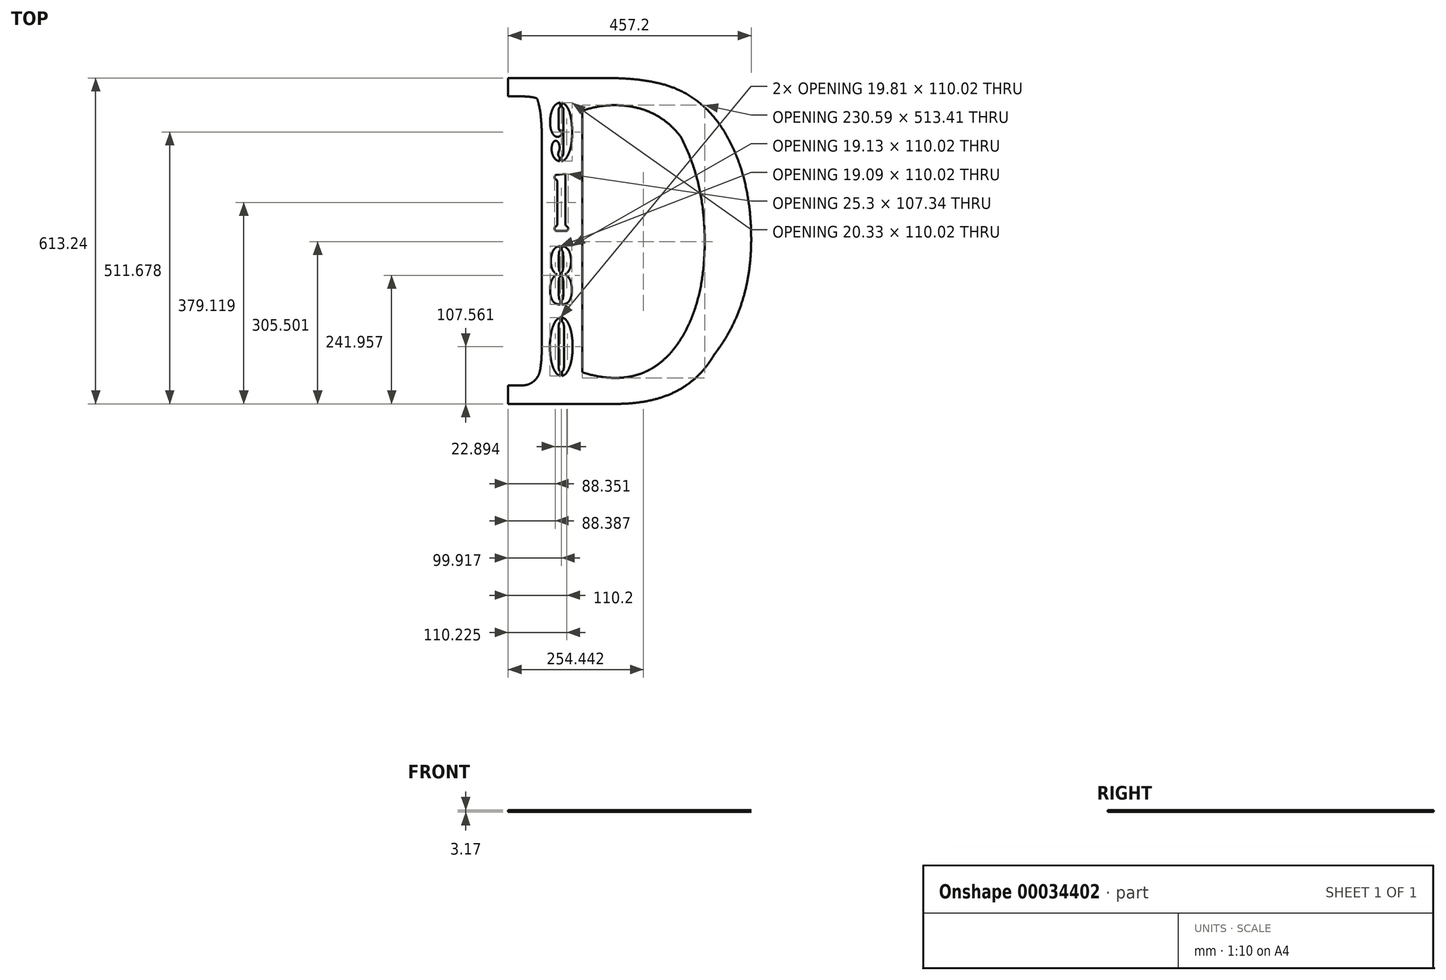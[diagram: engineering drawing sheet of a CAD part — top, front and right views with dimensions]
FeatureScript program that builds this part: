
annotation { "Feature Type Name" : "Feature", "Feature Type Description" : "" }
export const myFeature = defineFeature(function(context is Context, id is Id, definition is map)
    precondition{}
    {
        {
            var Q0;
            Q0=qCreatedBy(makeId("Top.planeOp"),FACE);
            var sketch = newSketch(context, id + "F0", { "sketchPlane" : qUnion([Q0])});
            skLineSegment(sketch, "E0", {"start": v(26.6, 0.36) * mm, "end": v(26.6, 0.12) * mm});
            skLineSegment(sketch, "E1", {"start": v(26.6, 0.12) * mm, "end": v(26.6, -0.1) * mm});
            skLineSegment(sketch, "E2", {"start": v(26.6, -0.1) * mm, "end": v(26.6, -0.34) * mm});
            skLineSegment(sketch, "E3", {"start": v(26.6, -0.34) * mm, "end": v(26.6, -0.57) * mm});
            skLineSegment(sketch, "E4", {"start": v(26.6, -0.57) * mm, "end": v(26.6, -0.8) * mm});
            skLineSegment(sketch, "E5", {"start": v(26.6, -0.8) * mm, "end": v(26.58, -1.03) * mm});
            skLineSegment(sketch, "E6", {"start": v(26.58, -1.03) * mm, "end": v(26.58, -1.26) * mm});
            skLineSegment(sketch, "E7", {"start": v(26.58, -1.26) * mm, "end": v(26.57, -1.49) * mm});
            skLineSegment(sketch, "E8", {"start": v(26.57, -1.49) * mm, "end": v(26.56, -1.72) * mm});
            skLineSegment(sketch, "E9", {"start": v(26.56, -1.72) * mm, "end": v(26.55, -1.94) * mm});
            skLineSegment(sketch, "E10", {"start": v(26.55, -1.94) * mm, "end": v(26.54, -2.17) * mm});
            skLineSegment(sketch, "E11", {"start": v(26.54, -2.17) * mm, "end": v(26.53, -2.4) * mm});
            skLineSegment(sketch, "E12", {"start": v(26.53, -2.4) * mm, "end": v(26.52, -2.62) * mm});
            skLineSegment(sketch, "E13", {"start": v(26.52, -2.62) * mm, "end": v(26.5, -2.85) * mm});
            skLineSegment(sketch, "E14", {"start": v(26.5, -2.85) * mm, "end": v(26.5, -3.07) * mm});
            skLineSegment(sketch, "E15", {"start": v(26.5, -3.07) * mm, "end": v(26.48, -3.3) * mm});
            skLineSegment(sketch, "E16", {"start": v(26.48, -3.3) * mm, "end": v(26.46, -3.52) * mm});
            skLineSegment(sketch, "E17", {"start": v(26.46, -3.52) * mm, "end": v(26.44, -3.74) * mm});
            skLineSegment(sketch, "E18", {"start": v(26.44, -3.74) * mm, "end": v(26.42, -3.97) * mm});
            skLineSegment(sketch, "E19", {"start": v(26.42, -3.97) * mm, "end": v(26.4, -4.19) * mm});
            skLineSegment(sketch, "E20", {"start": v(26.4, -4.19) * mm, "end": v(26.39, -4.4) * mm});
            skLineSegment(sketch, "E21", {"start": v(26.39, -4.4) * mm, "end": v(26.36, -4.63) * mm});
            skLineSegment(sketch, "E22", {"start": v(26.36, -4.63) * mm, "end": v(26.34, -4.85) * mm});
            skLineSegment(sketch, "E23", {"start": v(26.34, -4.85) * mm, "end": v(26.32, -5.07) * mm});
            skLineSegment(sketch, "E24", {"start": v(26.32, -5.07) * mm, "end": v(26.3, -5.29) * mm});
            skLineSegment(sketch, "E25", {"start": v(26.3, -5.29) * mm, "end": v(26.27, -5.5) * mm});
            skLineSegment(sketch, "E26", {"start": v(26.27, -5.5) * mm, "end": v(26.24, -5.73) * mm});
            skLineSegment(sketch, "E27", {"start": v(26.24, -5.73) * mm, "end": v(26.22, -5.94) * mm});
            skLineSegment(sketch, "E28", {"start": v(26.22, -5.94) * mm, "end": v(26.19, -6.16) * mm});
            skLineSegment(sketch, "E29", {"start": v(26.19, -6.16) * mm, "end": v(26.16, -6.38) * mm});
            skLineSegment(sketch, "E30", {"start": v(26.16, -6.38) * mm, "end": v(26.13, -6.6) * mm});
            skLineSegment(sketch, "E31", {"start": v(26.13, -6.6) * mm, "end": v(26.1, -6.8) * mm});
            skLineSegment(sketch, "E32", {"start": v(26.1, -6.8) * mm, "end": v(26.07, -7.02) * mm});
            skLineSegment(sketch, "E33", {"start": v(26.07, -7.02) * mm, "end": v(26.03, -7.24) * mm});
            skLineSegment(sketch, "E34", {"start": v(26.03, -7.24) * mm, "end": v(26, -7.45) * mm});
            skLineSegment(sketch, "E35", {"start": v(26, -7.45) * mm, "end": v(25.96, -7.66) * mm});
            skLineSegment(sketch, "E36", {"start": v(25.96, -7.66) * mm, "end": v(25.93, -7.88) * mm});
            skLineSegment(sketch, "E37", {"start": v(25.93, -7.88) * mm, "end": v(25.9, -8.09) * mm});
            skLineSegment(sketch, "E38", {"start": v(25.9, -8.09) * mm, "end": v(25.85, -8.3) * mm});
            skLineSegment(sketch, "E39", {"start": v(25.85, -8.3) * mm, "end": v(25.81, -8.5) * mm});
            skLineSegment(sketch, "E40", {"start": v(25.81, -8.5) * mm, "end": v(25.77, -8.72) * mm});
            skLineSegment(sketch, "E41", {"start": v(25.77, -8.72) * mm, "end": v(25.73, -8.93) * mm});
            skLineSegment(sketch, "E42", {"start": v(25.73, -8.93) * mm, "end": v(25.7, -9.14) * mm});
            skLineSegment(sketch, "E43", {"start": v(25.7, -9.14) * mm, "end": v(25.65, -9.35) * mm});
            skLineSegment(sketch, "E44", {"start": v(25.65, -9.35) * mm, "end": v(25.6, -9.55) * mm});
            skLineSegment(sketch, "E45", {"start": v(25.6, -9.55) * mm, "end": v(25.56, -9.76) * mm});
            skLineSegment(sketch, "E46", {"start": v(25.56, -9.76) * mm, "end": v(25.51, -9.97) * mm});
            skLineSegment(sketch, "E47", {"start": v(25.51, -9.97) * mm, "end": v(25.47, -10.17) * mm});
            skLineSegment(sketch, "E48", {"start": v(25.47, -10.17) * mm, "end": v(25.42, -10.38) * mm});
            skLineSegment(sketch, "E49", {"start": v(25.42, -10.38) * mm, "end": v(25.37, -10.59) * mm});
            skLineSegment(sketch, "E50", {"start": v(25.37, -10.59) * mm, "end": v(25.32, -10.79) * mm});
            skLineSegment(sketch, "E51", {"start": v(25.32, -10.79) * mm, "end": v(25.27, -11) * mm});
            skLineSegment(sketch, "E52", {"start": v(25.27, -11) * mm, "end": v(25.22, -11.2) * mm});
            skLineSegment(sketch, "E53", {"start": v(25.22, -11.2) * mm, "end": v(25.16, -11.4) * mm});
            skLineSegment(sketch, "E54", {"start": v(25.16, -11.4) * mm, "end": v(25.11, -11.6) * mm});
            skLineSegment(sketch, "E55", {"start": v(25.11, -11.6) * mm, "end": v(25.06, -11.8) * mm});
            skLineSegment(sketch, "E56", {"start": v(25.06, -11.8) * mm, "end": v(25, -12) * mm});
            skLineSegment(sketch, "E57", {"start": v(25, -12) * mm, "end": v(24.94, -12.2) * mm});
            skLineSegment(sketch, "E58", {"start": v(24.94, -12.2) * mm, "end": v(24.89, -12.4) * mm});
            skLineSegment(sketch, "E59", {"start": v(24.89, -12.4) * mm, "end": v(24.83, -12.6) * mm});
            skLineSegment(sketch, "E60", {"start": v(24.83, -12.6) * mm, "end": v(24.77, -12.8) * mm});
            skLineSegment(sketch, "E61", {"start": v(24.77, -12.8) * mm, "end": v(24.7, -13) * mm});
            skLineSegment(sketch, "E62", {"start": v(24.7, -13) * mm, "end": v(24.64, -13.2) * mm});
            skLineSegment(sketch, "E63", {"start": v(24.64, -13.2) * mm, "end": v(24.58, -13.4) * mm});
            skLineSegment(sketch, "E64", {"start": v(24.58, -13.4) * mm, "end": v(24.52, -13.6) * mm});
            skLineSegment(sketch, "E65", {"start": v(24.52, -13.6) * mm, "end": v(24.45, -13.8) * mm});
            skLineSegment(sketch, "E66", {"start": v(24.45, -13.8) * mm, "end": v(24.39, -13.99) * mm});
            skLineSegment(sketch, "E67", {"start": v(24.39, -13.99) * mm, "end": v(24.32, -14.18) * mm});
            skLineSegment(sketch, "E68", {"start": v(24.32, -14.18) * mm, "end": v(24.25, -14.38) * mm});
            skLineSegment(sketch, "E69", {"start": v(24.25, -14.38) * mm, "end": v(24.19, -14.57) * mm});
            skLineSegment(sketch, "E70", {"start": v(24.19, -14.57) * mm, "end": v(24.12, -14.76) * mm});
            skLineSegment(sketch, "E71", {"start": v(24.12, -14.76) * mm, "end": v(24.05, -14.95) * mm});
            skLineSegment(sketch, "E72", {"start": v(24.05, -14.95) * mm, "end": v(23.97, -15.15) * mm});
            skLineSegment(sketch, "E73", {"start": v(23.97, -15.15) * mm, "end": v(23.9, -15.34) * mm});
            skLineSegment(sketch, "E74", {"start": v(23.9, -15.34) * mm, "end": v(23.83, -15.53) * mm});
            skLineSegment(sketch, "E75", {"start": v(23.83, -15.53) * mm, "end": v(23.75, -15.72) * mm});
            skLineSegment(sketch, "E76", {"start": v(23.75, -15.72) * mm, "end": v(23.68, -15.91) * mm});
            skLineSegment(sketch, "E77", {"start": v(23.68, -15.91) * mm, "end": v(23.6, -16.1) * mm});
            skLineSegment(sketch, "E78", {"start": v(23.6, -16.1) * mm, "end": v(23.52, -16.29) * mm});
            skLineSegment(sketch, "E79", {"start": v(23.52, -16.29) * mm, "end": v(23.45, -16.48) * mm});
            skLineSegment(sketch, "E80", {"start": v(23.45, -16.48) * mm, "end": v(23.37, -16.66) * mm});
            skLineSegment(sketch, "E81", {"start": v(23.37, -16.66) * mm, "end": v(23.29, -16.85) * mm});
            skLineSegment(sketch, "E82", {"start": v(23.29, -16.85) * mm, "end": v(23.2, -17.04) * mm});
            skLineSegment(sketch, "E83", {"start": v(23.2, -17.04) * mm, "end": v(23.12, -17.22) * mm});
            skLineSegment(sketch, "E84", {"start": v(23.12, -17.22) * mm, "end": v(23.04, -17.4) * mm});
            skLineSegment(sketch, "E85", {"start": v(23.04, -17.4) * mm, "end": v(22.95, -17.6) * mm});
            skLineSegment(sketch, "E86", {"start": v(22.95, -17.6) * mm, "end": v(22.87, -17.78) * mm});
            skLineSegment(sketch, "E87", {"start": v(22.87, -17.78) * mm, "end": v(22.78, -17.96) * mm});
            skLineSegment(sketch, "E88", {"start": v(22.78, -17.96) * mm, "end": v(22.7, -18.15) * mm});
            skLineSegment(sketch, "E89", {"start": v(22.7, -18.15) * mm, "end": v(22.6, -18.33) * mm});
            skLineSegment(sketch, "E90", {"start": v(22.6, -18.33) * mm, "end": v(22.52, -18.5) * mm});
            skLineSegment(sketch, "E91", {"start": v(22.52, -18.5) * mm, "end": v(22.43, -18.7) * mm});
            skLineSegment(sketch, "E92", {"start": v(22.43, -18.7) * mm, "end": v(22.34, -18.87) * mm});
            skLineSegment(sketch, "E93", {"start": v(22.34, -18.87) * mm, "end": v(22.24, -19.05) * mm});
            skLineSegment(sketch, "E94", {"start": v(22.24, -19.05) * mm, "end": v(22.15, -19.23) * mm});
            skLineSegment(sketch, "E95", {"start": v(22.15, -19.23) * mm, "end": v(22.06, -19.41) * mm});
            skLineSegment(sketch, "E96", {"start": v(22.06, -19.41) * mm, "end": v(21.96, -19.6) * mm});
            skLineSegment(sketch, "E97", {"start": v(21.96, -19.6) * mm, "end": v(21.87, -19.77) * mm});
            skLineSegment(sketch, "E98", {"start": v(21.87, -19.77) * mm, "end": v(21.77, -19.95) * mm});
            skLineSegment(sketch, "E99", {"start": v(21.77, -19.95) * mm, "end": v(21.67, -20.12) * mm});
            skLineSegment(sketch, "E100", {"start": v(21.67, -20.12) * mm, "end": v(21.57, -20.3) * mm});
            skLineSegment(sketch, "E101", {"start": v(21.57, -20.3) * mm, "end": v(21.47, -20.48) * mm});
            skLineSegment(sketch, "E102", {"start": v(21.47, -20.48) * mm, "end": v(21.37, -20.65) * mm});
            skLineSegment(sketch, "E103", {"start": v(21.37, -20.65) * mm, "end": v(21.27, -20.83) * mm});
            skLineSegment(sketch, "E104", {"start": v(21.27, -20.83) * mm, "end": v(21.16, -21) * mm});
            skLineSegment(sketch, "E105", {"start": v(21.16, -21) * mm, "end": v(21.06, -21.17) * mm});
            skLineSegment(sketch, "E106", {"start": v(21.06, -21.17) * mm, "end": v(20.96, -21.35) * mm});
            skLineSegment(sketch, "E107", {"start": v(20.96, -21.35) * mm, "end": v(20.85, -21.52) * mm});
            skLineSegment(sketch, "E108", {"start": v(20.85, -21.52) * mm, "end": v(20.74, -21.7) * mm});
            skLineSegment(sketch, "E109", {"start": v(20.74, -21.7) * mm, "end": v(20.63, -21.86) * mm});
            skLineSegment(sketch, "E110", {"start": v(20.63, -21.86) * mm, "end": v(20.53, -22.03) * mm});
            skLineSegment(sketch, "E111", {"start": v(20.53, -22.03) * mm, "end": v(20.42, -22.2) * mm});
            skLineSegment(sketch, "E112", {"start": v(20.42, -22.2) * mm, "end": v(20.3, -22.37) * mm});
            skLineSegment(sketch, "E113", {"start": v(20.3, -22.37) * mm, "end": v(20.2, -22.54) * mm});
            skLineSegment(sketch, "E114", {"start": v(16.38, -27.97) * mm, "end": v(16.27, -28.11) * mm});
            skLineSegment(sketch, "E115", {"start": v(16.27, -28.11) * mm, "end": v(16.15, -28.25) * mm});
            skLineSegment(sketch, "E116", {"start": v(16.15, -28.25) * mm, "end": v(16.03, -28.4) * mm});
            skLineSegment(sketch, "E117", {"start": v(16.03, -28.4) * mm, "end": v(15.9, -28.53) * mm});
            skLineSegment(sketch, "E118", {"start": v(15.9, -28.53) * mm, "end": v(15.78, -28.67) * mm});
            skLineSegment(sketch, "E119", {"start": v(15.78, -28.67) * mm, "end": v(15.66, -28.8) * mm});
            skLineSegment(sketch, "E120", {"start": v(15.66, -28.8) * mm, "end": v(15.53, -28.94) * mm});
            skLineSegment(sketch, "E121", {"start": v(15.53, -28.94) * mm, "end": v(15.4, -29.07) * mm});
            skLineSegment(sketch, "E122", {"start": v(15.4, -29.07) * mm, "end": v(15.28, -29.2) * mm});
            skLineSegment(sketch, "E123", {"start": v(15.28, -29.2) * mm, "end": v(15.15, -29.33) * mm});
            skLineSegment(sketch, "E124", {"start": v(15.15, -29.33) * mm, "end": v(15.02, -29.46) * mm});
            skLineSegment(sketch, "E125", {"start": v(15.02, -29.46) * mm, "end": v(14.89, -29.59) * mm});
            skLineSegment(sketch, "E126", {"start": v(14.89, -29.59) * mm, "end": v(14.75, -29.71) * mm});
            skLineSegment(sketch, "E127", {"start": v(14.75, -29.71) * mm, "end": v(14.62, -29.84) * mm});
            skLineSegment(sketch, "E128", {"start": v(14.62, -29.84) * mm, "end": v(14.49, -29.96) * mm});
            skLineSegment(sketch, "E129", {"start": v(14.49, -29.96) * mm, "end": v(14.35, -30.09) * mm});
            skLineSegment(sketch, "E130", {"start": v(14.35, -30.09) * mm, "end": v(14.21, -30.2) * mm});
            skLineSegment(sketch, "E131", {"start": v(14.21, -30.2) * mm, "end": v(14.08, -30.33) * mm});
            skLineSegment(sketch, "E132", {"start": v(14.08, -30.33) * mm, "end": v(13.94, -30.44) * mm});
            skLineSegment(sketch, "E133", {"start": v(13.94, -30.44) * mm, "end": v(13.8, -30.56) * mm});
            skLineSegment(sketch, "E134", {"start": v(13.8, -30.56) * mm, "end": v(13.66, -30.68) * mm});
            skLineSegment(sketch, "E135", {"start": v(13.66, -30.68) * mm, "end": v(13.51, -30.8) * mm});
            skLineSegment(sketch, "E136", {"start": v(13.51, -30.8) * mm, "end": v(13.37, -30.9) * mm});
            skLineSegment(sketch, "E137", {"start": v(13.37, -30.9) * mm, "end": v(13.23, -31.02) * mm});
            skLineSegment(sketch, "E138", {"start": v(13.23, -31.02) * mm, "end": v(13.08, -31.13) * mm});
            skLineSegment(sketch, "E139", {"start": v(13.08, -31.13) * mm, "end": v(12.93, -31.24) * mm});
            skLineSegment(sketch, "E140", {"start": v(12.93, -31.24) * mm, "end": v(12.79, -31.34) * mm});
            skLineSegment(sketch, "E141", {"start": v(12.79, -31.34) * mm, "end": v(12.64, -31.45) * mm});
            skLineSegment(sketch, "E142", {"start": v(12.64, -31.45) * mm, "end": v(12.49, -31.56) * mm});
            skLineSegment(sketch, "E143", {"start": v(12.49, -31.56) * mm, "end": v(12.34, -31.66) * mm});
            skLineSegment(sketch, "E144", {"start": v(12.34, -31.66) * mm, "end": v(12.18, -31.76) * mm});
            skLineSegment(sketch, "E145", {"start": v(12.18, -31.76) * mm, "end": v(12.03, -31.86) * mm});
            skLineSegment(sketch, "E146", {"start": v(12.03, -31.86) * mm, "end": v(11.87, -31.96) * mm});
            skLineSegment(sketch, "E147", {"start": v(11.87, -31.96) * mm, "end": v(11.72, -32.06) * mm});
            skLineSegment(sketch, "E148", {"start": v(11.72, -32.06) * mm, "end": v(11.56, -32.16) * mm});
            skLineSegment(sketch, "E149", {"start": v(11.56, -32.16) * mm, "end": v(11.4, -32.25) * mm});
            skLineSegment(sketch, "E150", {"start": v(11.4, -32.25) * mm, "end": v(11.24, -32.35) * mm});
            skLineSegment(sketch, "E151", {"start": v(11.24, -32.35) * mm, "end": v(11.08, -32.44) * mm});
            skLineSegment(sketch, "E152", {"start": v(11.08, -32.44) * mm, "end": v(10.92, -32.53) * mm});
            skLineSegment(sketch, "E153", {"start": v(10.92, -32.53) * mm, "end": v(10.76, -32.62) * mm});
            skLineSegment(sketch, "E154", {"start": v(10.76, -32.62) * mm, "end": v(10.6, -32.71) * mm});
            skLineSegment(sketch, "E155", {"start": v(10.6, -32.71) * mm, "end": v(10.43, -32.8) * mm});
            skLineSegment(sketch, "E156", {"start": v(10.43, -32.8) * mm, "end": v(10.27, -32.89) * mm});
            skLineSegment(sketch, "E157", {"start": v(10.27, -32.89) * mm, "end": v(10.1, -32.97) * mm});
            skLineSegment(sketch, "E158", {"start": v(10.1, -32.97) * mm, "end": v(9.93, -33.06) * mm});
            skLineSegment(sketch, "E159", {"start": v(9.93, -33.06) * mm, "end": v(9.76, -33.14) * mm});
            skLineSegment(sketch, "E160", {"start": v(9.76, -33.14) * mm, "end": v(9.6, -33.22) * mm});
            skLineSegment(sketch, "E161", {"start": v(9.6, -33.22) * mm, "end": v(9.42, -33.3) * mm});
            skLineSegment(sketch, "E162", {"start": v(9.42, -33.3) * mm, "end": v(9.25, -33.38) * mm});
            skLineSegment(sketch, "E163", {"start": v(9.25, -33.38) * mm, "end": v(9.07, -33.46) * mm});
            skLineSegment(sketch, "E164", {"start": v(9.07, -33.46) * mm, "end": v(8.9, -33.53) * mm});
            skLineSegment(sketch, "E165", {"start": v(8.9, -33.53) * mm, "end": v(8.72, -33.6) * mm});
            skLineSegment(sketch, "E166", {"start": v(8.72, -33.6) * mm, "end": v(8.55, -33.68) * mm});
            skLineSegment(sketch, "E167", {"start": v(8.55, -33.68) * mm, "end": v(8.37, -33.75) * mm});
            skLineSegment(sketch, "E168", {"start": v(8.37, -33.75) * mm, "end": v(8.19, -33.82) * mm});
            skLineSegment(sketch, "E169", {"start": v(8.19, -33.82) * mm, "end": v(8, -33.9) * mm});
            skLineSegment(sketch, "E170", {"start": v(8, -33.9) * mm, "end": v(7.83, -33.96) * mm});
            skLineSegment(sketch, "E171", {"start": v(7.83, -33.96) * mm, "end": v(7.64, -34.03) * mm});
            skLineSegment(sketch, "E172", {"start": v(7.64, -34.03) * mm, "end": v(7.46, -34.1) * mm});
            skLineSegment(sketch, "E173", {"start": v(7.46, -34.1) * mm, "end": v(7.27, -34.16) * mm});
            skLineSegment(sketch, "E174", {"start": v(7.27, -34.16) * mm, "end": v(7.09, -34.22) * mm});
            skLineSegment(sketch, "E175", {"start": v(7.09, -34.22) * mm, "end": v(6.9, -34.28) * mm});
            skLineSegment(sketch, "E176", {"start": v(6.9, -34.28) * mm, "end": v(6.71, -34.34) * mm});
            skLineSegment(sketch, "E177", {"start": v(6.71, -34.34) * mm, "end": v(6.52, -34.4) * mm});
            skLineSegment(sketch, "E178", {"start": v(6.52, -34.4) * mm, "end": v(6.33, -34.46) * mm});
            skLineSegment(sketch, "E179", {"start": v(6.33, -34.46) * mm, "end": v(6.14, -34.52) * mm});
            skLineSegment(sketch, "E180", {"start": v(6.14, -34.52) * mm, "end": v(5.95, -34.57) * mm});
            skLineSegment(sketch, "E181", {"start": v(5.95, -34.57) * mm, "end": v(5.75, -34.62) * mm});
            skLineSegment(sketch, "E182", {"start": v(5.75, -34.62) * mm, "end": v(5.56, -34.68) * mm});
            skLineSegment(sketch, "E183", {"start": v(5.56, -34.68) * mm, "end": v(5.36, -34.73) * mm});
            skLineSegment(sketch, "E184", {"start": v(5.36, -34.73) * mm, "end": v(5.16, -34.78) * mm});
            skLineSegment(sketch, "E185", {"start": v(5.16, -34.78) * mm, "end": v(4.97, -34.82) * mm});
            skLineSegment(sketch, "E186", {"start": v(4.97, -34.82) * mm, "end": v(4.77, -34.87) * mm});
            skLineSegment(sketch, "E187", {"start": v(4.77, -34.87) * mm, "end": v(4.57, -34.92) * mm});
            skLineSegment(sketch, "E188", {"start": v(4.57, -34.92) * mm, "end": v(4.36, -34.96) * mm});
            skLineSegment(sketch, "E189", {"start": v(4.36, -34.96) * mm, "end": v(4.16, -35) * mm});
            skLineSegment(sketch, "E190", {"start": v(4.16, -35) * mm, "end": v(3.96, -35.05) * mm});
            skLineSegment(sketch, "E191", {"start": v(3.96, -35.05) * mm, "end": v(3.75, -35.09) * mm});
            skLineSegment(sketch, "E192", {"start": v(3.75, -35.09) * mm, "end": v(3.54, -35.13) * mm});
            skLineSegment(sketch, "E193", {"start": v(3.54, -35.13) * mm, "end": v(3.34, -35.16) * mm});
            skLineSegment(sketch, "E194", {"start": v(3.34, -35.16) * mm, "end": v(3.13, -35.2) * mm});
            skLineSegment(sketch, "E195", {"start": v(3.13, -35.2) * mm, "end": v(2.92, -35.23) * mm});
            skLineSegment(sketch, "E196", {"start": v(2.92, -35.23) * mm, "end": v(2.7, -35.27) * mm});
            skLineSegment(sketch, "E197", {"start": v(2.7, -35.27) * mm, "end": v(2.5, -35.3) * mm});
            skLineSegment(sketch, "E198", {"start": v(2.5, -35.3) * mm, "end": v(2.28, -35.33) * mm});
            skLineSegment(sketch, "E199", {"start": v(2.28, -35.33) * mm, "end": v(2.07, -35.36) * mm});
            skLineSegment(sketch, "E200", {"start": v(2.07, -35.36) * mm, "end": v(1.85, -35.39) * mm});
            skLineSegment(sketch, "E201", {"start": v(1.85, -35.39) * mm, "end": v(1.64, -35.42) * mm});
            skLineSegment(sketch, "E202", {"start": v(1.64, -35.42) * mm, "end": v(1.42, -35.44) * mm});
            skLineSegment(sketch, "E203", {"start": v(1.42, -35.44) * mm, "end": v(1.2, -35.47) * mm});
            skLineSegment(sketch, "E204", {"start": v(1.2, -35.47) * mm, "end": v(0.98, -35.5) * mm});
            skLineSegment(sketch, "E205", {"start": v(0.98, -35.5) * mm, "end": v(0.76, -35.51) * mm});
            skLineSegment(sketch, "E206", {"start": v(0.76, -35.51) * mm, "end": v(0.54, -35.53) * mm});
            skLineSegment(sketch, "E207", {"start": v(0.54, -35.53) * mm, "end": v(0.31, -35.55) * mm});
            skLineSegment(sketch, "E208", {"start": v(0.31, -35.55) * mm, "end": v(0.09, -35.57) * mm});
            skLineSegment(sketch, "E209", {"start": v(0.09, -35.57) * mm, "end": v(-0.14, -35.59) * mm});
            skLineSegment(sketch, "E210", {"start": v(-0.14, -35.59) * mm, "end": v(-0.36, -35.6) * mm});
            skLineSegment(sketch, "E211", {"start": v(-0.36, -35.6) * mm, "end": v(-0.6, -35.62) * mm});
            skLineSegment(sketch, "E212", {"start": v(-0.6, -35.62) * mm, "end": v(-0.82, -35.63) * mm});
            skLineSegment(sketch, "E213", {"start": v(-0.82, -35.63) * mm, "end": v(-1.05, -35.64) * mm});
            skLineSegment(sketch, "E214", {"start": v(-1.05, -35.64) * mm, "end": v(-1.28, -35.65) * mm});
            skLineSegment(sketch, "E215", {"start": v(-1.28, -35.65) * mm, "end": v(-1.51, -35.66) * mm});
            skLineSegment(sketch, "E216", {"start": v(-1.51, -35.66) * mm, "end": v(-1.75, -35.66) * mm});
            skLineSegment(sketch, "E217", {"start": v(-1.75, -35.66) * mm, "end": v(-1.98, -35.67) * mm});
            skLineSegment(sketch, "E218", {"start": v(-1.98, -35.67) * mm, "end": v(-2.22, -35.68) * mm});
            skLineSegment(sketch, "E219", {"start": v(-2.22, -35.68) * mm, "end": v(-2.45, -35.68) * mm});
            skLineSegment(sketch, "E220", {"start": v(-2.45, -35.68) * mm, "end": v(-2.7, -35.68) * mm});
            skLineSegment(sketch, "E221", {"start": v(-2.7, -35.68) * mm, "end": v(-2.93, -35.68) * mm});
            skLineSegment(sketch, "E222", {"start": v(-2.93, -35.68) * mm, "end": v(-26.6, -35.68) * mm});
            skLineSegment(sketch, "E223", {"start": v(-26.6, -35.68) * mm, "end": v(-26.6, -31.67) * mm});
            skLineSegment(sketch, "E224", {"start": v(-26.6, -31.67) * mm, "end": v(-23.9, -31.67) * mm});
            skLineSegment(sketch, "E225", {"start": v(-23.9, -31.67) * mm, "end": v(-23.82, -31.67) * mm});
            skLineSegment(sketch, "E226", {"start": v(-23.82, -31.67) * mm, "end": v(-23.73, -31.67) * mm});
            skLineSegment(sketch, "E227", {"start": v(-23.73, -31.67) * mm, "end": v(-23.64, -31.67) * mm});
            skLineSegment(sketch, "E228", {"start": v(-23.64, -31.67) * mm, "end": v(-23.56, -31.66) * mm});
            skLineSegment(sketch, "E229", {"start": v(-23.56, -31.66) * mm, "end": v(-23.47, -31.66) * mm});
            skLineSegment(sketch, "E230", {"start": v(-23.47, -31.66) * mm, "end": v(-23.4, -31.65) * mm});
            skLineSegment(sketch, "E231", {"start": v(-23.4, -31.65) * mm, "end": v(-23.3, -31.64) * mm});
            skLineSegment(sketch, "E232", {"start": v(-23.3, -31.64) * mm, "end": v(-23.23, -31.63) * mm});
            skLineSegment(sketch, "E233", {"start": v(-23.23, -31.63) * mm, "end": v(-23.14, -31.62) * mm});
            skLineSegment(sketch, "E234", {"start": v(-23.14, -31.62) * mm, "end": v(-23.06, -31.61) * mm});
            skLineSegment(sketch, "E235", {"start": v(-23.06, -31.61) * mm, "end": v(-22.98, -31.6) * mm});
            skLineSegment(sketch, "E236", {"start": v(-22.98, -31.6) * mm, "end": v(-22.9, -31.59) * mm});
            skLineSegment(sketch, "E237", {"start": v(-22.9, -31.59) * mm, "end": v(-22.83, -31.57) * mm});
            skLineSegment(sketch, "E238", {"start": v(-22.83, -31.57) * mm, "end": v(-22.75, -31.56) * mm});
            skLineSegment(sketch, "E239", {"start": v(-22.75, -31.56) * mm, "end": v(-22.67, -31.54) * mm});
            skLineSegment(sketch, "E240", {"start": v(-22.67, -31.54) * mm, "end": v(-22.6, -31.52) * mm});
            skLineSegment(sketch, "E241", {"start": v(-22.6, -31.52) * mm, "end": v(-22.52, -31.5) * mm});
            skLineSegment(sketch, "E242", {"start": v(-22.52, -31.5) * mm, "end": v(-22.45, -31.49) * mm});
            skLineSegment(sketch, "E243", {"start": v(-22.45, -31.49) * mm, "end": v(-22.38, -31.46) * mm});
            skLineSegment(sketch, "E244", {"start": v(-22.38, -31.46) * mm, "end": v(-22.3, -31.44) * mm});
            skLineSegment(sketch, "E245", {"start": v(-22.3, -31.44) * mm, "end": v(-22.23, -31.42) * mm});
            skLineSegment(sketch, "E246", {"start": v(-22.23, -31.42) * mm, "end": v(-22.16, -31.4) * mm});
            skLineSegment(sketch, "E247", {"start": v(-22.16, -31.4) * mm, "end": v(-22.1, -31.37) * mm});
            skLineSegment(sketch, "E248", {"start": v(-22.1, -31.37) * mm, "end": v(-22.02, -31.34) * mm});
            skLineSegment(sketch, "E249", {"start": v(-22.02, -31.34) * mm, "end": v(-21.96, -31.31) * mm});
            skLineSegment(sketch, "E250", {"start": v(-21.96, -31.31) * mm, "end": v(-21.89, -31.29) * mm});
            skLineSegment(sketch, "E251", {"start": v(-21.89, -31.29) * mm, "end": v(-21.82, -31.25) * mm});
            skLineSegment(sketch, "E252", {"start": v(-21.82, -31.25) * mm, "end": v(-21.76, -31.22) * mm});
            skLineSegment(sketch, "E253", {"start": v(-21.76, -31.22) * mm, "end": v(-21.7, -31.2) * mm});
            skLineSegment(sketch, "E254", {"start": v(-21.7, -31.2) * mm, "end": v(-21.63, -31.16) * mm});
            skLineSegment(sketch, "E255", {"start": v(-21.63, -31.16) * mm, "end": v(-21.57, -31.12) * mm});
            skLineSegment(sketch, "E256", {"start": v(-21.57, -31.12) * mm, "end": v(-21.5, -31.09) * mm});
            skLineSegment(sketch, "E257", {"start": v(-21.5, -31.09) * mm, "end": v(-21.44, -31.05) * mm});
            skLineSegment(sketch, "E258", {"start": v(-21.44, -31.05) * mm, "end": v(-21.38, -31.01) * mm});
            skLineSegment(sketch, "E259", {"start": v(-21.38, -31.01) * mm, "end": v(-21.32, -30.97) * mm});
            skLineSegment(sketch, "E260", {"start": v(-21.32, -30.97) * mm, "end": v(-21.26, -30.93) * mm});
            skLineSegment(sketch, "E261", {"start": v(-21.26, -30.93) * mm, "end": v(-21.2, -30.89) * mm});
            skLineSegment(sketch, "E262", {"start": v(-21.2, -30.89) * mm, "end": v(-21.15, -30.85) * mm});
            skLineSegment(sketch, "E263", {"start": v(-21.15, -30.85) * mm, "end": v(-21.1, -30.8) * mm});
            skLineSegment(sketch, "E264", {"start": v(-21.1, -30.8) * mm, "end": v(-21.04, -30.76) * mm});
            skLineSegment(sketch, "E265", {"start": v(-21.04, -30.76) * mm, "end": v(-20.98, -30.71) * mm});
            skLineSegment(sketch, "E266", {"start": v(-20.98, -30.71) * mm, "end": v(-20.93, -30.66) * mm});
            skLineSegment(sketch, "E267", {"start": v(-20.93, -30.66) * mm, "end": v(-20.87, -30.62) * mm});
            skLineSegment(sketch, "E268", {"start": v(-20.87, -30.62) * mm, "end": v(-20.82, -30.57) * mm});
            skLineSegment(sketch, "E269", {"start": v(-20.82, -30.57) * mm, "end": v(-20.77, -30.52) * mm});
            skLineSegment(sketch, "E270", {"start": v(-20.77, -30.52) * mm, "end": v(-20.72, -30.46) * mm});
            skLineSegment(sketch, "E271", {"start": v(-20.72, -30.46) * mm, "end": v(-20.67, -30.41) * mm});
            skLineSegment(sketch, "E272", {"start": v(-20.67, -30.41) * mm, "end": v(-20.62, -30.36) * mm});
            skLineSegment(sketch, "E273", {"start": v(-20.62, -30.36) * mm, "end": v(-20.57, -30.3) * mm});
            skLineSegment(sketch, "E274", {"start": v(-20.57, -30.3) * mm, "end": v(-20.52, -30.25) * mm});
            skLineSegment(sketch, "E275", {"start": v(-20.52, -30.25) * mm, "end": v(-20.48, -30.19) * mm});
            skLineSegment(sketch, "E276", {"start": v(-20.48, -30.19) * mm, "end": v(-20.43, -30.13) * mm});
            skLineSegment(sketch, "E277", {"start": v(-20.43, -30.13) * mm, "end": v(-20.39, -30.07) * mm});
            skLineSegment(sketch, "E278", {"start": v(-20.39, -30.07) * mm, "end": v(-20.34, -30) * mm});
            skLineSegment(sketch, "E279", {"start": v(-20.34, -30) * mm, "end": v(-20.3, -29.95) * mm});
            skLineSegment(sketch, "E280", {"start": v(-20.3, -29.95) * mm, "end": v(-20.26, -29.88) * mm});
            skLineSegment(sketch, "E281", {"start": v(-20.26, -29.88) * mm, "end": v(-20.22, -29.82) * mm});
            skLineSegment(sketch, "E282", {"start": v(-20.22, -29.82) * mm, "end": v(-20.18, -29.75) * mm});
            skLineSegment(sketch, "E283", {"start": v(-20.18, -29.75) * mm, "end": v(-20.14, -29.69) * mm});
            skLineSegment(sketch, "E284", {"start": v(-20.14, -29.69) * mm, "end": v(-20.1, -29.62) * mm});
            skLineSegment(sketch, "E285", {"start": v(-20.1, -29.62) * mm, "end": v(-20.06, -29.55) * mm});
            skLineSegment(sketch, "E286", {"start": v(-20.06, -29.55) * mm, "end": v(-20.02, -29.48) * mm});
            skLineSegment(sketch, "E287", {"start": v(-20.02, -29.48) * mm, "end": v(-19.98, -29.4) * mm});
            skLineSegment(sketch, "E288", {"start": v(-19.98, -29.4) * mm, "end": v(-19.95, -29.34) * mm});
            skLineSegment(sketch, "E289", {"start": v(-19.95, -29.34) * mm, "end": v(-19.93, -29.29) * mm});
            skLineSegment(sketch, "E290", {"start": v(-19.93, -29.29) * mm, "end": v(-19.9, -29.24) * mm});
            skLineSegment(sketch, "E291", {"start": v(-19.9, -29.24) * mm, "end": v(-19.88, -29.2) * mm});
            skLineSegment(sketch, "E292", {"start": v(-19.88, -29.2) * mm, "end": v(-19.86, -29.14) * mm});
            skLineSegment(sketch, "E293", {"start": v(-19.86, -29.14) * mm, "end": v(-19.84, -29.09) * mm});
            skLineSegment(sketch, "E294", {"start": v(-19.84, -29.09) * mm, "end": v(-19.82, -29.03) * mm});
            skLineSegment(sketch, "E295", {"start": v(-19.82, -29.03) * mm, "end": v(-19.8, -28.97) * mm});
            skLineSegment(sketch, "E296", {"start": v(-19.8, -28.97) * mm, "end": v(-19.78, -28.91) * mm});
            skLineSegment(sketch, "E297", {"start": v(-19.78, -28.91) * mm, "end": v(-19.76, -28.85) * mm});
            skLineSegment(sketch, "E298", {"start": v(-19.76, -28.85) * mm, "end": v(-19.74, -28.79) * mm});
            skLineSegment(sketch, "E299", {"start": v(-19.74, -28.79) * mm, "end": v(-19.7, -28.65) * mm});
            skLineSegment(sketch, "E300", {"start": v(-19.7, -28.65) * mm, "end": v(-19.67, -28.5) * mm});
            skLineSegment(sketch, "E301", {"start": v(-19.67, -28.5) * mm, "end": v(-19.64, -28.36) * mm});
            skLineSegment(sketch, "E302", {"start": v(-19.64, -28.36) * mm, "end": v(-19.6, -28.2) * mm});
            skLineSegment(sketch, "E303", {"start": v(-19.6, -28.2) * mm, "end": v(-19.57, -28.03) * mm});
            skLineSegment(sketch, "E304", {"start": v(-19.57, -28.03) * mm, "end": v(-19.54, -27.86) * mm});
            skLineSegment(sketch, "E305", {"start": v(-19.54, -27.86) * mm, "end": v(-19.52, -27.68) * mm});
            skLineSegment(sketch, "E306", {"start": v(-19.52, -27.68) * mm, "end": v(-19.49, -27.49) * mm});
            skLineSegment(sketch, "E307", {"start": v(-19.49, -27.49) * mm, "end": v(-19.46, -27.29) * mm});
            skLineSegment(sketch, "E308", {"start": v(-19.46, -27.29) * mm, "end": v(-19.44, -27.08) * mm});
            skLineSegment(sketch, "E309", {"start": v(-19.44, -27.08) * mm, "end": v(-19.42, -26.87) * mm});
            skLineSegment(sketch, "E310", {"start": v(-19.42, -26.87) * mm, "end": v(-19.4, -26.65) * mm});
            skLineSegment(sketch, "E311", {"start": v(-19.4, -26.65) * mm, "end": v(-19.37, -26.42) * mm});
            skLineSegment(sketch, "E312", {"start": v(-19.37, -26.42) * mm, "end": v(-19.36, -26.18) * mm});
            skLineSegment(sketch, "E313", {"start": v(-19.36, -26.18) * mm, "end": v(-19.34, -25.93) * mm});
            skLineSegment(sketch, "E314", {"start": v(-19.34, -25.93) * mm, "end": v(-19.32, -25.68) * mm});
            skLineSegment(sketch, "E315", {"start": v(-19.32, -25.68) * mm, "end": v(-19.3, -25.42) * mm});
            skLineSegment(sketch, "E316", {"start": v(-19.3, -25.42) * mm, "end": v(-19.3, -25.15) * mm});
            skLineSegment(sketch, "E317", {"start": v(-19.3, -25.15) * mm, "end": v(-19.28, -24.87) * mm});
            skLineSegment(sketch, "E318", {"start": v(-19.28, -24.87) * mm, "end": v(-19.27, -24.58) * mm});
            skLineSegment(sketch, "E319", {"start": v(-19.27, -24.58) * mm, "end": v(-19.26, -24.29) * mm});
            skLineSegment(sketch, "E320", {"start": v(-19.26, -24.29) * mm, "end": v(-19.26, -23.98) * mm});
            skLineSegment(sketch, "E321", {"start": v(-19.26, -23.98) * mm, "end": v(-19.25, -23.67) * mm});
            skLineSegment(sketch, "E322", {"start": v(-19.25, -23.67) * mm, "end": v(-19.24, -23.36) * mm});
            skLineSegment(sketch, "E323", {"start": v(-19.24, -23.36) * mm, "end": v(-19.24, -23.03) * mm});
            skLineSegment(sketch, "E324", {"start": v(-19.24, -23.03) * mm, "end": v(-19.24, -22.7) * mm});
            skLineSegment(sketch, "E325", {"start": v(-19.24, -22.7) * mm, "end": v(-19.24, -22.35) * mm});
            skLineSegment(sketch, "E326", {"start": v(-19.24, -22.35) * mm, "end": v(-19.24, 22.35) * mm});
            skLineSegment(sketch, "E327", {"start": v(-19.24, 22.35) * mm, "end": v(-19.24, 22.73) * mm});
            skLineSegment(sketch, "E328", {"start": v(-19.24, 22.73) * mm, "end": v(-19.24, 23.1) * mm});
            skLineSegment(sketch, "E329", {"start": v(-19.24, 23.1) * mm, "end": v(-19.25, 23.46) * mm});
            skLineSegment(sketch, "E330", {"start": v(-19.25, 23.46) * mm, "end": v(-19.26, 23.82) * mm});
            skLineSegment(sketch, "E331", {"start": v(-19.26, 23.82) * mm, "end": v(-19.26, 24.17) * mm});
            skLineSegment(sketch, "E332", {"start": v(-19.26, 24.17) * mm, "end": v(-19.28, 24.51) * mm});
            skLineSegment(sketch, "E333", {"start": v(-19.28, 24.51) * mm, "end": v(-19.29, 24.85) * mm});
            skLineSegment(sketch, "E334", {"start": v(-19.29, 24.85) * mm, "end": v(-19.3, 25.18) * mm});
            skLineSegment(sketch, "E335", {"start": v(-19.3, 25.18) * mm, "end": v(-19.32, 25.5) * mm});
            skLineSegment(sketch, "E336", {"start": v(-19.32, 25.5) * mm, "end": v(-19.34, 25.82) * mm});
            skLineSegment(sketch, "E337", {"start": v(-19.34, 25.82) * mm, "end": v(-19.36, 26.13) * mm});
            skLineSegment(sketch, "E338", {"start": v(-19.36, 26.13) * mm, "end": v(-19.39, 26.44) * mm});
            skLineSegment(sketch, "E339", {"start": v(-19.39, 26.44) * mm, "end": v(-19.41, 26.74) * mm});
            skLineSegment(sketch, "E340", {"start": v(-19.41, 26.74) * mm, "end": v(-19.44, 27.03) * mm});
            skLineSegment(sketch, "E341", {"start": v(-19.44, 27.03) * mm, "end": v(-19.47, 27.32) * mm});
            skLineSegment(sketch, "E342", {"start": v(-19.47, 27.32) * mm, "end": v(-19.5, 27.6) * mm});
            skLineSegment(sketch, "E343", {"start": v(-19.5, 27.6) * mm, "end": v(-19.54, 27.87) * mm});
            skLineSegment(sketch, "E344", {"start": v(-19.54, 27.87) * mm, "end": v(-19.57, 28.14) * mm});
            skLineSegment(sketch, "E345", {"start": v(-19.57, 28.14) * mm, "end": v(-19.61, 28.4) * mm});
            skLineSegment(sketch, "E346", {"start": v(-19.61, 28.4) * mm, "end": v(-19.65, 28.66) * mm});
            skLineSegment(sketch, "E347", {"start": v(-19.65, 28.66) * mm, "end": v(-19.7, 28.9) * mm});
            skLineSegment(sketch, "E348", {"start": v(-19.7, 28.9) * mm, "end": v(-19.74, 29.15) * mm});
            skLineSegment(sketch, "E349", {"start": v(-19.74, 29.15) * mm, "end": v(-19.78, 29.38) * mm});
            skLineSegment(sketch, "E350", {"start": v(-19.78, 29.38) * mm, "end": v(-19.83, 29.61) * mm});
            skLineSegment(sketch, "E351", {"start": v(-19.83, 29.61) * mm, "end": v(-19.88, 29.83) * mm});
            skLineSegment(sketch, "E352", {"start": v(-19.88, 29.83) * mm, "end": v(-19.94, 30.05) * mm});
            skLineSegment(sketch, "E353", {"start": v(-19.94, 30.05) * mm, "end": v(-19.96, 30.16) * mm});
            skLineSegment(sketch, "E354", {"start": v(-19.96, 30.16) * mm, "end": v(-20, 30.26) * mm});
            skLineSegment(sketch, "E355", {"start": v(-20, 30.26) * mm, "end": v(-20.02, 30.36) * mm});
            skLineSegment(sketch, "E356", {"start": v(-20.02, 30.36) * mm, "end": v(-20.05, 30.46) * mm});
            skLineSegment(sketch, "E357", {"start": v(-20.05, 30.46) * mm, "end": v(-20.08, 30.56) * mm});
            skLineSegment(sketch, "E358", {"start": v(-20.08, 30.56) * mm, "end": v(-20.1, 30.66) * mm});
            skLineSegment(sketch, "E359", {"start": v(-20.1, 30.66) * mm, "end": v(-20.14, 30.76) * mm});
            skLineSegment(sketch, "E360", {"start": v(-20.14, 30.76) * mm, "end": v(-20.17, 30.85) * mm});
            skLineSegment(sketch, "E361", {"start": v(-20.17, 30.85) * mm, "end": v(-20.2, 30.95) * mm});
            skLineSegment(sketch, "E362", {"start": v(-20.2, 30.95) * mm, "end": v(-20.23, 31.04) * mm});
            skLineSegment(sketch, "E363", {"start": v(-20.23, 31.04) * mm, "end": v(-20.26, 31.13) * mm});
            skLineSegment(sketch, "E364", {"start": v(-20.26, 31.13) * mm, "end": v(-20.3, 31.22) * mm});
            skLineSegment(sketch, "E365", {"start": v(-20.3, 31.22) * mm, "end": v(-20.36, 31.24) * mm});
            skLineSegment(sketch, "E366", {"start": v(-20.36, 31.24) * mm, "end": v(-20.43, 31.27) * mm});
            skLineSegment(sketch, "E367", {"start": v(-20.43, 31.27) * mm, "end": v(-20.5, 31.3) * mm});
            skLineSegment(sketch, "E368", {"start": v(-20.5, 31.3) * mm, "end": v(-20.58, 31.32) * mm});
            skLineSegment(sketch, "E369", {"start": v(-20.58, 31.32) * mm, "end": v(-20.66, 31.35) * mm});
            skLineSegment(sketch, "E370", {"start": v(-20.66, 31.35) * mm, "end": v(-20.74, 31.37) * mm});
            skLineSegment(sketch, "E371", {"start": v(-20.74, 31.37) * mm, "end": v(-20.83, 31.4) * mm});
            skLineSegment(sketch, "E372", {"start": v(-20.83, 31.4) * mm, "end": v(-20.92, 31.41) * mm});
            skLineSegment(sketch, "E373", {"start": v(-20.92, 31.41) * mm, "end": v(-21, 31.44) * mm});
            skLineSegment(sketch, "E374", {"start": v(-21, 31.44) * mm, "end": v(-21.1, 31.46) * mm});
            skLineSegment(sketch, "E375", {"start": v(-21.1, 31.46) * mm, "end": v(-21.2, 31.47) * mm});
            skLineSegment(sketch, "E376", {"start": v(-21.2, 31.47) * mm, "end": v(-21.3, 31.5) * mm});
            skLineSegment(sketch, "E377", {"start": v(-21.3, 31.5) * mm, "end": v(-21.4, 31.51) * mm});
            skLineSegment(sketch, "E378", {"start": v(-21.4, 31.51) * mm, "end": v(-21.5, 31.53) * mm});
            skLineSegment(sketch, "E379", {"start": v(-21.5, 31.53) * mm, "end": v(-21.61, 31.54) * mm});
            skLineSegment(sketch, "E380", {"start": v(-21.61, 31.54) * mm, "end": v(-21.73, 31.56) * mm});
            skLineSegment(sketch, "E381", {"start": v(-21.73, 31.56) * mm, "end": v(-21.84, 31.57) * mm});
            skLineSegment(sketch, "E382", {"start": v(-21.84, 31.57) * mm, "end": v(-21.96, 31.58) * mm});
            skLineSegment(sketch, "E383", {"start": v(-21.96, 31.58) * mm, "end": v(-22.08, 31.6) * mm});
            skLineSegment(sketch, "E384", {"start": v(-22.08, 31.6) * mm, "end": v(-22.2, 31.6) * mm});
            skLineSegment(sketch, "E385", {"start": v(-22.2, 31.6) * mm, "end": v(-22.33, 31.62) * mm});
            skLineSegment(sketch, "E386", {"start": v(-22.33, 31.62) * mm, "end": v(-22.46, 31.63) * mm});
            skLineSegment(sketch, "E387", {"start": v(-22.46, 31.63) * mm, "end": v(-22.59, 31.63) * mm});
            skLineSegment(sketch, "E388", {"start": v(-22.59, 31.63) * mm, "end": v(-22.72, 31.64) * mm});
            skLineSegment(sketch, "E389", {"start": v(-22.72, 31.64) * mm, "end": v(-22.86, 31.65) * mm});
            skLineSegment(sketch, "E390", {"start": v(-22.86, 31.65) * mm, "end": v(-23, 31.65) * mm});
            skLineSegment(sketch, "E391", {"start": v(-23, 31.65) * mm, "end": v(-23.14, 31.66) * mm});
            skLineSegment(sketch, "E392", {"start": v(-23.14, 31.66) * mm, "end": v(-23.3, 31.66) * mm});
            skLineSegment(sketch, "E393", {"start": v(-23.3, 31.66) * mm, "end": v(-23.44, 31.67) * mm});
            skLineSegment(sketch, "E394", {"start": v(-23.44, 31.67) * mm, "end": v(-23.6, 31.67) * mm});
            skLineSegment(sketch, "E395", {"start": v(-23.6, 31.67) * mm, "end": v(-23.75, 31.67) * mm});
            skLineSegment(sketch, "E396", {"start": v(-23.75, 31.67) * mm, "end": v(-23.9, 31.67) * mm});
            skLineSegment(sketch, "E397", {"start": v(-23.9, 31.67) * mm, "end": v(-26.6, 31.67) * mm});
            skLineSegment(sketch, "E398", {"start": v(-26.6, 31.67) * mm, "end": v(-26.6, 35.68) * mm});
            skLineSegment(sketch, "E399", {"start": v(-26.6, 35.68) * mm, "end": v(-4.97, 35.68) * mm});
            skLineSegment(sketch, "E400", {"start": v(-4.97, 35.68) * mm, "end": v(-4.66, 35.68) * mm});
            skLineSegment(sketch, "E401", {"start": v(-4.66, 35.68) * mm, "end": v(-4.35, 35.68) * mm});
            skLineSegment(sketch, "E402", {"start": v(-4.35, 35.68) * mm, "end": v(-4.04, 35.68) * mm});
            skLineSegment(sketch, "E403", {"start": v(-4.04, 35.68) * mm, "end": v(-3.74, 35.67) * mm});
            skLineSegment(sketch, "E404", {"start": v(-3.74, 35.67) * mm, "end": v(-3.43, 35.67) * mm});
            skLineSegment(sketch, "E405", {"start": v(-3.43, 35.67) * mm, "end": v(-3.13, 35.66) * mm});
            skLineSegment(sketch, "E406", {"start": v(-3.13, 35.66) * mm, "end": v(-2.83, 35.65) * mm});
            skLineSegment(sketch, "E407", {"start": v(-2.83, 35.65) * mm, "end": v(-2.54, 35.64) * mm});
            skLineSegment(sketch, "E408", {"start": v(-2.54, 35.64) * mm, "end": v(-2.24, 35.63) * mm});
            skLineSegment(sketch, "E409", {"start": v(-2.24, 35.63) * mm, "end": v(-1.95, 35.62) * mm});
            skLineSegment(sketch, "E410", {"start": v(-1.95, 35.62) * mm, "end": v(-1.66, 35.6) * mm});
            skLineSegment(sketch, "E411", {"start": v(-1.66, 35.6) * mm, "end": v(-1.37, 35.6) * mm});
            skLineSegment(sketch, "E412", {"start": v(-1.37, 35.6) * mm, "end": v(-1.08, 35.58) * mm});
            skLineSegment(sketch, "E413", {"start": v(-1.08, 35.58) * mm, "end": v(-0.8, 35.56) * mm});
            skLineSegment(sketch, "E414", {"start": v(-0.8, 35.56) * mm, "end": v(-0.52, 35.54) * mm});
            skLineSegment(sketch, "E415", {"start": v(-0.52, 35.54) * mm, "end": v(-0.24, 35.52) * mm});
            skLineSegment(sketch, "E416", {"start": v(-0.24, 35.52) * mm, "end": v(0.04, 35.5) * mm});
            skLineSegment(sketch, "E417", {"start": v(0.04, 35.5) * mm, "end": v(0.31, 35.48) * mm});
            skLineSegment(sketch, "E418", {"start": v(0.31, 35.48) * mm, "end": v(0.59, 35.45) * mm});
            skLineSegment(sketch, "E419", {"start": v(0.59, 35.45) * mm, "end": v(0.86, 35.43) * mm});
            skLineSegment(sketch, "E420", {"start": v(0.86, 35.43) * mm, "end": v(1.13, 35.4) * mm});
            skLineSegment(sketch, "E421", {"start": v(1.13, 35.4) * mm, "end": v(1.4, 35.38) * mm});
            skLineSegment(sketch, "E422", {"start": v(1.4, 35.38) * mm, "end": v(1.66, 35.35) * mm});
            skLineSegment(sketch, "E423", {"start": v(1.66, 35.35) * mm, "end": v(1.92, 35.32) * mm});
            skLineSegment(sketch, "E424", {"start": v(1.92, 35.32) * mm, "end": v(2.18, 35.29) * mm});
            skLineSegment(sketch, "E425", {"start": v(2.18, 35.29) * mm, "end": v(2.44, 35.26) * mm});
            skLineSegment(sketch, "E426", {"start": v(2.44, 35.26) * mm, "end": v(2.7, 35.22) * mm});
            skLineSegment(sketch, "E427", {"start": v(2.7, 35.22) * mm, "end": v(2.95, 35.19) * mm});
            skLineSegment(sketch, "E428", {"start": v(2.95, 35.19) * mm, "end": v(3.2, 35.15) * mm});
            skLineSegment(sketch, "E429", {"start": v(3.2, 35.15) * mm, "end": v(3.45, 35.12) * mm});
            skLineSegment(sketch, "E430", {"start": v(3.45, 35.12) * mm, "end": v(3.7, 35.08) * mm});
            skLineSegment(sketch, "E431", {"start": v(3.7, 35.08) * mm, "end": v(3.94, 35.04) * mm});
            skLineSegment(sketch, "E432", {"start": v(3.94, 35.04) * mm, "end": v(4.19, 35) * mm});
            skLineSegment(sketch, "E433", {"start": v(4.19, 35) * mm, "end": v(4.43, 34.96) * mm});
            skLineSegment(sketch, "E434", {"start": v(4.43, 34.96) * mm, "end": v(4.67, 34.91) * mm});
            skLineSegment(sketch, "E435", {"start": v(4.67, 34.91) * mm, "end": v(4.9, 34.87) * mm});
            skLineSegment(sketch, "E436", {"start": v(4.9, 34.87) * mm, "end": v(5.14, 34.82) * mm});
            skLineSegment(sketch, "E437", {"start": v(5.14, 34.82) * mm, "end": v(5.37, 34.78) * mm});
            skLineSegment(sketch, "E438", {"start": v(5.37, 34.78) * mm, "end": v(5.6, 34.73) * mm});
            skLineSegment(sketch, "E439", {"start": v(5.6, 34.73) * mm, "end": v(5.83, 34.68) * mm});
            skLineSegment(sketch, "E440", {"start": v(5.83, 34.68) * mm, "end": v(6.06, 34.63) * mm});
            skLineSegment(sketch, "E441", {"start": v(6.06, 34.63) * mm, "end": v(6.28, 34.58) * mm});
            skLineSegment(sketch, "E442", {"start": v(6.28, 34.58) * mm, "end": v(6.5, 34.52) * mm});
            skLineSegment(sketch, "E443", {"start": v(6.5, 34.52) * mm, "end": v(6.72, 34.47) * mm});
            skLineSegment(sketch, "E444", {"start": v(6.72, 34.47) * mm, "end": v(6.94, 34.41) * mm});
            skLineSegment(sketch, "E445", {"start": v(6.94, 34.41) * mm, "end": v(7.15, 34.35) * mm});
            skLineSegment(sketch, "E446", {"start": v(7.15, 34.35) * mm, "end": v(7.37, 34.3) * mm});
            skLineSegment(sketch, "E447", {"start": v(7.37, 34.3) * mm, "end": v(7.58, 34.24) * mm});
            skLineSegment(sketch, "E448", {"start": v(7.58, 34.24) * mm, "end": v(7.79, 34.18) * mm});
            skLineSegment(sketch, "E449", {"start": v(7.79, 34.18) * mm, "end": v(8, 34.11) * mm});
            skLineSegment(sketch, "E450", {"start": v(8, 34.11) * mm, "end": v(8.2, 34.05) * mm});
            skLineSegment(sketch, "E451", {"start": v(8.2, 34.05) * mm, "end": v(8.4, 33.99) * mm});
            skLineSegment(sketch, "E452", {"start": v(8.4, 33.99) * mm, "end": v(8.6, 33.92) * mm});
            skLineSegment(sketch, "E453", {"start": v(8.6, 33.92) * mm, "end": v(8.8, 33.85) * mm});
            skLineSegment(sketch, "E454", {"start": v(8.8, 33.85) * mm, "end": v(9, 33.78) * mm});
            skLineSegment(sketch, "E455", {"start": v(9, 33.78) * mm, "end": v(9.2, 33.71) * mm});
            skLineSegment(sketch, "E456", {"start": v(9.2, 33.71) * mm, "end": v(9.38, 33.64) * mm});
            skLineSegment(sketch, "E457", {"start": v(9.38, 33.64) * mm, "end": v(9.57, 33.57) * mm});
            skLineSegment(sketch, "E458", {"start": v(9.57, 33.57) * mm, "end": v(9.76, 33.5) * mm});
            skLineSegment(sketch, "E459", {"start": v(9.76, 33.5) * mm, "end": v(9.94, 33.42) * mm});
            skLineSegment(sketch, "E460", {"start": v(9.94, 33.42) * mm, "end": v(10.13, 33.35) * mm});
            skLineSegment(sketch, "E461", {"start": v(10.13, 33.35) * mm, "end": v(10.3, 33.27) * mm});
            skLineSegment(sketch, "E462", {"start": v(10.3, 33.27) * mm, "end": v(10.49, 33.2) * mm});
            skLineSegment(sketch, "E463", {"start": v(10.49, 33.2) * mm, "end": v(10.66, 33.11) * mm});
            skLineSegment(sketch, "E464", {"start": v(10.66, 33.11) * mm, "end": v(10.9, 33) * mm});
            skLineSegment(sketch, "E465", {"start": v(10.9, 33) * mm, "end": v(11.15, 32.88) * mm});
            skLineSegment(sketch, "E466", {"start": v(11.15, 32.88) * mm, "end": v(11.4, 32.77) * mm});
            skLineSegment(sketch, "E467", {"start": v(11.4, 32.77) * mm, "end": v(11.64, 32.64) * mm});
            skLineSegment(sketch, "E468", {"start": v(11.64, 32.64) * mm, "end": v(11.87, 32.52) * mm});
            skLineSegment(sketch, "E469", {"start": v(11.87, 32.52) * mm, "end": v(12.11, 32.4) * mm});
            skLineSegment(sketch, "E470", {"start": v(12.11, 32.4) * mm, "end": v(12.35, 32.26) * mm});
            skLineSegment(sketch, "E471", {"start": v(12.35, 32.26) * mm, "end": v(12.58, 32.13) * mm});
            skLineSegment(sketch, "E472", {"start": v(12.58, 32.13) * mm, "end": v(12.81, 32) * mm});
            skLineSegment(sketch, "E473", {"start": v(12.81, 32) * mm, "end": v(13.04, 31.85) * mm});
            skLineSegment(sketch, "E474", {"start": v(13.04, 31.85) * mm, "end": v(13.27, 31.71) * mm});
            skLineSegment(sketch, "E475", {"start": v(13.27, 31.71) * mm, "end": v(13.5, 31.57) * mm});
            skLineSegment(sketch, "E476", {"start": v(13.5, 31.57) * mm, "end": v(13.72, 31.42) * mm});
            skLineSegment(sketch, "E477", {"start": v(13.72, 31.42) * mm, "end": v(13.94, 31.27) * mm});
            skLineSegment(sketch, "E478", {"start": v(13.94, 31.27) * mm, "end": v(14.16, 31.11) * mm});
            skLineSegment(sketch, "E479", {"start": v(14.16, 31.11) * mm, "end": v(14.38, 30.95) * mm});
            skLineSegment(sketch, "E480", {"start": v(14.38, 30.95) * mm, "end": v(14.6, 30.8) * mm});
            skLineSegment(sketch, "E481", {"start": v(14.6, 30.8) * mm, "end": v(14.81, 30.63) * mm});
            skLineSegment(sketch, "E482", {"start": v(14.81, 30.63) * mm, "end": v(15.03, 30.46) * mm});
            skLineSegment(sketch, "E483", {"start": v(15.03, 30.46) * mm, "end": v(15.24, 30.3) * mm});
            skLineSegment(sketch, "E484", {"start": v(15.24, 30.3) * mm, "end": v(15.45, 30.12) * mm});
            skLineSegment(sketch, "E485", {"start": v(15.45, 30.12) * mm, "end": v(15.66, 29.95) * mm});
            skLineSegment(sketch, "E486", {"start": v(15.66, 29.95) * mm, "end": v(15.87, 29.77) * mm});
            skLineSegment(sketch, "E487", {"start": v(15.87, 29.77) * mm, "end": v(16.07, 29.59) * mm});
            skLineSegment(sketch, "E488", {"start": v(16.07, 29.59) * mm, "end": v(16.28, 29.4) * mm});
            skLineSegment(sketch, "E489", {"start": v(16.28, 29.4) * mm, "end": v(16.48, 29.22) * mm});
            skLineSegment(sketch, "E490", {"start": v(16.48, 29.22) * mm, "end": v(16.68, 29.03) * mm});
            skLineSegment(sketch, "E491", {"start": v(16.68, 29.03) * mm, "end": v(16.88, 28.83) * mm});
            skLineSegment(sketch, "E492", {"start": v(16.88, 28.83) * mm, "end": v(17.07, 28.64) * mm});
            skLineSegment(sketch, "E493", {"start": v(17.07, 28.64) * mm, "end": v(17.27, 28.44) * mm});
            skLineSegment(sketch, "E494", {"start": v(17.27, 28.44) * mm, "end": v(17.46, 28.24) * mm});
            skLineSegment(sketch, "E495", {"start": v(17.46, 28.24) * mm, "end": v(17.65, 28.03) * mm});
            skLineSegment(sketch, "E496", {"start": v(17.65, 28.03) * mm, "end": v(17.84, 27.82) * mm});
            skLineSegment(sketch, "E497", {"start": v(17.84, 27.82) * mm, "end": v(18.03, 27.61) * mm});
            skLineSegment(sketch, "E498", {"start": v(18.03, 27.61) * mm, "end": v(18.21, 27.4) * mm});
            skLineSegment(sketch, "E499", {"start": v(18.21, 27.4) * mm, "end": v(18.4, 27.18) * mm});
            skLineSegment(sketch, "E500", {"start": v(18.4, 27.18) * mm, "end": v(18.58, 26.96) * mm});
            skLineSegment(sketch, "E501", {"start": v(18.58, 26.96) * mm, "end": v(18.76, 26.74) * mm});
            skLineSegment(sketch, "E502", {"start": v(18.76, 26.74) * mm, "end": v(18.94, 26.5) * mm});
            skLineSegment(sketch, "E503", {"start": v(18.94, 26.5) * mm, "end": v(19.12, 26.28) * mm});
            skLineSegment(sketch, "E504", {"start": v(19.12, 26.28) * mm, "end": v(19.3, 26.05) * mm});
            skLineSegment(sketch, "E505", {"start": v(19.3, 26.05) * mm, "end": v(19.47, 25.81) * mm});
            skLineSegment(sketch, "E506", {"start": v(19.47, 25.81) * mm, "end": v(19.64, 25.58) * mm});
            skLineSegment(sketch, "E507", {"start": v(19.64, 25.58) * mm, "end": v(19.8, 25.33) * mm});
            skLineSegment(sketch, "E508", {"start": v(19.8, 25.33) * mm, "end": v(19.98, 25.1) * mm});
            skLineSegment(sketch, "E509", {"start": v(19.98, 25.1) * mm, "end": v(20.14, 24.84) * mm});
            skLineSegment(sketch, "E510", {"start": v(20.14, 24.84) * mm, "end": v(20.3, 24.6) * mm});
            skLineSegment(sketch, "E511", {"start": v(20.3, 24.6) * mm, "end": v(20.47, 24.34) * mm});
            skLineSegment(sketch, "E512", {"start": v(20.47, 24.34) * mm, "end": v(20.63, 24.08) * mm});
            skLineSegment(sketch, "E513", {"start": v(20.63, 24.08) * mm, "end": v(20.8, 23.83) * mm});
            skLineSegment(sketch, "E514", {"start": v(20.8, 23.83) * mm, "end": v(20.95, 23.56) * mm});
            skLineSegment(sketch, "E515", {"start": v(20.95, 23.56) * mm, "end": v(21.1, 23.3) * mm});
            skLineSegment(sketch, "E516", {"start": v(21.1, 23.3) * mm, "end": v(21.26, 23.03) * mm});
            skLineSegment(sketch, "E517", {"start": v(21.26, 23.03) * mm, "end": v(21.42, 22.76) * mm});
            skLineSegment(sketch, "E518", {"start": v(21.42, 22.76) * mm, "end": v(21.57, 22.48) * mm});
            skLineSegment(sketch, "E519", {"start": v(21.57, 22.48) * mm, "end": v(21.72, 22.2) * mm});
            skLineSegment(sketch, "E520", {"start": v(21.72, 22.2) * mm, "end": v(21.86, 21.93) * mm});
            skLineSegment(sketch, "E521", {"start": v(21.86, 21.93) * mm, "end": v(22, 21.65) * mm});
            skLineSegment(sketch, "E522", {"start": v(22, 21.65) * mm, "end": v(22.15, 21.36) * mm});
            skLineSegment(sketch, "E523", {"start": v(22.15, 21.36) * mm, "end": v(22.3, 21.07) * mm});
            skLineSegment(sketch, "E524", {"start": v(22.3, 21.07) * mm, "end": v(22.44, 20.78) * mm});
            skLineSegment(sketch, "E525", {"start": v(22.44, 20.78) * mm, "end": v(22.58, 20.48) * mm});
            skLineSegment(sketch, "E526", {"start": v(22.58, 20.48) * mm, "end": v(22.71, 20.19) * mm});
            skLineSegment(sketch, "E527", {"start": v(22.71, 20.19) * mm, "end": v(22.85, 19.88) * mm});
            skLineSegment(sketch, "E528", {"start": v(22.85, 19.88) * mm, "end": v(22.96, 19.62) * mm});
            skLineSegment(sketch, "E529", {"start": v(22.96, 19.62) * mm, "end": v(23.08, 19.35) * mm});
            skLineSegment(sketch, "E530", {"start": v(23.08, 19.35) * mm, "end": v(23.2, 19.08) * mm});
            skLineSegment(sketch, "E531", {"start": v(23.2, 19.08) * mm, "end": v(23.3, 18.81) * mm});
            skLineSegment(sketch, "E532", {"start": v(23.3, 18.81) * mm, "end": v(23.41, 18.54) * mm});
            skLineSegment(sketch, "E533", {"start": v(23.41, 18.54) * mm, "end": v(23.52, 18.27) * mm});
            skLineSegment(sketch, "E534", {"start": v(23.52, 18.27) * mm, "end": v(23.62, 18) * mm});
            skLineSegment(sketch, "E535", {"start": v(23.62, 18) * mm, "end": v(23.73, 17.72) * mm});
            skLineSegment(sketch, "E536", {"start": v(23.73, 17.72) * mm, "end": v(23.83, 17.44) * mm});
            skLineSegment(sketch, "E537", {"start": v(23.83, 17.44) * mm, "end": v(23.93, 17.16) * mm});
            skLineSegment(sketch, "E538", {"start": v(23.93, 17.16) * mm, "end": v(24.03, 16.88) * mm});
            skLineSegment(sketch, "E539", {"start": v(24.03, 16.88) * mm, "end": v(24.12, 16.6) * mm});
            skLineSegment(sketch, "E540", {"start": v(24.12, 16.6) * mm, "end": v(24.22, 16.32) * mm});
            skLineSegment(sketch, "E541", {"start": v(24.22, 16.32) * mm, "end": v(24.31, 16.04) * mm});
            skLineSegment(sketch, "E542", {"start": v(24.31, 16.04) * mm, "end": v(24.4, 15.76) * mm});
            skLineSegment(sketch, "E543", {"start": v(24.4, 15.76) * mm, "end": v(24.5, 15.47) * mm});
            skLineSegment(sketch, "E544", {"start": v(24.5, 15.47) * mm, "end": v(24.58, 15.19) * mm});
            skLineSegment(sketch, "E545", {"start": v(24.58, 15.19) * mm, "end": v(24.66, 14.9) * mm});
            skLineSegment(sketch, "E546", {"start": v(24.66, 14.9) * mm, "end": v(24.75, 14.6) * mm});
            skLineSegment(sketch, "E547", {"start": v(24.75, 14.6) * mm, "end": v(24.83, 14.32) * mm});
            skLineSegment(sketch, "E548", {"start": v(24.83, 14.32) * mm, "end": v(24.9, 14.03) * mm});
            skLineSegment(sketch, "E549", {"start": v(24.9, 14.03) * mm, "end": v(24.99, 13.74) * mm});
            skLineSegment(sketch, "E550", {"start": v(24.99, 13.74) * mm, "end": v(25.06, 13.44) * mm});
            skLineSegment(sketch, "E551", {"start": v(25.06, 13.44) * mm, "end": v(25.14, 13.15) * mm});
            skLineSegment(sketch, "E552", {"start": v(25.14, 13.15) * mm, "end": v(25.2, 12.85) * mm});
            skLineSegment(sketch, "E553", {"start": v(25.2, 12.85) * mm, "end": v(25.28, 12.55) * mm});
            skLineSegment(sketch, "E554", {"start": v(25.28, 12.55) * mm, "end": v(25.35, 12.26) * mm});
            skLineSegment(sketch, "E555", {"start": v(25.35, 12.26) * mm, "end": v(25.41, 11.96) * mm});
            skLineSegment(sketch, "E556", {"start": v(25.41, 11.96) * mm, "end": v(25.48, 11.66) * mm});
            skLineSegment(sketch, "E557", {"start": v(25.48, 11.66) * mm, "end": v(25.54, 11.35) * mm});
            skLineSegment(sketch, "E558", {"start": v(25.54, 11.35) * mm, "end": v(25.6, 11.05) * mm});
            skLineSegment(sketch, "E559", {"start": v(25.6, 11.05) * mm, "end": v(25.66, 10.75) * mm});
            skLineSegment(sketch, "E560", {"start": v(25.66, 10.75) * mm, "end": v(25.72, 10.44) * mm});
            skLineSegment(sketch, "E561", {"start": v(25.72, 10.44) * mm, "end": v(25.78, 10.13) * mm});
            skLineSegment(sketch, "E562", {"start": v(25.78, 10.13) * mm, "end": v(25.83, 9.83) * mm});
            skLineSegment(sketch, "E563", {"start": v(25.83, 9.83) * mm, "end": v(25.88, 9.52) * mm});
            skLineSegment(sketch, "E564", {"start": v(25.88, 9.52) * mm, "end": v(25.93, 9.2) * mm});
            skLineSegment(sketch, "E565", {"start": v(25.93, 9.2) * mm, "end": v(25.98, 8.9) * mm});
            skLineSegment(sketch, "E566", {"start": v(25.98, 8.9) * mm, "end": v(26.03, 8.58) * mm});
            skLineSegment(sketch, "E567", {"start": v(26.03, 8.58) * mm, "end": v(26.07, 8.27) * mm});
            skLineSegment(sketch, "E568", {"start": v(26.07, 8.27) * mm, "end": v(26.12, 7.95) * mm});
            skLineSegment(sketch, "E569", {"start": v(26.12, 7.95) * mm, "end": v(26.16, 7.63) * mm});
            skLineSegment(sketch, "E570", {"start": v(26.16, 7.63) * mm, "end": v(26.2, 7.32) * mm});
            skLineSegment(sketch, "E571", {"start": v(26.2, 7.32) * mm, "end": v(26.24, 7) * mm});
            skLineSegment(sketch, "E572", {"start": v(26.24, 7) * mm, "end": v(26.27, 6.68) * mm});
            skLineSegment(sketch, "E573", {"start": v(26.27, 6.68) * mm, "end": v(26.3, 6.35) * mm});
            skLineSegment(sketch, "E574", {"start": v(26.3, 6.35) * mm, "end": v(26.34, 6.03) * mm});
            skLineSegment(sketch, "E575", {"start": v(26.34, 6.03) * mm, "end": v(26.37, 5.7) * mm});
            skLineSegment(sketch, "E576", {"start": v(26.37, 5.7) * mm, "end": v(26.4, 5.38) * mm});
            skLineSegment(sketch, "E577", {"start": v(26.4, 5.38) * mm, "end": v(26.42, 5.06) * mm});
            skLineSegment(sketch, "E578", {"start": v(26.42, 5.06) * mm, "end": v(26.45, 4.73) * mm});
            skLineSegment(sketch, "E579", {"start": v(26.45, 4.73) * mm, "end": v(26.47, 4.4) * mm});
            skLineSegment(sketch, "E580", {"start": v(26.47, 4.4) * mm, "end": v(26.5, 4.07) * mm});
            skLineSegment(sketch, "E581", {"start": v(26.5, 4.07) * mm, "end": v(26.51, 3.74) * mm});
            skLineSegment(sketch, "E582", {"start": v(26.51, 3.74) * mm, "end": v(26.53, 3.4) * mm});
            skLineSegment(sketch, "E583", {"start": v(26.53, 3.4) * mm, "end": v(26.54, 3.07) * mm});
            skLineSegment(sketch, "E584", {"start": v(26.54, 3.07) * mm, "end": v(26.56, 2.74) * mm});
            skLineSegment(sketch, "E585", {"start": v(26.56, 2.74) * mm, "end": v(26.57, 2.4) * mm});
            skLineSegment(sketch, "E586", {"start": v(26.57, 2.4) * mm, "end": v(26.58, 2.06) * mm});
            skLineSegment(sketch, "E587", {"start": v(26.58, 2.06) * mm, "end": v(26.59, 1.72) * mm});
            skLineSegment(sketch, "E588", {"start": v(26.59, 1.72) * mm, "end": v(26.6, 1.38) * mm});
            skLineSegment(sketch, "E589", {"start": v(26.6, 1.38) * mm, "end": v(26.6, 1.04) * mm});
            skLineSegment(sketch, "E590", {"start": v(26.6, 1.04) * mm, "end": v(26.6, 0.7) * mm});
            skLineSegment(sketch, "E591", {"start": v(26.6, 0.7) * mm, "end": v(26.6, 0.36) * mm});
            skLineSegment(sketch, "E592", {"start": v(16.42, -0.13) * mm, "end": v(16.42, 0.28) * mm});
            skLineSegment(sketch, "E593", {"start": v(16.42, 0.28) * mm, "end": v(16.42, 0.68) * mm});
            skLineSegment(sketch, "E594", {"start": v(16.42, 0.68) * mm, "end": v(16.41, 1.08) * mm});
            skLineSegment(sketch, "E595", {"start": v(16.41, 1.08) * mm, "end": v(16.4, 1.49) * mm});
            skLineSegment(sketch, "E596", {"start": v(16.4, 1.49) * mm, "end": v(16.4, 1.89) * mm});
            skLineSegment(sketch, "E597", {"start": v(16.4, 1.89) * mm, "end": v(16.38, 2.29) * mm});
            skLineSegment(sketch, "E598", {"start": v(16.38, 2.29) * mm, "end": v(16.36, 2.68) * mm});
            skLineSegment(sketch, "E599", {"start": v(16.36, 2.68) * mm, "end": v(16.34, 3.08) * mm});
            skLineSegment(sketch, "E600", {"start": v(16.34, 3.08) * mm, "end": v(16.32, 3.47) * mm});
            skLineSegment(sketch, "E601", {"start": v(16.32, 3.47) * mm, "end": v(16.3, 3.87) * mm});
            skLineSegment(sketch, "E602", {"start": v(16.3, 3.87) * mm, "end": v(16.27, 4.26) * mm});
            skLineSegment(sketch, "E603", {"start": v(16.27, 4.26) * mm, "end": v(16.24, 4.65) * mm});
            skLineSegment(sketch, "E604", {"start": v(16.24, 4.65) * mm, "end": v(16.2, 5.03) * mm});
            skLineSegment(sketch, "E605", {"start": v(16.2, 5.03) * mm, "end": v(16.17, 5.42) * mm});
            skLineSegment(sketch, "E606", {"start": v(16.17, 5.42) * mm, "end": v(16.14, 5.8) * mm});
            skLineSegment(sketch, "E607", {"start": v(16.14, 5.8) * mm, "end": v(16.1, 6.2) * mm});
            skLineSegment(sketch, "E608", {"start": v(16.1, 6.2) * mm, "end": v(16.05, 6.57) * mm});
            skLineSegment(sketch, "E609", {"start": v(16.05, 6.57) * mm, "end": v(16, 6.95) * mm});
            skLineSegment(sketch, "E610", {"start": v(16, 6.95) * mm, "end": v(15.96, 7.33) * mm});
            skLineSegment(sketch, "E611", {"start": v(15.96, 7.33) * mm, "end": v(15.91, 7.7) * mm});
            skLineSegment(sketch, "E612", {"start": v(15.91, 7.7) * mm, "end": v(15.86, 8.09) * mm});
            skLineSegment(sketch, "E613", {"start": v(15.86, 8.09) * mm, "end": v(15.8, 8.46) * mm});
            skLineSegment(sketch, "E614", {"start": v(15.8, 8.46) * mm, "end": v(15.74, 8.83) * mm});
            skLineSegment(sketch, "E615", {"start": v(15.74, 8.83) * mm, "end": v(15.68, 9.2) * mm});
            skLineSegment(sketch, "E616", {"start": v(15.68, 9.2) * mm, "end": v(15.62, 9.58) * mm});
            skLineSegment(sketch, "E617", {"start": v(15.62, 9.58) * mm, "end": v(15.56, 9.94) * mm});
            skLineSegment(sketch, "E618", {"start": v(15.56, 9.94) * mm, "end": v(15.49, 10.31) * mm});
            skLineSegment(sketch, "E619", {"start": v(15.49, 10.31) * mm, "end": v(15.42, 10.68) * mm});
            skLineSegment(sketch, "E620", {"start": v(15.42, 10.68) * mm, "end": v(15.34, 11.04) * mm});
            skLineSegment(sketch, "E621", {"start": v(15.34, 11.04) * mm, "end": v(15.27, 11.4) * mm});
            skLineSegment(sketch, "E622", {"start": v(15.27, 11.4) * mm, "end": v(15.2, 11.76) * mm});
            skLineSegment(sketch, "E623", {"start": v(15.2, 11.76) * mm, "end": v(15.1, 12.12) * mm});
            skLineSegment(sketch, "E624", {"start": v(15.1, 12.12) * mm, "end": v(15.03, 12.48) * mm});
            skLineSegment(sketch, "E625", {"start": v(15.03, 12.48) * mm, "end": v(14.94, 12.84) * mm});
            skLineSegment(sketch, "E626", {"start": v(14.94, 12.84) * mm, "end": v(14.85, 13.2) * mm});
            skLineSegment(sketch, "E627", {"start": v(14.85, 13.2) * mm, "end": v(14.76, 13.55) * mm});
            skLineSegment(sketch, "E628", {"start": v(14.76, 13.55) * mm, "end": v(14.67, 13.9) * mm});
            skLineSegment(sketch, "E629", {"start": v(14.67, 13.9) * mm, "end": v(14.57, 14.25) * mm});
            skLineSegment(sketch, "E630", {"start": v(14.57, 14.25) * mm, "end": v(14.47, 14.6) * mm});
            skLineSegment(sketch, "E631", {"start": v(14.47, 14.6) * mm, "end": v(14.37, 14.95) * mm});
            skLineSegment(sketch, "E632", {"start": v(14.37, 14.95) * mm, "end": v(14.27, 15.3) * mm});
            skLineSegment(sketch, "E633", {"start": v(14.27, 15.3) * mm, "end": v(14.16, 15.64) * mm});
            skLineSegment(sketch, "E634", {"start": v(14.16, 15.64) * mm, "end": v(14.05, 15.98) * mm});
            skLineSegment(sketch, "E635", {"start": v(14.05, 15.98) * mm, "end": v(13.94, 16.32) * mm});
            skLineSegment(sketch, "E636", {"start": v(13.94, 16.32) * mm, "end": v(13.82, 16.66) * mm});
            skLineSegment(sketch, "E637", {"start": v(13.82, 16.66) * mm, "end": v(13.7, 17) * mm});
            skLineSegment(sketch, "E638", {"start": v(13.7, 17) * mm, "end": v(13.59, 17.34) * mm});
            skLineSegment(sketch, "E639", {"start": v(13.59, 17.34) * mm, "end": v(13.47, 17.67) * mm});
            skLineSegment(sketch, "E640", {"start": v(13.47, 17.67) * mm, "end": v(13.34, 18) * mm});
            skLineSegment(sketch, "E641", {"start": v(13.34, 18) * mm, "end": v(13.21, 18.34) * mm});
            skLineSegment(sketch, "E642", {"start": v(13.21, 18.34) * mm, "end": v(13.08, 18.67) * mm});
            skLineSegment(sketch, "E643", {"start": v(13.08, 18.67) * mm, "end": v(12.95, 19) * mm});
            skLineSegment(sketch, "E644", {"start": v(12.95, 19) * mm, "end": v(12.82, 19.33) * mm});
            skLineSegment(sketch, "E645", {"start": v(12.82, 19.33) * mm, "end": v(12.68, 19.65) * mm});
            skLineSegment(sketch, "E646", {"start": v(12.68, 19.65) * mm, "end": v(12.54, 19.98) * mm});
            skLineSegment(sketch, "E647", {"start": v(12.54, 19.98) * mm, "end": v(12.4, 20.3) * mm});
            skLineSegment(sketch, "E648", {"start": v(12.4, 20.3) * mm, "end": v(12.25, 20.62) * mm});
            skLineSegment(sketch, "E649", {"start": v(12.25, 20.62) * mm, "end": v(12.1, 20.94) * mm});
            skLineSegment(sketch, "E650", {"start": v(12.1, 20.94) * mm, "end": v(11.95, 21.26) * mm});
            skLineSegment(sketch, "E651", {"start": v(11.95, 21.26) * mm, "end": v(11.8, 21.58) * mm});
            skLineSegment(sketch, "E652", {"start": v(11.8, 21.58) * mm, "end": v(11.65, 21.9) * mm});
            skLineSegment(sketch, "E653", {"start": v(11.65, 21.9) * mm, "end": v(11.49, 22.2) * mm});
            skLineSegment(sketch, "E654", {"start": v(11.49, 22.2) * mm, "end": v(11.33, 22.52) * mm});
            skLineSegment(sketch, "E655", {"start": v(11.33, 22.52) * mm, "end": v(11.17, 22.83) * mm});
            skLineSegment(sketch, "E656", {"start": v(11.17, 22.83) * mm, "end": v(11.08, 22.94) * mm});
            skLineSegment(sketch, "E657", {"start": v(11.08, 22.94) * mm, "end": v(11, 23.05) * mm});
            skLineSegment(sketch, "E658", {"start": v(11, 23.05) * mm, "end": v(10.92, 23.15) * mm});
            skLineSegment(sketch, "E659", {"start": v(10.92, 23.15) * mm, "end": v(10.83, 23.26) * mm});
            skLineSegment(sketch, "E660", {"start": v(10.83, 23.26) * mm, "end": v(10.75, 23.36) * mm});
            skLineSegment(sketch, "E661", {"start": v(10.75, 23.36) * mm, "end": v(10.67, 23.47) * mm});
            skLineSegment(sketch, "E662", {"start": v(10.67, 23.47) * mm, "end": v(10.58, 23.57) * mm});
            skLineSegment(sketch, "E663", {"start": v(10.58, 23.57) * mm, "end": v(10.5, 23.67) * mm});
            skLineSegment(sketch, "E664", {"start": v(10.5, 23.67) * mm, "end": v(10.4, 23.77) * mm});
            skLineSegment(sketch, "E665", {"start": v(10.4, 23.77) * mm, "end": v(10.32, 23.87) * mm});
            skLineSegment(sketch, "E666", {"start": v(10.32, 23.87) * mm, "end": v(10.24, 23.97) * mm});
            skLineSegment(sketch, "E667", {"start": v(10.24, 23.97) * mm, "end": v(10.15, 24.07) * mm});
            skLineSegment(sketch, "E668", {"start": v(10.15, 24.07) * mm, "end": v(10.06, 24.17) * mm});
            skLineSegment(sketch, "E669", {"start": v(10.06, 24.17) * mm, "end": v(9.97, 24.26) * mm});
            skLineSegment(sketch, "E670", {"start": v(9.97, 24.26) * mm, "end": v(9.88, 24.36) * mm});
            skLineSegment(sketch, "E671", {"start": v(9.88, 24.36) * mm, "end": v(9.8, 24.45) * mm});
            skLineSegment(sketch, "E672", {"start": v(9.8, 24.45) * mm, "end": v(9.7, 24.55) * mm});
            skLineSegment(sketch, "E673", {"start": v(9.7, 24.55) * mm, "end": v(9.61, 24.64) * mm});
            skLineSegment(sketch, "E674", {"start": v(9.61, 24.64) * mm, "end": v(9.52, 24.73) * mm});
            skLineSegment(sketch, "E675", {"start": v(9.52, 24.73) * mm, "end": v(9.43, 24.82) * mm});
            skLineSegment(sketch, "E676", {"start": v(9.43, 24.82) * mm, "end": v(9.34, 24.91) * mm});
            skLineSegment(sketch, "E677", {"start": v(9.34, 24.91) * mm, "end": v(9.24, 25) * mm});
            skLineSegment(sketch, "E678", {"start": v(9.24, 25) * mm, "end": v(9.15, 25.1) * mm});
            skLineSegment(sketch, "E679", {"start": v(9.15, 25.1) * mm, "end": v(9.06, 25.18) * mm});
            skLineSegment(sketch, "E680", {"start": v(9.06, 25.18) * mm, "end": v(8.96, 25.27) * mm});
            skLineSegment(sketch, "E681", {"start": v(8.96, 25.27) * mm, "end": v(8.87, 25.36) * mm});
            skLineSegment(sketch, "E682", {"start": v(8.87, 25.36) * mm, "end": v(8.77, 25.44) * mm});
            skLineSegment(sketch, "E683", {"start": v(8.77, 25.44) * mm, "end": v(8.68, 25.53) * mm});
            skLineSegment(sketch, "E684", {"start": v(8.68, 25.53) * mm, "end": v(8.58, 25.6) * mm});
            skLineSegment(sketch, "E685", {"start": v(8.58, 25.6) * mm, "end": v(8.48, 25.7) * mm});
            skLineSegment(sketch, "E686", {"start": v(8.48, 25.7) * mm, "end": v(8.39, 25.77) * mm});
            skLineSegment(sketch, "E687", {"start": v(8.39, 25.77) * mm, "end": v(8.29, 25.86) * mm});
            skLineSegment(sketch, "E688", {"start": v(8.29, 25.86) * mm, "end": v(8.2, 25.94) * mm});
            skLineSegment(sketch, "E689", {"start": v(8.2, 25.94) * mm, "end": v(8.1, 26.02) * mm});
            skLineSegment(sketch, "E690", {"start": v(8.1, 26.02) * mm, "end": v(8, 26.1) * mm});
            skLineSegment(sketch, "E691", {"start": v(8, 26.1) * mm, "end": v(7.9, 26.17) * mm});
            skLineSegment(sketch, "E692", {"start": v(7.9, 26.17) * mm, "end": v(7.8, 26.25) * mm});
            skLineSegment(sketch, "E693", {"start": v(7.8, 26.25) * mm, "end": v(7.7, 26.33) * mm});
            skLineSegment(sketch, "E694", {"start": v(7.7, 26.33) * mm, "end": v(7.6, 26.4) * mm});
            skLineSegment(sketch, "E695", {"start": v(7.6, 26.4) * mm, "end": v(7.49, 26.48) * mm});
            skLineSegment(sketch, "E696", {"start": v(7.49, 26.48) * mm, "end": v(7.39, 26.55) * mm});
            skLineSegment(sketch, "E697", {"start": v(7.39, 26.55) * mm, "end": v(7.28, 26.62) * mm});
            skLineSegment(sketch, "E698", {"start": v(7.28, 26.62) * mm, "end": v(7.18, 26.7) * mm});
            skLineSegment(sketch, "E699", {"start": v(7.18, 26.7) * mm, "end": v(7.08, 26.77) * mm});
            skLineSegment(sketch, "E700", {"start": v(7.08, 26.77) * mm, "end": v(6.97, 26.84) * mm});
            skLineSegment(sketch, "E701", {"start": v(6.97, 26.84) * mm, "end": v(6.87, 26.9) * mm});
            skLineSegment(sketch, "E702", {"start": v(6.87, 26.9) * mm, "end": v(6.76, 26.98) * mm});
            skLineSegment(sketch, "E703", {"start": v(6.76, 26.98) * mm, "end": v(6.66, 27.04) * mm});
            skLineSegment(sketch, "E704", {"start": v(6.66, 27.04) * mm, "end": v(6.55, 27.11) * mm});
            skLineSegment(sketch, "E705", {"start": v(6.55, 27.11) * mm, "end": v(6.44, 27.18) * mm});
            skLineSegment(sketch, "E706", {"start": v(6.44, 27.18) * mm, "end": v(6.33, 27.24) * mm});
            skLineSegment(sketch, "E707", {"start": v(6.33, 27.24) * mm, "end": v(6.23, 27.3) * mm});
            skLineSegment(sketch, "E708", {"start": v(6.23, 27.3) * mm, "end": v(6.12, 27.37) * mm});
            skLineSegment(sketch, "E709", {"start": v(6.12, 27.37) * mm, "end": v(6, 27.43) * mm});
            skLineSegment(sketch, "E710", {"start": v(6, 27.43) * mm, "end": v(5.9, 27.5) * mm});
            skLineSegment(sketch, "E711", {"start": v(5.9, 27.5) * mm, "end": v(5.8, 27.56) * mm});
            skLineSegment(sketch, "E712", {"start": v(5.8, 27.56) * mm, "end": v(5.68, 27.62) * mm});
            skLineSegment(sketch, "E713", {"start": v(5.68, 27.62) * mm, "end": v(5.57, 27.68) * mm});
            skLineSegment(sketch, "E714", {"start": v(5.57, 27.68) * mm, "end": v(5.46, 27.74) * mm});
            skLineSegment(sketch, "E715", {"start": v(5.46, 27.74) * mm, "end": v(5.35, 27.8) * mm});
            skLineSegment(sketch, "E716", {"start": v(5.35, 27.8) * mm, "end": v(5.23, 27.85) * mm});
            skLineSegment(sketch, "E717", {"start": v(5.23, 27.85) * mm, "end": v(5.12, 27.9) * mm});
            skLineSegment(sketch, "E718", {"start": v(5.12, 27.9) * mm, "end": v(5, 27.96) * mm});
            skLineSegment(sketch, "E719", {"start": v(5, 27.96) * mm, "end": v(4.9, 28.02) * mm});
            skLineSegment(sketch, "E720", {"start": v(4.9, 28.02) * mm, "end": v(4.78, 28.07) * mm});
            skLineSegment(sketch, "E721", {"start": v(4.78, 28.07) * mm, "end": v(4.66, 28.12) * mm});
            skLineSegment(sketch, "E722", {"start": v(4.66, 28.12) * mm, "end": v(4.55, 28.17) * mm});
            skLineSegment(sketch, "E723", {"start": v(4.55, 28.17) * mm, "end": v(4.43, 28.22) * mm});
            skLineSegment(sketch, "E724", {"start": v(4.43, 28.22) * mm, "end": v(4.31, 28.28) * mm});
            skLineSegment(sketch, "E725", {"start": v(4.31, 28.28) * mm, "end": v(4.2, 28.32) * mm});
            skLineSegment(sketch, "E726", {"start": v(4.2, 28.32) * mm, "end": v(4.08, 28.37) * mm});
            skLineSegment(sketch, "E727", {"start": v(4.08, 28.37) * mm, "end": v(3.96, 28.42) * mm});
            skLineSegment(sketch, "E728", {"start": v(3.96, 28.42) * mm, "end": v(3.84, 28.47) * mm});
            skLineSegment(sketch, "E729", {"start": v(3.84, 28.47) * mm, "end": v(3.72, 28.51) * mm});
            skLineSegment(sketch, "E730", {"start": v(3.72, 28.51) * mm, "end": v(3.6, 28.56) * mm});
            skLineSegment(sketch, "E731", {"start": v(3.6, 28.56) * mm, "end": v(3.48, 28.6) * mm});
            skLineSegment(sketch, "E732", {"start": v(3.48, 28.6) * mm, "end": v(3.36, 28.65) * mm});
            skLineSegment(sketch, "E733", {"start": v(3.36, 28.65) * mm, "end": v(3.24, 28.69) * mm});
            skLineSegment(sketch, "E734", {"start": v(3.24, 28.69) * mm, "end": v(3.12, 28.73) * mm});
            skLineSegment(sketch, "E735", {"start": v(3.12, 28.73) * mm, "end": v(3, 28.77) * mm});
            skLineSegment(sketch, "E736", {"start": v(3, 28.77) * mm, "end": v(2.88, 28.81) * mm});
            skLineSegment(sketch, "E737", {"start": v(2.88, 28.81) * mm, "end": v(2.75, 28.85) * mm});
            skLineSegment(sketch, "E738", {"start": v(2.75, 28.85) * mm, "end": v(2.63, 28.89) * mm});
            skLineSegment(sketch, "E739", {"start": v(2.63, 28.89) * mm, "end": v(2.5, 28.93) * mm});
            skLineSegment(sketch, "E740", {"start": v(2.5, 28.93) * mm, "end": v(2.38, 28.96) * mm});
            skLineSegment(sketch, "E741", {"start": v(2.38, 28.96) * mm, "end": v(2.25, 29) * mm});
            skLineSegment(sketch, "E742", {"start": v(2.25, 29) * mm, "end": v(2.13, 29.03) * mm});
            skLineSegment(sketch, "E743", {"start": v(2.13, 29.03) * mm, "end": v(2, 29.07) * mm});
            skLineSegment(sketch, "E744", {"start": v(2, 29.07) * mm, "end": v(1.88, 29.1) * mm});
            skLineSegment(sketch, "E745", {"start": v(1.88, 29.1) * mm, "end": v(1.75, 29.13) * mm});
            skLineSegment(sketch, "E746", {"start": v(1.75, 29.13) * mm, "end": v(1.62, 29.17) * mm});
            skLineSegment(sketch, "E747", {"start": v(1.62, 29.17) * mm, "end": v(1.5, 29.2) * mm});
            skLineSegment(sketch, "E748", {"start": v(1.5, 29.2) * mm, "end": v(1.36, 29.23) * mm});
            skLineSegment(sketch, "E749", {"start": v(1.36, 29.23) * mm, "end": v(1.23, 29.26) * mm});
            skLineSegment(sketch, "E750", {"start": v(1.23, 29.26) * mm, "end": v(1.1, 29.28) * mm});
            skLineSegment(sketch, "E751", {"start": v(1.1, 29.28) * mm, "end": v(0.97, 29.31) * mm});
            skLineSegment(sketch, "E752", {"start": v(0.97, 29.31) * mm, "end": v(0.84, 29.34) * mm});
            skLineSegment(sketch, "E753", {"start": v(0.84, 29.34) * mm, "end": v(0.71, 29.36) * mm});
            skLineSegment(sketch, "E754", {"start": v(0.71, 29.36) * mm, "end": v(0.58, 29.39) * mm});
            skLineSegment(sketch, "E755", {"start": v(0.58, 29.39) * mm, "end": v(0.45, 29.41) * mm});
            skLineSegment(sketch, "E756", {"start": v(0.45, 29.41) * mm, "end": v(0.32, 29.44) * mm});
            skLineSegment(sketch, "E757", {"start": v(0.32, 29.44) * mm, "end": v(0.18, 29.46) * mm});
            skLineSegment(sketch, "E758", {"start": v(0.18, 29.46) * mm, "end": v(0, 29.49) * mm});
            skLineSegment(sketch, "E759", {"start": v(0.05, 29.48) * mm, "end": v(-0.09, 29.5) * mm});
            skLineSegment(sketch, "E760", {"start": v(-0.09, 29.5) * mm, "end": v(-0.22, 29.52) * mm});
            skLineSegment(sketch, "E761", {"start": v(-0.22, 29.52) * mm, "end": v(-0.36, 29.54) * mm});
            skLineSegment(sketch, "E762", {"start": v(-0.36, 29.54) * mm, "end": v(-0.5, 29.56) * mm});
            skLineSegment(sketch, "E763", {"start": v(-0.5, 29.56) * mm, "end": v(-0.63, 29.57) * mm});
            skLineSegment(sketch, "E764", {"start": v(-0.63, 29.57) * mm, "end": v(-0.77, 29.6) * mm});
            skLineSegment(sketch, "E765", {"start": v(-0.77, 29.6) * mm, "end": v(-0.9, 29.6) * mm});
            skLineSegment(sketch, "E766", {"start": v(-0.9, 29.6) * mm, "end": v(-1.04, 29.62) * mm});
            skLineSegment(sketch, "E767", {"start": v(-1.04, 29.62) * mm, "end": v(-1.18, 29.64) * mm});
            skLineSegment(sketch, "E768", {"start": v(-1.18, 29.64) * mm, "end": v(-1.46, 29.66) * mm});
            skLineSegment(sketch, "E769", {"start": v(-1.46, 29.66) * mm, "end": v(-1.74, 29.68) * mm});
            skLineSegment(sketch, "E770", {"start": v(-1.74, 29.68) * mm, "end": v(-2.02, 29.7) * mm});
            skLineSegment(sketch, "E771", {"start": v(-2.02, 29.7) * mm, "end": v(-2.3, 29.72) * mm});
            skLineSegment(sketch, "E772", {"start": v(-2.3, 29.72) * mm, "end": v(-2.6, 29.73) * mm});
            skLineSegment(sketch, "E773", {"start": v(-2.6, 29.73) * mm, "end": v(-2.88, 29.74) * mm});
            skLineSegment(sketch, "E774", {"start": v(-2.88, 29.74) * mm, "end": v(-3.17, 29.74) * mm});
            skLineSegment(sketch, "E775", {"start": v(-3.17, 29.74) * mm, "end": v(-3.46, 29.74) * mm});
            skLineSegment(sketch, "E776", {"start": v(-3.46, 29.74) * mm, "end": v(-3.67, 29.74) * mm});
            skLineSegment(sketch, "E777", {"start": v(-3.67, 29.74) * mm, "end": v(-3.87, 29.74) * mm});
            skLineSegment(sketch, "E778", {"start": v(-3.87, 29.74) * mm, "end": v(-4.08, 29.73) * mm});
            skLineSegment(sketch, "E779", {"start": v(-4.08, 29.73) * mm, "end": v(-4.29, 29.72) * mm});
            skLineSegment(sketch, "E780", {"start": v(-4.29, 29.72) * mm, "end": v(-4.5, 29.71) * mm});
            skLineSegment(sketch, "E781", {"start": v(-4.5, 29.71) * mm, "end": v(-4.7, 29.7) * mm});
            skLineSegment(sketch, "E782", {"start": v(-4.7, 29.7) * mm, "end": v(-4.91, 29.68) * mm});
            skLineSegment(sketch, "E783", {"start": v(-4.91, 29.68) * mm, "end": v(-5.12, 29.67) * mm});
            skLineSegment(sketch, "E784", {"start": v(-5.12, 29.67) * mm, "end": v(-5.33, 29.65) * mm});
            skLineSegment(sketch, "E785", {"start": v(-5.33, 29.65) * mm, "end": v(-5.54, 29.62) * mm});
            skLineSegment(sketch, "E786", {"start": v(-5.54, 29.62) * mm, "end": v(-5.76, 29.6) * mm});
            skLineSegment(sketch, "E787", {"start": v(-5.76, 29.6) * mm, "end": v(-5.97, 29.57) * mm});
            skLineSegment(sketch, "E788", {"start": v(-5.97, 29.57) * mm, "end": v(-6.18, 29.54) * mm});
            skLineSegment(sketch, "E789", {"start": v(-6.18, 29.54) * mm, "end": v(-6.4, 29.5) * mm});
            skLineSegment(sketch, "E790", {"start": v(-6.4, 29.5) * mm, "end": v(-6.62, 29.47) * mm});
            skLineSegment(sketch, "E791", {"start": v(-6.62, 29.47) * mm, "end": v(-6.83, 29.43) * mm});
            skLineSegment(sketch, "E792", {"start": v(-6.83, 29.43) * mm, "end": v(-7.05, 29.4) * mm});
            skLineSegment(sketch, "E793", {"start": v(-7.05, 29.4) * mm, "end": v(-7.27, 29.35) * mm});
            skLineSegment(sketch, "E794", {"start": v(-7.27, 29.35) * mm, "end": v(-7.49, 29.3) * mm});
            skLineSegment(sketch, "E795", {"start": v(-7.49, 29.3) * mm, "end": v(-7.7, 29.26) * mm});
            skLineSegment(sketch, "E796", {"start": v(-7.7, 29.26) * mm, "end": v(-7.93, 29.21) * mm});
            skLineSegment(sketch, "E797", {"start": v(-7.93, 29.21) * mm, "end": v(-8.15, 29.16) * mm});
            skLineSegment(sketch, "E798", {"start": v(-8.15, 29.16) * mm, "end": v(-8.37, 29.1) * mm});
            skLineSegment(sketch, "E799", {"start": v(-8.37, 29.1) * mm, "end": v(-8.6, 29.05) * mm});
            skLineSegment(sketch, "E800", {"start": v(-8.6, 29.05) * mm, "end": v(-8.82, 28.99) * mm});
            skLineSegment(sketch, "E801", {"start": v(-8.82, 28.99) * mm, "end": v(-9.04, 28.93) * mm});
            skLineSegment(sketch, "E802", {"start": v(-9.04, 28.93) * mm, "end": v(-9.27, 28.86) * mm});
            skLineSegment(sketch, "E803", {"start": v(-9.27, 28.86) * mm, "end": v(-9.5, 28.8) * mm});
            skLineSegment(sketch, "E804", {"start": v(-9.5, 28.8) * mm, "end": v(-9.72, 28.73) * mm});
            skLineSegment(sketch, "E805", {"start": v(-9.72, 28.73) * mm, "end": v(-9.95, 28.66) * mm});
            skLineSegment(sketch, "E806", {"start": v(-9.95, 28.66) * mm, "end": v(-10.18, 28.58) * mm});
            skLineSegment(sketch, "E807", {"start": v(-10.18, 28.58) * mm, "end": v(-10.4, 28.5) * mm});
            skLineSegment(sketch, "E808", {"start": v(-10.4, 28.5) * mm, "end": v(-10.4, -28.8) * mm});
            skLineSegment(sketch, "E809", {"start": v(-10.4, -28.8) * mm, "end": v(-10.16, -28.87) * mm});
            skLineSegment(sketch, "E810", {"start": v(-10.16, -28.87) * mm, "end": v(-9.9, -28.94) * mm});
            skLineSegment(sketch, "E811", {"start": v(-9.9, -28.94) * mm, "end": v(-9.66, -29.01) * mm});
            skLineSegment(sketch, "E812", {"start": v(-9.66, -29.01) * mm, "end": v(-9.41, -29.08) * mm});
            skLineSegment(sketch, "E813", {"start": v(-9.41, -29.08) * mm, "end": v(-9.16, -29.14) * mm});
            skLineSegment(sketch, "E814", {"start": v(-9.16, -29.14) * mm, "end": v(-8.92, -29.2) * mm});
            skLineSegment(sketch, "E815", {"start": v(-8.92, -29.2) * mm, "end": v(-8.68, -29.27) * mm});
            skLineSegment(sketch, "E816", {"start": v(-8.68, -29.27) * mm, "end": v(-8.44, -29.32) * mm});
            skLineSegment(sketch, "E817", {"start": v(-8.44, -29.32) * mm, "end": v(-8.2, -29.38) * mm});
            skLineSegment(sketch, "E818", {"start": v(-8.2, -29.38) * mm, "end": v(-7.96, -29.43) * mm});
            skLineSegment(sketch, "E819", {"start": v(-7.96, -29.43) * mm, "end": v(-7.73, -29.48) * mm});
            skLineSegment(sketch, "E820", {"start": v(-7.73, -29.48) * mm, "end": v(-7.5, -29.53) * mm});
            skLineSegment(sketch, "E821", {"start": v(-7.5, -29.53) * mm, "end": v(-7.26, -29.58) * mm});
            skLineSegment(sketch, "E822", {"start": v(-7.26, -29.58) * mm, "end": v(-7.03, -29.62) * mm});
            skLineSegment(sketch, "E823", {"start": v(-7.03, -29.62) * mm, "end": v(-6.8, -29.66) * mm});
            skLineSegment(sketch, "E824", {"start": v(-6.8, -29.66) * mm, "end": v(-6.57, -29.7) * mm});
            skLineSegment(sketch, "E825", {"start": v(-6.57, -29.7) * mm, "end": v(-6.35, -29.74) * mm});
            skLineSegment(sketch, "E826", {"start": v(-6.35, -29.74) * mm, "end": v(-6.12, -29.77) * mm});
            skLineSegment(sketch, "E827", {"start": v(-6.12, -29.77) * mm, "end": v(-5.9, -29.8) * mm});
            skLineSegment(sketch, "E828", {"start": v(-5.9, -29.8) * mm, "end": v(-5.68, -29.83) * mm});
            skLineSegment(sketch, "E829", {"start": v(-5.68, -29.83) * mm, "end": v(-5.46, -29.86) * mm});
            skLineSegment(sketch, "E830", {"start": v(-5.46, -29.86) * mm, "end": v(-5.24, -29.89) * mm});
            skLineSegment(sketch, "E831", {"start": v(-5.24, -29.89) * mm, "end": v(-5.03, -29.9) * mm});
            skLineSegment(sketch, "E832", {"start": v(-5.03, -29.9) * mm, "end": v(-4.81, -29.93) * mm});
            skLineSegment(sketch, "E833", {"start": v(-4.81, -29.93) * mm, "end": v(-4.6, -29.95) * mm});
            skLineSegment(sketch, "E834", {"start": v(-4.6, -29.95) * mm, "end": v(-4.39, -29.96) * mm});
            skLineSegment(sketch, "E835", {"start": v(-4.39, -29.96) * mm, "end": v(-4.18, -29.97) * mm});
            skLineSegment(sketch, "E836", {"start": v(-4.18, -29.97) * mm, "end": v(-3.97, -29.98) * mm});
            skLineSegment(sketch, "E837", {"start": v(-3.97, -29.98) * mm, "end": v(-3.77, -30) * mm});
            skLineSegment(sketch, "E838", {"start": v(-3.77, -30) * mm, "end": v(-3.56, -30) * mm});
            skLineSegment(sketch, "E839", {"start": v(-3.56, -30) * mm, "end": v(-3.36, -30) * mm});
            skLineSegment(sketch, "E840", {"start": v(-3.36, -30) * mm, "end": v(-3.16, -30) * mm});
            skLineSegment(sketch, "E841", {"start": v(-3.16, -30) * mm, "end": v(-3.02, -30) * mm});
            skLineSegment(sketch, "E842", {"start": v(-3.02, -30) * mm, "end": v(-2.87, -30) * mm});
            skLineSegment(sketch, "E843", {"start": v(-2.87, -30) * mm, "end": v(-2.73, -30) * mm});
            skLineSegment(sketch, "E844", {"start": v(-2.73, -30) * mm, "end": v(-2.6, -30) * mm});
            skLineSegment(sketch, "E845", {"start": v(-2.6, -30) * mm, "end": v(-2.45, -30) * mm});
            skLineSegment(sketch, "E846", {"start": v(-2.45, -30) * mm, "end": v(-2.3, -29.98) * mm});
            skLineSegment(sketch, "E847", {"start": v(-2.3, -29.98) * mm, "end": v(-2.17, -29.98) * mm});
            skLineSegment(sketch, "E848", {"start": v(-2.17, -29.98) * mm, "end": v(-2.03, -29.97) * mm});
            skLineSegment(sketch, "E849", {"start": v(-2.03, -29.97) * mm, "end": v(-1.89, -29.96) * mm});
            skLineSegment(sketch, "E850", {"start": v(-1.89, -29.96) * mm, "end": v(-1.75, -29.95) * mm});
            skLineSegment(sketch, "E851", {"start": v(-1.75, -29.95) * mm, "end": v(-1.61, -29.94) * mm});
            skLineSegment(sketch, "E852", {"start": v(-1.61, -29.94) * mm, "end": v(-1.47, -29.93) * mm});
            skLineSegment(sketch, "E853", {"start": v(-1.47, -29.93) * mm, "end": v(-1.34, -29.91) * mm});
            skLineSegment(sketch, "E854", {"start": v(-1.34, -29.91) * mm, "end": v(-1.2, -29.9) * mm});
            skLineSegment(sketch, "E855", {"start": v(-1.2, -29.9) * mm, "end": v(-1.06, -29.88) * mm});
            skLineSegment(sketch, "E856", {"start": v(-1.06, -29.88) * mm, "end": v(-0.93, -29.87) * mm});
            skLineSegment(sketch, "E857", {"start": v(-0.93, -29.87) * mm, "end": v(-0.8, -29.85) * mm});
            skLineSegment(sketch, "E858", {"start": v(-0.8, -29.85) * mm, "end": v(-0.66, -29.83) * mm});
            skLineSegment(sketch, "E859", {"start": v(-0.66, -29.83) * mm, "end": v(-0.52, -29.8) * mm});
            skLineSegment(sketch, "E860", {"start": v(-0.52, -29.8) * mm, "end": v(-0.39, -29.79) * mm});
            skLineSegment(sketch, "E861", {"start": v(-0.39, -29.79) * mm, "end": v(-0.25, -29.77) * mm});
            skLineSegment(sketch, "E862", {"start": v(-0.25, -29.77) * mm, "end": v(-0.12, -29.74) * mm});
            skLineSegment(sketch, "E863", {"start": v(-0.12, -29.74) * mm, "end": v(0.01, -29.72) * mm});
            skLineSegment(sketch, "E864", {"start": v(0.01, -29.72) * mm, "end": v(0.14, -29.7) * mm});
            skLineSegment(sketch, "E865", {"start": v(0.14, -29.7) * mm, "end": v(0.28, -29.67) * mm});
            skLineSegment(sketch, "E866", {"start": v(0.28, -29.67) * mm, "end": v(0.4, -29.64) * mm});
            skLineSegment(sketch, "E867", {"start": v(0.4, -29.64) * mm, "end": v(0.54, -29.61) * mm});
            skLineSegment(sketch, "E868", {"start": v(0.54, -29.61) * mm, "end": v(0.67, -29.58) * mm});
            skLineSegment(sketch, "E869", {"start": v(0.67, -29.58) * mm, "end": v(0.8, -29.55) * mm});
            skLineSegment(sketch, "E870", {"start": v(0.8, -29.55) * mm, "end": v(0.93, -29.52) * mm});
            skLineSegment(sketch, "E871", {"start": v(0.93, -29.52) * mm, "end": v(1.06, -29.49) * mm});
            skLineSegment(sketch, "E872", {"start": v(1.06, -29.49) * mm, "end": v(1.19, -29.45) * mm});
            skLineSegment(sketch, "E873", {"start": v(1.19, -29.45) * mm, "end": v(1.31, -29.42) * mm});
            skLineSegment(sketch, "E874", {"start": v(1.31, -29.42) * mm, "end": v(1.44, -29.38) * mm});
            skLineSegment(sketch, "E875", {"start": v(1.44, -29.38) * mm, "end": v(1.57, -29.35) * mm});
            skLineSegment(sketch, "E876", {"start": v(1.57, -29.35) * mm, "end": v(1.7, -29.3) * mm});
            skLineSegment(sketch, "E877", {"start": v(1.7, -29.3) * mm, "end": v(1.82, -29.27) * mm});
            skLineSegment(sketch, "E878", {"start": v(1.82, -29.27) * mm, "end": v(1.95, -29.23) * mm});
            skLineSegment(sketch, "E879", {"start": v(1.95, -29.23) * mm, "end": v(2.07, -29.19) * mm});
            skLineSegment(sketch, "E880", {"start": v(2.07, -29.19) * mm, "end": v(2.2, -29.14) * mm});
            skLineSegment(sketch, "E881", {"start": v(2.2, -29.14) * mm, "end": v(2.32, -29.1) * mm});
            skLineSegment(sketch, "E882", {"start": v(2.32, -29.1) * mm, "end": v(2.45, -29.06) * mm});
            skLineSegment(sketch, "E883", {"start": v(2.45, -29.06) * mm, "end": v(2.57, -29) * mm});
            skLineSegment(sketch, "E884", {"start": v(2.57, -29) * mm, "end": v(2.7, -28.96) * mm});
            skLineSegment(sketch, "E885", {"start": v(2.7, -28.96) * mm, "end": v(2.82, -28.92) * mm});
            skLineSegment(sketch, "E886", {"start": v(2.82, -28.92) * mm, "end": v(2.94, -28.87) * mm});
            skLineSegment(sketch, "E887", {"start": v(2.94, -28.87) * mm, "end": v(3.06, -28.82) * mm});
            skLineSegment(sketch, "E888", {"start": v(3.06, -28.82) * mm, "end": v(3.18, -28.77) * mm});
            skLineSegment(sketch, "E889", {"start": v(3.18, -28.77) * mm, "end": v(3.3, -28.71) * mm});
            skLineSegment(sketch, "E890", {"start": v(3.3, -28.71) * mm, "end": v(3.42, -28.66) * mm});
            skLineSegment(sketch, "E891", {"start": v(3.42, -28.66) * mm, "end": v(3.54, -28.6) * mm});
            skLineSegment(sketch, "E892", {"start": v(3.54, -28.6) * mm, "end": v(3.66, -28.55) * mm});
            skLineSegment(sketch, "E893", {"start": v(3.66, -28.55) * mm, "end": v(3.78, -28.5) * mm});
            skLineSegment(sketch, "E894", {"start": v(3.78, -28.5) * mm, "end": v(3.9, -28.44) * mm});
            skLineSegment(sketch, "E895", {"start": v(3.9, -28.44) * mm, "end": v(4.02, -28.38) * mm});
            skLineSegment(sketch, "E896", {"start": v(4.02, -28.38) * mm, "end": v(4.13, -28.32) * mm});
            skLineSegment(sketch, "E897", {"start": v(4.13, -28.32) * mm, "end": v(4.25, -28.26) * mm});
            skLineSegment(sketch, "E898", {"start": v(4.25, -28.26) * mm, "end": v(4.37, -28.2) * mm});
            skLineSegment(sketch, "E899", {"start": v(4.37, -28.2) * mm, "end": v(4.48, -28.13) * mm});
            skLineSegment(sketch, "E900", {"start": v(4.48, -28.13) * mm, "end": v(4.6, -28.07) * mm});
            skLineSegment(sketch, "E901", {"start": v(4.6, -28.07) * mm, "end": v(4.72, -28) * mm});
            skLineSegment(sketch, "E902", {"start": v(4.72, -28) * mm, "end": v(4.83, -27.94) * mm});
            skLineSegment(sketch, "E903", {"start": v(4.83, -27.94) * mm, "end": v(4.94, -27.87) * mm});
            skLineSegment(sketch, "E904", {"start": v(4.94, -27.87) * mm, "end": v(5.06, -27.8) * mm});
            skLineSegment(sketch, "E905", {"start": v(5.06, -27.8) * mm, "end": v(5.17, -27.73) * mm});
            skLineSegment(sketch, "E906", {"start": v(5.17, -27.73) * mm, "end": v(5.28, -27.66) * mm});
            skLineSegment(sketch, "E907", {"start": v(5.28, -27.66) * mm, "end": v(5.4, -27.6) * mm});
            skLineSegment(sketch, "E908", {"start": v(5.4, -27.6) * mm, "end": v(5.5, -27.52) * mm});
            skLineSegment(sketch, "E909", {"start": v(5.5, -27.52) * mm, "end": v(5.62, -27.44) * mm});
            skLineSegment(sketch, "E910", {"start": v(5.62, -27.44) * mm, "end": v(5.73, -27.37) * mm});
            skLineSegment(sketch, "E911", {"start": v(5.73, -27.37) * mm, "end": v(5.84, -27.3) * mm});
            skLineSegment(sketch, "E912", {"start": v(5.84, -27.3) * mm, "end": v(5.95, -27.22) * mm});
            skLineSegment(sketch, "E913", {"start": v(5.95, -27.22) * mm, "end": v(6.06, -27.14) * mm});
            skLineSegment(sketch, "E914", {"start": v(6.06, -27.14) * mm, "end": v(6.17, -27.06) * mm});
            skLineSegment(sketch, "E915", {"start": v(6.17, -27.06) * mm, "end": v(6.28, -26.98) * mm});
            skLineSegment(sketch, "E916", {"start": v(6.28, -26.98) * mm, "end": v(6.39, -26.9) * mm});
            skLineSegment(sketch, "E917", {"start": v(6.39, -26.9) * mm, "end": v(6.5, -26.82) * mm});
            skLineSegment(sketch, "E918", {"start": v(6.5, -26.82) * mm, "end": v(6.6, -26.73) * mm});
            skLineSegment(sketch, "E919", {"start": v(6.6, -26.73) * mm, "end": v(6.7, -26.65) * mm});
            skLineSegment(sketch, "E920", {"start": v(6.7, -26.65) * mm, "end": v(6.81, -26.56) * mm});
            skLineSegment(sketch, "E921", {"start": v(6.81, -26.56) * mm, "end": v(6.92, -26.48) * mm});
            skLineSegment(sketch, "E922", {"start": v(6.92, -26.48) * mm, "end": v(7.03, -26.39) * mm});
            skLineSegment(sketch, "E923", {"start": v(7.03, -26.39) * mm, "end": v(7.13, -26.3) * mm});
            skLineSegment(sketch, "E924", {"start": v(7.13, -26.3) * mm, "end": v(7.24, -26.21) * mm});
            skLineSegment(sketch, "E925", {"start": v(7.24, -26.21) * mm, "end": v(7.34, -26.12) * mm});
            skLineSegment(sketch, "E926", {"start": v(7.34, -26.12) * mm, "end": v(7.44, -26.03) * mm});
            skLineSegment(sketch, "E927", {"start": v(7.44, -26.03) * mm, "end": v(7.55, -25.93) * mm});
            skLineSegment(sketch, "E928", {"start": v(7.55, -25.93) * mm, "end": v(7.65, -25.84) * mm});
            skLineSegment(sketch, "E929", {"start": v(7.65, -25.84) * mm, "end": v(7.75, -25.75) * mm});
            skLineSegment(sketch, "E930", {"start": v(7.75, -25.75) * mm, "end": v(7.85, -25.65) * mm});
            skLineSegment(sketch, "E931", {"start": v(7.85, -25.65) * mm, "end": v(7.95, -25.55) * mm});
            skLineSegment(sketch, "E932", {"start": v(7.95, -25.55) * mm, "end": v(8.05, -25.45) * mm});
            skLineSegment(sketch, "E933", {"start": v(8.05, -25.45) * mm, "end": v(8.15, -25.35) * mm});
            skLineSegment(sketch, "E934", {"start": v(8.15, -25.35) * mm, "end": v(8.25, -25.25) * mm});
            skLineSegment(sketch, "E935", {"start": v(8.25, -25.25) * mm, "end": v(8.35, -25.15) * mm});
            skLineSegment(sketch, "E936", {"start": v(8.35, -25.15) * mm, "end": v(8.45, -25.05) * mm});
            skLineSegment(sketch, "E937", {"start": v(8.45, -25.05) * mm, "end": v(8.55, -24.95) * mm});
            skLineSegment(sketch, "E938", {"start": v(8.55, -24.95) * mm, "end": v(8.65, -24.84) * mm});
            skLineSegment(sketch, "E939", {"start": v(8.65, -24.84) * mm, "end": v(8.75, -24.74) * mm});
            skLineSegment(sketch, "E940", {"start": v(8.75, -24.74) * mm, "end": v(8.84, -24.63) * mm});
            skLineSegment(sketch, "E941", {"start": v(8.84, -24.63) * mm, "end": v(8.94, -24.52) * mm});
            skLineSegment(sketch, "E942", {"start": v(8.94, -24.52) * mm, "end": v(9.04, -24.41) * mm});
            skLineSegment(sketch, "E943", {"start": v(9.04, -24.41) * mm, "end": v(9.13, -24.3) * mm});
            skLineSegment(sketch, "E944", {"start": v(9.13, -24.3) * mm, "end": v(9.23, -24.19) * mm});
            skLineSegment(sketch, "E945", {"start": v(9.23, -24.19) * mm, "end": v(9.32, -24.08) * mm});
            skLineSegment(sketch, "E946", {"start": v(9.32, -24.08) * mm, "end": v(9.42, -23.96) * mm});
            skLineSegment(sketch, "E947", {"start": v(9.42, -23.96) * mm, "end": v(9.5, -23.85) * mm});
            skLineSegment(sketch, "E948", {"start": v(9.5, -23.85) * mm, "end": v(9.6, -23.73) * mm});
            skLineSegment(sketch, "E949", {"start": v(9.6, -23.73) * mm, "end": v(9.7, -23.62) * mm});
            skLineSegment(sketch, "E950", {"start": v(9.7, -23.62) * mm, "end": v(9.79, -23.5) * mm});
            skLineSegment(sketch, "E951", {"start": v(9.79, -23.5) * mm, "end": v(9.88, -23.38) * mm});
            skLineSegment(sketch, "E952", {"start": v(9.88, -23.38) * mm, "end": v(9.97, -23.26) * mm});
            skLineSegment(sketch, "E953", {"start": v(9.97, -23.26) * mm, "end": v(10.06, -23.14) * mm});
            skLineSegment(sketch, "E954", {"start": v(10.06, -23.14) * mm, "end": v(10.15, -23.02) * mm});
            skLineSegment(sketch, "E955", {"start": v(10.15, -23.02) * mm, "end": v(10.24, -22.9) * mm});
            skLineSegment(sketch, "E956", {"start": v(10.24, -22.9) * mm, "end": v(10.33, -22.77) * mm});
            skLineSegment(sketch, "E957", {"start": v(10.33, -22.77) * mm, "end": v(10.42, -22.65) * mm});
            skLineSegment(sketch, "E958", {"start": v(10.42, -22.65) * mm, "end": v(10.51, -22.52) * mm});
            skLineSegment(sketch, "E959", {"start": v(10.51, -22.52) * mm, "end": v(10.6, -22.4) * mm});
            skLineSegment(sketch, "E960", {"start": v(10.6, -22.4) * mm, "end": v(10.69, -22.26) * mm});
            skLineSegment(sketch, "E961", {"start": v(10.69, -22.26) * mm, "end": v(10.77, -22.13) * mm});
            skLineSegment(sketch, "E962", {"start": v(10.77, -22.13) * mm, "end": v(10.86, -22) * mm});
            skLineSegment(sketch, "E963", {"start": v(10.86, -22) * mm, "end": v(10.95, -21.87) * mm});
            skLineSegment(sketch, "E964", {"start": v(10.95, -21.87) * mm, "end": v(11.03, -21.74) * mm});
            skLineSegment(sketch, "E965", {"start": v(11.03, -21.74) * mm, "end": v(11.12, -21.6) * mm});
            skLineSegment(sketch, "E966", {"start": v(11.12, -21.6) * mm, "end": v(11.2, -21.47) * mm});
            skLineSegment(sketch, "E967", {"start": v(11.2, -21.47) * mm, "end": v(11.29, -21.33) * mm});
            skLineSegment(sketch, "E968", {"start": v(11.29, -21.33) * mm, "end": v(11.37, -21.2) * mm});
            skLineSegment(sketch, "E969", {"start": v(11.37, -21.2) * mm, "end": v(11.53, -20.94) * mm});
            skLineSegment(sketch, "E970", {"start": v(11.53, -20.94) * mm, "end": v(11.68, -20.68) * mm});
            skLineSegment(sketch, "E971", {"start": v(11.68, -20.68) * mm, "end": v(11.83, -20.41) * mm});
            skLineSegment(sketch, "E972", {"start": v(11.83, -20.41) * mm, "end": v(11.98, -20.15) * mm});
            skLineSegment(sketch, "E973", {"start": v(11.98, -20.15) * mm, "end": v(12.13, -19.88) * mm});
            skLineSegment(sketch, "E974", {"start": v(12.13, -19.88) * mm, "end": v(12.27, -19.6) * mm});
            skLineSegment(sketch, "E975", {"start": v(12.27, -19.6) * mm, "end": v(12.42, -19.34) * mm});
            skLineSegment(sketch, "E976", {"start": v(12.42, -19.34) * mm, "end": v(12.56, -19.06) * mm});
            skLineSegment(sketch, "E977", {"start": v(12.56, -19.06) * mm, "end": v(12.7, -18.78) * mm});
            skLineSegment(sketch, "E978", {"start": v(12.7, -18.78) * mm, "end": v(12.83, -18.5) * mm});
            skLineSegment(sketch, "E979", {"start": v(12.83, -18.5) * mm, "end": v(12.96, -18.22) * mm});
            skLineSegment(sketch, "E980", {"start": v(12.96, -18.22) * mm, "end": v(13.09, -17.94) * mm});
            skLineSegment(sketch, "E981", {"start": v(13.09, -17.94) * mm, "end": v(13.22, -17.65) * mm});
            skLineSegment(sketch, "E982", {"start": v(13.22, -17.65) * mm, "end": v(13.34, -17.37) * mm});
            skLineSegment(sketch, "E983", {"start": v(13.34, -17.37) * mm, "end": v(13.46, -17.08) * mm});
            skLineSegment(sketch, "E984", {"start": v(13.46, -17.08) * mm, "end": v(13.58, -16.78) * mm});
            skLineSegment(sketch, "E985", {"start": v(13.58, -16.78) * mm, "end": v(13.7, -16.49) * mm});
            skLineSegment(sketch, "E986", {"start": v(13.7, -16.49) * mm, "end": v(13.81, -16.2) * mm});
            skLineSegment(sketch, "E987", {"start": v(13.81, -16.2) * mm, "end": v(13.93, -15.9) * mm});
            skLineSegment(sketch, "E988", {"start": v(13.93, -15.9) * mm, "end": v(14.04, -15.6) * mm});
            skLineSegment(sketch, "E989", {"start": v(14.04, -15.6) * mm, "end": v(14.14, -15.29) * mm});
            skLineSegment(sketch, "E990", {"start": v(14.14, -15.29) * mm, "end": v(14.25, -14.98) * mm});
            skLineSegment(sketch, "E991", {"start": v(14.25, -14.98) * mm, "end": v(14.35, -14.67) * mm});
            skLineSegment(sketch, "E992", {"start": v(14.35, -14.67) * mm, "end": v(14.45, -14.36) * mm});
            skLineSegment(sketch, "E993", {"start": v(14.45, -14.36) * mm, "end": v(14.55, -14.05) * mm});
            skLineSegment(sketch, "E994", {"start": v(14.55, -14.05) * mm, "end": v(14.64, -13.74) * mm});
            skLineSegment(sketch, "E995", {"start": v(14.64, -13.74) * mm, "end": v(14.74, -13.42) * mm});
            skLineSegment(sketch, "E996", {"start": v(14.74, -13.42) * mm, "end": v(14.83, -13.1) * mm});
            skLineSegment(sketch, "E997", {"start": v(14.83, -13.1) * mm, "end": v(14.91, -12.78) * mm});
            skLineSegment(sketch, "E998", {"start": v(14.91, -12.78) * mm, "end": v(15, -12.45) * mm});
            skLineSegment(sketch, "E999", {"start": v(15, -12.45) * mm, "end": v(15.08, -12.13) * mm});
            skLineSegment(sketch, "E1000", {"start": v(15.08, -12.13) * mm, "end": v(15.16, -11.8) * mm});
            skLineSegment(sketch, "E1001", {"start": v(15.16, -11.8) * mm, "end": v(15.24, -11.47) * mm});
            skLineSegment(sketch, "E1002", {"start": v(15.24, -11.47) * mm, "end": v(15.31, -11.14) * mm});
            skLineSegment(sketch, "E1003", {"start": v(15.31, -11.14) * mm, "end": v(15.39, -10.8) * mm});
            skLineSegment(sketch, "E1004", {"start": v(15.39, -10.8) * mm, "end": v(15.46, -10.47) * mm});
            skLineSegment(sketch, "E1005", {"start": v(15.46, -10.47) * mm, "end": v(15.52, -10.13) * mm});
            skLineSegment(sketch, "E1006", {"start": v(15.52, -10.13) * mm, "end": v(15.6, -9.79) * mm});
            skLineSegment(sketch, "E1007", {"start": v(15.6, -9.79) * mm, "end": v(15.65, -9.44) * mm});
            skLineSegment(sketch, "E1008", {"start": v(15.65, -9.44) * mm, "end": v(15.71, -9.1) * mm});
            skLineSegment(sketch, "E1009", {"start": v(15.71, -9.1) * mm, "end": v(15.77, -8.75) * mm});
            skLineSegment(sketch, "E1010", {"start": v(15.77, -8.75) * mm, "end": v(15.83, -8.4) * mm});
            skLineSegment(sketch, "E1011", {"start": v(15.83, -8.4) * mm, "end": v(15.88, -8.05) * mm});
            skLineSegment(sketch, "E1012", {"start": v(15.88, -8.05) * mm, "end": v(15.93, -7.7) * mm});
            skLineSegment(sketch, "E1013", {"start": v(15.93, -7.7) * mm, "end": v(15.98, -7.33) * mm});
            skLineSegment(sketch, "E1014", {"start": v(15.98, -7.33) * mm, "end": v(16.02, -6.97) * mm});
            skLineSegment(sketch, "E1015", {"start": v(16.02, -6.97) * mm, "end": v(16.07, -6.61) * mm});
            skLineSegment(sketch, "E1016", {"start": v(16.07, -6.61) * mm, "end": v(16.1, -6.25) * mm});
            skLineSegment(sketch, "E1017", {"start": v(16.1, -6.25) * mm, "end": v(16.15, -5.88) * mm});
            skLineSegment(sketch, "E1018", {"start": v(16.15, -5.88) * mm, "end": v(16.18, -5.52) * mm});
            skLineSegment(sketch, "E1019", {"start": v(16.18, -5.52) * mm, "end": v(16.22, -5.15) * mm});
            skLineSegment(sketch, "E1020", {"start": v(16.22, -5.15) * mm, "end": v(16.25, -4.77) * mm});
            skLineSegment(sketch, "E1021", {"start": v(16.25, -4.77) * mm, "end": v(16.27, -4.4) * mm});
            skLineSegment(sketch, "E1022", {"start": v(16.27, -4.4) * mm, "end": v(16.3, -4.02) * mm});
            skLineSegment(sketch, "E1023", {"start": v(16.3, -4.02) * mm, "end": v(16.32, -3.64) * mm});
            skLineSegment(sketch, "E1024", {"start": v(16.32, -3.64) * mm, "end": v(16.35, -3.26) * mm});
            skLineSegment(sketch, "E1025", {"start": v(16.35, -3.26) * mm, "end": v(16.36, -2.88) * mm});
            skLineSegment(sketch, "E1026", {"start": v(16.36, -2.88) * mm, "end": v(16.38, -2.5) * mm});
            skLineSegment(sketch, "E1027", {"start": v(16.38, -2.5) * mm, "end": v(16.4, -2.1) * mm});
            skLineSegment(sketch, "E1028", {"start": v(16.4, -2.1) * mm, "end": v(16.4, -1.71) * mm});
            skLineSegment(sketch, "E1029", {"start": v(16.4, -1.71) * mm, "end": v(16.41, -1.32) * mm});
            skLineSegment(sketch, "E1030", {"start": v(16.41, -1.32) * mm, "end": v(16.42, -0.93) * mm});
            skLineSegment(sketch, "E1031", {"start": v(16.42, -0.93) * mm, "end": v(16.42, -0.53) * mm});
            skLineSegment(sketch, "E1032", {"start": v(16.42, -0.53) * mm, "end": v(16.42, -0.13) * mm});
            skLineSegment(sketch, "E1033", {"start": v(-14.96, 17.46) * mm, "end": v(-14.96, 18.39) * mm});
            skLineSegment(sketch, "E1034", {"start": v(-14.96, 18.39) * mm, "end": v(-14.93, 18.4) * mm});
            skLineSegment(sketch, "E1035", {"start": v(-14.93, 18.4) * mm, "end": v(-14.9, 18.43) * mm});
            skLineSegment(sketch, "E1036", {"start": v(-14.9, 18.43) * mm, "end": v(-14.86, 18.46) * mm});
            skLineSegment(sketch, "E1037", {"start": v(-14.86, 18.46) * mm, "end": v(-14.83, 18.48) * mm});
            skLineSegment(sketch, "E1038", {"start": v(-14.83, 18.48) * mm, "end": v(-14.8, 18.5) * mm});
            skLineSegment(sketch, "E1039", {"start": v(-14.8, 18.5) * mm, "end": v(-14.78, 18.53) * mm});
            skLineSegment(sketch, "E1040", {"start": v(-14.78, 18.53) * mm, "end": v(-14.76, 18.55) * mm});
            skLineSegment(sketch, "E1041", {"start": v(-14.76, 18.55) * mm, "end": v(-14.74, 18.58) * mm});
            skLineSegment(sketch, "E1042", {"start": v(-14.74, 18.58) * mm, "end": v(-14.72, 18.6) * mm});
            skLineSegment(sketch, "E1043", {"start": v(-14.72, 18.6) * mm, "end": v(-14.7, 18.63) * mm});
            skLineSegment(sketch, "E1044", {"start": v(-14.7, 18.63) * mm, "end": v(-14.68, 18.67) * mm});
            skLineSegment(sketch, "E1045", {"start": v(-14.68, 18.67) * mm, "end": v(-14.66, 18.7) * mm});
            skLineSegment(sketch, "E1046", {"start": v(-14.66, 18.7) * mm, "end": v(-14.65, 18.74) * mm});
            skLineSegment(sketch, "E1047", {"start": v(-14.65, 18.74) * mm, "end": v(-14.63, 18.78) * mm});
            skLineSegment(sketch, "E1048", {"start": v(-14.63, 18.78) * mm, "end": v(-14.62, 18.82) * mm});
            skLineSegment(sketch, "E1049", {"start": v(-14.62, 18.82) * mm, "end": v(-14.6, 18.87) * mm});
            skLineSegment(sketch, "E1050", {"start": v(-14.6, 18.87) * mm, "end": v(-14.59, 18.92) * mm});
            skLineSegment(sketch, "E1051", {"start": v(-14.59, 18.92) * mm, "end": v(-14.58, 18.97) * mm});
            skLineSegment(sketch, "E1052", {"start": v(-14.58, 18.97) * mm, "end": v(-14.56, 19.02) * mm});
            skLineSegment(sketch, "E1053", {"start": v(-14.56, 19.02) * mm, "end": v(-14.55, 19.07) * mm});
            skLineSegment(sketch, "E1054", {"start": v(-14.55, 19.07) * mm, "end": v(-14.54, 19.12) * mm});
            skLineSegment(sketch, "E1055", {"start": v(-14.54, 19.12) * mm, "end": v(-14.53, 19.17) * mm});
            skLineSegment(sketch, "E1056", {"start": v(-14.53, 19.17) * mm, "end": v(-14.52, 19.22) * mm});
            skLineSegment(sketch, "E1057", {"start": v(-14.52, 19.22) * mm, "end": v(-14.52, 19.27) * mm});
            skLineSegment(sketch, "E1058", {"start": v(-14.52, 19.27) * mm, "end": v(-14.5, 19.33) * mm});
            skLineSegment(sketch, "E1059", {"start": v(-14.5, 19.33) * mm, "end": v(-14.5, 19.38) * mm});
            skLineSegment(sketch, "E1060", {"start": v(-14.5, 19.38) * mm, "end": v(-14.5, 19.43) * mm});
            skLineSegment(sketch, "E1061", {"start": v(-14.5, 19.43) * mm, "end": v(-14.5, 19.49) * mm});
            skLineSegment(sketch, "E1062", {"start": v(-14.5, 19.49) * mm, "end": v(-14.5, 19.54) * mm});
            skLineSegment(sketch, "E1063", {"start": v(-14.5, 19.54) * mm, "end": v(-14.49, 19.6) * mm});
            skLineSegment(sketch, "E1064", {"start": v(-14.49, 19.6) * mm, "end": v(-14.49, 19.66) * mm});
            skLineSegment(sketch, "E1065", {"start": v(-14.49, 19.66) * mm, "end": v(-14.49, 19.71) * mm});
            skLineSegment(sketch, "E1066", {"start": v(-14.49, 19.71) * mm, "end": v(-14.49, 28.16) * mm});
            skLineSegment(sketch, "E1067", {"start": v(-14.49, 28.16) * mm, "end": v(-14.49, 28.35) * mm});
            skLineSegment(sketch, "E1068", {"start": v(-14.49, 28.35) * mm, "end": v(-14.49, 28.52) * mm});
            skLineSegment(sketch, "E1069", {"start": v(-14.49, 28.52) * mm, "end": v(-14.5, 28.65) * mm});
            skLineSegment(sketch, "E1070", {"start": v(-14.5, 28.65) * mm, "end": v(-14.5, 28.76) * mm});
            skLineSegment(sketch, "E1071", {"start": v(-14.5, 28.76) * mm, "end": v(-14.5, 28.8) * mm});
            skLineSegment(sketch, "E1072", {"start": v(-14.5, 28.8) * mm, "end": v(-14.5, 28.84) * mm});
            skLineSegment(sketch, "E1073", {"start": v(-14.5, 28.84) * mm, "end": v(-14.52, 28.89) * mm});
            skLineSegment(sketch, "E1074", {"start": v(-14.52, 28.89) * mm, "end": v(-14.52, 28.92) * mm});
            skLineSegment(sketch, "E1075", {"start": v(-14.52, 28.92) * mm, "end": v(-14.53, 28.96) * mm});
            skLineSegment(sketch, "E1076", {"start": v(-14.53, 28.96) * mm, "end": v(-14.54, 29) * mm});
            skLineSegment(sketch, "E1077", {"start": v(-14.54, 29) * mm, "end": v(-14.55, 29.03) * mm});
            skLineSegment(sketch, "E1078", {"start": v(-14.55, 29.03) * mm, "end": v(-14.57, 29.07) * mm});
            skLineSegment(sketch, "E1079", {"start": v(-14.57, 29.07) * mm, "end": v(-14.58, 29.09) * mm});
            skLineSegment(sketch, "E1080", {"start": v(-14.58, 29.09) * mm, "end": v(-14.59, 29.11) * mm});
            skLineSegment(sketch, "E1081", {"start": v(-14.59, 29.11) * mm, "end": v(-14.6, 29.13) * mm});
            skLineSegment(sketch, "E1082", {"start": v(-14.6, 29.13) * mm, "end": v(-14.61, 29.16) * mm});
            skLineSegment(sketch, "E1083", {"start": v(-14.61, 29.16) * mm, "end": v(-14.63, 29.18) * mm});
            skLineSegment(sketch, "E1084", {"start": v(-14.63, 29.18) * mm, "end": v(-14.64, 29.2) * mm});
            skLineSegment(sketch, "E1085", {"start": v(-14.64, 29.2) * mm, "end": v(-14.66, 29.22) * mm});
            skLineSegment(sketch, "E1086", {"start": v(-14.66, 29.22) * mm, "end": v(-14.68, 29.24) * mm});
            skLineSegment(sketch, "E1087", {"start": v(-14.68, 29.24) * mm, "end": v(-14.7, 29.26) * mm});
            skLineSegment(sketch, "E1088", {"start": v(-14.7, 29.26) * mm, "end": v(-14.71, 29.27) * mm});
            skLineSegment(sketch, "E1089", {"start": v(-14.71, 29.27) * mm, "end": v(-14.73, 29.3) * mm});
            skLineSegment(sketch, "E1090", {"start": v(-14.73, 29.3) * mm, "end": v(-14.76, 29.3) * mm});
            skLineSegment(sketch, "E1091", {"start": v(-14.76, 29.3) * mm, "end": v(-14.78, 29.32) * mm});
            skLineSegment(sketch, "E1092", {"start": v(-14.78, 29.32) * mm, "end": v(-14.8, 29.34) * mm});
            skLineSegment(sketch, "E1093", {"start": v(-14.8, 29.34) * mm, "end": v(-14.83, 29.35) * mm});
            skLineSegment(sketch, "E1094", {"start": v(-14.83, 29.35) * mm, "end": v(-14.85, 29.37) * mm});
            skLineSegment(sketch, "E1095", {"start": v(-14.85, 29.37) * mm, "end": v(-14.85, 30.26) * mm});
            skLineSegment(sketch, "E1096", {"start": v(-14.85, 30.26) * mm, "end": v(-14.8, 30.25) * mm});
            skLineSegment(sketch, "E1097", {"start": v(-14.8, 30.25) * mm, "end": v(-14.74, 30.24) * mm});
            skLineSegment(sketch, "E1098", {"start": v(-14.74, 30.24) * mm, "end": v(-14.69, 30.22) * mm});
            skLineSegment(sketch, "E1099", {"start": v(-14.69, 30.22) * mm, "end": v(-14.63, 30.2) * mm});
            skLineSegment(sketch, "E1100", {"start": v(-14.63, 30.2) * mm, "end": v(-14.58, 30.17) * mm});
            skLineSegment(sketch, "E1101", {"start": v(-14.58, 30.17) * mm, "end": v(-14.53, 30.15) * mm});
            skLineSegment(sketch, "E1102", {"start": v(-14.53, 30.15) * mm, "end": v(-14.47, 30.12) * mm});
            skLineSegment(sketch, "E1103", {"start": v(-14.47, 30.12) * mm, "end": v(-14.42, 30.09) * mm});
            skLineSegment(sketch, "E1104", {"start": v(-14.42, 30.09) * mm, "end": v(-14.37, 30.06) * mm});
            skLineSegment(sketch, "E1105", {"start": v(-14.37, 30.06) * mm, "end": v(-14.32, 30.02) * mm});
            skLineSegment(sketch, "E1106", {"start": v(-14.32, 30.02) * mm, "end": v(-14.27, 29.98) * mm});
            skLineSegment(sketch, "E1107", {"start": v(-14.27, 29.98) * mm, "end": v(-14.22, 29.94) * mm});
            skLineSegment(sketch, "E1108", {"start": v(-14.22, 29.94) * mm, "end": v(-14.16, 29.9) * mm});
            skLineSegment(sketch, "E1109", {"start": v(-14.16, 29.9) * mm, "end": v(-14.11, 29.85) * mm});
            skLineSegment(sketch, "E1110", {"start": v(-14.11, 29.85) * mm, "end": v(-14.07, 29.8) * mm});
            skLineSegment(sketch, "E1111", {"start": v(-14.07, 29.8) * mm, "end": v(-14.02, 29.75) * mm});
            skLineSegment(sketch, "E1112", {"start": v(-14.02, 29.75) * mm, "end": v(-13.97, 29.7) * mm});
            skLineSegment(sketch, "E1113", {"start": v(-13.97, 29.7) * mm, "end": v(-13.92, 29.64) * mm});
            skLineSegment(sketch, "E1114", {"start": v(-13.92, 29.64) * mm, "end": v(-13.87, 29.58) * mm});
            skLineSegment(sketch, "E1115", {"start": v(-13.87, 29.58) * mm, "end": v(-13.83, 29.52) * mm});
            skLineSegment(sketch, "E1116", {"start": v(-13.83, 29.52) * mm, "end": v(-13.78, 29.45) * mm});
            skLineSegment(sketch, "E1117", {"start": v(-13.78, 29.45) * mm, "end": v(-13.73, 29.38) * mm});
            skLineSegment(sketch, "E1118", {"start": v(-13.73, 29.38) * mm, "end": v(-13.69, 29.32) * mm});
            skLineSegment(sketch, "E1119", {"start": v(-13.69, 29.32) * mm, "end": v(-13.65, 29.25) * mm});
            skLineSegment(sketch, "E1120", {"start": v(-13.65, 29.25) * mm, "end": v(-13.6, 29.17) * mm});
            skLineSegment(sketch, "E1121", {"start": v(-13.6, 29.17) * mm, "end": v(-13.56, 29.1) * mm});
            skLineSegment(sketch, "E1122", {"start": v(-13.56, 29.1) * mm, "end": v(-13.52, 29.02) * mm});
            skLineSegment(sketch, "E1123", {"start": v(-13.52, 29.02) * mm, "end": v(-13.48, 28.94) * mm});
            skLineSegment(sketch, "E1124", {"start": v(-13.48, 28.94) * mm, "end": v(-13.44, 28.85) * mm});
            skLineSegment(sketch, "E1125", {"start": v(-13.44, 28.85) * mm, "end": v(-13.4, 28.77) * mm});
            skLineSegment(sketch, "E1126", {"start": v(-13.4, 28.77) * mm, "end": v(-13.36, 28.68) * mm});
            skLineSegment(sketch, "E1127", {"start": v(-13.36, 28.68) * mm, "end": v(-13.32, 28.59) * mm});
            skLineSegment(sketch, "E1128", {"start": v(-13.32, 28.59) * mm, "end": v(-13.27, 28.49) * mm});
            skLineSegment(sketch, "E1129", {"start": v(-13.27, 28.49) * mm, "end": v(-13.23, 28.38) * mm});
            skLineSegment(sketch, "E1130", {"start": v(-13.23, 28.38) * mm, "end": v(-13.2, 28.27) * mm});
            skLineSegment(sketch, "E1131", {"start": v(-13.2, 28.27) * mm, "end": v(-13.15, 28.16) * mm});
            skLineSegment(sketch, "E1132", {"start": v(-13.15, 28.16) * mm, "end": v(-13.12, 28.04) * mm});
            skLineSegment(sketch, "E1133", {"start": v(-13.12, 28.04) * mm, "end": v(-13.08, 27.92) * mm});
            skLineSegment(sketch, "E1134", {"start": v(-13.08, 27.92) * mm, "end": v(-13.05, 27.8) * mm});
            skLineSegment(sketch, "E1135", {"start": v(-13.05, 27.8) * mm, "end": v(-13.01, 27.67) * mm});
            skLineSegment(sketch, "E1136", {"start": v(-13.01, 27.67) * mm, "end": v(-12.98, 27.54) * mm});
            skLineSegment(sketch, "E1137", {"start": v(-12.98, 27.54) * mm, "end": v(-12.95, 27.4) * mm});
            skLineSegment(sketch, "E1138", {"start": v(-12.95, 27.4) * mm, "end": v(-12.92, 27.27) * mm});
            skLineSegment(sketch, "E1139", {"start": v(-12.92, 27.27) * mm, "end": v(-12.89, 27.12) * mm});
            skLineSegment(sketch, "E1140", {"start": v(-12.89, 27.12) * mm, "end": v(-12.86, 26.98) * mm});
            skLineSegment(sketch, "E1141", {"start": v(-12.86, 26.98) * mm, "end": v(-12.83, 26.83) * mm});
            skLineSegment(sketch, "E1142", {"start": v(-12.83, 26.83) * mm, "end": v(-12.8, 26.68) * mm});
            skLineSegment(sketch, "E1143", {"start": v(-12.8, 26.68) * mm, "end": v(-12.78, 26.52) * mm});
            skLineSegment(sketch, "E1144", {"start": v(-12.78, 26.52) * mm, "end": v(-12.76, 26.36) * mm});
            skLineSegment(sketch, "E1145", {"start": v(-12.76, 26.36) * mm, "end": v(-12.74, 26.2) * mm});
            skLineSegment(sketch, "E1146", {"start": v(-12.74, 26.2) * mm, "end": v(-12.72, 26.04) * mm});
            skLineSegment(sketch, "E1147", {"start": v(-12.72, 26.04) * mm, "end": v(-12.7, 25.88) * mm});
            skLineSegment(sketch, "E1148", {"start": v(-12.7, 25.88) * mm, "end": v(-12.68, 25.71) * mm});
            skLineSegment(sketch, "E1149", {"start": v(-12.68, 25.71) * mm, "end": v(-12.67, 25.54) * mm});
            skLineSegment(sketch, "E1150", {"start": v(-12.67, 25.54) * mm, "end": v(-12.66, 25.38) * mm});
            skLineSegment(sketch, "E1151", {"start": v(-12.66, 25.38) * mm, "end": v(-12.64, 25.2) * mm});
            skLineSegment(sketch, "E1152", {"start": v(-12.64, 25.2) * mm, "end": v(-12.63, 25.03) * mm});
            skLineSegment(sketch, "E1153", {"start": v(-12.63, 25.03) * mm, "end": v(-12.62, 24.86) * mm});
            skLineSegment(sketch, "E1154", {"start": v(-12.62, 24.86) * mm, "end": v(-12.61, 24.69) * mm});
            skLineSegment(sketch, "E1155", {"start": v(-12.61, 24.69) * mm, "end": v(-12.6, 24.5) * mm});
            skLineSegment(sketch, "E1156", {"start": v(-12.6, 24.5) * mm, "end": v(-12.6, 24.33) * mm});
            skLineSegment(sketch, "E1157", {"start": v(-12.6, 24.33) * mm, "end": v(-12.6, 24.15) * mm});
            skLineSegment(sketch, "E1158", {"start": v(-12.6, 24.15) * mm, "end": v(-12.6, 23.97) * mm});
            skLineSegment(sketch, "E1159", {"start": v(-12.6, 23.97) * mm, "end": v(-12.6, 23.79) * mm});
            skLineSegment(sketch, "E1160", {"start": v(-12.6, 23.79) * mm, "end": v(-12.6, 23.59) * mm});
            skLineSegment(sketch, "E1161", {"start": v(-12.6, 23.59) * mm, "end": v(-12.6, 23.4) * mm});
            skLineSegment(sketch, "E1162", {"start": v(-12.6, 23.4) * mm, "end": v(-12.6, 23.2) * mm});
            skLineSegment(sketch, "E1163", {"start": v(-12.6, 23.2) * mm, "end": v(-12.6, 23.02) * mm});
            skLineSegment(sketch, "E1164", {"start": v(-12.6, 23.02) * mm, "end": v(-12.62, 22.83) * mm});
            skLineSegment(sketch, "E1165", {"start": v(-12.62, 22.83) * mm, "end": v(-12.63, 22.65) * mm});
            skLineSegment(sketch, "E1166", {"start": v(-12.63, 22.65) * mm, "end": v(-12.64, 22.47) * mm});
            skLineSegment(sketch, "E1167", {"start": v(-12.64, 22.47) * mm, "end": v(-12.65, 22.3) * mm});
            skLineSegment(sketch, "E1168", {"start": v(-12.65, 22.3) * mm, "end": v(-12.67, 22.12) * mm});
            skLineSegment(sketch, "E1169", {"start": v(-12.67, 22.12) * mm, "end": v(-12.68, 21.95) * mm});
            skLineSegment(sketch, "E1170", {"start": v(-12.68, 21.95) * mm, "end": v(-12.7, 21.78) * mm});
            skLineSegment(sketch, "E1171", {"start": v(-12.7, 21.78) * mm, "end": v(-12.72, 21.6) * mm});
            skLineSegment(sketch, "E1172", {"start": v(-12.72, 21.6) * mm, "end": v(-12.75, 21.44) * mm});
            skLineSegment(sketch, "E1173", {"start": v(-12.75, 21.44) * mm, "end": v(-12.77, 21.28) * mm});
            skLineSegment(sketch, "E1174", {"start": v(-12.77, 21.28) * mm, "end": v(-12.8, 21.12) * mm});
            skLineSegment(sketch, "E1175", {"start": v(-12.8, 21.12) * mm, "end": v(-12.82, 20.97) * mm});
            skLineSegment(sketch, "E1176", {"start": v(-12.82, 20.97) * mm, "end": v(-12.85, 20.81) * mm});
            skLineSegment(sketch, "E1177", {"start": v(-12.85, 20.81) * mm, "end": v(-12.89, 20.66) * mm});
            skLineSegment(sketch, "E1178", {"start": v(-12.89, 20.66) * mm, "end": v(-12.92, 20.51) * mm});
            skLineSegment(sketch, "E1179", {"start": v(-12.92, 20.51) * mm, "end": v(-12.95, 20.36) * mm});
            skLineSegment(sketch, "E1180", {"start": v(-12.95, 20.36) * mm, "end": v(-13, 20.22) * mm});
            skLineSegment(sketch, "E1181", {"start": v(-13, 20.22) * mm, "end": v(-13.03, 20.08) * mm});
            skLineSegment(sketch, "E1182", {"start": v(-13.03, 20.08) * mm, "end": v(-13.07, 19.94) * mm});
            skLineSegment(sketch, "E1183", {"start": v(-13.07, 19.94) * mm, "end": v(-13.11, 19.8) * mm});
            skLineSegment(sketch, "E1184", {"start": v(-13.11, 19.8) * mm, "end": v(-13.16, 19.67) * mm});
            skLineSegment(sketch, "E1185", {"start": v(-13.16, 19.67) * mm, "end": v(-13.2, 19.54) * mm});
            skLineSegment(sketch, "E1186", {"start": v(-13.2, 19.54) * mm, "end": v(-13.25, 19.41) * mm});
            skLineSegment(sketch, "E1187", {"start": v(-13.25, 19.41) * mm, "end": v(-13.3, 19.28) * mm});
            skLineSegment(sketch, "E1188", {"start": v(-13.3, 19.28) * mm, "end": v(-13.35, 19.16) * mm});
            skLineSegment(sketch, "E1189", {"start": v(-13.35, 19.16) * mm, "end": v(-13.4, 19.04) * mm});
            skLineSegment(sketch, "E1190", {"start": v(-13.4, 19.04) * mm, "end": v(-13.46, 18.92) * mm});
            skLineSegment(sketch, "E1191", {"start": v(-13.46, 18.92) * mm, "end": v(-13.51, 18.8) * mm});
            skLineSegment(sketch, "E1192", {"start": v(-13.51, 18.8) * mm, "end": v(-13.55, 18.73) * mm});
            skLineSegment(sketch, "E1193", {"start": v(-13.55, 18.73) * mm, "end": v(-13.6, 18.65) * mm});
            skLineSegment(sketch, "E1194", {"start": v(-13.6, 18.65) * mm, "end": v(-13.64, 18.58) * mm});
            skLineSegment(sketch, "E1195", {"start": v(-13.64, 18.58) * mm, "end": v(-13.68, 18.5) * mm});
            skLineSegment(sketch, "E1196", {"start": v(-13.68, 18.5) * mm, "end": v(-13.72, 18.43) * mm});
            skLineSegment(sketch, "E1197", {"start": v(-13.72, 18.43) * mm, "end": v(-13.76, 18.37) * mm});
            skLineSegment(sketch, "E1198", {"start": v(-13.76, 18.37) * mm, "end": v(-13.8, 18.3) * mm});
            skLineSegment(sketch, "E1199", {"start": v(-13.8, 18.3) * mm, "end": v(-13.85, 18.24) * mm});
            skLineSegment(sketch, "E1200", {"start": v(-13.85, 18.24) * mm, "end": v(-13.9, 18.18) * mm});
            skLineSegment(sketch, "E1201", {"start": v(-13.9, 18.18) * mm, "end": v(-13.94, 18.12) * mm});
            skLineSegment(sketch, "E1202", {"start": v(-13.94, 18.12) * mm, "end": v(-13.98, 18.06) * mm});
            skLineSegment(sketch, "E1203", {"start": v(-13.98, 18.06) * mm, "end": v(-14.03, 18) * mm});
            skLineSegment(sketch, "E1204", {"start": v(-14.03, 18) * mm, "end": v(-14.07, 17.96) * mm});
            skLineSegment(sketch, "E1205", {"start": v(-14.07, 17.96) * mm, "end": v(-14.12, 17.9) * mm});
            skLineSegment(sketch, "E1206", {"start": v(-14.12, 17.9) * mm, "end": v(-14.17, 17.86) * mm});
            skLineSegment(sketch, "E1207", {"start": v(-14.17, 17.86) * mm, "end": v(-14.21, 17.81) * mm});
            skLineSegment(sketch, "E1208", {"start": v(-14.21, 17.81) * mm, "end": v(-14.26, 17.77) * mm});
            skLineSegment(sketch, "E1209", {"start": v(-14.26, 17.77) * mm, "end": v(-14.3, 17.73) * mm});
            skLineSegment(sketch, "E1210", {"start": v(-14.3, 17.73) * mm, "end": v(-14.36, 17.7) * mm});
            skLineSegment(sketch, "E1211", {"start": v(-14.36, 17.7) * mm, "end": v(-14.4, 17.66) * mm});
            skLineSegment(sketch, "E1212", {"start": v(-14.4, 17.66) * mm, "end": v(-14.45, 17.63) * mm});
            skLineSegment(sketch, "E1213", {"start": v(-14.45, 17.63) * mm, "end": v(-14.5, 17.6) * mm});
            skLineSegment(sketch, "E1214", {"start": v(-14.5, 17.6) * mm, "end": v(-14.54, 17.57) * mm});
            skLineSegment(sketch, "E1215", {"start": v(-14.54, 17.57) * mm, "end": v(-14.6, 17.55) * mm});
            skLineSegment(sketch, "E1216", {"start": v(-14.6, 17.55) * mm, "end": v(-14.64, 17.53) * mm});
            skLineSegment(sketch, "E1217", {"start": v(-14.64, 17.53) * mm, "end": v(-14.68, 17.51) * mm});
            skLineSegment(sketch, "E1218", {"start": v(-14.68, 17.51) * mm, "end": v(-14.73, 17.5) * mm});
            skLineSegment(sketch, "E1219", {"start": v(-14.73, 17.5) * mm, "end": v(-14.78, 17.48) * mm});
            skLineSegment(sketch, "E1220", {"start": v(-14.78, 17.48) * mm, "end": v(-14.82, 17.47) * mm});
            skLineSegment(sketch, "E1221", {"start": v(-14.82, 17.47) * mm, "end": v(-14.87, 17.47) * mm});
            skLineSegment(sketch, "E1222", {"start": v(-14.87, 17.47) * mm, "end": v(-14.92, 17.46) * mm});
            skLineSegment(sketch, "E1223", {"start": v(-14.92, 17.46) * mm, "end": v(-14.96, 17.46) * mm});
            skLineSegment(sketch, "E1224", {"start": v(-15.31, 18.39) * mm, "end": v(-15.31, 17.46) * mm});
            skLineSegment(sketch, "E1225", {"start": v(-15.31, 17.46) * mm, "end": v(-15.37, 17.46) * mm});
            skLineSegment(sketch, "E1226", {"start": v(-15.37, 17.46) * mm, "end": v(-15.43, 17.47) * mm});
            skLineSegment(sketch, "E1227", {"start": v(-15.43, 17.47) * mm, "end": v(-15.48, 17.48) * mm});
            skLineSegment(sketch, "E1228", {"start": v(-15.48, 17.48) * mm, "end": v(-15.54, 17.49) * mm});
            skLineSegment(sketch, "E1229", {"start": v(-15.54, 17.49) * mm, "end": v(-15.6, 17.5) * mm});
            skLineSegment(sketch, "E1230", {"start": v(-15.6, 17.5) * mm, "end": v(-15.66, 17.52) * mm});
            skLineSegment(sketch, "E1231", {"start": v(-15.66, 17.52) * mm, "end": v(-15.72, 17.55) * mm});
            skLineSegment(sketch, "E1232", {"start": v(-15.72, 17.55) * mm, "end": v(-15.78, 17.57) * mm});
            skLineSegment(sketch, "E1233", {"start": v(-15.78, 17.57) * mm, "end": v(-15.83, 17.6) * mm});
            skLineSegment(sketch, "E1234", {"start": v(-15.83, 17.6) * mm, "end": v(-15.9, 17.63) * mm});
            skLineSegment(sketch, "E1235", {"start": v(-15.9, 17.63) * mm, "end": v(-15.95, 17.67) * mm});
            skLineSegment(sketch, "E1236", {"start": v(-15.95, 17.67) * mm, "end": v(-16.01, 17.7) * mm});
            skLineSegment(sketch, "E1237", {"start": v(-16.01, 17.7) * mm, "end": v(-16.07, 17.75) * mm});
            skLineSegment(sketch, "E1238", {"start": v(-16.07, 17.75) * mm, "end": v(-16.13, 17.8) * mm});
            skLineSegment(sketch, "E1239", {"start": v(-16.13, 17.8) * mm, "end": v(-16.19, 17.85) * mm});
            skLineSegment(sketch, "E1240", {"start": v(-16.19, 17.85) * mm, "end": v(-16.25, 17.9) * mm});
            skLineSegment(sketch, "E1241", {"start": v(-16.25, 17.9) * mm, "end": v(-16.3, 17.95) * mm});
            skLineSegment(sketch, "E1242", {"start": v(-16.3, 17.95) * mm, "end": v(-16.34, 18) * mm});
            skLineSegment(sketch, "E1243", {"start": v(-16.34, 18) * mm, "end": v(-16.4, 18.05) * mm});
            skLineSegment(sketch, "E1244", {"start": v(-16.4, 18.05) * mm, "end": v(-16.44, 18.1) * mm});
            skLineSegment(sketch, "E1245", {"start": v(-16.44, 18.1) * mm, "end": v(-16.48, 18.16) * mm});
            skLineSegment(sketch, "E1246", {"start": v(-16.48, 18.16) * mm, "end": v(-16.52, 18.21) * mm});
            skLineSegment(sketch, "E1247", {"start": v(-16.52, 18.21) * mm, "end": v(-16.56, 18.27) * mm});
            skLineSegment(sketch, "E1248", {"start": v(-16.56, 18.27) * mm, "end": v(-16.6, 18.33) * mm});
            skLineSegment(sketch, "E1249", {"start": v(-16.6, 18.33) * mm, "end": v(-16.64, 18.4) * mm});
            skLineSegment(sketch, "E1250", {"start": v(-16.64, 18.4) * mm, "end": v(-16.68, 18.46) * mm});
            skLineSegment(sketch, "E1251", {"start": v(-16.68, 18.46) * mm, "end": v(-16.72, 18.52) * mm});
            skLineSegment(sketch, "E1252", {"start": v(-16.72, 18.52) * mm, "end": v(-16.75, 18.59) * mm});
            skLineSegment(sketch, "E1253", {"start": v(-16.75, 18.59) * mm, "end": v(-16.78, 18.66) * mm});
            skLineSegment(sketch, "E1254", {"start": v(-16.78, 18.66) * mm, "end": v(-16.81, 18.73) * mm});
            skLineSegment(sketch, "E1255", {"start": v(-16.81, 18.73) * mm, "end": v(-16.84, 18.8) * mm});
            skLineSegment(sketch, "E1256", {"start": v(-16.84, 18.8) * mm, "end": v(-16.87, 18.88) * mm});
            skLineSegment(sketch, "E1257", {"start": v(-16.87, 18.88) * mm, "end": v(-16.9, 18.95) * mm});
            skLineSegment(sketch, "E1258", {"start": v(-16.9, 18.95) * mm, "end": v(-16.93, 19.03) * mm});
            skLineSegment(sketch, "E1259", {"start": v(-16.93, 19.03) * mm, "end": v(-16.95, 19.1) * mm});
            skLineSegment(sketch, "E1260", {"start": v(-16.95, 19.1) * mm, "end": v(-16.97, 19.18) * mm});
            skLineSegment(sketch, "E1261", {"start": v(-16.97, 19.18) * mm, "end": v(-17, 19.26) * mm});
            skLineSegment(sketch, "E1262", {"start": v(-17, 19.26) * mm, "end": v(-17.01, 19.34) * mm});
            skLineSegment(sketch, "E1263", {"start": v(-17.01, 19.34) * mm, "end": v(-17.03, 19.42) * mm});
            skLineSegment(sketch, "E1264", {"start": v(-17.03, 19.42) * mm, "end": v(-17.04, 19.5) * mm});
            skLineSegment(sketch, "E1265", {"start": v(-17.04, 19.5) * mm, "end": v(-17.06, 19.58) * mm});
            skLineSegment(sketch, "E1266", {"start": v(-17.06, 19.58) * mm, "end": v(-17.07, 19.66) * mm});
            skLineSegment(sketch, "E1267", {"start": v(-17.07, 19.66) * mm, "end": v(-17.08, 19.75) * mm});
            skLineSegment(sketch, "E1268", {"start": v(-17.08, 19.75) * mm, "end": v(-17.09, 19.83) * mm});
            skLineSegment(sketch, "E1269", {"start": v(-17.09, 19.83) * mm, "end": v(-17.1, 19.91) * mm});
            skLineSegment(sketch, "E1270", {"start": v(-17.1, 19.91) * mm, "end": v(-17.1, 20) * mm});
            skLineSegment(sketch, "E1271", {"start": v(-17.1, 20) * mm, "end": v(-17.1, 20.08) * mm});
            skLineSegment(sketch, "E1272", {"start": v(-17.1, 20.08) * mm, "end": v(-17.1, 20.17) * mm});
            skLineSegment(sketch, "E1273", {"start": v(-17.1, 20.17) * mm, "end": v(-17.1, 20.26) * mm});
            skLineSegment(sketch, "E1274", {"start": v(-17.1, 20.26) * mm, "end": v(-17.1, 20.36) * mm});
            skLineSegment(sketch, "E1275", {"start": v(-17.1, 20.36) * mm, "end": v(-17.1, 20.45) * mm});
            skLineSegment(sketch, "E1276", {"start": v(-17.1, 20.45) * mm, "end": v(-17.08, 20.53) * mm});
            skLineSegment(sketch, "E1277", {"start": v(-17.08, 20.53) * mm, "end": v(-17.07, 20.62) * mm});
            skLineSegment(sketch, "E1278", {"start": v(-17.07, 20.62) * mm, "end": v(-17.06, 20.7) * mm});
            skLineSegment(sketch, "E1279", {"start": v(-17.06, 20.7) * mm, "end": v(-17.05, 20.79) * mm});
            skLineSegment(sketch, "E1280", {"start": v(-17.05, 20.79) * mm, "end": v(-17.03, 20.87) * mm});
            skLineSegment(sketch, "E1281", {"start": v(-17.03, 20.87) * mm, "end": v(-17.02, 20.95) * mm});
            skLineSegment(sketch, "E1282", {"start": v(-17.02, 20.95) * mm, "end": v(-17, 21.02) * mm});
            skLineSegment(sketch, "E1283", {"start": v(-17, 21.02) * mm, "end": v(-16.98, 21.1) * mm});
            skLineSegment(sketch, "E1284", {"start": v(-16.98, 21.1) * mm, "end": v(-16.95, 21.17) * mm});
            skLineSegment(sketch, "E1285", {"start": v(-16.95, 21.17) * mm, "end": v(-16.93, 21.24) * mm});
            skLineSegment(sketch, "E1286", {"start": v(-16.93, 21.24) * mm, "end": v(-16.9, 21.31) * mm});
            skLineSegment(sketch, "E1287", {"start": v(-16.9, 21.31) * mm, "end": v(-16.87, 21.38) * mm});
            skLineSegment(sketch, "E1288", {"start": v(-16.87, 21.38) * mm, "end": v(-16.84, 21.44) * mm});
            skLineSegment(sketch, "E1289", {"start": v(-16.84, 21.44) * mm, "end": v(-16.8, 21.5) * mm});
            skLineSegment(sketch, "E1290", {"start": v(-16.8, 21.5) * mm, "end": v(-16.77, 21.56) * mm});
            skLineSegment(sketch, "E1291", {"start": v(-16.77, 21.56) * mm, "end": v(-16.74, 21.62) * mm});
            skLineSegment(sketch, "E1292", {"start": v(-16.74, 21.62) * mm, "end": v(-16.7, 21.67) * mm});
            skLineSegment(sketch, "E1293", {"start": v(-16.7, 21.67) * mm, "end": v(-16.66, 21.71) * mm});
            skLineSegment(sketch, "E1294", {"start": v(-16.66, 21.71) * mm, "end": v(-16.62, 21.75) * mm});
            skLineSegment(sketch, "E1295", {"start": v(-16.62, 21.75) * mm, "end": v(-16.6, 21.77) * mm});
            skLineSegment(sketch, "E1296", {"start": v(-16.6, 21.77) * mm, "end": v(-16.59, 21.8) * mm});
            skLineSegment(sketch, "E1297", {"start": v(-16.59, 21.8) * mm, "end": v(-16.57, 21.81) * mm});
            skLineSegment(sketch, "E1298", {"start": v(-16.57, 21.81) * mm, "end": v(-16.55, 21.83) * mm});
            skLineSegment(sketch, "E1299", {"start": v(-16.55, 21.83) * mm, "end": v(-16.52, 21.84) * mm});
            skLineSegment(sketch, "E1300", {"start": v(-16.52, 21.84) * mm, "end": v(-16.5, 21.86) * mm});
            skLineSegment(sketch, "E1301", {"start": v(-16.5, 21.86) * mm, "end": v(-16.48, 21.87) * mm});
            skLineSegment(sketch, "E1302", {"start": v(-16.48, 21.87) * mm, "end": v(-16.46, 21.88) * mm});
            skLineSegment(sketch, "E1303", {"start": v(-16.46, 21.88) * mm, "end": v(-16.44, 21.9) * mm});
            skLineSegment(sketch, "E1304", {"start": v(-16.44, 21.9) * mm, "end": v(-16.42, 21.9) * mm});
            skLineSegment(sketch, "E1305", {"start": v(-16.42, 21.9) * mm, "end": v(-16.4, 21.91) * mm});
            skLineSegment(sketch, "E1306", {"start": v(-16.4, 21.91) * mm, "end": v(-16.37, 21.92) * mm});
            skLineSegment(sketch, "E1307", {"start": v(-16.37, 21.92) * mm, "end": v(-16.35, 21.93) * mm});
            skLineSegment(sketch, "E1308", {"start": v(-16.35, 21.93) * mm, "end": v(-16.33, 21.94) * mm});
            skLineSegment(sketch, "E1309", {"start": v(-16.33, 21.94) * mm, "end": v(-16.3, 21.94) * mm});
            skLineSegment(sketch, "E1310", {"start": v(-16.3, 21.94) * mm, "end": v(-16.28, 21.95) * mm});
            skLineSegment(sketch, "E1311", {"start": v(-16.28, 21.95) * mm, "end": v(-16.26, 21.95) * mm});
            skLineSegment(sketch, "E1312", {"start": v(-16.26, 21.95) * mm, "end": v(-16.23, 21.95) * mm});
            skLineSegment(sketch, "E1313", {"start": v(-16.23, 21.95) * mm, "end": v(-16.21, 21.95) * mm});
            skLineSegment(sketch, "E1314", {"start": v(-16.21, 21.95) * mm, "end": v(-16.19, 21.95) * mm});
            skLineSegment(sketch, "E1315", {"start": v(-16.19, 21.95) * mm, "end": v(-16.14, 21.95) * mm});
            skLineSegment(sketch, "E1316", {"start": v(-16.14, 21.95) * mm, "end": v(-16.1, 21.95) * mm});
            skLineSegment(sketch, "E1317", {"start": v(-16.1, 21.95) * mm, "end": v(-16.08, 21.94) * mm});
            skLineSegment(sketch, "E1318", {"start": v(-16.08, 21.94) * mm, "end": v(-16.06, 21.94) * mm});
            skLineSegment(sketch, "E1319", {"start": v(-16.06, 21.94) * mm, "end": v(-16.02, 21.93) * mm});
            skLineSegment(sketch, "E1320", {"start": v(-16.02, 21.93) * mm, "end": v(-15.98, 21.91) * mm});
            skLineSegment(sketch, "E1321", {"start": v(-15.98, 21.91) * mm, "end": v(-15.94, 21.9) * mm});
            skLineSegment(sketch, "E1322", {"start": v(-15.94, 21.9) * mm, "end": v(-15.9, 21.87) * mm});
            skLineSegment(sketch, "E1323", {"start": v(-15.9, 21.87) * mm, "end": v(-15.87, 21.84) * mm});
            skLineSegment(sketch, "E1324", {"start": v(-15.87, 21.84) * mm, "end": v(-15.83, 21.81) * mm});
            skLineSegment(sketch, "E1325", {"start": v(-15.83, 21.81) * mm, "end": v(-15.8, 21.78) * mm});
            skLineSegment(sketch, "E1326", {"start": v(-15.8, 21.78) * mm, "end": v(-15.76, 21.75) * mm});
            skLineSegment(sketch, "E1327", {"start": v(-15.76, 21.75) * mm, "end": v(-15.73, 21.7) * mm});
            skLineSegment(sketch, "E1328", {"start": v(-15.73, 21.7) * mm, "end": v(-15.7, 21.66) * mm});
            skLineSegment(sketch, "E1329", {"start": v(-15.7, 21.66) * mm, "end": v(-15.66, 21.62) * mm});
            skLineSegment(sketch, "E1330", {"start": v(-15.66, 21.62) * mm, "end": v(-15.63, 21.56) * mm});
            skLineSegment(sketch, "E1331", {"start": v(-15.63, 21.56) * mm, "end": v(-15.6, 21.51) * mm});
            skLineSegment(sketch, "E1332", {"start": v(-15.6, 21.51) * mm, "end": v(-15.57, 21.45) * mm});
            skLineSegment(sketch, "E1333", {"start": v(-15.57, 21.45) * mm, "end": v(-15.54, 21.4) * mm});
            skLineSegment(sketch, "E1334", {"start": v(-15.54, 21.4) * mm, "end": v(-15.51, 21.34) * mm});
            skLineSegment(sketch, "E1335", {"start": v(-15.51, 21.34) * mm, "end": v(-15.5, 21.28) * mm});
            skLineSegment(sketch, "E1336", {"start": v(-15.5, 21.28) * mm, "end": v(-15.47, 21.22) * mm});
            skLineSegment(sketch, "E1337", {"start": v(-15.47, 21.22) * mm, "end": v(-15.45, 21.15) * mm});
            skLineSegment(sketch, "E1338", {"start": v(-15.45, 21.15) * mm, "end": v(-15.43, 21.09) * mm});
            skLineSegment(sketch, "E1339", {"start": v(-15.43, 21.09) * mm, "end": v(-15.41, 21.02) * mm});
            skLineSegment(sketch, "E1340", {"start": v(-15.41, 21.02) * mm, "end": v(-15.4, 20.95) * mm});
            skLineSegment(sketch, "E1341", {"start": v(-15.4, 20.95) * mm, "end": v(-15.39, 20.88) * mm});
            skLineSegment(sketch, "E1342", {"start": v(-15.39, 20.88) * mm, "end": v(-15.38, 20.81) * mm});
            skLineSegment(sketch, "E1343", {"start": v(-15.38, 20.81) * mm, "end": v(-15.37, 20.74) * mm});
            skLineSegment(sketch, "E1344", {"start": v(-15.37, 20.74) * mm, "end": v(-15.36, 20.67) * mm});
            skLineSegment(sketch, "E1345", {"start": v(-15.36, 20.67) * mm, "end": v(-15.36, 20.6) * mm});
            skLineSegment(sketch, "E1346", {"start": v(-15.36, 20.6) * mm, "end": v(-15.35, 20.51) * mm});
            skLineSegment(sketch, "E1347", {"start": v(-15.35, 20.51) * mm, "end": v(-15.35, 20.44) * mm});
            skLineSegment(sketch, "E1348", {"start": v(-15.35, 20.44) * mm, "end": v(-15.35, 20.33) * mm});
            skLineSegment(sketch, "E1349", {"start": v(-15.35, 20.33) * mm, "end": v(-15.36, 20.23) * mm});
            skLineSegment(sketch, "E1350", {"start": v(-15.36, 20.23) * mm, "end": v(-15.36, 20.18) * mm});
            skLineSegment(sketch, "E1351", {"start": v(-15.36, 20.18) * mm, "end": v(-15.37, 20.13) * mm});
            skLineSegment(sketch, "E1352", {"start": v(-15.37, 20.13) * mm, "end": v(-15.37, 20.08) * mm});
            skLineSegment(sketch, "E1353", {"start": v(-15.37, 20.08) * mm, "end": v(-15.38, 20.04) * mm});
            skLineSegment(sketch, "E1354", {"start": v(-15.38, 20.04) * mm, "end": v(-15.39, 20) * mm});
            skLineSegment(sketch, "E1355", {"start": v(-15.39, 20) * mm, "end": v(-15.4, 19.95) * mm});
            skLineSegment(sketch, "E1356", {"start": v(-15.4, 19.95) * mm, "end": v(-15.4, 19.9) * mm});
            skLineSegment(sketch, "E1357", {"start": v(-15.4, 19.9) * mm, "end": v(-15.41, 19.86) * mm});
            skLineSegment(sketch, "E1358", {"start": v(-15.41, 19.86) * mm, "end": v(-15.42, 19.82) * mm});
            skLineSegment(sketch, "E1359", {"start": v(-15.42, 19.82) * mm, "end": v(-15.43, 19.78) * mm});
            skLineSegment(sketch, "E1360", {"start": v(-15.43, 19.78) * mm, "end": v(-15.45, 19.74) * mm});
            skLineSegment(sketch, "E1361", {"start": v(-15.45, 19.74) * mm, "end": v(-15.46, 19.7) * mm});
            skLineSegment(sketch, "E1362", {"start": v(-15.46, 19.7) * mm, "end": v(-15.6, 19.28) * mm});
            skLineSegment(sketch, "E1363", {"start": v(-15.6, 19.28) * mm, "end": v(-15.62, 19.24) * mm});
            skLineSegment(sketch, "E1364", {"start": v(-15.62, 19.24) * mm, "end": v(-15.64, 19.2) * mm});
            skLineSegment(sketch, "E1365", {"start": v(-15.64, 19.2) * mm, "end": v(-15.65, 19.16) * mm});
            skLineSegment(sketch, "E1366", {"start": v(-15.65, 19.16) * mm, "end": v(-15.65, 19.12) * mm});
            skLineSegment(sketch, "E1367", {"start": v(-15.65, 19.12) * mm, "end": v(-15.66, 19.08) * mm});
            skLineSegment(sketch, "E1368", {"start": v(-15.66, 19.08) * mm, "end": v(-15.67, 19.04) * mm});
            skLineSegment(sketch, "E1369", {"start": v(-15.67, 19.04) * mm, "end": v(-15.67, 19) * mm});
            skLineSegment(sketch, "E1370", {"start": v(-15.67, 19) * mm, "end": v(-15.67, 18.96) * mm});
            skLineSegment(sketch, "E1371", {"start": v(-15.67, 18.96) * mm, "end": v(-15.67, 18.93) * mm});
            skLineSegment(sketch, "E1372", {"start": v(-15.67, 18.93) * mm, "end": v(-15.67, 18.9) * mm});
            skLineSegment(sketch, "E1373", {"start": v(-15.67, 18.9) * mm, "end": v(-15.66, 18.87) * mm});
            skLineSegment(sketch, "E1374", {"start": v(-15.66, 18.87) * mm, "end": v(-15.66, 18.83) * mm});
            skLineSegment(sketch, "E1375", {"start": v(-15.66, 18.83) * mm, "end": v(-15.66, 18.8) * mm});
            skLineSegment(sketch, "E1376", {"start": v(-15.66, 18.8) * mm, "end": v(-15.65, 18.77) * mm});
            skLineSegment(sketch, "E1377", {"start": v(-15.65, 18.77) * mm, "end": v(-15.64, 18.74) * mm});
            skLineSegment(sketch, "E1378", {"start": v(-15.64, 18.74) * mm, "end": v(-15.63, 18.72) * mm});
            skLineSegment(sketch, "E1379", {"start": v(-15.63, 18.72) * mm, "end": v(-15.62, 18.69) * mm});
            skLineSegment(sketch, "E1380", {"start": v(-15.62, 18.69) * mm, "end": v(-15.61, 18.66) * mm});
            skLineSegment(sketch, "E1381", {"start": v(-15.61, 18.66) * mm, "end": v(-15.6, 18.63) * mm});
            skLineSegment(sketch, "E1382", {"start": v(-15.6, 18.63) * mm, "end": v(-15.59, 18.6) * mm});
            skLineSegment(sketch, "E1383", {"start": v(-15.59, 18.6) * mm, "end": v(-15.57, 18.58) * mm});
            skLineSegment(sketch, "E1384", {"start": v(-15.57, 18.58) * mm, "end": v(-15.56, 18.55) * mm});
            skLineSegment(sketch, "E1385", {"start": v(-15.56, 18.55) * mm, "end": v(-15.54, 18.53) * mm});
            skLineSegment(sketch, "E1386", {"start": v(-15.54, 18.53) * mm, "end": v(-15.53, 18.5) * mm});
            skLineSegment(sketch, "E1387", {"start": v(-15.53, 18.5) * mm, "end": v(-15.5, 18.48) * mm});
            skLineSegment(sketch, "E1388", {"start": v(-15.5, 18.48) * mm, "end": v(-15.49, 18.46) * mm});
            skLineSegment(sketch, "E1389", {"start": v(-15.49, 18.46) * mm, "end": v(-15.46, 18.45) * mm});
            skLineSegment(sketch, "E1390", {"start": v(-15.46, 18.45) * mm, "end": v(-15.44, 18.43) * mm});
            skLineSegment(sketch, "E1391", {"start": v(-15.44, 18.43) * mm, "end": v(-15.4, 18.42) * mm});
            skLineSegment(sketch, "E1392", {"start": v(-15.4, 18.42) * mm, "end": v(-15.38, 18.4) * mm});
            skLineSegment(sketch, "E1393", {"start": v(-15.38, 18.4) * mm, "end": v(-15.35, 18.4) * mm});
            skLineSegment(sketch, "E1394", {"start": v(-15.35, 18.4) * mm, "end": v(-15.31, 18.39) * mm});
            skLineSegment(sketch, "E1395", {"start": v(-14.85, 24.39) * mm, "end": v(-14.85, 23.34) * mm});
            skLineSegment(sketch, "E1396", {"start": v(-14.85, 23.34) * mm, "end": v(-14.92, 23.27) * mm});
            skLineSegment(sketch, "E1397", {"start": v(-14.92, 23.27) * mm, "end": v(-14.98, 23.2) * mm});
            skLineSegment(sketch, "E1398", {"start": v(-14.98, 23.2) * mm, "end": v(-15.04, 23.15) * mm});
            skLineSegment(sketch, "E1399", {"start": v(-15.04, 23.15) * mm, "end": v(-15.1, 23.1) * mm});
            skLineSegment(sketch, "E1400", {"start": v(-15.1, 23.1) * mm, "end": v(-15.17, 23.05) * mm});
            skLineSegment(sketch, "E1401", {"start": v(-15.17, 23.05) * mm, "end": v(-15.23, 23) * mm});
            skLineSegment(sketch, "E1402", {"start": v(-15.23, 23) * mm, "end": v(-15.3, 22.96) * mm});
            skLineSegment(sketch, "E1403", {"start": v(-15.3, 22.96) * mm, "end": v(-15.32, 22.94) * mm});
            skLineSegment(sketch, "E1404", {"start": v(-15.32, 22.94) * mm, "end": v(-15.35, 22.92) * mm});
            skLineSegment(sketch, "E1405", {"start": v(-15.35, 22.92) * mm, "end": v(-15.38, 22.9) * mm});
            skLineSegment(sketch, "E1406", {"start": v(-15.38, 22.9) * mm, "end": v(-15.42, 22.9) * mm});
            skLineSegment(sketch, "E1407", {"start": v(-15.42, 22.9) * mm, "end": v(-15.45, 22.88) * mm});
            skLineSegment(sketch, "E1408", {"start": v(-15.45, 22.88) * mm, "end": v(-15.48, 22.86) * mm});
            skLineSegment(sketch, "E1409", {"start": v(-15.48, 22.86) * mm, "end": v(-15.5, 22.85) * mm});
            skLineSegment(sketch, "E1410", {"start": v(-15.5, 22.85) * mm, "end": v(-15.54, 22.84) * mm});
            skLineSegment(sketch, "E1411", {"start": v(-15.54, 22.84) * mm, "end": v(-15.57, 22.83) * mm});
            skLineSegment(sketch, "E1412", {"start": v(-15.57, 22.83) * mm, "end": v(-15.6, 22.82) * mm});
            skLineSegment(sketch, "E1413", {"start": v(-15.6, 22.82) * mm, "end": v(-15.63, 22.81) * mm});
            skLineSegment(sketch, "E1414", {"start": v(-15.63, 22.81) * mm, "end": v(-15.66, 22.8) * mm});
            skLineSegment(sketch, "E1415", {"start": v(-15.66, 22.8) * mm, "end": v(-15.69, 22.8) * mm});
            skLineSegment(sketch, "E1416", {"start": v(-15.69, 22.8) * mm, "end": v(-15.72, 22.8) * mm});
            skLineSegment(sketch, "E1417", {"start": v(-15.72, 22.8) * mm, "end": v(-15.75, 22.8) * mm});
            skLineSegment(sketch, "E1418", {"start": v(-15.75, 22.8) * mm, "end": v(-15.78, 22.79) * mm});
            skLineSegment(sketch, "E1419", {"start": v(-15.78, 22.79) * mm, "end": v(-15.8, 22.79) * mm});
            skLineSegment(sketch, "E1420", {"start": v(-15.8, 22.79) * mm, "end": v(-15.84, 22.79) * mm});
            skLineSegment(sketch, "E1421", {"start": v(-15.84, 22.79) * mm, "end": v(-15.87, 22.79) * mm});
            skLineSegment(sketch, "E1422", {"start": v(-15.87, 22.79) * mm, "end": v(-15.9, 22.8) * mm});
            skLineSegment(sketch, "E1423", {"start": v(-15.9, 22.8) * mm, "end": v(-15.95, 22.8) * mm});
            skLineSegment(sketch, "E1424", {"start": v(-15.95, 22.8) * mm, "end": v(-15.98, 22.8) * mm});
            skLineSegment(sketch, "E1425", {"start": v(-15.98, 22.8) * mm, "end": v(-16.02, 22.8) * mm});
            skLineSegment(sketch, "E1426", {"start": v(-16.02, 22.8) * mm, "end": v(-16.05, 22.82) * mm});
            skLineSegment(sketch, "E1427", {"start": v(-16.05, 22.82) * mm, "end": v(-16.1, 22.83) * mm});
            skLineSegment(sketch, "E1428", {"start": v(-16.1, 22.83) * mm, "end": v(-16.13, 22.84) * mm});
            skLineSegment(sketch, "E1429", {"start": v(-16.13, 22.84) * mm, "end": v(-16.16, 22.86) * mm});
            skLineSegment(sketch, "E1430", {"start": v(-16.16, 22.86) * mm, "end": v(-16.2, 22.87) * mm});
            skLineSegment(sketch, "E1431", {"start": v(-16.2, 22.87) * mm, "end": v(-16.24, 22.9) * mm});
            skLineSegment(sketch, "E1432", {"start": v(-16.24, 22.9) * mm, "end": v(-16.27, 22.91) * mm});
            skLineSegment(sketch, "E1433", {"start": v(-16.27, 22.91) * mm, "end": v(-16.3, 22.93) * mm});
            skLineSegment(sketch, "E1434", {"start": v(-16.3, 22.93) * mm, "end": v(-16.34, 22.96) * mm});
            skLineSegment(sketch, "E1435", {"start": v(-16.34, 22.96) * mm, "end": v(-16.38, 22.98) * mm});
            skLineSegment(sketch, "E1436", {"start": v(-16.38, 22.98) * mm, "end": v(-16.42, 23) * mm});
            skLineSegment(sketch, "E1437", {"start": v(-16.42, 23) * mm, "end": v(-16.45, 23.04) * mm});
            skLineSegment(sketch, "E1438", {"start": v(-16.45, 23.04) * mm, "end": v(-16.49, 23.06) * mm});
            skLineSegment(sketch, "E1439", {"start": v(-16.49, 23.06) * mm, "end": v(-16.52, 23.1) * mm});
            skLineSegment(sketch, "E1440", {"start": v(-16.52, 23.1) * mm, "end": v(-16.56, 23.13) * mm});
            skLineSegment(sketch, "E1441", {"start": v(-16.56, 23.13) * mm, "end": v(-16.6, 23.16) * mm});
            skLineSegment(sketch, "E1442", {"start": v(-16.6, 23.16) * mm, "end": v(-16.63, 23.2) * mm});
            skLineSegment(sketch, "E1443", {"start": v(-16.63, 23.2) * mm, "end": v(-16.66, 23.23) * mm});
            skLineSegment(sketch, "E1444", {"start": v(-16.66, 23.23) * mm, "end": v(-16.7, 23.27) * mm});
            skLineSegment(sketch, "E1445", {"start": v(-16.7, 23.27) * mm, "end": v(-16.72, 23.3) * mm});
            skLineSegment(sketch, "E1446", {"start": v(-16.72, 23.3) * mm, "end": v(-16.75, 23.35) * mm});
            skLineSegment(sketch, "E1447", {"start": v(-16.75, 23.35) * mm, "end": v(-16.78, 23.39) * mm});
            skLineSegment(sketch, "E1448", {"start": v(-16.78, 23.39) * mm, "end": v(-16.81, 23.43) * mm});
            skLineSegment(sketch, "E1449", {"start": v(-16.81, 23.43) * mm, "end": v(-16.84, 23.47) * mm});
            skLineSegment(sketch, "E1450", {"start": v(-16.84, 23.47) * mm, "end": v(-16.87, 23.52) * mm});
            skLineSegment(sketch, "E1451", {"start": v(-16.87, 23.52) * mm, "end": v(-16.9, 23.56) * mm});
            skLineSegment(sketch, "E1452", {"start": v(-16.9, 23.56) * mm, "end": v(-16.93, 23.61) * mm});
            skLineSegment(sketch, "E1453", {"start": v(-16.93, 23.61) * mm, "end": v(-16.96, 23.67) * mm});
            skLineSegment(sketch, "E1454", {"start": v(-16.96, 23.67) * mm, "end": v(-16.99, 23.72) * mm});
            skLineSegment(sketch, "E1455", {"start": v(-16.99, 23.72) * mm, "end": v(-17.01, 23.78) * mm});
            skLineSegment(sketch, "E1456", {"start": v(-17.01, 23.78) * mm, "end": v(-17.04, 23.84) * mm});
            skLineSegment(sketch, "E1457", {"start": v(-17.04, 23.84) * mm, "end": v(-17.07, 23.9) * mm});
            skLineSegment(sketch, "E1458", {"start": v(-17.07, 23.9) * mm, "end": v(-17.1, 23.97) * mm});
            skLineSegment(sketch, "E1459", {"start": v(-17.1, 23.97) * mm, "end": v(-17.12, 24.03) * mm});
            skLineSegment(sketch, "E1460", {"start": v(-17.12, 24.03) * mm, "end": v(-17.14, 24.1) * mm});
            skLineSegment(sketch, "E1461", {"start": v(-17.14, 24.1) * mm, "end": v(-17.17, 24.16) * mm});
            skLineSegment(sketch, "E1462", {"start": v(-17.17, 24.16) * mm, "end": v(-17.19, 24.23) * mm});
            skLineSegment(sketch, "E1463", {"start": v(-17.19, 24.23) * mm, "end": v(-17.2, 24.3) * mm});
            skLineSegment(sketch, "E1464", {"start": v(-17.2, 24.3) * mm, "end": v(-17.23, 24.38) * mm});
            skLineSegment(sketch, "E1465", {"start": v(-17.23, 24.38) * mm, "end": v(-17.25, 24.45) * mm});
            skLineSegment(sketch, "E1466", {"start": v(-17.25, 24.45) * mm, "end": v(-17.27, 24.52) * mm});
            skLineSegment(sketch, "E1467", {"start": v(-17.27, 24.52) * mm, "end": v(-17.29, 24.6) * mm});
            skLineSegment(sketch, "E1468", {"start": v(-17.29, 24.6) * mm, "end": v(-17.3, 24.68) * mm});
            skLineSegment(sketch, "E1469", {"start": v(-17.3, 24.68) * mm, "end": v(-17.32, 24.76) * mm});
            skLineSegment(sketch, "E1470", {"start": v(-17.32, 24.76) * mm, "end": v(-17.34, 24.84) * mm});
            skLineSegment(sketch, "E1471", {"start": v(-17.34, 24.84) * mm, "end": v(-17.35, 24.92) * mm});
            skLineSegment(sketch, "E1472", {"start": v(-17.35, 24.92) * mm, "end": v(-17.36, 25) * mm});
            skLineSegment(sketch, "E1473", {"start": v(-17.36, 25) * mm, "end": v(-17.38, 25.08) * mm});
            skLineSegment(sketch, "E1474", {"start": v(-17.38, 25.08) * mm, "end": v(-17.39, 25.16) * mm});
            skLineSegment(sketch, "E1475", {"start": v(-17.39, 25.16) * mm, "end": v(-17.4, 25.24) * mm});
            skLineSegment(sketch, "E1476", {"start": v(-17.4, 25.24) * mm, "end": v(-17.4, 25.33) * mm});
            skLineSegment(sketch, "E1477", {"start": v(-17.4, 25.33) * mm, "end": v(-17.41, 25.41) * mm});
            skLineSegment(sketch, "E1478", {"start": v(-17.41, 25.41) * mm, "end": v(-17.42, 25.5) * mm});
            skLineSegment(sketch, "E1479", {"start": v(-17.42, 25.5) * mm, "end": v(-17.43, 25.58) * mm});
            skLineSegment(sketch, "E1480", {"start": v(-17.43, 25.58) * mm, "end": v(-17.43, 25.67) * mm});
            skLineSegment(sketch, "E1481", {"start": v(-17.43, 25.67) * mm, "end": v(-17.43, 25.75) * mm});
            skLineSegment(sketch, "E1482", {"start": v(-17.43, 25.75) * mm, "end": v(-17.44, 25.84) * mm});
            skLineSegment(sketch, "E1483", {"start": v(-17.44, 25.84) * mm, "end": v(-17.44, 25.93) * mm});
            skLineSegment(sketch, "E1484", {"start": v(-17.44, 25.93) * mm, "end": v(-17.44, 26.02) * mm});
            skLineSegment(sketch, "E1485", {"start": v(-17.44, 26.02) * mm, "end": v(-17.44, 26.15) * mm});
            skLineSegment(sketch, "E1486", {"start": v(-17.44, 26.15) * mm, "end": v(-17.44, 26.27) * mm});
            skLineSegment(sketch, "E1487", {"start": v(-17.44, 26.27) * mm, "end": v(-17.43, 26.4) * mm});
            skLineSegment(sketch, "E1488", {"start": v(-17.43, 26.4) * mm, "end": v(-17.42, 26.53) * mm});
            skLineSegment(sketch, "E1489", {"start": v(-17.42, 26.53) * mm, "end": v(-17.42, 26.65) * mm});
            skLineSegment(sketch, "E1490", {"start": v(-17.42, 26.65) * mm, "end": v(-17.4, 26.78) * mm});
            skLineSegment(sketch, "E1491", {"start": v(-17.4, 26.78) * mm, "end": v(-17.4, 26.9) * mm});
            skLineSegment(sketch, "E1492", {"start": v(-17.4, 26.9) * mm, "end": v(-17.38, 27.02) * mm});
            skLineSegment(sketch, "E1493", {"start": v(-17.38, 27.02) * mm, "end": v(-17.36, 27.15) * mm});
            skLineSegment(sketch, "E1494", {"start": v(-17.36, 27.15) * mm, "end": v(-17.35, 27.27) * mm});
            skLineSegment(sketch, "E1495", {"start": v(-17.35, 27.27) * mm, "end": v(-17.33, 27.4) * mm});
            skLineSegment(sketch, "E1496", {"start": v(-17.33, 27.4) * mm, "end": v(-17.3, 27.51) * mm});
            skLineSegment(sketch, "E1497", {"start": v(-17.3, 27.51) * mm, "end": v(-17.28, 27.64) * mm});
            skLineSegment(sketch, "E1498", {"start": v(-17.28, 27.64) * mm, "end": v(-17.26, 27.76) * mm});
            skLineSegment(sketch, "E1499", {"start": v(-17.26, 27.76) * mm, "end": v(-17.23, 27.88) * mm});
            skLineSegment(sketch, "E1500", {"start": v(-17.23, 27.88) * mm, "end": v(-17.2, 28) * mm});
            skLineSegment(sketch, "E1501", {"start": v(-17.2, 28) * mm, "end": v(-17.17, 28.11) * mm});
            skLineSegment(sketch, "E1502", {"start": v(-17.17, 28.11) * mm, "end": v(-17.14, 28.23) * mm});
            skLineSegment(sketch, "E1503", {"start": v(-17.14, 28.23) * mm, "end": v(-17.1, 28.34) * mm});
            skLineSegment(sketch, "E1504", {"start": v(-17.1, 28.34) * mm, "end": v(-17.07, 28.44) * mm});
            skLineSegment(sketch, "E1505", {"start": v(-17.07, 28.44) * mm, "end": v(-17.03, 28.55) * mm});
            skLineSegment(sketch, "E1506", {"start": v(-17.03, 28.55) * mm, "end": v(-17, 28.65) * mm});
            skLineSegment(sketch, "E1507", {"start": v(-17, 28.65) * mm, "end": v(-16.96, 28.75) * mm});
            skLineSegment(sketch, "E1508", {"start": v(-16.96, 28.75) * mm, "end": v(-16.92, 28.84) * mm});
            skLineSegment(sketch, "E1509", {"start": v(-16.92, 28.84) * mm, "end": v(-16.88, 28.94) * mm});
            skLineSegment(sketch, "E1510", {"start": v(-16.88, 28.94) * mm, "end": v(-16.84, 29.02) * mm});
            skLineSegment(sketch, "E1511", {"start": v(-16.84, 29.02) * mm, "end": v(-16.8, 29.1) * mm});
            skLineSegment(sketch, "E1512", {"start": v(-16.8, 29.1) * mm, "end": v(-16.75, 29.2) * mm});
            skLineSegment(sketch, "E1513", {"start": v(-16.75, 29.2) * mm, "end": v(-16.7, 29.27) * mm});
            skLineSegment(sketch, "E1514", {"start": v(-16.7, 29.27) * mm, "end": v(-16.66, 29.34) * mm});
            skLineSegment(sketch, "E1515", {"start": v(-16.66, 29.34) * mm, "end": v(-16.61, 29.42) * mm});
            skLineSegment(sketch, "E1516", {"start": v(-16.61, 29.42) * mm, "end": v(-16.56, 29.49) * mm});
            skLineSegment(sketch, "E1517", {"start": v(-16.56, 29.49) * mm, "end": v(-16.53, 29.53) * mm});
            skLineSegment(sketch, "E1518", {"start": v(-16.53, 29.53) * mm, "end": v(-16.5, 29.58) * mm});
            skLineSegment(sketch, "E1519", {"start": v(-16.5, 29.58) * mm, "end": v(-16.45, 29.63) * mm});
            skLineSegment(sketch, "E1520", {"start": v(-16.45, 29.63) * mm, "end": v(-16.42, 29.67) * mm});
            skLineSegment(sketch, "E1521", {"start": v(-16.42, 29.67) * mm, "end": v(-16.38, 29.71) * mm});
            skLineSegment(sketch, "E1522", {"start": v(-16.38, 29.71) * mm, "end": v(-16.34, 29.75) * mm});
            skLineSegment(sketch, "E1523", {"start": v(-16.34, 29.75) * mm, "end": v(-16.3, 29.79) * mm});
            skLineSegment(sketch, "E1524", {"start": v(-16.3, 29.79) * mm, "end": v(-16.26, 29.83) * mm});
            skLineSegment(sketch, "E1525", {"start": v(-16.26, 29.83) * mm, "end": v(-16.22, 29.86) * mm});
            skLineSegment(sketch, "E1526", {"start": v(-16.22, 29.86) * mm, "end": v(-16.18, 29.9) * mm});
            skLineSegment(sketch, "E1527", {"start": v(-16.18, 29.9) * mm, "end": v(-16.14, 29.93) * mm});
            skLineSegment(sketch, "E1528", {"start": v(-16.14, 29.93) * mm, "end": v(-16.1, 29.96) * mm});
            skLineSegment(sketch, "E1529", {"start": v(-16.1, 29.96) * mm, "end": v(-16.06, 30) * mm});
            skLineSegment(sketch, "E1530", {"start": v(-16.06, 30) * mm, "end": v(-16.02, 30.02) * mm});
            skLineSegment(sketch, "E1531", {"start": v(-16.02, 30.02) * mm, "end": v(-15.98, 30.04) * mm});
            skLineSegment(sketch, "E1532", {"start": v(-15.98, 30.04) * mm, "end": v(-15.93, 30.07) * mm});
            skLineSegment(sketch, "E1533", {"start": v(-15.93, 30.07) * mm, "end": v(-15.9, 30.1) * mm});
            skLineSegment(sketch, "E1534", {"start": v(-15.9, 30.1) * mm, "end": v(-15.85, 30.12) * mm});
            skLineSegment(sketch, "E1535", {"start": v(-15.85, 30.12) * mm, "end": v(-15.8, 30.14) * mm});
            skLineSegment(sketch, "E1536", {"start": v(-15.8, 30.14) * mm, "end": v(-15.76, 30.15) * mm});
            skLineSegment(sketch, "E1537", {"start": v(-15.76, 30.15) * mm, "end": v(-15.72, 30.17) * mm});
            skLineSegment(sketch, "E1538", {"start": v(-15.72, 30.17) * mm, "end": v(-15.67, 30.19) * mm});
            skLineSegment(sketch, "E1539", {"start": v(-15.67, 30.19) * mm, "end": v(-15.63, 30.2) * mm});
            skLineSegment(sketch, "E1540", {"start": v(-15.63, 30.2) * mm, "end": v(-15.58, 30.22) * mm});
            skLineSegment(sketch, "E1541", {"start": v(-15.58, 30.22) * mm, "end": v(-15.54, 30.23) * mm});
            skLineSegment(sketch, "E1542", {"start": v(-15.54, 30.23) * mm, "end": v(-15.49, 30.24) * mm});
            skLineSegment(sketch, "E1543", {"start": v(-15.49, 30.24) * mm, "end": v(-15.44, 30.25) * mm});
            skLineSegment(sketch, "E1544", {"start": v(-15.44, 30.25) * mm, "end": v(-15.4, 30.25) * mm});
            skLineSegment(sketch, "E1545", {"start": v(-15.4, 30.25) * mm, "end": v(-15.35, 30.26) * mm});
            skLineSegment(sketch, "E1546", {"start": v(-15.35, 30.26) * mm, "end": v(-15.3, 30.26) * mm});
            skLineSegment(sketch, "E1547", {"start": v(-15.3, 30.26) * mm, "end": v(-15.25, 30.26) * mm});
            skLineSegment(sketch, "E1548", {"start": v(-15.25, 30.26) * mm, "end": v(-15.2, 30.26) * mm});
            skLineSegment(sketch, "E1549", {"start": v(-15.2, 30.26) * mm, "end": v(-15.2, 29.37) * mm});
            skLineSegment(sketch, "E1550", {"start": v(-15.2, 29.37) * mm, "end": v(-15.23, 29.36) * mm});
            skLineSegment(sketch, "E1551", {"start": v(-15.23, 29.36) * mm, "end": v(-15.25, 29.34) * mm});
            skLineSegment(sketch, "E1552", {"start": v(-15.25, 29.34) * mm, "end": v(-15.27, 29.33) * mm});
            skLineSegment(sketch, "E1553", {"start": v(-15.27, 29.33) * mm, "end": v(-15.29, 29.31) * mm});
            skLineSegment(sketch, "E1554", {"start": v(-15.29, 29.31) * mm, "end": v(-15.3, 29.3) * mm});
            skLineSegment(sketch, "E1555", {"start": v(-15.3, 29.3) * mm, "end": v(-15.33, 29.28) * mm});
            skLineSegment(sketch, "E1556", {"start": v(-15.33, 29.28) * mm, "end": v(-15.34, 29.27) * mm});
            skLineSegment(sketch, "E1557", {"start": v(-15.34, 29.27) * mm, "end": v(-15.36, 29.25) * mm});
            skLineSegment(sketch, "E1558", {"start": v(-15.36, 29.25) * mm, "end": v(-15.38, 29.23) * mm});
            skLineSegment(sketch, "E1559", {"start": v(-15.38, 29.23) * mm, "end": v(-15.4, 29.21) * mm});
            skLineSegment(sketch, "E1560", {"start": v(-15.4, 29.21) * mm, "end": v(-15.4, 29.19) * mm});
            skLineSegment(sketch, "E1561", {"start": v(-15.4, 29.19) * mm, "end": v(-15.42, 29.17) * mm});
            skLineSegment(sketch, "E1562", {"start": v(-15.42, 29.17) * mm, "end": v(-15.43, 29.15) * mm});
            skLineSegment(sketch, "E1563", {"start": v(-15.43, 29.15) * mm, "end": v(-15.44, 29.12) * mm});
            skLineSegment(sketch, "E1564", {"start": v(-15.44, 29.12) * mm, "end": v(-15.46, 29.1) * mm});
            skLineSegment(sketch, "E1565", {"start": v(-15.46, 29.1) * mm, "end": v(-15.47, 29.07) * mm});
            skLineSegment(sketch, "E1566", {"start": v(-15.47, 29.07) * mm, "end": v(-15.48, 29.05) * mm});
            skLineSegment(sketch, "E1567", {"start": v(-15.48, 29.05) * mm, "end": v(-15.49, 29.02) * mm});
            skLineSegment(sketch, "E1568", {"start": v(-15.49, 29.02) * mm, "end": v(-15.5, 29) * mm});
            skLineSegment(sketch, "E1569", {"start": v(-15.5, 29) * mm, "end": v(-15.5, 28.96) * mm});
            skLineSegment(sketch, "E1570", {"start": v(-15.5, 28.96) * mm, "end": v(-15.5, 28.93) * mm});
            skLineSegment(sketch, "E1571", {"start": v(-15.5, 28.93) * mm, "end": v(-15.52, 28.9) * mm});
            skLineSegment(sketch, "E1572", {"start": v(-15.52, 28.9) * mm, "end": v(-15.53, 28.83) * mm});
            skLineSegment(sketch, "E1573", {"start": v(-15.53, 28.83) * mm, "end": v(-15.54, 28.75) * mm});
            skLineSegment(sketch, "E1574", {"start": v(-15.54, 28.75) * mm, "end": v(-15.54, 28.67) * mm});
            skLineSegment(sketch, "E1575", {"start": v(-15.54, 28.67) * mm, "end": v(-15.55, 28.58) * mm});
            skLineSegment(sketch, "E1576", {"start": v(-15.55, 28.58) * mm, "end": v(-15.55, 28.49) * mm});
            skLineSegment(sketch, "E1577", {"start": v(-15.55, 28.49) * mm, "end": v(-15.55, 25) * mm});
            skLineSegment(sketch, "E1578", {"start": v(-15.55, 25) * mm, "end": v(-15.55, 24.9) * mm});
            skLineSegment(sketch, "E1579", {"start": v(-15.55, 24.9) * mm, "end": v(-15.54, 24.8) * mm});
            skLineSegment(sketch, "E1580", {"start": v(-15.54, 24.8) * mm, "end": v(-15.54, 24.72) * mm});
            skLineSegment(sketch, "E1581", {"start": v(-15.54, 24.72) * mm, "end": v(-15.53, 24.64) * mm});
            skLineSegment(sketch, "E1582", {"start": v(-15.53, 24.64) * mm, "end": v(-15.52, 24.6) * mm});
            skLineSegment(sketch, "E1583", {"start": v(-15.52, 24.6) * mm, "end": v(-15.51, 24.56) * mm});
            skLineSegment(sketch, "E1584", {"start": v(-15.51, 24.56) * mm, "end": v(-15.5, 24.52) * mm});
            skLineSegment(sketch, "E1585", {"start": v(-15.5, 24.52) * mm, "end": v(-15.5, 24.48) * mm});
            skLineSegment(sketch, "E1586", {"start": v(-15.5, 24.48) * mm, "end": v(-15.49, 24.45) * mm});
            skLineSegment(sketch, "E1587", {"start": v(-15.49, 24.45) * mm, "end": v(-15.48, 24.42) * mm});
            skLineSegment(sketch, "E1588", {"start": v(-15.48, 24.42) * mm, "end": v(-15.47, 24.39) * mm});
            skLineSegment(sketch, "E1589", {"start": v(-15.47, 24.39) * mm, "end": v(-15.46, 24.36) * mm});
            skLineSegment(sketch, "E1590", {"start": v(-15.46, 24.36) * mm, "end": v(-15.45, 24.33) * mm});
            skLineSegment(sketch, "E1591", {"start": v(-15.45, 24.33) * mm, "end": v(-15.44, 24.3) * mm});
            skLineSegment(sketch, "E1592", {"start": v(-15.44, 24.3) * mm, "end": v(-15.42, 24.28) * mm});
            skLineSegment(sketch, "E1593", {"start": v(-15.42, 24.28) * mm, "end": v(-15.41, 24.26) * mm});
            skLineSegment(sketch, "E1594", {"start": v(-15.41, 24.26) * mm, "end": v(-15.4, 24.23) * mm});
            skLineSegment(sketch, "E1595", {"start": v(-15.4, 24.23) * mm, "end": v(-15.38, 24.22) * mm});
            skLineSegment(sketch, "E1596", {"start": v(-15.38, 24.22) * mm, "end": v(-15.37, 24.2) * mm});
            skLineSegment(sketch, "E1597", {"start": v(-15.37, 24.2) * mm, "end": v(-15.36, 24.18) * mm});
            skLineSegment(sketch, "E1598", {"start": v(-15.36, 24.18) * mm, "end": v(-15.34, 24.17) * mm});
            skLineSegment(sketch, "E1599", {"start": v(-15.34, 24.17) * mm, "end": v(-15.33, 24.16) * mm});
            skLineSegment(sketch, "E1600", {"start": v(-15.33, 24.16) * mm, "end": v(-15.3, 24.15) * mm});
            skLineSegment(sketch, "E1601", {"start": v(-15.3, 24.15) * mm, "end": v(-15.3, 24.14) * mm});
            skLineSegment(sketch, "E1602", {"start": v(-15.3, 24.14) * mm, "end": v(-15.28, 24.14) * mm});
            skLineSegment(sketch, "E1603", {"start": v(-15.28, 24.14) * mm, "end": v(-15.26, 24.13) * mm});
            skLineSegment(sketch, "E1604", {"start": v(-15.26, 24.13) * mm, "end": v(-15.24, 24.13) * mm});
            skLineSegment(sketch, "E1605", {"start": v(-15.24, 24.13) * mm, "end": v(-15.22, 24.13) * mm});
            skLineSegment(sketch, "E1606", {"start": v(-15.22, 24.13) * mm, "end": v(-15.2, 24.13) * mm});
            skLineSegment(sketch, "E1607", {"start": v(-15.2, 24.13) * mm, "end": v(-15.19, 24.14) * mm});
            skLineSegment(sketch, "E1608", {"start": v(-15.19, 24.14) * mm, "end": v(-15.17, 24.14) * mm});
            skLineSegment(sketch, "E1609", {"start": v(-15.17, 24.14) * mm, "end": v(-15.15, 24.15) * mm});
            skLineSegment(sketch, "E1610", {"start": v(-15.15, 24.15) * mm, "end": v(-15.13, 24.16) * mm});
            skLineSegment(sketch, "E1611", {"start": v(-15.13, 24.16) * mm, "end": v(-15.1, 24.17) * mm});
            skLineSegment(sketch, "E1612", {"start": v(-15.1, 24.17) * mm, "end": v(-15.08, 24.19) * mm});
            skLineSegment(sketch, "E1613", {"start": v(-15.08, 24.19) * mm, "end": v(-15.06, 24.2) * mm});
            skLineSegment(sketch, "E1614", {"start": v(-15.06, 24.2) * mm, "end": v(-15.04, 24.22) * mm});
            skLineSegment(sketch, "E1615", {"start": v(-15.04, 24.22) * mm, "end": v(-15.01, 24.24) * mm});
            skLineSegment(sketch, "E1616", {"start": v(-15.01, 24.24) * mm, "end": v(-14.99, 24.26) * mm});
            skLineSegment(sketch, "E1617", {"start": v(-14.99, 24.26) * mm, "end": v(-14.96, 24.28) * mm});
            skLineSegment(sketch, "E1618", {"start": v(-14.96, 24.28) * mm, "end": v(-14.91, 24.33) * mm});
            skLineSegment(sketch, "E1619", {"start": v(-14.91, 24.33) * mm, "end": v(-14.85, 24.39) * mm});
            skLineSegment(sketch, "E1620", {"start": v(-14.08, 14.68) * mm, "end": v(-14.08, 3.93) * mm});
            skLineSegment(sketch, "E1621", {"start": v(-14.08, 3.93) * mm, "end": v(-14.08, 3.84) * mm});
            skLineSegment(sketch, "E1622", {"start": v(-14.08, 3.84) * mm, "end": v(-14.08, 3.76) * mm});
            skLineSegment(sketch, "E1623", {"start": v(-14.08, 3.76) * mm, "end": v(-14.07, 3.7) * mm});
            skLineSegment(sketch, "E1624", {"start": v(-14.07, 3.7) * mm, "end": v(-14.06, 3.62) * mm});
            skLineSegment(sketch, "E1625", {"start": v(-14.06, 3.62) * mm, "end": v(-14.05, 3.56) * mm});
            skLineSegment(sketch, "E1626", {"start": v(-14.05, 3.56) * mm, "end": v(-14.04, 3.5) * mm});
            skLineSegment(sketch, "E1627", {"start": v(-14.04, 3.5) * mm, "end": v(-14.03, 3.48) * mm});
            skLineSegment(sketch, "E1628", {"start": v(-14.03, 3.48) * mm, "end": v(-14.03, 3.46) * mm});
            skLineSegment(sketch, "E1629", {"start": v(-14.03, 3.46) * mm, "end": v(-14.02, 3.44) * mm});
            skLineSegment(sketch, "E1630", {"start": v(-14.02, 3.44) * mm, "end": v(-14.01, 3.42) * mm});
            skLineSegment(sketch, "E1631", {"start": v(-14.01, 3.42) * mm, "end": v(-14, 3.38) * mm});
            skLineSegment(sketch, "E1632", {"start": v(-14, 3.38) * mm, "end": v(-13.98, 3.36) * mm});
            skLineSegment(sketch, "E1633", {"start": v(-13.98, 3.36) * mm, "end": v(-13.97, 3.34) * mm});
            skLineSegment(sketch, "E1634", {"start": v(-13.97, 3.34) * mm, "end": v(-13.97, 3.33) * mm});
            skLineSegment(sketch, "E1635", {"start": v(-13.97, 3.33) * mm, "end": v(-13.96, 3.32) * mm});
            skLineSegment(sketch, "E1636", {"start": v(-13.96, 3.32) * mm, "end": v(-13.95, 3.3) * mm});
            skLineSegment(sketch, "E1637", {"start": v(-13.95, 3.3) * mm, "end": v(-13.94, 3.3) * mm});
            skLineSegment(sketch, "E1638", {"start": v(-13.94, 3.3) * mm, "end": v(-13.92, 3.29) * mm});
            skLineSegment(sketch, "E1639", {"start": v(-13.92, 3.29) * mm, "end": v(-13.87, 3.26) * mm});
            skLineSegment(sketch, "E1640", {"start": v(-13.87, 3.26) * mm, "end": v(-13.8, 3.23) * mm});
            skLineSegment(sketch, "E1641", {"start": v(-13.8, 3.23) * mm, "end": v(-13.73, 3.19) * mm});
            skLineSegment(sketch, "E1642", {"start": v(-13.73, 3.19) * mm, "end": v(-13.7, 3.17) * mm});
            skLineSegment(sketch, "E1643", {"start": v(-13.7, 3.17) * mm, "end": v(-13.67, 3.16) * mm});
            skLineSegment(sketch, "E1644", {"start": v(-13.67, 3.16) * mm, "end": v(-13.65, 3.14) * mm});
            skLineSegment(sketch, "E1645", {"start": v(-13.65, 3.14) * mm, "end": v(-13.63, 3.12) * mm});
            skLineSegment(sketch, "E1646", {"start": v(-13.63, 3.12) * mm, "end": v(-13.6, 3.1) * mm});
            skLineSegment(sketch, "E1647", {"start": v(-13.6, 3.1) * mm, "end": v(-13.6, 3.07) * mm});
            skLineSegment(sketch, "E1648", {"start": v(-13.6, 3.07) * mm, "end": v(-13.57, 3.04) * mm});
            skLineSegment(sketch, "E1649", {"start": v(-13.57, 3.04) * mm, "end": v(-13.56, 3.01) * mm});
            skLineSegment(sketch, "E1650", {"start": v(-13.56, 3.01) * mm, "end": v(-13.55, 2.98) * mm});
            skLineSegment(sketch, "E1651", {"start": v(-13.55, 2.98) * mm, "end": v(-13.53, 2.94) * mm});
            skLineSegment(sketch, "E1652", {"start": v(-13.53, 2.94) * mm, "end": v(-13.53, 2.9) * mm});
            skLineSegment(sketch, "E1653", {"start": v(-13.53, 2.9) * mm, "end": v(-13.52, 2.87) * mm});
            skLineSegment(sketch, "E1654", {"start": v(-13.52, 2.87) * mm, "end": v(-13.51, 2.83) * mm});
            skLineSegment(sketch, "E1655", {"start": v(-13.51, 2.83) * mm, "end": v(-13.5, 2.78) * mm});
            skLineSegment(sketch, "E1656", {"start": v(-13.5, 2.78) * mm, "end": v(-13.5, 2.73) * mm});
            skLineSegment(sketch, "E1657", {"start": v(-13.5, 2.73) * mm, "end": v(-13.5, 2.69) * mm});
            skLineSegment(sketch, "E1658", {"start": v(-13.5, 2.69) * mm, "end": v(-13.5, 2.66) * mm});
            skLineSegment(sketch, "E1659", {"start": v(-13.5, 2.66) * mm, "end": v(-13.5, 2.63) * mm});
            skLineSegment(sketch, "E1660", {"start": v(-13.5, 2.63) * mm, "end": v(-13.5, 2.6) * mm});
            skLineSegment(sketch, "E1661", {"start": v(-13.5, 2.6) * mm, "end": v(-13.51, 2.57) * mm});
            skLineSegment(sketch, "E1662", {"start": v(-13.51, 2.57) * mm, "end": v(-13.52, 2.55) * mm});
            skLineSegment(sketch, "E1663", {"start": v(-13.52, 2.55) * mm, "end": v(-13.52, 2.52) * mm});
            skLineSegment(sketch, "E1664", {"start": v(-13.52, 2.52) * mm, "end": v(-13.53, 2.5) * mm});
            skLineSegment(sketch, "E1665", {"start": v(-13.53, 2.5) * mm, "end": v(-13.53, 2.47) * mm});
            skLineSegment(sketch, "E1666", {"start": v(-13.53, 2.47) * mm, "end": v(-13.54, 2.45) * mm});
            skLineSegment(sketch, "E1667", {"start": v(-13.54, 2.45) * mm, "end": v(-13.55, 2.42) * mm});
            skLineSegment(sketch, "E1668", {"start": v(-13.55, 2.42) * mm, "end": v(-13.56, 2.4) * mm});
            skLineSegment(sketch, "E1669", {"start": v(-13.56, 2.4) * mm, "end": v(-13.57, 2.38) * mm});
            skLineSegment(sketch, "E1670", {"start": v(-13.57, 2.38) * mm, "end": v(-13.58, 2.36) * mm});
            skLineSegment(sketch, "E1671", {"start": v(-13.58, 2.36) * mm, "end": v(-13.6, 2.34) * mm});
            skLineSegment(sketch, "E1672", {"start": v(-13.6, 2.34) * mm, "end": v(-13.6, 2.32) * mm});
            skLineSegment(sketch, "E1673", {"start": v(-13.6, 2.32) * mm, "end": v(-13.62, 2.3) * mm});
            skLineSegment(sketch, "E1674", {"start": v(-13.62, 2.3) * mm, "end": v(-13.64, 2.29) * mm});
            skLineSegment(sketch, "E1675", {"start": v(-13.64, 2.29) * mm, "end": v(-13.65, 2.28) * mm});
            skLineSegment(sketch, "E1676", {"start": v(-13.65, 2.28) * mm, "end": v(-13.66, 2.26) * mm});
            skLineSegment(sketch, "E1677", {"start": v(-13.66, 2.26) * mm, "end": v(-13.68, 2.25) * mm});
            skLineSegment(sketch, "E1678", {"start": v(-13.68, 2.25) * mm, "end": v(-13.7, 2.24) * mm});
            skLineSegment(sketch, "E1679", {"start": v(-13.7, 2.24) * mm, "end": v(-13.7, 2.23) * mm});
            skLineSegment(sketch, "E1680", {"start": v(-13.7, 2.23) * mm, "end": v(-13.72, 2.23) * mm});
            skLineSegment(sketch, "E1681", {"start": v(-13.72, 2.23) * mm, "end": v(-13.74, 2.22) * mm});
            skLineSegment(sketch, "E1682", {"start": v(-13.74, 2.22) * mm, "end": v(-13.76, 2.21) * mm});
            skLineSegment(sketch, "E1683", {"start": v(-13.76, 2.21) * mm, "end": v(-13.78, 2.2) * mm});
            skLineSegment(sketch, "E1684", {"start": v(-13.78, 2.2) * mm, "end": v(-13.8, 2.2) * mm});
            skLineSegment(sketch, "E1685", {"start": v(-13.8, 2.2) * mm, "end": v(-13.82, 2.2) * mm});
            skLineSegment(sketch, "E1686", {"start": v(-13.82, 2.2) * mm, "end": v(-13.84, 2.2) * mm});
            skLineSegment(sketch, "E1687", {"start": v(-13.84, 2.2) * mm, "end": v(-13.87, 2.2) * mm});
            skLineSegment(sketch, "E1688", {"start": v(-13.87, 2.2) * mm, "end": v(-13.9, 2.2) * mm});
            skLineSegment(sketch, "E1689", {"start": v(-13.9, 2.2) * mm, "end": v(-13.92, 2.2) * mm});
            skLineSegment(sketch, "E1690", {"start": v(-13.92, 2.2) * mm, "end": v(-14.08, 2.2) * mm});
            skLineSegment(sketch, "E1691", {"start": v(-14.08, 2.2) * mm, "end": v(-15.86, 2.2) * mm});
            skLineSegment(sketch, "E1692", {"start": v(-15.86, 2.2) * mm, "end": v(-16.02, 2.2) * mm});
            skLineSegment(sketch, "E1693", {"start": v(-16.02, 2.2) * mm, "end": v(-16.04, 2.2) * mm});
            skLineSegment(sketch, "E1694", {"start": v(-16.04, 2.2) * mm, "end": v(-16.07, 2.2) * mm});
            skLineSegment(sketch, "E1695", {"start": v(-16.07, 2.2) * mm, "end": v(-16.1, 2.2) * mm});
            skLineSegment(sketch, "E1696", {"start": v(-16.1, 2.2) * mm, "end": v(-16.12, 2.2) * mm});
            skLineSegment(sketch, "E1697", {"start": v(-16.12, 2.2) * mm, "end": v(-16.14, 2.2) * mm});
            skLineSegment(sketch, "E1698", {"start": v(-16.14, 2.2) * mm, "end": v(-16.16, 2.2) * mm});
            skLineSegment(sketch, "E1699", {"start": v(-16.16, 2.2) * mm, "end": v(-16.18, 2.21) * mm});
            skLineSegment(sketch, "E1700", {"start": v(-16.18, 2.21) * mm, "end": v(-16.2, 2.22) * mm});
            skLineSegment(sketch, "E1701", {"start": v(-16.2, 2.22) * mm, "end": v(-16.21, 2.23) * mm});
            skLineSegment(sketch, "E1702", {"start": v(-16.21, 2.23) * mm, "end": v(-16.23, 2.23) * mm});
            skLineSegment(sketch, "E1703", {"start": v(-16.23, 2.23) * mm, "end": v(-16.25, 2.24) * mm});
            skLineSegment(sketch, "E1704", {"start": v(-16.25, 2.24) * mm, "end": v(-16.26, 2.25) * mm});
            skLineSegment(sketch, "E1705", {"start": v(-16.26, 2.25) * mm, "end": v(-16.28, 2.26) * mm});
            skLineSegment(sketch, "E1706", {"start": v(-16.28, 2.26) * mm, "end": v(-16.29, 2.28) * mm});
            skLineSegment(sketch, "E1707", {"start": v(-16.29, 2.28) * mm, "end": v(-16.3, 2.29) * mm});
            skLineSegment(sketch, "E1708", {"start": v(-16.3, 2.29) * mm, "end": v(-16.31, 2.3) * mm});
            skLineSegment(sketch, "E1709", {"start": v(-16.31, 2.3) * mm, "end": v(-16.33, 2.32) * mm});
            skLineSegment(sketch, "E1710", {"start": v(-16.33, 2.32) * mm, "end": v(-16.34, 2.34) * mm});
            skLineSegment(sketch, "E1711", {"start": v(-16.34, 2.34) * mm, "end": v(-16.35, 2.36) * mm});
            skLineSegment(sketch, "E1712", {"start": v(-16.35, 2.36) * mm, "end": v(-16.36, 2.38) * mm});
            skLineSegment(sketch, "E1713", {"start": v(-16.36, 2.38) * mm, "end": v(-16.38, 2.4) * mm});
            skLineSegment(sketch, "E1714", {"start": v(-16.38, 2.4) * mm, "end": v(-16.39, 2.42) * mm});
            skLineSegment(sketch, "E1715", {"start": v(-16.39, 2.42) * mm, "end": v(-16.4, 2.45) * mm});
            skLineSegment(sketch, "E1716", {"start": v(-16.4, 2.45) * mm, "end": v(-16.4, 2.47) * mm});
            skLineSegment(sketch, "E1717", {"start": v(-16.4, 2.47) * mm, "end": v(-16.4, 2.5) * mm});
            skLineSegment(sketch, "E1718", {"start": v(-16.4, 2.5) * mm, "end": v(-16.42, 2.52) * mm});
            skLineSegment(sketch, "E1719", {"start": v(-16.42, 2.52) * mm, "end": v(-16.42, 2.55) * mm});
            skLineSegment(sketch, "E1720", {"start": v(-16.42, 2.55) * mm, "end": v(-16.43, 2.57) * mm});
            skLineSegment(sketch, "E1721", {"start": v(-16.43, 2.57) * mm, "end": v(-16.43, 2.6) * mm});
            skLineSegment(sketch, "E1722", {"start": v(-16.43, 2.6) * mm, "end": v(-16.43, 2.63) * mm});
            skLineSegment(sketch, "E1723", {"start": v(-16.43, 2.63) * mm, "end": v(-16.43, 2.66) * mm});
            skLineSegment(sketch, "E1724", {"start": v(-16.43, 2.66) * mm, "end": v(-16.43, 2.69) * mm});
            skLineSegment(sketch, "E1725", {"start": v(-16.43, 2.69) * mm, "end": v(-16.43, 2.73) * mm});
            skLineSegment(sketch, "E1726", {"start": v(-16.43, 2.73) * mm, "end": v(-16.43, 2.78) * mm});
            skLineSegment(sketch, "E1727", {"start": v(-16.43, 2.78) * mm, "end": v(-16.42, 2.83) * mm});
            skLineSegment(sketch, "E1728", {"start": v(-16.42, 2.83) * mm, "end": v(-16.42, 2.87) * mm});
            skLineSegment(sketch, "E1729", {"start": v(-16.42, 2.87) * mm, "end": v(-16.41, 2.9) * mm});
            skLineSegment(sketch, "E1730", {"start": v(-16.41, 2.9) * mm, "end": v(-16.4, 2.94) * mm});
            skLineSegment(sketch, "E1731", {"start": v(-16.4, 2.94) * mm, "end": v(-16.4, 2.98) * mm});
            skLineSegment(sketch, "E1732", {"start": v(-16.4, 2.98) * mm, "end": v(-16.38, 3.01) * mm});
            skLineSegment(sketch, "E1733", {"start": v(-16.38, 3.01) * mm, "end": v(-16.36, 3.04) * mm});
            skLineSegment(sketch, "E1734", {"start": v(-16.36, 3.04) * mm, "end": v(-16.35, 3.07) * mm});
            skLineSegment(sketch, "E1735", {"start": v(-16.35, 3.07) * mm, "end": v(-16.33, 3.1) * mm});
            skLineSegment(sketch, "E1736", {"start": v(-16.33, 3.1) * mm, "end": v(-16.3, 3.12) * mm});
            skLineSegment(sketch, "E1737", {"start": v(-16.3, 3.12) * mm, "end": v(-16.29, 3.14) * mm});
            skLineSegment(sketch, "E1738", {"start": v(-16.29, 3.14) * mm, "end": v(-16.26, 3.16) * mm});
            skLineSegment(sketch, "E1739", {"start": v(-16.26, 3.16) * mm, "end": v(-16.24, 3.17) * mm});
            skLineSegment(sketch, "E1740", {"start": v(-16.24, 3.17) * mm, "end": v(-16.2, 3.19) * mm});
            skLineSegment(sketch, "E1741", {"start": v(-16.2, 3.19) * mm, "end": v(-16.13, 3.23) * mm});
            skLineSegment(sketch, "E1742", {"start": v(-16.13, 3.23) * mm, "end": v(-16.06, 3.26) * mm});
            skLineSegment(sketch, "E1743", {"start": v(-16.06, 3.26) * mm, "end": v(-16.02, 3.29) * mm});
            skLineSegment(sketch, "E1744", {"start": v(-16.02, 3.29) * mm, "end": v(-16, 3.3) * mm});
            skLineSegment(sketch, "E1745", {"start": v(-16, 3.3) * mm, "end": v(-15.99, 3.3) * mm});
            skLineSegment(sketch, "E1746", {"start": v(-15.99, 3.3) * mm, "end": v(-15.98, 3.32) * mm});
            skLineSegment(sketch, "E1747", {"start": v(-15.98, 3.32) * mm, "end": v(-15.97, 3.33) * mm});
            skLineSegment(sketch, "E1748", {"start": v(-15.97, 3.33) * mm, "end": v(-15.96, 3.34) * mm});
            skLineSegment(sketch, "E1749", {"start": v(-15.96, 3.34) * mm, "end": v(-15.95, 3.36) * mm});
            skLineSegment(sketch, "E1750", {"start": v(-15.95, 3.36) * mm, "end": v(-15.95, 3.38) * mm});
            skLineSegment(sketch, "E1751", {"start": v(-15.95, 3.38) * mm, "end": v(-15.93, 3.42) * mm});
            skLineSegment(sketch, "E1752", {"start": v(-15.93, 3.42) * mm, "end": v(-15.92, 3.44) * mm});
            skLineSegment(sketch, "E1753", {"start": v(-15.92, 3.44) * mm, "end": v(-15.91, 3.46) * mm});
            skLineSegment(sketch, "E1754", {"start": v(-15.91, 3.46) * mm, "end": v(-15.9, 3.48) * mm});
            skLineSegment(sketch, "E1755", {"start": v(-15.9, 3.48) * mm, "end": v(-15.9, 3.5) * mm});
            skLineSegment(sketch, "E1756", {"start": v(-15.9, 3.5) * mm, "end": v(-15.89, 3.56) * mm});
            skLineSegment(sketch, "E1757", {"start": v(-15.89, 3.56) * mm, "end": v(-15.88, 3.62) * mm});
            skLineSegment(sketch, "E1758", {"start": v(-15.88, 3.62) * mm, "end": v(-15.87, 3.7) * mm});
            skLineSegment(sketch, "E1759", {"start": v(-15.87, 3.7) * mm, "end": v(-15.86, 3.76) * mm});
            skLineSegment(sketch, "E1760", {"start": v(-15.86, 3.76) * mm, "end": v(-15.86, 3.84) * mm});
            skLineSegment(sketch, "E1761", {"start": v(-15.86, 3.84) * mm, "end": v(-15.86, 3.93) * mm});
            skLineSegment(sketch, "E1762", {"start": v(-15.86, 3.93) * mm, "end": v(-15.86, 12.5) * mm});
            skLineSegment(sketch, "E1763", {"start": v(-15.86, 12.5) * mm, "end": v(-15.86, 12.61) * mm});
            skLineSegment(sketch, "E1764", {"start": v(-15.86, 12.61) * mm, "end": v(-15.86, 12.72) * mm});
            skLineSegment(sketch, "E1765", {"start": v(-15.86, 12.72) * mm, "end": v(-15.87, 12.82) * mm});
            skLineSegment(sketch, "E1766", {"start": v(-15.87, 12.82) * mm, "end": v(-15.87, 12.9) * mm});
            skLineSegment(sketch, "E1767", {"start": v(-15.87, 12.9) * mm, "end": v(-15.88, 13) * mm});
            skLineSegment(sketch, "E1768", {"start": v(-15.88, 13) * mm, "end": v(-15.89, 13.07) * mm});
            skLineSegment(sketch, "E1769", {"start": v(-15.89, 13.07) * mm, "end": v(-15.9, 13.13) * mm});
            skLineSegment(sketch, "E1770", {"start": v(-15.9, 13.13) * mm, "end": v(-15.9, 13.2) * mm});
            skLineSegment(sketch, "E1771", {"start": v(-15.9, 13.2) * mm, "end": v(-15.92, 13.24) * mm});
            skLineSegment(sketch, "E1772", {"start": v(-15.92, 13.24) * mm, "end": v(-15.93, 13.27) * mm});
            skLineSegment(sketch, "E1773", {"start": v(-15.93, 13.27) * mm, "end": v(-15.94, 13.29) * mm});
            skLineSegment(sketch, "E1774", {"start": v(-15.94, 13.29) * mm, "end": v(-15.95, 13.3) * mm});
            skLineSegment(sketch, "E1775", {"start": v(-15.95, 13.3) * mm, "end": v(-15.95, 13.33) * mm});
            skLineSegment(sketch, "E1776", {"start": v(-15.95, 13.33) * mm, "end": v(-15.96, 13.35) * mm});
            skLineSegment(sketch, "E1777", {"start": v(-15.96, 13.35) * mm, "end": v(-15.97, 13.36) * mm});
            skLineSegment(sketch, "E1778", {"start": v(-15.97, 13.36) * mm, "end": v(-15.98, 13.38) * mm});
            skLineSegment(sketch, "E1779", {"start": v(-15.98, 13.38) * mm, "end": v(-16, 13.4) * mm});
            skLineSegment(sketch, "E1780", {"start": v(-16, 13.4) * mm, "end": v(-16, 13.4) * mm});
            skLineSegment(sketch, "E1781", {"start": v(-16, 13.4) * mm, "end": v(-16.01, 13.41) * mm});
            skLineSegment(sketch, "E1782", {"start": v(-16.01, 13.41) * mm, "end": v(-16.03, 13.42) * mm});
            skLineSegment(sketch, "E1783", {"start": v(-16.03, 13.42) * mm, "end": v(-16.04, 13.43) * mm});
            skLineSegment(sketch, "E1784", {"start": v(-16.04, 13.43) * mm, "end": v(-16.05, 13.43) * mm});
            skLineSegment(sketch, "E1785", {"start": v(-16.05, 13.43) * mm, "end": v(-16.06, 13.44) * mm});
            skLineSegment(sketch, "E1786", {"start": v(-16.06, 13.44) * mm, "end": v(-16.23, 13.48) * mm});
            skLineSegment(sketch, "E1787", {"start": v(-16.23, 13.48) * mm, "end": v(-16.25, 13.5) * mm});
            skLineSegment(sketch, "E1788", {"start": v(-16.25, 13.5) * mm, "end": v(-16.28, 13.5) * mm});
            skLineSegment(sketch, "E1789", {"start": v(-16.28, 13.5) * mm, "end": v(-16.3, 13.52) * mm});
            skLineSegment(sketch, "E1790", {"start": v(-16.3, 13.52) * mm, "end": v(-16.32, 13.54) * mm});
            skLineSegment(sketch, "E1791", {"start": v(-16.32, 13.54) * mm, "end": v(-16.34, 13.55) * mm});
            skLineSegment(sketch, "E1792", {"start": v(-16.34, 13.55) * mm, "end": v(-16.36, 13.58) * mm});
            skLineSegment(sketch, "E1793", {"start": v(-16.36, 13.58) * mm, "end": v(-16.38, 13.6) * mm});
            skLineSegment(sketch, "E1794", {"start": v(-16.38, 13.6) * mm, "end": v(-16.4, 13.63) * mm});
            skLineSegment(sketch, "E1795", {"start": v(-16.4, 13.63) * mm, "end": v(-16.4, 13.65) * mm});
            skLineSegment(sketch, "E1796", {"start": v(-16.4, 13.65) * mm, "end": v(-16.42, 13.69) * mm});
            skLineSegment(sketch, "E1797", {"start": v(-16.42, 13.69) * mm, "end": v(-16.43, 13.72) * mm});
            skLineSegment(sketch, "E1798", {"start": v(-16.43, 13.72) * mm, "end": v(-16.43, 13.75) * mm});
            skLineSegment(sketch, "E1799", {"start": v(-16.43, 13.75) * mm, "end": v(-16.44, 13.8) * mm});
            skLineSegment(sketch, "E1800", {"start": v(-16.44, 13.8) * mm, "end": v(-16.44, 13.83) * mm});
            skLineSegment(sketch, "E1801", {"start": v(-16.44, 13.83) * mm, "end": v(-16.45, 13.88) * mm});
            skLineSegment(sketch, "E1802", {"start": v(-16.45, 13.88) * mm, "end": v(-16.45, 13.92) * mm});
            skLineSegment(sketch, "E1803", {"start": v(-16.45, 13.92) * mm, "end": v(-16.45, 13.96) * mm});
            skLineSegment(sketch, "E1804", {"start": v(-16.45, 13.96) * mm, "end": v(-16.44, 14) * mm});
            skLineSegment(sketch, "E1805", {"start": v(-16.44, 14) * mm, "end": v(-16.44, 14.03) * mm});
            skLineSegment(sketch, "E1806", {"start": v(-16.44, 14.03) * mm, "end": v(-16.44, 14.06) * mm});
            skLineSegment(sketch, "E1807", {"start": v(-16.44, 14.06) * mm, "end": v(-16.43, 14.1) * mm});
            skLineSegment(sketch, "E1808", {"start": v(-16.43, 14.1) * mm, "end": v(-16.43, 14.12) * mm});
            skLineSegment(sketch, "E1809", {"start": v(-16.43, 14.12) * mm, "end": v(-16.42, 14.15) * mm});
            skLineSegment(sketch, "E1810", {"start": v(-16.42, 14.15) * mm, "end": v(-16.41, 14.18) * mm});
            skLineSegment(sketch, "E1811", {"start": v(-16.41, 14.18) * mm, "end": v(-16.4, 14.21) * mm});
            skLineSegment(sketch, "E1812", {"start": v(-16.4, 14.21) * mm, "end": v(-16.4, 14.24) * mm});
            skLineSegment(sketch, "E1813", {"start": v(-16.4, 14.24) * mm, "end": v(-16.38, 14.27) * mm});
            skLineSegment(sketch, "E1814", {"start": v(-16.38, 14.27) * mm, "end": v(-16.37, 14.3) * mm});
            skLineSegment(sketch, "E1815", {"start": v(-16.37, 14.3) * mm, "end": v(-16.35, 14.31) * mm});
            skLineSegment(sketch, "E1816", {"start": v(-16.35, 14.31) * mm, "end": v(-16.34, 14.34) * mm});
            skLineSegment(sketch, "E1817", {"start": v(-16.34, 14.34) * mm, "end": v(-16.32, 14.36) * mm});
            skLineSegment(sketch, "E1818", {"start": v(-16.32, 14.36) * mm, "end": v(-16.3, 14.38) * mm});
            skLineSegment(sketch, "E1819", {"start": v(-16.3, 14.38) * mm, "end": v(-16.3, 14.39) * mm});
            skLineSegment(sketch, "E1820", {"start": v(-16.3, 14.39) * mm, "end": v(-16.29, 14.4) * mm});
            skLineSegment(sketch, "E1821", {"start": v(-16.29, 14.4) * mm, "end": v(-16.28, 14.4) * mm});
            skLineSegment(sketch, "E1822", {"start": v(-16.28, 14.4) * mm, "end": v(-16.26, 14.41) * mm});
            skLineSegment(sketch, "E1823", {"start": v(-16.26, 14.41) * mm, "end": v(-16.23, 14.43) * mm});
            skLineSegment(sketch, "E1824", {"start": v(-16.23, 14.43) * mm, "end": v(-16.2, 14.44) * mm});
            skLineSegment(sketch, "E1825", {"start": v(-16.2, 14.44) * mm, "end": v(-16.16, 14.45) * mm});
            skLineSegment(sketch, "E1826", {"start": v(-16.16, 14.45) * mm, "end": v(-16.12, 14.46) * mm});
            skLineSegment(sketch, "E1827", {"start": v(-16.12, 14.46) * mm, "end": v(-16.07, 14.47) * mm});
            skLineSegment(sketch, "E1828", {"start": v(-16.07, 14.47) * mm, "end": v(-16.02, 14.48) * mm});
            skLineSegment(sketch, "E1829", {"start": v(-16.02, 14.48) * mm, "end": v(-14.08, 14.68) * mm});
            skLineSegment(sketch, "E1830", {"start": v(-15.21, -2.01) * mm, "end": v(-15.23, -2.04) * mm});
            skLineSegment(sketch, "E1831", {"start": v(-15.23, -2.04) * mm, "end": v(-15.26, -2.06) * mm});
            skLineSegment(sketch, "E1832", {"start": v(-15.26, -2.06) * mm, "end": v(-15.28, -2.09) * mm});
            skLineSegment(sketch, "E1833", {"start": v(-15.28, -2.09) * mm, "end": v(-15.3, -2.11) * mm});
            skLineSegment(sketch, "E1834", {"start": v(-15.3, -2.11) * mm, "end": v(-15.32, -2.14) * mm});
            skLineSegment(sketch, "E1835", {"start": v(-15.32, -2.14) * mm, "end": v(-15.34, -2.17) * mm});
            skLineSegment(sketch, "E1836", {"start": v(-15.34, -2.17) * mm, "end": v(-15.35, -2.2) * mm});
            skLineSegment(sketch, "E1837", {"start": v(-15.35, -2.2) * mm, "end": v(-15.37, -2.22) * mm});
            skLineSegment(sketch, "E1838", {"start": v(-15.37, -2.22) * mm, "end": v(-15.39, -2.25) * mm});
            skLineSegment(sketch, "E1839", {"start": v(-15.39, -2.25) * mm, "end": v(-15.4, -2.27) * mm});
            skLineSegment(sketch, "E1840", {"start": v(-15.4, -2.27) * mm, "end": v(-15.41, -2.3) * mm});
            skLineSegment(sketch, "E1841", {"start": v(-15.41, -2.3) * mm, "end": v(-15.42, -2.33) * mm});
            skLineSegment(sketch, "E1842", {"start": v(-15.42, -2.33) * mm, "end": v(-15.44, -2.36) * mm});
            skLineSegment(sketch, "E1843", {"start": v(-15.44, -2.36) * mm, "end": v(-15.45, -2.38) * mm});
            skLineSegment(sketch, "E1844", {"start": v(-15.45, -2.38) * mm, "end": v(-15.45, -2.41) * mm});
            skLineSegment(sketch, "E1845", {"start": v(-15.45, -2.41) * mm, "end": v(-15.46, -2.44) * mm});
            skLineSegment(sketch, "E1846", {"start": v(-15.46, -2.44) * mm, "end": v(-15.47, -2.47) * mm});
            skLineSegment(sketch, "E1847", {"start": v(-15.47, -2.47) * mm, "end": v(-15.47, -2.5) * mm});
            skLineSegment(sketch, "E1848", {"start": v(-15.47, -2.5) * mm, "end": v(-15.49, -2.58) * mm});
            skLineSegment(sketch, "E1849", {"start": v(-15.49, -2.58) * mm, "end": v(-15.5, -2.67) * mm});
            skLineSegment(sketch, "E1850", {"start": v(-15.5, -2.67) * mm, "end": v(-15.5, -2.77) * mm});
            skLineSegment(sketch, "E1851", {"start": v(-15.5, -2.77) * mm, "end": v(-15.5, -2.88) * mm});
            skLineSegment(sketch, "E1852", {"start": v(-15.5, -2.88) * mm, "end": v(-15.51, -3) * mm});
            skLineSegment(sketch, "E1853", {"start": v(-15.51, -3) * mm, "end": v(-15.52, -3.14) * mm});
            skLineSegment(sketch, "E1854", {"start": v(-15.52, -3.14) * mm, "end": v(-15.52, -3.28) * mm});
            skLineSegment(sketch, "E1855", {"start": v(-15.52, -3.28) * mm, "end": v(-15.52, -5.8) * mm});
            skLineSegment(sketch, "E1856", {"start": v(-15.52, -5.8) * mm, "end": v(-15.52, -5.88) * mm});
            skLineSegment(sketch, "E1857", {"start": v(-15.52, -5.88) * mm, "end": v(-15.51, -5.96) * mm});
            skLineSegment(sketch, "E1858", {"start": v(-15.51, -5.96) * mm, "end": v(-15.5, -6.03) * mm});
            skLineSegment(sketch, "E1859", {"start": v(-15.5, -6.03) * mm, "end": v(-15.5, -6.1) * mm});
            skLineSegment(sketch, "E1860", {"start": v(-15.5, -6.1) * mm, "end": v(-15.5, -6.18) * mm});
            skLineSegment(sketch, "E1861", {"start": v(-15.5, -6.18) * mm, "end": v(-15.49, -6.25) * mm});
            skLineSegment(sketch, "E1862", {"start": v(-15.49, -6.25) * mm, "end": v(-15.47, -6.32) * mm});
            skLineSegment(sketch, "E1863", {"start": v(-15.47, -6.32) * mm, "end": v(-15.46, -6.39) * mm});
            skLineSegment(sketch, "E1864", {"start": v(-15.46, -6.39) * mm, "end": v(-15.45, -6.43) * mm});
            skLineSegment(sketch, "E1865", {"start": v(-15.45, -6.43) * mm, "end": v(-15.44, -6.47) * mm});
            skLineSegment(sketch, "E1866", {"start": v(-15.44, -6.47) * mm, "end": v(-15.43, -6.51) * mm});
            skLineSegment(sketch, "E1867", {"start": v(-15.43, -6.51) * mm, "end": v(-15.42, -6.55) * mm});
            skLineSegment(sketch, "E1868", {"start": v(-15.42, -6.55) * mm, "end": v(-15.4, -6.58) * mm});
            skLineSegment(sketch, "E1869", {"start": v(-15.4, -6.58) * mm, "end": v(-15.4, -6.61) * mm});
            skLineSegment(sketch, "E1870", {"start": v(-15.4, -6.61) * mm, "end": v(-15.38, -6.64) * mm});
            skLineSegment(sketch, "E1871", {"start": v(-15.38, -6.64) * mm, "end": v(-15.37, -6.67) * mm});
            skLineSegment(sketch, "E1872", {"start": v(-15.37, -6.67) * mm, "end": v(-15.35, -6.7) * mm});
            skLineSegment(sketch, "E1873", {"start": v(-15.35, -6.7) * mm, "end": v(-15.34, -6.72) * mm});
            skLineSegment(sketch, "E1874", {"start": v(-15.34, -6.72) * mm, "end": v(-15.32, -6.74) * mm});
            skLineSegment(sketch, "E1875", {"start": v(-15.32, -6.74) * mm, "end": v(-15.3, -6.77) * mm});
            skLineSegment(sketch, "E1876", {"start": v(-15.3, -6.77) * mm, "end": v(-15.28, -6.79) * mm});
            skLineSegment(sketch, "E1877", {"start": v(-15.28, -6.79) * mm, "end": v(-15.26, -6.8) * mm});
            skLineSegment(sketch, "E1878", {"start": v(-15.26, -6.8) * mm, "end": v(-15.23, -6.83) * mm});
            skLineSegment(sketch, "E1879", {"start": v(-15.23, -6.83) * mm, "end": v(-15.21, -6.85) * mm});
            skLineSegment(sketch, "E1880", {"start": v(-15.21, -6.85) * mm, "end": v(-15.21, -7.81) * mm});
            skLineSegment(sketch, "E1881", {"start": v(-15.21, -7.81) * mm, "end": v(-15.23, -7.83) * mm});
            skLineSegment(sketch, "E1882", {"start": v(-15.23, -7.83) * mm, "end": v(-15.25, -7.85) * mm});
            skLineSegment(sketch, "E1883", {"start": v(-15.25, -7.85) * mm, "end": v(-15.27, -7.86) * mm});
            skLineSegment(sketch, "E1884", {"start": v(-15.27, -7.86) * mm, "end": v(-15.29, -7.88) * mm});
            skLineSegment(sketch, "E1885", {"start": v(-15.29, -7.88) * mm, "end": v(-15.3, -7.9) * mm});
            skLineSegment(sketch, "E1886", {"start": v(-15.3, -7.9) * mm, "end": v(-15.32, -7.92) * mm});
            skLineSegment(sketch, "E1887", {"start": v(-15.32, -7.92) * mm, "end": v(-15.34, -7.94) * mm});
            skLineSegment(sketch, "E1888", {"start": v(-15.34, -7.94) * mm, "end": v(-15.35, -7.97) * mm});
            skLineSegment(sketch, "E1889", {"start": v(-15.35, -7.97) * mm, "end": v(-15.37, -7.99) * mm});
            skLineSegment(sketch, "E1890", {"start": v(-15.37, -7.99) * mm, "end": v(-15.38, -8.01) * mm});
            skLineSegment(sketch, "E1891", {"start": v(-15.38, -8.01) * mm, "end": v(-15.4, -8.04) * mm});
            skLineSegment(sketch, "E1892", {"start": v(-15.4, -8.04) * mm, "end": v(-15.4, -8.06) * mm});
            skLineSegment(sketch, "E1893", {"start": v(-15.4, -8.06) * mm, "end": v(-15.42, -8.09) * mm});
            skLineSegment(sketch, "E1894", {"start": v(-15.42, -8.09) * mm, "end": v(-15.43, -8.11) * mm});
            skLineSegment(sketch, "E1895", {"start": v(-15.43, -8.11) * mm, "end": v(-15.44, -8.14) * mm});
            skLineSegment(sketch, "E1896", {"start": v(-15.44, -8.14) * mm, "end": v(-15.45, -8.17) * mm});
            skLineSegment(sketch, "E1897", {"start": v(-15.45, -8.17) * mm, "end": v(-15.46, -8.2) * mm});
            skLineSegment(sketch, "E1898", {"start": v(-15.46, -8.2) * mm, "end": v(-15.46, -8.23) * mm});
            skLineSegment(sketch, "E1899", {"start": v(-15.46, -8.23) * mm, "end": v(-15.48, -8.3) * mm});
            skLineSegment(sketch, "E1900", {"start": v(-15.48, -8.3) * mm, "end": v(-15.5, -8.37) * mm});
            skLineSegment(sketch, "E1901", {"start": v(-15.5, -8.37) * mm, "end": v(-15.5, -8.45) * mm});
            skLineSegment(sketch, "E1902", {"start": v(-15.5, -8.45) * mm, "end": v(-15.5, -8.53) * mm});
            skLineSegment(sketch, "E1903", {"start": v(-15.5, -8.53) * mm, "end": v(-15.51, -8.62) * mm});
            skLineSegment(sketch, "E1904", {"start": v(-15.51, -8.62) * mm, "end": v(-15.52, -8.72) * mm});
            skLineSegment(sketch, "E1905", {"start": v(-15.52, -8.72) * mm, "end": v(-15.52, -8.82) * mm});
            skLineSegment(sketch, "E1906", {"start": v(-15.52, -8.82) * mm, "end": v(-15.52, -11.95) * mm});
            skLineSegment(sketch, "E1907", {"start": v(-15.52, -11.95) * mm, "end": v(-15.52, -12.04) * mm});
            skLineSegment(sketch, "E1908", {"start": v(-15.52, -12.04) * mm, "end": v(-15.51, -12.13) * mm});
            skLineSegment(sketch, "E1909", {"start": v(-15.51, -12.13) * mm, "end": v(-15.5, -12.2) * mm});
            skLineSegment(sketch, "E1910", {"start": v(-15.5, -12.2) * mm, "end": v(-15.5, -12.3) * mm});
            skLineSegment(sketch, "E1911", {"start": v(-15.5, -12.3) * mm, "end": v(-15.5, -12.37) * mm});
            skLineSegment(sketch, "E1912", {"start": v(-15.5, -12.37) * mm, "end": v(-15.48, -12.44) * mm});
            skLineSegment(sketch, "E1913", {"start": v(-15.48, -12.44) * mm, "end": v(-15.47, -12.51) * mm});
            skLineSegment(sketch, "E1914", {"start": v(-15.47, -12.51) * mm, "end": v(-15.46, -12.58) * mm});
            skLineSegment(sketch, "E1915", {"start": v(-15.46, -12.58) * mm, "end": v(-15.45, -12.62) * mm});
            skLineSegment(sketch, "E1916", {"start": v(-15.45, -12.62) * mm, "end": v(-15.44, -12.66) * mm});
            skLineSegment(sketch, "E1917", {"start": v(-15.44, -12.66) * mm, "end": v(-15.43, -12.7) * mm});
            skLineSegment(sketch, "E1918", {"start": v(-15.43, -12.7) * mm, "end": v(-15.42, -12.73) * mm});
            skLineSegment(sketch, "E1919", {"start": v(-15.42, -12.73) * mm, "end": v(-15.4, -12.76) * mm});
            skLineSegment(sketch, "E1920", {"start": v(-15.4, -12.76) * mm, "end": v(-15.4, -12.8) * mm});
            skLineSegment(sketch, "E1921", {"start": v(-15.4, -12.8) * mm, "end": v(-15.38, -12.82) * mm});
            skLineSegment(sketch, "E1922", {"start": v(-15.38, -12.82) * mm, "end": v(-15.37, -12.84) * mm});
            skLineSegment(sketch, "E1923", {"start": v(-15.37, -12.84) * mm, "end": v(-15.35, -12.86) * mm});
            skLineSegment(sketch, "E1924", {"start": v(-15.35, -12.86) * mm, "end": v(-15.34, -12.88) * mm});
            skLineSegment(sketch, "E1925", {"start": v(-15.34, -12.88) * mm, "end": v(-15.32, -12.9) * mm});
            skLineSegment(sketch, "E1926", {"start": v(-15.32, -12.9) * mm, "end": v(-15.3, -12.91) * mm});
            skLineSegment(sketch, "E1927", {"start": v(-15.3, -12.91) * mm, "end": v(-15.28, -12.93) * mm});
            skLineSegment(sketch, "E1928", {"start": v(-15.28, -12.93) * mm, "end": v(-15.26, -12.95) * mm});
            skLineSegment(sketch, "E1929", {"start": v(-15.26, -12.95) * mm, "end": v(-15.24, -12.96) * mm});
            skLineSegment(sketch, "E1930", {"start": v(-15.24, -12.96) * mm, "end": v(-15.21, -12.97) * mm});
            skLineSegment(sketch, "E1931", {"start": v(-15.21, -12.97) * mm, "end": v(-15.21, -13.93) * mm});
            skLineSegment(sketch, "E1932", {"start": v(-15.21, -13.93) * mm, "end": v(-15.3, -13.92) * mm});
            skLineSegment(sketch, "E1933", {"start": v(-15.3, -13.92) * mm, "end": v(-15.36, -13.92) * mm});
            skLineSegment(sketch, "E1934", {"start": v(-15.36, -13.92) * mm, "end": v(-15.41, -13.91) * mm});
            skLineSegment(sketch, "E1935", {"start": v(-15.41, -13.91) * mm, "end": v(-15.46, -13.91) * mm});
            skLineSegment(sketch, "E1936", {"start": v(-15.46, -13.91) * mm, "end": v(-15.51, -13.9) * mm});
            skLineSegment(sketch, "E1937", {"start": v(-15.51, -13.9) * mm, "end": v(-15.57, -13.9) * mm});
            skLineSegment(sketch, "E1938", {"start": v(-15.57, -13.9) * mm, "end": v(-15.62, -13.9) * mm});
            skLineSegment(sketch, "E1939", {"start": v(-15.62, -13.9) * mm, "end": v(-15.67, -13.88) * mm});
            skLineSegment(sketch, "E1940", {"start": v(-15.67, -13.88) * mm, "end": v(-15.72, -13.87) * mm});
            skLineSegment(sketch, "E1941", {"start": v(-15.72, -13.87) * mm, "end": v(-15.77, -13.86) * mm});
            skLineSegment(sketch, "E1942", {"start": v(-15.77, -13.86) * mm, "end": v(-15.83, -13.84) * mm});
            skLineSegment(sketch, "E1943", {"start": v(-15.83, -13.84) * mm, "end": v(-15.88, -13.83) * mm});
            skLineSegment(sketch, "E1944", {"start": v(-15.88, -13.83) * mm, "end": v(-15.93, -13.8) * mm});
            skLineSegment(sketch, "E1945", {"start": v(-15.93, -13.8) * mm, "end": v(-15.99, -13.8) * mm});
            skLineSegment(sketch, "E1946", {"start": v(-15.99, -13.8) * mm, "end": v(-16.04, -13.77) * mm});
            skLineSegment(sketch, "E1947", {"start": v(-16.04, -13.77) * mm, "end": v(-16.1, -13.75) * mm});
            skLineSegment(sketch, "E1948", {"start": v(-16.1, -13.75) * mm, "end": v(-16.15, -13.72) * mm});
            skLineSegment(sketch, "E1949", {"start": v(-16.15, -13.72) * mm, "end": v(-16.21, -13.7) * mm});
            skLineSegment(sketch, "E1950", {"start": v(-16.21, -13.7) * mm, "end": v(-16.27, -13.66) * mm});
            skLineSegment(sketch, "E1951", {"start": v(-16.27, -13.66) * mm, "end": v(-16.33, -13.63) * mm});
            skLineSegment(sketch, "E1952", {"start": v(-16.33, -13.63) * mm, "end": v(-16.38, -13.6) * mm});
            skLineSegment(sketch, "E1953", {"start": v(-16.38, -13.6) * mm, "end": v(-16.44, -13.56) * mm});
            skLineSegment(sketch, "E1954", {"start": v(-16.44, -13.56) * mm, "end": v(-16.49, -13.53) * mm});
            skLineSegment(sketch, "E1955", {"start": v(-16.49, -13.53) * mm, "end": v(-16.53, -13.5) * mm});
            skLineSegment(sketch, "E1956", {"start": v(-16.53, -13.5) * mm, "end": v(-16.58, -13.45) * mm});
            skLineSegment(sketch, "E1957", {"start": v(-16.58, -13.45) * mm, "end": v(-16.62, -13.42) * mm});
            skLineSegment(sketch, "E1958", {"start": v(-16.62, -13.42) * mm, "end": v(-16.66, -13.37) * mm});
            skLineSegment(sketch, "E1959", {"start": v(-16.66, -13.37) * mm, "end": v(-16.7, -13.33) * mm});
            skLineSegment(sketch, "E1960", {"start": v(-16.7, -13.33) * mm, "end": v(-16.74, -13.28) * mm});
            skLineSegment(sketch, "E1961", {"start": v(-16.74, -13.28) * mm, "end": v(-16.79, -13.23) * mm});
            skLineSegment(sketch, "E1962", {"start": v(-16.79, -13.23) * mm, "end": v(-16.83, -13.17) * mm});
            skLineSegment(sketch, "E1963", {"start": v(-16.83, -13.17) * mm, "end": v(-16.87, -13.11) * mm});
            skLineSegment(sketch, "E1964", {"start": v(-16.87, -13.11) * mm, "end": v(-16.9, -13.05) * mm});
            skLineSegment(sketch, "E1965", {"start": v(-16.9, -13.05) * mm, "end": v(-16.94, -13) * mm});
            skLineSegment(sketch, "E1966", {"start": v(-16.94, -13) * mm, "end": v(-16.97, -12.94) * mm});
            skLineSegment(sketch, "E1967", {"start": v(-16.97, -12.94) * mm, "end": v(-17, -12.88) * mm});
            skLineSegment(sketch, "E1968", {"start": v(-17, -12.88) * mm, "end": v(-17.03, -12.82) * mm});
            skLineSegment(sketch, "E1969", {"start": v(-17.03, -12.82) * mm, "end": v(-17.06, -12.76) * mm});
            skLineSegment(sketch, "E1970", {"start": v(-17.06, -12.76) * mm, "end": v(-17.08, -12.7) * mm});
            skLineSegment(sketch, "E1971", {"start": v(-17.08, -12.7) * mm, "end": v(-17.11, -12.64) * mm});
            skLineSegment(sketch, "E1972", {"start": v(-17.11, -12.64) * mm, "end": v(-17.14, -12.58) * mm});
            skLineSegment(sketch, "E1973", {"start": v(-17.14, -12.58) * mm, "end": v(-17.16, -12.51) * mm});
            skLineSegment(sketch, "E1974", {"start": v(-17.16, -12.51) * mm, "end": v(-17.18, -12.45) * mm});
            skLineSegment(sketch, "E1975", {"start": v(-17.18, -12.45) * mm, "end": v(-17.2, -12.38) * mm});
            skLineSegment(sketch, "E1976", {"start": v(-17.2, -12.38) * mm, "end": v(-17.23, -12.31) * mm});
            skLineSegment(sketch, "E1977", {"start": v(-17.23, -12.31) * mm, "end": v(-17.25, -12.24) * mm});
            skLineSegment(sketch, "E1978", {"start": v(-17.25, -12.24) * mm, "end": v(-17.27, -12.17) * mm});
            skLineSegment(sketch, "E1979", {"start": v(-17.27, -12.17) * mm, "end": v(-17.28, -12.1) * mm});
            skLineSegment(sketch, "E1980", {"start": v(-17.28, -12.1) * mm, "end": v(-17.3, -12.03) * mm});
            skLineSegment(sketch, "E1981", {"start": v(-17.3, -12.03) * mm, "end": v(-17.32, -11.96) * mm});
            skLineSegment(sketch, "E1982", {"start": v(-17.32, -11.96) * mm, "end": v(-17.33, -11.88) * mm});
            skLineSegment(sketch, "E1983", {"start": v(-17.33, -11.88) * mm, "end": v(-17.34, -11.8) * mm});
            skLineSegment(sketch, "E1984", {"start": v(-17.34, -11.8) * mm, "end": v(-17.36, -11.73) * mm});
            skLineSegment(sketch, "E1985", {"start": v(-17.36, -11.73) * mm, "end": v(-17.37, -11.65) * mm});
            skLineSegment(sketch, "E1986", {"start": v(-17.37, -11.65) * mm, "end": v(-17.38, -11.57) * mm});
            skLineSegment(sketch, "E1987", {"start": v(-17.38, -11.57) * mm, "end": v(-17.4, -11.5) * mm});
            skLineSegment(sketch, "E1988", {"start": v(-17.4, -11.5) * mm, "end": v(-17.4, -11.4) * mm});
            skLineSegment(sketch, "E1989", {"start": v(-17.4, -11.4) * mm, "end": v(-17.4, -11.33) * mm});
            skLineSegment(sketch, "E1990", {"start": v(-17.4, -11.33) * mm, "end": v(-17.41, -11.24) * mm});
            skLineSegment(sketch, "E1991", {"start": v(-17.41, -11.24) * mm, "end": v(-17.42, -11.16) * mm});
            skLineSegment(sketch, "E1992", {"start": v(-17.42, -11.16) * mm, "end": v(-17.42, -11.07) * mm});
            skLineSegment(sketch, "E1993", {"start": v(-17.42, -11.07) * mm, "end": v(-17.43, -10.98) * mm});
            skLineSegment(sketch, "E1994", {"start": v(-17.43, -10.98) * mm, "end": v(-17.43, -10.9) * mm});
            skLineSegment(sketch, "E1995", {"start": v(-17.43, -10.9) * mm, "end": v(-17.43, -10.8) * mm});
            skLineSegment(sketch, "E1996", {"start": v(-17.43, -10.8) * mm, "end": v(-17.43, -10.71) * mm});
            skLineSegment(sketch, "E1997", {"start": v(-17.43, -10.71) * mm, "end": v(-17.43, -10.61) * mm});
            skLineSegment(sketch, "E1998", {"start": v(-17.43, -10.61) * mm, "end": v(-17.43, -10.51) * mm});
            skLineSegment(sketch, "E1999", {"start": v(-17.43, -10.51) * mm, "end": v(-17.43, -10.41) * mm});
            skLineSegment(sketch, "E2000", {"start": v(-17.43, -10.41) * mm, "end": v(-17.42, -10.32) * mm});
            skLineSegment(sketch, "E2001", {"start": v(-17.42, -10.32) * mm, "end": v(-17.42, -10.22) * mm});
            skLineSegment(sketch, "E2002", {"start": v(-17.42, -10.22) * mm, "end": v(-17.4, -10.12) * mm});
            skLineSegment(sketch, "E2003", {"start": v(-17.4, -10.12) * mm, "end": v(-17.4, -10.03) * mm});
            skLineSegment(sketch, "E2004", {"start": v(-17.4, -10.03) * mm, "end": v(-17.4, -9.93) * mm});
            skLineSegment(sketch, "E2005", {"start": v(-17.4, -9.93) * mm, "end": v(-17.38, -9.84) * mm});
            skLineSegment(sketch, "E2006", {"start": v(-17.38, -9.84) * mm, "end": v(-17.37, -9.75) * mm});
            skLineSegment(sketch, "E2007", {"start": v(-17.37, -9.75) * mm, "end": v(-17.35, -9.66) * mm});
            skLineSegment(sketch, "E2008", {"start": v(-17.35, -9.66) * mm, "end": v(-17.34, -9.57) * mm});
            skLineSegment(sketch, "E2009", {"start": v(-17.34, -9.57) * mm, "end": v(-17.32, -9.48) * mm});
            skLineSegment(sketch, "E2010", {"start": v(-17.32, -9.48) * mm, "end": v(-17.3, -9.4) * mm});
            skLineSegment(sketch, "E2011", {"start": v(-17.3, -9.4) * mm, "end": v(-17.29, -9.3) * mm});
            skLineSegment(sketch, "E2012", {"start": v(-17.29, -9.3) * mm, "end": v(-17.27, -9.22) * mm});
            skLineSegment(sketch, "E2013", {"start": v(-17.27, -9.22) * mm, "end": v(-17.25, -9.14) * mm});
            skLineSegment(sketch, "E2014", {"start": v(-17.25, -9.14) * mm, "end": v(-17.22, -9.06) * mm});
            skLineSegment(sketch, "E2015", {"start": v(-17.22, -9.06) * mm, "end": v(-17.2, -8.98) * mm});
            skLineSegment(sketch, "E2016", {"start": v(-17.2, -8.98) * mm, "end": v(-17.17, -8.9) * mm});
            skLineSegment(sketch, "E2017", {"start": v(-17.17, -8.9) * mm, "end": v(-17.15, -8.82) * mm});
            skLineSegment(sketch, "E2018", {"start": v(-17.15, -8.82) * mm, "end": v(-17.12, -8.75) * mm});
            skLineSegment(sketch, "E2019", {"start": v(-17.12, -8.75) * mm, "end": v(-17.1, -8.67) * mm});
            skLineSegment(sketch, "E2020", {"start": v(-17.1, -8.67) * mm, "end": v(-17.07, -8.6) * mm});
            skLineSegment(sketch, "E2021", {"start": v(-17.07, -8.6) * mm, "end": v(-17.04, -8.53) * mm});
            skLineSegment(sketch, "E2022", {"start": v(-17.04, -8.53) * mm, "end": v(-17, -8.47) * mm});
            skLineSegment(sketch, "E2023", {"start": v(-17, -8.47) * mm, "end": v(-16.97, -8.4) * mm});
            skLineSegment(sketch, "E2024", {"start": v(-16.97, -8.4) * mm, "end": v(-16.94, -8.34) * mm});
            skLineSegment(sketch, "E2025", {"start": v(-16.94, -8.34) * mm, "end": v(-16.9, -8.27) * mm});
            skLineSegment(sketch, "E2026", {"start": v(-16.9, -8.27) * mm, "end": v(-16.87, -8.21) * mm});
            skLineSegment(sketch, "E2027", {"start": v(-16.87, -8.21) * mm, "end": v(-16.83, -8.15) * mm});
            skLineSegment(sketch, "E2028", {"start": v(-16.83, -8.15) * mm, "end": v(-16.8, -8.1) * mm});
            skLineSegment(sketch, "E2029", {"start": v(-16.8, -8.1) * mm, "end": v(-16.75, -8.03) * mm});
            skLineSegment(sketch, "E2030", {"start": v(-16.75, -8.03) * mm, "end": v(-16.7, -7.97) * mm});
            skLineSegment(sketch, "E2031", {"start": v(-16.7, -7.97) * mm, "end": v(-16.66, -7.92) * mm});
            skLineSegment(sketch, "E2032", {"start": v(-16.66, -7.92) * mm, "end": v(-16.62, -7.86) * mm});
            skLineSegment(sketch, "E2033", {"start": v(-16.62, -7.86) * mm, "end": v(-16.57, -7.81) * mm});
            skLineSegment(sketch, "E2034", {"start": v(-16.57, -7.81) * mm, "end": v(-16.53, -7.76) * mm});
            skLineSegment(sketch, "E2035", {"start": v(-16.53, -7.76) * mm, "end": v(-16.48, -7.72) * mm});
            skLineSegment(sketch, "E2036", {"start": v(-16.48, -7.72) * mm, "end": v(-16.43, -7.68) * mm});
            skLineSegment(sketch, "E2037", {"start": v(-16.43, -7.68) * mm, "end": v(-16.38, -7.63) * mm});
            skLineSegment(sketch, "E2038", {"start": v(-16.38, -7.63) * mm, "end": v(-16.33, -7.6) * mm});
            skLineSegment(sketch, "E2039", {"start": v(-16.33, -7.6) * mm, "end": v(-16.27, -7.55) * mm});
            skLineSegment(sketch, "E2040", {"start": v(-16.27, -7.55) * mm, "end": v(-16.2, -7.5) * mm});
            skLineSegment(sketch, "E2041", {"start": v(-16.2, -7.5) * mm, "end": v(-16.14, -7.46) * mm});
            skLineSegment(sketch, "E2042", {"start": v(-16.14, -7.46) * mm, "end": v(-16.07, -7.41) * mm});
            skLineSegment(sketch, "E2043", {"start": v(-16.07, -7.41) * mm, "end": v(-16, -7.37) * mm});
            skLineSegment(sketch, "E2044", {"start": v(-16, -7.37) * mm, "end": v(-15.92, -7.32) * mm});
            skLineSegment(sketch, "E2045", {"start": v(-15.92, -7.32) * mm, "end": v(-16, -7.27) * mm});
            skLineSegment(sketch, "E2046", {"start": v(-16, -7.27) * mm, "end": v(-16.07, -7.23) * mm});
            skLineSegment(sketch, "E2047", {"start": v(-16.07, -7.23) * mm, "end": v(-16.14, -7.18) * mm});
            skLineSegment(sketch, "E2048", {"start": v(-16.14, -7.18) * mm, "end": v(-16.2, -7.14) * mm});
            skLineSegment(sketch, "E2049", {"start": v(-16.2, -7.14) * mm, "end": v(-16.26, -7.1) * mm});
            skLineSegment(sketch, "E2050", {"start": v(-16.26, -7.1) * mm, "end": v(-16.32, -7.05) * mm});
            skLineSegment(sketch, "E2051", {"start": v(-16.32, -7.05) * mm, "end": v(-16.37, -7) * mm});
            skLineSegment(sketch, "E2052", {"start": v(-16.37, -7) * mm, "end": v(-16.42, -6.97) * mm});
            skLineSegment(sketch, "E2053", {"start": v(-16.42, -6.97) * mm, "end": v(-16.46, -6.92) * mm});
            skLineSegment(sketch, "E2054", {"start": v(-16.46, -6.92) * mm, "end": v(-16.5, -6.88) * mm});
            skLineSegment(sketch, "E2055", {"start": v(-16.5, -6.88) * mm, "end": v(-16.55, -6.83) * mm});
            skLineSegment(sketch, "E2056", {"start": v(-16.55, -6.83) * mm, "end": v(-16.6, -6.78) * mm});
            skLineSegment(sketch, "E2057", {"start": v(-16.6, -6.78) * mm, "end": v(-16.64, -6.72) * mm});
            skLineSegment(sketch, "E2058", {"start": v(-16.64, -6.72) * mm, "end": v(-16.68, -6.66) * mm});
            skLineSegment(sketch, "E2059", {"start": v(-16.68, -6.66) * mm, "end": v(-16.72, -6.6) * mm});
            skLineSegment(sketch, "E2060", {"start": v(-16.72, -6.6) * mm, "end": v(-16.76, -6.54) * mm});
            skLineSegment(sketch, "E2061", {"start": v(-16.76, -6.54) * mm, "end": v(-16.8, -6.5) * mm});
            skLineSegment(sketch, "E2062", {"start": v(-16.8, -6.5) * mm, "end": v(-16.82, -6.44) * mm});
            skLineSegment(sketch, "E2063", {"start": v(-16.82, -6.44) * mm, "end": v(-16.85, -6.39) * mm});
            skLineSegment(sketch, "E2064", {"start": v(-16.85, -6.39) * mm, "end": v(-16.88, -6.33) * mm});
            skLineSegment(sketch, "E2065", {"start": v(-16.88, -6.33) * mm, "end": v(-16.9, -6.28) * mm});
            skLineSegment(sketch, "E2066", {"start": v(-16.9, -6.28) * mm, "end": v(-16.93, -6.22) * mm});
            skLineSegment(sketch, "E2067", {"start": v(-16.93, -6.22) * mm, "end": v(-16.95, -6.16) * mm});
            skLineSegment(sketch, "E2068", {"start": v(-16.95, -6.16) * mm, "end": v(-16.98, -6.1) * mm});
            skLineSegment(sketch, "E2069", {"start": v(-16.98, -6.1) * mm, "end": v(-17, -6.04) * mm});
            skLineSegment(sketch, "E2070", {"start": v(-17, -6.04) * mm, "end": v(-17.02, -5.98) * mm});
            skLineSegment(sketch, "E2071", {"start": v(-17.02, -5.98) * mm, "end": v(-17.04, -5.92) * mm});
            skLineSegment(sketch, "E2072", {"start": v(-17.04, -5.92) * mm, "end": v(-17.06, -5.86) * mm});
            skLineSegment(sketch, "E2073", {"start": v(-17.06, -5.86) * mm, "end": v(-17.08, -5.8) * mm});
            skLineSegment(sketch, "E2074", {"start": v(-17.08, -5.8) * mm, "end": v(-17.1, -5.73) * mm});
            skLineSegment(sketch, "E2075", {"start": v(-17.1, -5.73) * mm, "end": v(-17.11, -5.67) * mm});
            skLineSegment(sketch, "E2076", {"start": v(-17.11, -5.67) * mm, "end": v(-17.13, -5.6) * mm});
            skLineSegment(sketch, "E2077", {"start": v(-17.13, -5.6) * mm, "end": v(-17.14, -5.53) * mm});
            skLineSegment(sketch, "E2078", {"start": v(-17.14, -5.53) * mm, "end": v(-17.16, -5.46) * mm});
            skLineSegment(sketch, "E2079", {"start": v(-17.16, -5.46) * mm, "end": v(-17.17, -5.4) * mm});
            skLineSegment(sketch, "E2080", {"start": v(-17.17, -5.4) * mm, "end": v(-17.18, -5.32) * mm});
            skLineSegment(sketch, "E2081", {"start": v(-17.18, -5.32) * mm, "end": v(-17.2, -5.25) * mm});
            skLineSegment(sketch, "E2082", {"start": v(-17.2, -5.25) * mm, "end": v(-17.2, -5.17) * mm});
            skLineSegment(sketch, "E2083", {"start": v(-17.2, -5.17) * mm, "end": v(-17.21, -5.1) * mm});
            skLineSegment(sketch, "E2084", {"start": v(-17.21, -5.1) * mm, "end": v(-17.22, -5.02) * mm});
            skLineSegment(sketch, "E2085", {"start": v(-17.22, -5.02) * mm, "end": v(-17.23, -4.95) * mm});
            skLineSegment(sketch, "E2086", {"start": v(-17.23, -4.95) * mm, "end": v(-17.23, -4.87) * mm});
            skLineSegment(sketch, "E2087", {"start": v(-17.23, -4.87) * mm, "end": v(-17.24, -4.8) * mm});
            skLineSegment(sketch, "E2088", {"start": v(-17.24, -4.8) * mm, "end": v(-17.24, -4.71) * mm});
            skLineSegment(sketch, "E2089", {"start": v(-17.24, -4.71) * mm, "end": v(-17.25, -4.63) * mm});
            skLineSegment(sketch, "E2090", {"start": v(-17.25, -4.63) * mm, "end": v(-17.25, -4.55) * mm});
            skLineSegment(sketch, "E2091", {"start": v(-17.25, -4.55) * mm, "end": v(-17.25, -4.47) * mm});
            skLineSegment(sketch, "E2092", {"start": v(-17.25, -4.47) * mm, "end": v(-17.25, -4.38) * mm});
            skLineSegment(sketch, "E2093", {"start": v(-17.25, -4.38) * mm, "end": v(-17.25, -4.27) * mm});
            skLineSegment(sketch, "E2094", {"start": v(-17.25, -4.27) * mm, "end": v(-17.25, -4.16) * mm});
            skLineSegment(sketch, "E2095", {"start": v(-17.25, -4.16) * mm, "end": v(-17.24, -4.05) * mm});
            skLineSegment(sketch, "E2096", {"start": v(-17.24, -4.05) * mm, "end": v(-17.24, -3.95) * mm});
            skLineSegment(sketch, "E2097", {"start": v(-17.24, -3.95) * mm, "end": v(-17.23, -3.84) * mm});
            skLineSegment(sketch, "E2098", {"start": v(-17.23, -3.84) * mm, "end": v(-17.22, -3.74) * mm});
            skLineSegment(sketch, "E2099", {"start": v(-17.22, -3.74) * mm, "end": v(-17.2, -3.64) * mm});
            skLineSegment(sketch, "E2100", {"start": v(-17.2, -3.64) * mm, "end": v(-17.2, -3.53) * mm});
            skLineSegment(sketch, "E2101", {"start": v(-17.2, -3.53) * mm, "end": v(-17.18, -3.43) * mm});
            skLineSegment(sketch, "E2102", {"start": v(-17.18, -3.43) * mm, "end": v(-17.16, -3.33) * mm});
            skLineSegment(sketch, "E2103", {"start": v(-17.16, -3.33) * mm, "end": v(-17.14, -3.24) * mm});
            skLineSegment(sketch, "E2104", {"start": v(-17.14, -3.24) * mm, "end": v(-17.12, -3.14) * mm});
            skLineSegment(sketch, "E2105", {"start": v(-17.12, -3.14) * mm, "end": v(-17.1, -3.04) * mm});
            skLineSegment(sketch, "E2106", {"start": v(-17.1, -3.04) * mm, "end": v(-17.08, -2.95) * mm});
            skLineSegment(sketch, "E2107", {"start": v(-17.08, -2.95) * mm, "end": v(-17.05, -2.86) * mm});
            skLineSegment(sketch, "E2108", {"start": v(-17.05, -2.86) * mm, "end": v(-17.03, -2.77) * mm});
            skLineSegment(sketch, "E2109", {"start": v(-17.03, -2.77) * mm, "end": v(-17, -2.68) * mm});
            skLineSegment(sketch, "E2110", {"start": v(-17, -2.68) * mm, "end": v(-16.97, -2.59) * mm});
            skLineSegment(sketch, "E2111", {"start": v(-16.97, -2.59) * mm, "end": v(-16.94, -2.5) * mm});
            skLineSegment(sketch, "E2112", {"start": v(-16.94, -2.5) * mm, "end": v(-16.9, -2.42) * mm});
            skLineSegment(sketch, "E2113", {"start": v(-16.9, -2.42) * mm, "end": v(-16.87, -2.34) * mm});
            skLineSegment(sketch, "E2114", {"start": v(-16.87, -2.34) * mm, "end": v(-16.83, -2.27) * mm});
            skLineSegment(sketch, "E2115", {"start": v(-16.83, -2.27) * mm, "end": v(-16.8, -2.2) * mm});
            skLineSegment(sketch, "E2116", {"start": v(-16.8, -2.2) * mm, "end": v(-16.76, -2.12) * mm});
            skLineSegment(sketch, "E2117", {"start": v(-16.76, -2.12) * mm, "end": v(-16.72, -2.05) * mm});
            skLineSegment(sketch, "E2118", {"start": v(-16.72, -2.05) * mm, "end": v(-16.68, -1.98) * mm});
            skLineSegment(sketch, "E2119", {"start": v(-16.68, -1.98) * mm, "end": v(-16.64, -1.92) * mm});
            skLineSegment(sketch, "E2120", {"start": v(-16.64, -1.92) * mm, "end": v(-16.6, -1.86) * mm});
            skLineSegment(sketch, "E2121", {"start": v(-16.6, -1.86) * mm, "end": v(-16.55, -1.8) * mm});
            skLineSegment(sketch, "E2122", {"start": v(-16.55, -1.8) * mm, "end": v(-16.5, -1.74) * mm});
            skLineSegment(sketch, "E2123", {"start": v(-16.5, -1.74) * mm, "end": v(-16.46, -1.69) * mm});
            skLineSegment(sketch, "E2124", {"start": v(-16.46, -1.69) * mm, "end": v(-16.4, -1.64) * mm});
            skLineSegment(sketch, "E2125", {"start": v(-16.4, -1.64) * mm, "end": v(-16.38, -1.6) * mm});
            skLineSegment(sketch, "E2126", {"start": v(-16.38, -1.6) * mm, "end": v(-16.35, -1.58) * mm});
            skLineSegment(sketch, "E2127", {"start": v(-16.35, -1.58) * mm, "end": v(-16.32, -1.56) * mm});
            skLineSegment(sketch, "E2128", {"start": v(-16.32, -1.56) * mm, "end": v(-16.3, -1.53) * mm});
            skLineSegment(sketch, "E2129", {"start": v(-16.3, -1.53) * mm, "end": v(-16.26, -1.5) * mm});
            skLineSegment(sketch, "E2130", {"start": v(-16.26, -1.5) * mm, "end": v(-16.23, -1.48) * mm});
            skLineSegment(sketch, "E2131", {"start": v(-16.23, -1.48) * mm, "end": v(-16.2, -1.46) * mm});
            skLineSegment(sketch, "E2132", {"start": v(-16.2, -1.46) * mm, "end": v(-16.17, -1.44) * mm});
            skLineSegment(sketch, "E2133", {"start": v(-16.17, -1.44) * mm, "end": v(-16.13, -1.41) * mm});
            skLineSegment(sketch, "E2134", {"start": v(-16.13, -1.41) * mm, "end": v(-16.1, -1.4) * mm});
            skLineSegment(sketch, "E2135", {"start": v(-16.1, -1.4) * mm, "end": v(-16.07, -1.37) * mm});
            skLineSegment(sketch, "E2136", {"start": v(-16.07, -1.37) * mm, "end": v(-16.03, -1.35) * mm});
            skLineSegment(sketch, "E2137", {"start": v(-16.03, -1.35) * mm, "end": v(-16, -1.34) * mm});
            skLineSegment(sketch, "E2138", {"start": v(-16, -1.34) * mm, "end": v(-15.96, -1.32) * mm});
            skLineSegment(sketch, "E2139", {"start": v(-15.96, -1.32) * mm, "end": v(-15.92, -1.3) * mm});
            skLineSegment(sketch, "E2140", {"start": v(-15.92, -1.3) * mm, "end": v(-15.89, -1.28) * mm});
            skLineSegment(sketch, "E2141", {"start": v(-15.89, -1.28) * mm, "end": v(-15.85, -1.27) * mm});
            skLineSegment(sketch, "E2142", {"start": v(-15.85, -1.27) * mm, "end": v(-15.81, -1.25) * mm});
            skLineSegment(sketch, "E2143", {"start": v(-15.81, -1.25) * mm, "end": v(-15.77, -1.24) * mm});
            skLineSegment(sketch, "E2144", {"start": v(-15.77, -1.24) * mm, "end": v(-15.73, -1.23) * mm});
            skLineSegment(sketch, "E2145", {"start": v(-15.73, -1.23) * mm, "end": v(-15.7, -1.21) * mm});
            skLineSegment(sketch, "E2146", {"start": v(-15.7, -1.21) * mm, "end": v(-15.65, -1.2) * mm});
            skLineSegment(sketch, "E2147", {"start": v(-15.65, -1.2) * mm, "end": v(-15.57, -1.18) * mm});
            skLineSegment(sketch, "E2148", {"start": v(-15.57, -1.18) * mm, "end": v(-15.48, -1.16) * mm});
            skLineSegment(sketch, "E2149", {"start": v(-15.48, -1.16) * mm, "end": v(-15.4, -1.15) * mm});
            skLineSegment(sketch, "E2150", {"start": v(-15.4, -1.15) * mm, "end": v(-15.3, -1.13) * mm});
            skLineSegment(sketch, "E2151", {"start": v(-15.3, -1.13) * mm, "end": v(-15.21, -1.12) * mm});
            skLineSegment(sketch, "E2152", {"start": v(-15.21, -1.12) * mm, "end": v(-15.21, -2.01) * mm});
            skLineSegment(sketch, "E2153", {"start": v(-14.89, -2.01) * mm, "end": v(-14.89, -1.12) * mm});
            skLineSegment(sketch, "E2154", {"start": v(-14.89, -1.12) * mm, "end": v(-14.8, -1.13) * mm});
            skLineSegment(sketch, "E2155", {"start": v(-14.8, -1.13) * mm, "end": v(-14.7, -1.15) * mm});
            skLineSegment(sketch, "E2156", {"start": v(-14.7, -1.15) * mm, "end": v(-14.62, -1.16) * mm});
            skLineSegment(sketch, "E2157", {"start": v(-14.62, -1.16) * mm, "end": v(-14.53, -1.18) * mm});
            skLineSegment(sketch, "E2158", {"start": v(-14.53, -1.18) * mm, "end": v(-14.45, -1.2) * mm});
            skLineSegment(sketch, "E2159", {"start": v(-14.45, -1.2) * mm, "end": v(-14.4, -1.21) * mm});
            skLineSegment(sketch, "E2160", {"start": v(-14.4, -1.21) * mm, "end": v(-14.36, -1.23) * mm});
            skLineSegment(sketch, "E2161", {"start": v(-14.36, -1.23) * mm, "end": v(-14.32, -1.24) * mm});
            skLineSegment(sketch, "E2162", {"start": v(-14.32, -1.24) * mm, "end": v(-14.29, -1.25) * mm});
            skLineSegment(sketch, "E2163", {"start": v(-14.29, -1.25) * mm, "end": v(-14.25, -1.27) * mm});
            skLineSegment(sketch, "E2164", {"start": v(-14.25, -1.27) * mm, "end": v(-14.2, -1.28) * mm});
            skLineSegment(sketch, "E2165", {"start": v(-14.2, -1.28) * mm, "end": v(-14.17, -1.3) * mm});
            skLineSegment(sketch, "E2166", {"start": v(-14.17, -1.3) * mm, "end": v(-14.13, -1.32) * mm});
            skLineSegment(sketch, "E2167", {"start": v(-14.13, -1.32) * mm, "end": v(-14.1, -1.34) * mm});
            skLineSegment(sketch, "E2168", {"start": v(-14.1, -1.34) * mm, "end": v(-14.06, -1.35) * mm});
            skLineSegment(sketch, "E2169", {"start": v(-14.06, -1.35) * mm, "end": v(-14.03, -1.37) * mm});
            skLineSegment(sketch, "E2170", {"start": v(-14.03, -1.37) * mm, "end": v(-14, -1.4) * mm});
            skLineSegment(sketch, "E2171", {"start": v(-14, -1.4) * mm, "end": v(-13.96, -1.41) * mm});
            skLineSegment(sketch, "E2172", {"start": v(-13.96, -1.41) * mm, "end": v(-13.93, -1.44) * mm});
            skLineSegment(sketch, "E2173", {"start": v(-13.93, -1.44) * mm, "end": v(-13.9, -1.46) * mm});
            skLineSegment(sketch, "E2174", {"start": v(-13.9, -1.46) * mm, "end": v(-13.86, -1.48) * mm});
            skLineSegment(sketch, "E2175", {"start": v(-13.86, -1.48) * mm, "end": v(-13.83, -1.5) * mm});
            skLineSegment(sketch, "E2176", {"start": v(-13.83, -1.5) * mm, "end": v(-13.8, -1.53) * mm});
            skLineSegment(sketch, "E2177", {"start": v(-13.8, -1.53) * mm, "end": v(-13.77, -1.56) * mm});
            skLineSegment(sketch, "E2178", {"start": v(-13.77, -1.56) * mm, "end": v(-13.74, -1.58) * mm});
            skLineSegment(sketch, "E2179", {"start": v(-13.74, -1.58) * mm, "end": v(-13.71, -1.6) * mm});
            skLineSegment(sketch, "E2180", {"start": v(-13.71, -1.6) * mm, "end": v(-13.69, -1.64) * mm});
            skLineSegment(sketch, "E2181", {"start": v(-13.69, -1.64) * mm, "end": v(-13.64, -1.69) * mm});
            skLineSegment(sketch, "E2182", {"start": v(-13.64, -1.69) * mm, "end": v(-13.6, -1.74) * mm});
            skLineSegment(sketch, "E2183", {"start": v(-13.6, -1.74) * mm, "end": v(-13.54, -1.8) * mm});
            skLineSegment(sketch, "E2184", {"start": v(-13.54, -1.8) * mm, "end": v(-13.5, -1.86) * mm});
            skLineSegment(sketch, "E2185", {"start": v(-13.5, -1.86) * mm, "end": v(-13.46, -1.92) * mm});
            skLineSegment(sketch, "E2186", {"start": v(-13.46, -1.92) * mm, "end": v(-13.41, -1.98) * mm});
            skLineSegment(sketch, "E2187", {"start": v(-13.41, -1.98) * mm, "end": v(-13.37, -2.05) * mm});
            skLineSegment(sketch, "E2188", {"start": v(-13.37, -2.05) * mm, "end": v(-13.33, -2.12) * mm});
            skLineSegment(sketch, "E2189", {"start": v(-13.33, -2.12) * mm, "end": v(-13.3, -2.2) * mm});
            skLineSegment(sketch, "E2190", {"start": v(-13.3, -2.2) * mm, "end": v(-13.26, -2.27) * mm});
            skLineSegment(sketch, "E2191", {"start": v(-13.26, -2.27) * mm, "end": v(-13.22, -2.34) * mm});
            skLineSegment(sketch, "E2192", {"start": v(-13.22, -2.34) * mm, "end": v(-13.2, -2.42) * mm});
            skLineSegment(sketch, "E2193", {"start": v(-13.2, -2.42) * mm, "end": v(-13.16, -2.5) * mm});
            skLineSegment(sketch, "E2194", {"start": v(-13.16, -2.5) * mm, "end": v(-13.13, -2.59) * mm});
            skLineSegment(sketch, "E2195", {"start": v(-13.13, -2.59) * mm, "end": v(-13.1, -2.68) * mm});
            skLineSegment(sketch, "E2196", {"start": v(-13.1, -2.68) * mm, "end": v(-13.07, -2.77) * mm});
            skLineSegment(sketch, "E2197", {"start": v(-13.07, -2.77) * mm, "end": v(-13.04, -2.86) * mm});
            skLineSegment(sketch, "E2198", {"start": v(-13.04, -2.86) * mm, "end": v(-13.02, -2.95) * mm});
            skLineSegment(sketch, "E2199", {"start": v(-13.02, -2.95) * mm, "end": v(-13, -3.04) * mm});
            skLineSegment(sketch, "E2200", {"start": v(-13, -3.04) * mm, "end": v(-12.97, -3.14) * mm});
            skLineSegment(sketch, "E2201", {"start": v(-12.97, -3.14) * mm, "end": v(-12.95, -3.24) * mm});
            skLineSegment(sketch, "E2202", {"start": v(-12.95, -3.24) * mm, "end": v(-12.93, -3.33) * mm});
            skLineSegment(sketch, "E2203", {"start": v(-12.93, -3.33) * mm, "end": v(-12.91, -3.43) * mm});
            skLineSegment(sketch, "E2204", {"start": v(-12.91, -3.43) * mm, "end": v(-12.9, -3.53) * mm});
            skLineSegment(sketch, "E2205", {"start": v(-12.9, -3.53) * mm, "end": v(-12.89, -3.64) * mm});
            skLineSegment(sketch, "E2206", {"start": v(-12.89, -3.64) * mm, "end": v(-12.88, -3.74) * mm});
            skLineSegment(sketch, "E2207", {"start": v(-12.88, -3.74) * mm, "end": v(-12.87, -3.84) * mm});
            skLineSegment(sketch, "E2208", {"start": v(-12.87, -3.84) * mm, "end": v(-12.86, -3.95) * mm});
            skLineSegment(sketch, "E2209", {"start": v(-12.86, -3.95) * mm, "end": v(-12.85, -4.05) * mm});
            skLineSegment(sketch, "E2210", {"start": v(-12.85, -4.05) * mm, "end": v(-12.85, -4.16) * mm});
            skLineSegment(sketch, "E2211", {"start": v(-12.85, -4.16) * mm, "end": v(-12.84, -4.27) * mm});
            skLineSegment(sketch, "E2212", {"start": v(-12.84, -4.27) * mm, "end": v(-12.84, -4.38) * mm});
            skLineSegment(sketch, "E2213", {"start": v(-12.84, -4.38) * mm, "end": v(-12.84, -4.47) * mm});
            skLineSegment(sketch, "E2214", {"start": v(-12.84, -4.47) * mm, "end": v(-12.85, -4.55) * mm});
            skLineSegment(sketch, "E2215", {"start": v(-12.85, -4.55) * mm, "end": v(-12.85, -4.63) * mm});
            skLineSegment(sketch, "E2216", {"start": v(-12.85, -4.63) * mm, "end": v(-12.85, -4.71) * mm});
            skLineSegment(sketch, "E2217", {"start": v(-12.85, -4.71) * mm, "end": v(-12.86, -4.8) * mm});
            skLineSegment(sketch, "E2218", {"start": v(-12.86, -4.8) * mm, "end": v(-12.86, -4.87) * mm});
            skLineSegment(sketch, "E2219", {"start": v(-12.86, -4.87) * mm, "end": v(-12.87, -4.95) * mm});
            skLineSegment(sketch, "E2220", {"start": v(-12.87, -4.95) * mm, "end": v(-12.87, -5.02) * mm});
            skLineSegment(sketch, "E2221", {"start": v(-12.87, -5.02) * mm, "end": v(-12.88, -5.1) * mm});
            skLineSegment(sketch, "E2222", {"start": v(-12.88, -5.1) * mm, "end": v(-12.9, -5.17) * mm});
            skLineSegment(sketch, "E2223", {"start": v(-12.9, -5.17) * mm, "end": v(-12.9, -5.25) * mm});
            skLineSegment(sketch, "E2224", {"start": v(-12.9, -5.25) * mm, "end": v(-12.91, -5.32) * mm});
            skLineSegment(sketch, "E2225", {"start": v(-12.91, -5.32) * mm, "end": v(-12.92, -5.4) * mm});
            skLineSegment(sketch, "E2226", {"start": v(-12.92, -5.4) * mm, "end": v(-12.94, -5.46) * mm});
            skLineSegment(sketch, "E2227", {"start": v(-12.94, -5.46) * mm, "end": v(-12.95, -5.53) * mm});
            skLineSegment(sketch, "E2228", {"start": v(-12.95, -5.53) * mm, "end": v(-12.97, -5.6) * mm});
            skLineSegment(sketch, "E2229", {"start": v(-12.97, -5.6) * mm, "end": v(-12.98, -5.67) * mm});
            skLineSegment(sketch, "E2230", {"start": v(-12.98, -5.67) * mm, "end": v(-13, -5.73) * mm});
            skLineSegment(sketch, "E2231", {"start": v(-13, -5.73) * mm, "end": v(-13.02, -5.8) * mm});
            skLineSegment(sketch, "E2232", {"start": v(-13.02, -5.8) * mm, "end": v(-13.04, -5.86) * mm});
            skLineSegment(sketch, "E2233", {"start": v(-13.04, -5.86) * mm, "end": v(-13.05, -5.92) * mm});
            skLineSegment(sketch, "E2234", {"start": v(-13.05, -5.92) * mm, "end": v(-13.08, -5.98) * mm});
            skLineSegment(sketch, "E2235", {"start": v(-13.08, -5.98) * mm, "end": v(-13.1, -6.04) * mm});
            skLineSegment(sketch, "E2236", {"start": v(-13.1, -6.04) * mm, "end": v(-13.12, -6.1) * mm});
            skLineSegment(sketch, "E2237", {"start": v(-13.12, -6.1) * mm, "end": v(-13.14, -6.16) * mm});
            skLineSegment(sketch, "E2238", {"start": v(-13.14, -6.16) * mm, "end": v(-13.17, -6.22) * mm});
            skLineSegment(sketch, "E2239", {"start": v(-13.17, -6.22) * mm, "end": v(-13.2, -6.28) * mm});
            skLineSegment(sketch, "E2240", {"start": v(-13.2, -6.28) * mm, "end": v(-13.22, -6.33) * mm});
            skLineSegment(sketch, "E2241", {"start": v(-13.22, -6.33) * mm, "end": v(-13.25, -6.39) * mm});
            skLineSegment(sketch, "E2242", {"start": v(-13.25, -6.39) * mm, "end": v(-13.27, -6.44) * mm});
            skLineSegment(sketch, "E2243", {"start": v(-13.27, -6.44) * mm, "end": v(-13.3, -6.5) * mm});
            skLineSegment(sketch, "E2244", {"start": v(-13.3, -6.5) * mm, "end": v(-13.33, -6.54) * mm});
            skLineSegment(sketch, "E2245", {"start": v(-13.33, -6.54) * mm, "end": v(-13.37, -6.6) * mm});
            skLineSegment(sketch, "E2246", {"start": v(-13.37, -6.6) * mm, "end": v(-13.41, -6.66) * mm});
            skLineSegment(sketch, "E2247", {"start": v(-13.41, -6.66) * mm, "end": v(-13.46, -6.72) * mm});
            skLineSegment(sketch, "E2248", {"start": v(-13.46, -6.72) * mm, "end": v(-13.5, -6.78) * mm});
            skLineSegment(sketch, "E2249", {"start": v(-13.5, -6.78) * mm, "end": v(-13.54, -6.83) * mm});
            skLineSegment(sketch, "E2250", {"start": v(-13.54, -6.83) * mm, "end": v(-13.58, -6.88) * mm});
            skLineSegment(sketch, "E2251", {"start": v(-13.58, -6.88) * mm, "end": v(-13.63, -6.92) * mm});
            skLineSegment(sketch, "E2252", {"start": v(-13.63, -6.92) * mm, "end": v(-13.68, -6.97) * mm});
            skLineSegment(sketch, "E2253", {"start": v(-13.68, -6.97) * mm, "end": v(-13.72, -7) * mm});
            skLineSegment(sketch, "E2254", {"start": v(-13.72, -7) * mm, "end": v(-13.78, -7.05) * mm});
            skLineSegment(sketch, "E2255", {"start": v(-13.78, -7.05) * mm, "end": v(-13.83, -7.1) * mm});
            skLineSegment(sketch, "E2256", {"start": v(-13.83, -7.1) * mm, "end": v(-13.9, -7.14) * mm});
            skLineSegment(sketch, "E2257", {"start": v(-13.9, -7.14) * mm, "end": v(-13.96, -7.18) * mm});
            skLineSegment(sketch, "E2258", {"start": v(-13.96, -7.18) * mm, "end": v(-14.03, -7.23) * mm});
            skLineSegment(sketch, "E2259", {"start": v(-14.03, -7.23) * mm, "end": v(-14.1, -7.27) * mm});
            skLineSegment(sketch, "E2260", {"start": v(-14.1, -7.27) * mm, "end": v(-14.18, -7.32) * mm});
            skLineSegment(sketch, "E2261", {"start": v(-14.18, -7.32) * mm, "end": v(-14.1, -7.37) * mm});
            skLineSegment(sketch, "E2262", {"start": v(-14.1, -7.37) * mm, "end": v(-14.02, -7.41) * mm});
            skLineSegment(sketch, "E2263", {"start": v(-14.02, -7.41) * mm, "end": v(-13.95, -7.46) * mm});
            skLineSegment(sketch, "E2264", {"start": v(-13.95, -7.46) * mm, "end": v(-13.88, -7.5) * mm});
            skLineSegment(sketch, "E2265", {"start": v(-13.88, -7.5) * mm, "end": v(-13.82, -7.55) * mm});
            skLineSegment(sketch, "E2266", {"start": v(-13.82, -7.55) * mm, "end": v(-13.76, -7.6) * mm});
            skLineSegment(sketch, "E2267", {"start": v(-13.76, -7.6) * mm, "end": v(-13.71, -7.63) * mm});
            skLineSegment(sketch, "E2268", {"start": v(-13.71, -7.63) * mm, "end": v(-13.66, -7.68) * mm});
            skLineSegment(sketch, "E2269", {"start": v(-13.66, -7.68) * mm, "end": v(-13.61, -7.72) * mm});
            skLineSegment(sketch, "E2270", {"start": v(-13.61, -7.72) * mm, "end": v(-13.57, -7.76) * mm});
            skLineSegment(sketch, "E2271", {"start": v(-13.57, -7.76) * mm, "end": v(-13.52, -7.81) * mm});
            skLineSegment(sketch, "E2272", {"start": v(-13.52, -7.81) * mm, "end": v(-13.48, -7.86) * mm});
            skLineSegment(sketch, "E2273", {"start": v(-13.48, -7.86) * mm, "end": v(-13.43, -7.92) * mm});
            skLineSegment(sketch, "E2274", {"start": v(-13.43, -7.92) * mm, "end": v(-13.39, -7.97) * mm});
            skLineSegment(sketch, "E2275", {"start": v(-13.39, -7.97) * mm, "end": v(-13.34, -8.03) * mm});
            skLineSegment(sketch, "E2276", {"start": v(-13.34, -8.03) * mm, "end": v(-13.3, -8.1) * mm});
            skLineSegment(sketch, "E2277", {"start": v(-13.3, -8.1) * mm, "end": v(-13.26, -8.15) * mm});
            skLineSegment(sketch, "E2278", {"start": v(-13.26, -8.15) * mm, "end": v(-13.23, -8.21) * mm});
            skLineSegment(sketch, "E2279", {"start": v(-13.23, -8.21) * mm, "end": v(-13.2, -8.27) * mm});
            skLineSegment(sketch, "E2280", {"start": v(-13.2, -8.27) * mm, "end": v(-13.16, -8.34) * mm});
            skLineSegment(sketch, "E2281", {"start": v(-13.16, -8.34) * mm, "end": v(-13.12, -8.4) * mm});
            skLineSegment(sketch, "E2282", {"start": v(-13.12, -8.4) * mm, "end": v(-13.09, -8.47) * mm});
            skLineSegment(sketch, "E2283", {"start": v(-13.09, -8.47) * mm, "end": v(-13.06, -8.53) * mm});
            skLineSegment(sketch, "E2284", {"start": v(-13.06, -8.53) * mm, "end": v(-13.03, -8.6) * mm});
            skLineSegment(sketch, "E2285", {"start": v(-13.03, -8.6) * mm, "end": v(-13, -8.67) * mm});
            skLineSegment(sketch, "E2286", {"start": v(-13, -8.67) * mm, "end": v(-12.97, -8.75) * mm});
            skLineSegment(sketch, "E2287", {"start": v(-12.97, -8.75) * mm, "end": v(-12.94, -8.82) * mm});
            skLineSegment(sketch, "E2288", {"start": v(-12.94, -8.82) * mm, "end": v(-12.92, -8.9) * mm});
            skLineSegment(sketch, "E2289", {"start": v(-12.92, -8.9) * mm, "end": v(-12.9, -8.98) * mm});
            skLineSegment(sketch, "E2290", {"start": v(-12.9, -8.98) * mm, "end": v(-12.87, -9.06) * mm});
            skLineSegment(sketch, "E2291", {"start": v(-12.87, -9.06) * mm, "end": v(-12.85, -9.14) * mm});
            skLineSegment(sketch, "E2292", {"start": v(-12.85, -9.14) * mm, "end": v(-12.83, -9.22) * mm});
            skLineSegment(sketch, "E2293", {"start": v(-12.83, -9.22) * mm, "end": v(-12.8, -9.3) * mm});
            skLineSegment(sketch, "E2294", {"start": v(-12.8, -9.3) * mm, "end": v(-12.79, -9.4) * mm});
            skLineSegment(sketch, "E2295", {"start": v(-12.79, -9.4) * mm, "end": v(-12.77, -9.48) * mm});
            skLineSegment(sketch, "E2296", {"start": v(-12.77, -9.48) * mm, "end": v(-12.76, -9.57) * mm});
            skLineSegment(sketch, "E2297", {"start": v(-12.76, -9.57) * mm, "end": v(-12.74, -9.66) * mm});
            skLineSegment(sketch, "E2298", {"start": v(-12.74, -9.66) * mm, "end": v(-12.73, -9.75) * mm});
            skLineSegment(sketch, "E2299", {"start": v(-12.73, -9.75) * mm, "end": v(-12.71, -9.84) * mm});
            skLineSegment(sketch, "E2300", {"start": v(-12.71, -9.84) * mm, "end": v(-12.7, -9.93) * mm});
            skLineSegment(sketch, "E2301", {"start": v(-12.7, -9.93) * mm, "end": v(-12.7, -10.03) * mm});
            skLineSegment(sketch, "E2302", {"start": v(-12.7, -10.03) * mm, "end": v(-12.69, -10.12) * mm});
            skLineSegment(sketch, "E2303", {"start": v(-12.69, -10.12) * mm, "end": v(-12.68, -10.22) * mm});
            skLineSegment(sketch, "E2304", {"start": v(-12.68, -10.22) * mm, "end": v(-12.67, -10.32) * mm});
            skLineSegment(sketch, "E2305", {"start": v(-12.67, -10.32) * mm, "end": v(-12.67, -10.41) * mm});
            skLineSegment(sketch, "E2306", {"start": v(-12.67, -10.41) * mm, "end": v(-12.66, -10.51) * mm});
            skLineSegment(sketch, "E2307", {"start": v(-12.66, -10.51) * mm, "end": v(-12.66, -10.61) * mm});
            skLineSegment(sketch, "E2308", {"start": v(-12.66, -10.61) * mm, "end": v(-12.66, -10.71) * mm});
            skLineSegment(sketch, "E2309", {"start": v(-12.66, -10.71) * mm, "end": v(-12.66, -10.8) * mm});
            skLineSegment(sketch, "E2310", {"start": v(-12.66, -10.8) * mm, "end": v(-12.66, -10.9) * mm});
            skLineSegment(sketch, "E2311", {"start": v(-12.66, -10.9) * mm, "end": v(-12.67, -10.98) * mm});
            skLineSegment(sketch, "E2312", {"start": v(-12.67, -10.98) * mm, "end": v(-12.67, -11.07) * mm});
            skLineSegment(sketch, "E2313", {"start": v(-12.67, -11.07) * mm, "end": v(-12.68, -11.16) * mm});
            skLineSegment(sketch, "E2314", {"start": v(-12.68, -11.16) * mm, "end": v(-12.68, -11.24) * mm});
            skLineSegment(sketch, "E2315", {"start": v(-12.68, -11.24) * mm, "end": v(-12.69, -11.33) * mm});
            skLineSegment(sketch, "E2316", {"start": v(-12.69, -11.33) * mm, "end": v(-12.7, -11.4) * mm});
            skLineSegment(sketch, "E2317", {"start": v(-12.7, -11.4) * mm, "end": v(-12.7, -11.5) * mm});
            skLineSegment(sketch, "E2318", {"start": v(-12.7, -11.5) * mm, "end": v(-12.71, -11.57) * mm});
            skLineSegment(sketch, "E2319", {"start": v(-12.71, -11.57) * mm, "end": v(-12.72, -11.65) * mm});
            skLineSegment(sketch, "E2320", {"start": v(-12.72, -11.65) * mm, "end": v(-12.74, -11.73) * mm});
            skLineSegment(sketch, "E2321", {"start": v(-12.74, -11.73) * mm, "end": v(-12.75, -11.8) * mm});
            skLineSegment(sketch, "E2322", {"start": v(-12.75, -11.8) * mm, "end": v(-12.76, -11.88) * mm});
            skLineSegment(sketch, "E2323", {"start": v(-12.76, -11.88) * mm, "end": v(-12.78, -11.96) * mm});
            skLineSegment(sketch, "E2324", {"start": v(-12.78, -11.96) * mm, "end": v(-12.8, -12.03) * mm});
            skLineSegment(sketch, "E2325", {"start": v(-12.8, -12.03) * mm, "end": v(-12.81, -12.1) * mm});
            skLineSegment(sketch, "E2326", {"start": v(-12.81, -12.1) * mm, "end": v(-12.83, -12.17) * mm});
            skLineSegment(sketch, "E2327", {"start": v(-12.83, -12.17) * mm, "end": v(-12.85, -12.24) * mm});
            skLineSegment(sketch, "E2328", {"start": v(-12.85, -12.24) * mm, "end": v(-12.87, -12.31) * mm});
            skLineSegment(sketch, "E2329", {"start": v(-12.87, -12.31) * mm, "end": v(-12.89, -12.38) * mm});
            skLineSegment(sketch, "E2330", {"start": v(-12.89, -12.38) * mm, "end": v(-12.91, -12.45) * mm});
            skLineSegment(sketch, "E2331", {"start": v(-12.91, -12.45) * mm, "end": v(-12.93, -12.51) * mm});
            skLineSegment(sketch, "E2332", {"start": v(-12.93, -12.51) * mm, "end": v(-12.96, -12.58) * mm});
            skLineSegment(sketch, "E2333", {"start": v(-12.96, -12.58) * mm, "end": v(-12.98, -12.64) * mm});
            skLineSegment(sketch, "E2334", {"start": v(-12.98, -12.64) * mm, "end": v(-13, -12.7) * mm});
            skLineSegment(sketch, "E2335", {"start": v(-13, -12.7) * mm, "end": v(-13.04, -12.76) * mm});
            skLineSegment(sketch, "E2336", {"start": v(-13.04, -12.76) * mm, "end": v(-13.07, -12.82) * mm});
            skLineSegment(sketch, "E2337", {"start": v(-13.07, -12.82) * mm, "end": v(-13.1, -12.88) * mm});
            skLineSegment(sketch, "E2338", {"start": v(-13.1, -12.88) * mm, "end": v(-13.12, -12.94) * mm});
            skLineSegment(sketch, "E2339", {"start": v(-13.12, -12.94) * mm, "end": v(-13.16, -13) * mm});
            skLineSegment(sketch, "E2340", {"start": v(-13.16, -13) * mm, "end": v(-13.19, -13.05) * mm});
            skLineSegment(sketch, "E2341", {"start": v(-13.19, -13.05) * mm, "end": v(-13.23, -13.11) * mm});
            skLineSegment(sketch, "E2342", {"start": v(-13.23, -13.11) * mm, "end": v(-13.27, -13.17) * mm});
            skLineSegment(sketch, "E2343", {"start": v(-13.27, -13.17) * mm, "end": v(-13.3, -13.23) * mm});
            skLineSegment(sketch, "E2344", {"start": v(-13.3, -13.23) * mm, "end": v(-13.35, -13.28) * mm});
            skLineSegment(sketch, "E2345", {"start": v(-13.35, -13.28) * mm, "end": v(-13.4, -13.33) * mm});
            skLineSegment(sketch, "E2346", {"start": v(-13.4, -13.33) * mm, "end": v(-13.43, -13.38) * mm});
            skLineSegment(sketch, "E2347", {"start": v(-13.43, -13.38) * mm, "end": v(-13.47, -13.42) * mm});
            skLineSegment(sketch, "E2348", {"start": v(-13.47, -13.42) * mm, "end": v(-13.52, -13.46) * mm});
            skLineSegment(sketch, "E2349", {"start": v(-13.52, -13.46) * mm, "end": v(-13.56, -13.5) * mm});
            skLineSegment(sketch, "E2350", {"start": v(-13.56, -13.5) * mm, "end": v(-13.6, -13.54) * mm});
            skLineSegment(sketch, "E2351", {"start": v(-13.6, -13.54) * mm, "end": v(-13.66, -13.57) * mm});
            skLineSegment(sketch, "E2352", {"start": v(-13.66, -13.57) * mm, "end": v(-13.7, -13.6) * mm});
            skLineSegment(sketch, "E2353", {"start": v(-13.7, -13.6) * mm, "end": v(-13.77, -13.64) * mm});
            skLineSegment(sketch, "E2354", {"start": v(-13.77, -13.64) * mm, "end": v(-13.82, -13.67) * mm});
            skLineSegment(sketch, "E2355", {"start": v(-13.82, -13.67) * mm, "end": v(-13.88, -13.7) * mm});
            skLineSegment(sketch, "E2356", {"start": v(-13.88, -13.7) * mm, "end": v(-13.95, -13.72) * mm});
            skLineSegment(sketch, "E2357", {"start": v(-13.95, -13.72) * mm, "end": v(-14, -13.74) * mm});
            skLineSegment(sketch, "E2358", {"start": v(-14, -13.74) * mm, "end": v(-14.04, -13.76) * mm});
            skLineSegment(sketch, "E2359", {"start": v(-14.04, -13.76) * mm, "end": v(-14.09, -13.78) * mm});
            skLineSegment(sketch, "E2360", {"start": v(-14.09, -13.78) * mm, "end": v(-14.14, -13.8) * mm});
            skLineSegment(sketch, "E2361", {"start": v(-14.14, -13.8) * mm, "end": v(-14.19, -13.81) * mm});
            skLineSegment(sketch, "E2362", {"start": v(-14.19, -13.81) * mm, "end": v(-14.24, -13.82) * mm});
            skLineSegment(sketch, "E2363", {"start": v(-14.24, -13.82) * mm, "end": v(-14.3, -13.84) * mm});
            skLineSegment(sketch, "E2364", {"start": v(-14.3, -13.84) * mm, "end": v(-14.34, -13.85) * mm});
            skLineSegment(sketch, "E2365", {"start": v(-14.34, -13.85) * mm, "end": v(-14.4, -13.86) * mm});
            skLineSegment(sketch, "E2366", {"start": v(-14.4, -13.86) * mm, "end": v(-14.45, -13.87) * mm});
            skLineSegment(sketch, "E2367", {"start": v(-14.45, -13.87) * mm, "end": v(-14.5, -13.88) * mm});
            skLineSegment(sketch, "E2368", {"start": v(-14.5, -13.88) * mm, "end": v(-14.56, -13.9) * mm});
            skLineSegment(sketch, "E2369", {"start": v(-14.56, -13.9) * mm, "end": v(-14.62, -13.9) * mm});
            skLineSegment(sketch, "E2370", {"start": v(-14.62, -13.9) * mm, "end": v(-14.67, -13.9) * mm});
            skLineSegment(sketch, "E2371", {"start": v(-14.67, -13.9) * mm, "end": v(-14.73, -13.91) * mm});
            skLineSegment(sketch, "E2372", {"start": v(-14.73, -13.91) * mm, "end": v(-14.8, -13.92) * mm});
            skLineSegment(sketch, "E2373", {"start": v(-14.8, -13.92) * mm, "end": v(-14.86, -13.93) * mm});
            skLineSegment(sketch, "E2374", {"start": v(-14.86, -13.93) * mm, "end": v(-14.86, -12.97) * mm});
            skLineSegment(sketch, "E2375", {"start": v(-14.86, -12.97) * mm, "end": v(-14.83, -12.96) * mm});
            skLineSegment(sketch, "E2376", {"start": v(-14.83, -12.96) * mm, "end": v(-14.8, -12.95) * mm});
            skLineSegment(sketch, "E2377", {"start": v(-14.8, -12.95) * mm, "end": v(-14.79, -12.93) * mm});
            skLineSegment(sketch, "E2378", {"start": v(-14.79, -12.93) * mm, "end": v(-14.77, -12.91) * mm});
            skLineSegment(sketch, "E2379", {"start": v(-14.77, -12.91) * mm, "end": v(-14.75, -12.9) * mm});
            skLineSegment(sketch, "E2380", {"start": v(-14.75, -12.9) * mm, "end": v(-14.73, -12.88) * mm});
            skLineSegment(sketch, "E2381", {"start": v(-14.73, -12.88) * mm, "end": v(-14.72, -12.86) * mm});
            skLineSegment(sketch, "E2382", {"start": v(-14.72, -12.86) * mm, "end": v(-14.7, -12.84) * mm});
            skLineSegment(sketch, "E2383", {"start": v(-14.7, -12.84) * mm, "end": v(-14.69, -12.82) * mm});
            skLineSegment(sketch, "E2384", {"start": v(-14.69, -12.82) * mm, "end": v(-14.68, -12.8) * mm});
            skLineSegment(sketch, "E2385", {"start": v(-14.68, -12.8) * mm, "end": v(-14.67, -12.76) * mm});
            skLineSegment(sketch, "E2386", {"start": v(-14.67, -12.76) * mm, "end": v(-14.65, -12.73) * mm});
            skLineSegment(sketch, "E2387", {"start": v(-14.65, -12.73) * mm, "end": v(-14.64, -12.7) * mm});
            skLineSegment(sketch, "E2388", {"start": v(-14.64, -12.7) * mm, "end": v(-14.63, -12.66) * mm});
            skLineSegment(sketch, "E2389", {"start": v(-14.63, -12.66) * mm, "end": v(-14.62, -12.62) * mm});
            skLineSegment(sketch, "E2390", {"start": v(-14.62, -12.62) * mm, "end": v(-14.61, -12.58) * mm});
            skLineSegment(sketch, "E2391", {"start": v(-14.61, -12.58) * mm, "end": v(-14.6, -12.51) * mm});
            skLineSegment(sketch, "E2392", {"start": v(-14.6, -12.51) * mm, "end": v(-14.59, -12.44) * mm});
            skLineSegment(sketch, "E2393", {"start": v(-14.59, -12.44) * mm, "end": v(-14.58, -12.37) * mm});
            skLineSegment(sketch, "E2394", {"start": v(-14.58, -12.37) * mm, "end": v(-14.57, -12.3) * mm});
            skLineSegment(sketch, "E2395", {"start": v(-14.57, -12.3) * mm, "end": v(-14.56, -12.2) * mm});
            skLineSegment(sketch, "E2396", {"start": v(-14.56, -12.2) * mm, "end": v(-14.56, -12.13) * mm});
            skLineSegment(sketch, "E2397", {"start": v(-14.56, -12.13) * mm, "end": v(-14.55, -12.04) * mm});
            skLineSegment(sketch, "E2398", {"start": v(-14.55, -12.04) * mm, "end": v(-14.55, -11.95) * mm});
            skLineSegment(sketch, "E2399", {"start": v(-14.55, -11.95) * mm, "end": v(-14.55, -8.82) * mm});
            skLineSegment(sketch, "E2400", {"start": v(-14.55, -8.82) * mm, "end": v(-14.56, -8.77) * mm});
            skLineSegment(sketch, "E2401", {"start": v(-14.56, -8.77) * mm, "end": v(-14.56, -8.7) * mm});
            skLineSegment(sketch, "E2402", {"start": v(-14.56, -8.7) * mm, "end": v(-14.57, -8.63) * mm});
            skLineSegment(sketch, "E2403", {"start": v(-14.57, -8.63) * mm, "end": v(-14.58, -8.53) * mm});
            skLineSegment(sketch, "E2404", {"start": v(-14.58, -8.53) * mm, "end": v(-14.6, -8.43) * mm});
            skLineSegment(sketch, "E2405", {"start": v(-14.6, -8.43) * mm, "end": v(-14.61, -8.35) * mm});
            skLineSegment(sketch, "E2406", {"start": v(-14.61, -8.35) * mm, "end": v(-14.63, -8.27) * mm});
            skLineSegment(sketch, "E2407", {"start": v(-14.63, -8.27) * mm, "end": v(-14.64, -8.2) * mm});
            skLineSegment(sketch, "E2408", {"start": v(-14.64, -8.2) * mm, "end": v(-14.65, -8.16) * mm});
            skLineSegment(sketch, "E2409", {"start": v(-14.65, -8.16) * mm, "end": v(-14.66, -8.13) * mm});
            skLineSegment(sketch, "E2410", {"start": v(-14.66, -8.13) * mm, "end": v(-14.67, -8.1) * mm});
            skLineSegment(sketch, "E2411", {"start": v(-14.67, -8.1) * mm, "end": v(-14.68, -8.07) * mm});
            skLineSegment(sketch, "E2412", {"start": v(-14.68, -8.07) * mm, "end": v(-14.7, -8.05) * mm});
            skLineSegment(sketch, "E2413", {"start": v(-14.7, -8.05) * mm, "end": v(-14.7, -8.02) * mm});
            skLineSegment(sketch, "E2414", {"start": v(-14.7, -8.02) * mm, "end": v(-14.72, -8) * mm});
            skLineSegment(sketch, "E2415", {"start": v(-14.72, -8) * mm, "end": v(-14.73, -7.98) * mm});
            skLineSegment(sketch, "E2416", {"start": v(-14.73, -7.98) * mm, "end": v(-14.74, -7.96) * mm});
            skLineSegment(sketch, "E2417", {"start": v(-14.74, -7.96) * mm, "end": v(-14.76, -7.94) * mm});
            skLineSegment(sketch, "E2418", {"start": v(-14.76, -7.94) * mm, "end": v(-14.78, -7.92) * mm});
            skLineSegment(sketch, "E2419", {"start": v(-14.78, -7.92) * mm, "end": v(-14.8, -7.9) * mm});
            skLineSegment(sketch, "E2420", {"start": v(-14.8, -7.9) * mm, "end": v(-14.82, -7.87) * mm});
            skLineSegment(sketch, "E2421", {"start": v(-14.82, -7.87) * mm, "end": v(-14.84, -7.85) * mm});
            skLineSegment(sketch, "E2422", {"start": v(-14.84, -7.85) * mm, "end": v(-14.86, -7.83) * mm});
            skLineSegment(sketch, "E2423", {"start": v(-14.86, -7.83) * mm, "end": v(-14.89, -7.81) * mm});
            skLineSegment(sketch, "E2424", {"start": v(-14.89, -7.81) * mm, "end": v(-14.89, -6.85) * mm});
            skLineSegment(sketch, "E2425", {"start": v(-14.89, -6.85) * mm, "end": v(-14.86, -6.83) * mm});
            skLineSegment(sketch, "E2426", {"start": v(-14.86, -6.83) * mm, "end": v(-14.84, -6.8) * mm});
            skLineSegment(sketch, "E2427", {"start": v(-14.84, -6.8) * mm, "end": v(-14.81, -6.78) * mm});
            skLineSegment(sketch, "E2428", {"start": v(-14.81, -6.78) * mm, "end": v(-14.8, -6.76) * mm});
            skLineSegment(sketch, "E2429", {"start": v(-14.8, -6.76) * mm, "end": v(-14.77, -6.74) * mm});
            skLineSegment(sketch, "E2430", {"start": v(-14.77, -6.74) * mm, "end": v(-14.75, -6.71) * mm});
            skLineSegment(sketch, "E2431", {"start": v(-14.75, -6.71) * mm, "end": v(-14.74, -6.69) * mm});
            skLineSegment(sketch, "E2432", {"start": v(-14.74, -6.69) * mm, "end": v(-14.72, -6.66) * mm});
            skLineSegment(sketch, "E2433", {"start": v(-14.72, -6.66) * mm, "end": v(-14.71, -6.64) * mm});
            skLineSegment(sketch, "E2434", {"start": v(-14.71, -6.64) * mm, "end": v(-14.7, -6.61) * mm});
            skLineSegment(sketch, "E2435", {"start": v(-14.7, -6.61) * mm, "end": v(-14.69, -6.58) * mm});
            skLineSegment(sketch, "E2436", {"start": v(-14.69, -6.58) * mm, "end": v(-14.68, -6.55) * mm});
            skLineSegment(sketch, "E2437", {"start": v(-14.68, -6.55) * mm, "end": v(-14.66, -6.51) * mm});
            skLineSegment(sketch, "E2438", {"start": v(-14.66, -6.51) * mm, "end": v(-14.65, -6.47) * mm});
            skLineSegment(sketch, "E2439", {"start": v(-14.65, -6.47) * mm, "end": v(-14.65, -6.43) * mm});
            skLineSegment(sketch, "E2440", {"start": v(-14.65, -6.43) * mm, "end": v(-14.64, -6.39) * mm});
            skLineSegment(sketch, "E2441", {"start": v(-14.64, -6.39) * mm, "end": v(-14.63, -6.33) * mm});
            skLineSegment(sketch, "E2442", {"start": v(-14.63, -6.33) * mm, "end": v(-14.62, -6.26) * mm});
            skLineSegment(sketch, "E2443", {"start": v(-14.62, -6.26) * mm, "end": v(-14.59, -6.07) * mm});
            skLineSegment(sketch, "E2444", {"start": v(-14.59, -6.07) * mm, "end": v(-14.56, -5.89) * mm});
            skLineSegment(sketch, "E2445", {"start": v(-14.56, -5.89) * mm, "end": v(-14.56, -5.84) * mm});
            skLineSegment(sketch, "E2446", {"start": v(-14.56, -5.84) * mm, "end": v(-14.55, -5.8) * mm});
            skLineSegment(sketch, "E2447", {"start": v(-14.55, -5.8) * mm, "end": v(-14.55, -3.28) * mm});
            skLineSegment(sketch, "E2448", {"start": v(-14.55, -3.28) * mm, "end": v(-14.56, -3.22) * mm});
            skLineSegment(sketch, "E2449", {"start": v(-14.56, -3.22) * mm, "end": v(-14.56, -3.15) * mm});
            skLineSegment(sketch, "E2450", {"start": v(-14.56, -3.15) * mm, "end": v(-14.57, -3.06) * mm});
            skLineSegment(sketch, "E2451", {"start": v(-14.57, -3.06) * mm, "end": v(-14.58, -2.95) * mm});
            skLineSegment(sketch, "E2452", {"start": v(-14.58, -2.95) * mm, "end": v(-14.63, -2.45) * mm});
            skLineSegment(sketch, "E2453", {"start": v(-14.63, -2.45) * mm, "end": v(-14.64, -2.42) * mm});
            skLineSegment(sketch, "E2454", {"start": v(-14.64, -2.42) * mm, "end": v(-14.65, -2.4) * mm});
            skLineSegment(sketch, "E2455", {"start": v(-14.65, -2.4) * mm, "end": v(-14.66, -2.37) * mm});
            skLineSegment(sketch, "E2456", {"start": v(-14.66, -2.37) * mm, "end": v(-14.67, -2.34) * mm});
            skLineSegment(sketch, "E2457", {"start": v(-14.67, -2.34) * mm, "end": v(-14.68, -2.3) * mm});
            skLineSegment(sketch, "E2458", {"start": v(-14.68, -2.3) * mm, "end": v(-14.7, -2.28) * mm});
            skLineSegment(sketch, "E2459", {"start": v(-14.7, -2.28) * mm, "end": v(-14.7, -2.25) * mm});
            skLineSegment(sketch, "E2460", {"start": v(-14.7, -2.25) * mm, "end": v(-14.72, -2.23) * mm});
            skLineSegment(sketch, "E2461", {"start": v(-14.72, -2.23) * mm, "end": v(-14.74, -2.2) * mm});
            skLineSegment(sketch, "E2462", {"start": v(-14.74, -2.2) * mm, "end": v(-14.75, -2.17) * mm});
            skLineSegment(sketch, "E2463", {"start": v(-14.75, -2.17) * mm, "end": v(-14.77, -2.14) * mm});
            skLineSegment(sketch, "E2464", {"start": v(-14.77, -2.14) * mm, "end": v(-14.8, -2.12) * mm});
            skLineSegment(sketch, "E2465", {"start": v(-14.8, -2.12) * mm, "end": v(-14.82, -2.1) * mm});
            skLineSegment(sketch, "E2466", {"start": v(-14.82, -2.1) * mm, "end": v(-14.84, -2.06) * mm});
            skLineSegment(sketch, "E2467", {"start": v(-14.84, -2.06) * mm, "end": v(-14.86, -2.04) * mm});
            skLineSegment(sketch, "E2468", {"start": v(-14.86, -2.04) * mm, "end": v(-14.89, -2.01) * mm});
            skLineSegment(sketch, "E2469", {"start": v(-15.16, -29.57) * mm, "end": v(-15.22, -29.55) * mm});
            skLineSegment(sketch, "E2470", {"start": v(-15.22, -29.55) * mm, "end": v(-15.28, -29.53) * mm});
            skLineSegment(sketch, "E2471", {"start": v(-15.28, -29.53) * mm, "end": v(-15.34, -29.51) * mm});
            skLineSegment(sketch, "E2472", {"start": v(-15.34, -29.51) * mm, "end": v(-15.4, -29.49) * mm});
            skLineSegment(sketch, "E2473", {"start": v(-15.4, -29.49) * mm, "end": v(-15.46, -29.46) * mm});
            skLineSegment(sketch, "E2474", {"start": v(-15.46, -29.46) * mm, "end": v(-15.52, -29.43) * mm});
            skLineSegment(sketch, "E2475", {"start": v(-15.52, -29.43) * mm, "end": v(-15.57, -29.4) * mm});
            skLineSegment(sketch, "E2476", {"start": v(-15.57, -29.4) * mm, "end": v(-15.63, -29.37) * mm});
            skLineSegment(sketch, "E2477", {"start": v(-15.63, -29.37) * mm, "end": v(-15.68, -29.34) * mm});
            skLineSegment(sketch, "E2478", {"start": v(-15.68, -29.34) * mm, "end": v(-15.73, -29.3) * mm});
            skLineSegment(sketch, "E2479", {"start": v(-15.73, -29.3) * mm, "end": v(-15.78, -29.26) * mm});
            skLineSegment(sketch, "E2480", {"start": v(-15.78, -29.26) * mm, "end": v(-15.84, -29.22) * mm});
            skLineSegment(sketch, "E2481", {"start": v(-15.84, -29.22) * mm, "end": v(-15.89, -29.17) * mm});
            skLineSegment(sketch, "E2482", {"start": v(-15.89, -29.17) * mm, "end": v(-15.94, -29.12) * mm});
            skLineSegment(sketch, "E2483", {"start": v(-15.94, -29.12) * mm, "end": v(-15.98, -29.07) * mm});
            skLineSegment(sketch, "E2484", {"start": v(-15.98, -29.07) * mm, "end": v(-16.03, -29.02) * mm});
            skLineSegment(sketch, "E2485", {"start": v(-16.03, -29.02) * mm, "end": v(-16.08, -28.97) * mm});
            skLineSegment(sketch, "E2486", {"start": v(-16.08, -28.97) * mm, "end": v(-16.13, -28.9) * mm});
            skLineSegment(sketch, "E2487", {"start": v(-16.13, -28.9) * mm, "end": v(-16.17, -28.85) * mm});
            skLineSegment(sketch, "E2488", {"start": v(-16.17, -28.85) * mm, "end": v(-16.22, -28.79) * mm});
            skLineSegment(sketch, "E2489", {"start": v(-16.22, -28.79) * mm, "end": v(-16.26, -28.72) * mm});
            skLineSegment(sketch, "E2490", {"start": v(-16.26, -28.72) * mm, "end": v(-16.3, -28.65) * mm});
            skLineSegment(sketch, "E2491", {"start": v(-16.3, -28.65) * mm, "end": v(-16.35, -28.58) * mm});
            skLineSegment(sketch, "E2492", {"start": v(-16.35, -28.58) * mm, "end": v(-16.4, -28.5) * mm});
            skLineSegment(sketch, "E2493", {"start": v(-16.4, -28.5) * mm, "end": v(-16.44, -28.42) * mm});
            skLineSegment(sketch, "E2494", {"start": v(-16.44, -28.42) * mm, "end": v(-16.49, -28.34) * mm});
            skLineSegment(sketch, "E2495", {"start": v(-16.49, -28.34) * mm, "end": v(-16.53, -28.26) * mm});
            skLineSegment(sketch, "E2496", {"start": v(-16.53, -28.26) * mm, "end": v(-16.57, -28.17) * mm});
            skLineSegment(sketch, "E2497", {"start": v(-16.57, -28.17) * mm, "end": v(-16.61, -28.08) * mm});
            skLineSegment(sketch, "E2498", {"start": v(-16.61, -28.08) * mm, "end": v(-16.66, -27.99) * mm});
            skLineSegment(sketch, "E2499", {"start": v(-16.66, -27.99) * mm, "end": v(-16.7, -27.89) * mm});
            skLineSegment(sketch, "E2500", {"start": v(-16.7, -27.89) * mm, "end": v(-16.74, -27.8) * mm});
            skLineSegment(sketch, "E2501", {"start": v(-16.74, -27.8) * mm, "end": v(-16.78, -27.68) * mm});
            skLineSegment(sketch, "E2502", {"start": v(-16.78, -27.68) * mm, "end": v(-16.83, -27.57) * mm});
            skLineSegment(sketch, "E2503", {"start": v(-16.83, -27.57) * mm, "end": v(-16.87, -27.45) * mm});
            skLineSegment(sketch, "E2504", {"start": v(-16.87, -27.45) * mm, "end": v(-16.9, -27.33) * mm});
            skLineSegment(sketch, "E2505", {"start": v(-16.9, -27.33) * mm, "end": v(-16.95, -27.21) * mm});
            skLineSegment(sketch, "E2506", {"start": v(-16.95, -27.21) * mm, "end": v(-16.98, -27.09) * mm});
            skLineSegment(sketch, "E2507", {"start": v(-16.98, -27.09) * mm, "end": v(-17.02, -26.96) * mm});
            skLineSegment(sketch, "E2508", {"start": v(-17.02, -26.96) * mm, "end": v(-17.05, -26.84) * mm});
            skLineSegment(sketch, "E2509", {"start": v(-17.05, -26.84) * mm, "end": v(-17.09, -26.7) * mm});
            skLineSegment(sketch, "E2510", {"start": v(-17.09, -26.7) * mm, "end": v(-17.12, -26.57) * mm});
            skLineSegment(sketch, "E2511", {"start": v(-17.12, -26.57) * mm, "end": v(-17.15, -26.44) * mm});
            skLineSegment(sketch, "E2512", {"start": v(-17.15, -26.44) * mm, "end": v(-17.18, -26.3) * mm});
            skLineSegment(sketch, "E2513", {"start": v(-17.18, -26.3) * mm, "end": v(-17.2, -26.16) * mm});
            skLineSegment(sketch, "E2514", {"start": v(-17.2, -26.16) * mm, "end": v(-17.23, -26.02) * mm});
            skLineSegment(sketch, "E2515", {"start": v(-17.23, -26.02) * mm, "end": v(-17.26, -25.88) * mm});
            skLineSegment(sketch, "E2516", {"start": v(-17.26, -25.88) * mm, "end": v(-17.28, -25.73) * mm});
            skLineSegment(sketch, "E2517", {"start": v(-17.28, -25.73) * mm, "end": v(-17.3, -25.58) * mm});
            skLineSegment(sketch, "E2518", {"start": v(-17.3, -25.58) * mm, "end": v(-17.33, -25.43) * mm});
            skLineSegment(sketch, "E2519", {"start": v(-17.33, -25.43) * mm, "end": v(-17.35, -25.28) * mm});
            skLineSegment(sketch, "E2520", {"start": v(-17.35, -25.28) * mm, "end": v(-17.36, -25.13) * mm});
            skLineSegment(sketch, "E2521", {"start": v(-17.36, -25.13) * mm, "end": v(-17.38, -24.97) * mm});
            skLineSegment(sketch, "E2522", {"start": v(-17.38, -24.97) * mm, "end": v(-17.4, -24.82) * mm});
            skLineSegment(sketch, "E2523", {"start": v(-17.4, -24.82) * mm, "end": v(-17.41, -24.66) * mm});
            skLineSegment(sketch, "E2524", {"start": v(-17.41, -24.66) * mm, "end": v(-17.42, -24.5) * mm});
            skLineSegment(sketch, "E2525", {"start": v(-17.42, -24.5) * mm, "end": v(-17.43, -24.34) * mm});
            skLineSegment(sketch, "E2526", {"start": v(-17.43, -24.34) * mm, "end": v(-17.44, -24.17) * mm});
            skLineSegment(sketch, "E2527", {"start": v(-17.44, -24.17) * mm, "end": v(-17.45, -24) * mm});
            skLineSegment(sketch, "E2528", {"start": v(-17.45, -24) * mm, "end": v(-17.46, -23.84) * mm});
            skLineSegment(sketch, "E2529", {"start": v(-17.46, -23.84) * mm, "end": v(-17.46, -23.67) * mm});
            skLineSegment(sketch, "E2530", {"start": v(-17.46, -23.67) * mm, "end": v(-17.47, -23.5) * mm});
            skLineSegment(sketch, "E2531", {"start": v(-17.47, -23.5) * mm, "end": v(-17.47, -23.33) * mm});
            skLineSegment(sketch, "E2532", {"start": v(-17.47, -23.33) * mm, "end": v(-17.47, -23.16) * mm});
            skLineSegment(sketch, "E2533", {"start": v(-17.47, -23.16) * mm, "end": v(-17.47, -22.99) * mm});
            skLineSegment(sketch, "E2534", {"start": v(-17.47, -22.99) * mm, "end": v(-17.47, -22.82) * mm});
            skLineSegment(sketch, "E2535", {"start": v(-17.47, -22.82) * mm, "end": v(-17.46, -22.65) * mm});
            skLineSegment(sketch, "E2536", {"start": v(-17.46, -22.65) * mm, "end": v(-17.46, -22.48) * mm});
            skLineSegment(sketch, "E2537", {"start": v(-17.46, -22.48) * mm, "end": v(-17.45, -22.32) * mm});
            skLineSegment(sketch, "E2538", {"start": v(-17.45, -22.32) * mm, "end": v(-17.44, -22.15) * mm});
            skLineSegment(sketch, "E2539", {"start": v(-17.44, -22.15) * mm, "end": v(-17.43, -21.99) * mm});
            skLineSegment(sketch, "E2540", {"start": v(-17.43, -21.99) * mm, "end": v(-17.42, -21.83) * mm});
            skLineSegment(sketch, "E2541", {"start": v(-17.42, -21.83) * mm, "end": v(-17.41, -21.67) * mm});
            skLineSegment(sketch, "E2542", {"start": v(-17.41, -21.67) * mm, "end": v(-17.4, -21.51) * mm});
            skLineSegment(sketch, "E2543", {"start": v(-17.4, -21.51) * mm, "end": v(-17.38, -21.36) * mm});
            skLineSegment(sketch, "E2544", {"start": v(-17.38, -21.36) * mm, "end": v(-17.36, -21.2) * mm});
            skLineSegment(sketch, "E2545", {"start": v(-17.36, -21.2) * mm, "end": v(-17.35, -21.05) * mm});
            skLineSegment(sketch, "E2546", {"start": v(-17.35, -21.05) * mm, "end": v(-17.33, -20.9) * mm});
            skLineSegment(sketch, "E2547", {"start": v(-17.33, -20.9) * mm, "end": v(-17.3, -20.75) * mm});
            skLineSegment(sketch, "E2548", {"start": v(-17.3, -20.75) * mm, "end": v(-17.28, -20.6) * mm});
            skLineSegment(sketch, "E2549", {"start": v(-17.28, -20.6) * mm, "end": v(-17.26, -20.45) * mm});
            skLineSegment(sketch, "E2550", {"start": v(-17.26, -20.45) * mm, "end": v(-17.23, -20.3) * mm});
            skLineSegment(sketch, "E2551", {"start": v(-17.23, -20.3) * mm, "end": v(-17.2, -20.17) * mm});
            skLineSegment(sketch, "E2552", {"start": v(-17.2, -20.17) * mm, "end": v(-17.18, -20.03) * mm});
            skLineSegment(sketch, "E2553", {"start": v(-17.18, -20.03) * mm, "end": v(-17.15, -19.89) * mm});
            skLineSegment(sketch, "E2554", {"start": v(-17.15, -19.89) * mm, "end": v(-17.12, -19.75) * mm});
            skLineSegment(sketch, "E2555", {"start": v(-17.12, -19.75) * mm, "end": v(-17.09, -19.62) * mm});
            skLineSegment(sketch, "E2556", {"start": v(-17.09, -19.62) * mm, "end": v(-17.05, -19.5) * mm});
            skLineSegment(sketch, "E2557", {"start": v(-17.05, -19.5) * mm, "end": v(-17.02, -19.37) * mm});
            skLineSegment(sketch, "E2558", {"start": v(-17.02, -19.37) * mm, "end": v(-16.98, -19.24) * mm});
            skLineSegment(sketch, "E2559", {"start": v(-16.98, -19.24) * mm, "end": v(-16.95, -19.12) * mm});
            skLineSegment(sketch, "E2560", {"start": v(-16.95, -19.12) * mm, "end": v(-16.9, -19) * mm});
            skLineSegment(sketch, "E2561", {"start": v(-16.9, -19) * mm, "end": v(-16.87, -18.88) * mm});
            skLineSegment(sketch, "E2562", {"start": v(-16.87, -18.88) * mm, "end": v(-16.83, -18.76) * mm});
            skLineSegment(sketch, "E2563", {"start": v(-16.83, -18.76) * mm, "end": v(-16.78, -18.65) * mm});
            skLineSegment(sketch, "E2564", {"start": v(-16.78, -18.65) * mm, "end": v(-16.74, -18.54) * mm});
            skLineSegment(sketch, "E2565", {"start": v(-16.74, -18.54) * mm, "end": v(-16.7, -18.44) * mm});
            skLineSegment(sketch, "E2566", {"start": v(-16.7, -18.44) * mm, "end": v(-16.66, -18.34) * mm});
            skLineSegment(sketch, "E2567", {"start": v(-16.66, -18.34) * mm, "end": v(-16.61, -18.25) * mm});
            skLineSegment(sketch, "E2568", {"start": v(-16.61, -18.25) * mm, "end": v(-16.57, -18.16) * mm});
            skLineSegment(sketch, "E2569", {"start": v(-16.57, -18.16) * mm, "end": v(-16.53, -18.07) * mm});
            skLineSegment(sketch, "E2570", {"start": v(-16.53, -18.07) * mm, "end": v(-16.49, -17.99) * mm});
            skLineSegment(sketch, "E2571", {"start": v(-16.49, -17.99) * mm, "end": v(-16.44, -17.9) * mm});
            skLineSegment(sketch, "E2572", {"start": v(-16.44, -17.9) * mm, "end": v(-16.4, -17.83) * mm});
            skLineSegment(sketch, "E2573", {"start": v(-16.4, -17.83) * mm, "end": v(-16.35, -17.75) * mm});
            skLineSegment(sketch, "E2574", {"start": v(-16.35, -17.75) * mm, "end": v(-16.3, -17.68) * mm});
            skLineSegment(sketch, "E2575", {"start": v(-16.3, -17.68) * mm, "end": v(-16.26, -17.61) * mm});
            skLineSegment(sketch, "E2576", {"start": v(-16.26, -17.61) * mm, "end": v(-16.22, -17.54) * mm});
            skLineSegment(sketch, "E2577", {"start": v(-16.22, -17.54) * mm, "end": v(-16.17, -17.48) * mm});
            skLineSegment(sketch, "E2578", {"start": v(-16.17, -17.48) * mm, "end": v(-16.13, -17.42) * mm});
            skLineSegment(sketch, "E2579", {"start": v(-16.13, -17.42) * mm, "end": v(-16.08, -17.36) * mm});
            skLineSegment(sketch, "E2580", {"start": v(-16.08, -17.36) * mm, "end": v(-16.03, -17.3) * mm});
            skLineSegment(sketch, "E2581", {"start": v(-16.03, -17.3) * mm, "end": v(-15.98, -17.26) * mm});
            skLineSegment(sketch, "E2582", {"start": v(-15.98, -17.26) * mm, "end": v(-15.94, -17.2) * mm});
            skLineSegment(sketch, "E2583", {"start": v(-15.94, -17.2) * mm, "end": v(-15.89, -17.16) * mm});
            skLineSegment(sketch, "E2584", {"start": v(-15.89, -17.16) * mm, "end": v(-15.84, -17.11) * mm});
            skLineSegment(sketch, "E2585", {"start": v(-15.84, -17.11) * mm, "end": v(-15.78, -17.07) * mm});
            skLineSegment(sketch, "E2586", {"start": v(-15.78, -17.07) * mm, "end": v(-15.73, -17.03) * mm});
            skLineSegment(sketch, "E2587", {"start": v(-15.73, -17.03) * mm, "end": v(-15.68, -17) * mm});
            skLineSegment(sketch, "E2588", {"start": v(-15.68, -17) * mm, "end": v(-15.63, -16.96) * mm});
            skLineSegment(sketch, "E2589", {"start": v(-15.63, -16.96) * mm, "end": v(-15.57, -16.93) * mm});
            skLineSegment(sketch, "E2590", {"start": v(-15.57, -16.93) * mm, "end": v(-15.52, -16.9) * mm});
            skLineSegment(sketch, "E2591", {"start": v(-15.52, -16.9) * mm, "end": v(-15.46, -16.87) * mm});
            skLineSegment(sketch, "E2592", {"start": v(-15.46, -16.87) * mm, "end": v(-15.4, -16.84) * mm});
            skLineSegment(sketch, "E2593", {"start": v(-15.4, -16.84) * mm, "end": v(-15.34, -16.82) * mm});
            skLineSegment(sketch, "E2594", {"start": v(-15.34, -16.82) * mm, "end": v(-15.28, -16.8) * mm});
            skLineSegment(sketch, "E2595", {"start": v(-15.28, -16.8) * mm, "end": v(-15.22, -16.78) * mm});
            skLineSegment(sketch, "E2596", {"start": v(-15.22, -16.78) * mm, "end": v(-15.16, -16.76) * mm});
            skLineSegment(sketch, "E2597", {"start": v(-15.16, -16.76) * mm, "end": v(-15.16, -17.72) * mm});
            skLineSegment(sketch, "E2598", {"start": v(-15.16, -17.72) * mm, "end": v(-15.22, -17.75) * mm});
            skLineSegment(sketch, "E2599", {"start": v(-15.22, -17.75) * mm, "end": v(-15.27, -17.8) * mm});
            skLineSegment(sketch, "E2600", {"start": v(-15.27, -17.8) * mm, "end": v(-15.3, -17.8) * mm});
            skLineSegment(sketch, "E2601", {"start": v(-15.3, -17.8) * mm, "end": v(-15.32, -17.83) * mm});
            skLineSegment(sketch, "E2602", {"start": v(-15.32, -17.83) * mm, "end": v(-15.33, -17.84) * mm});
            skLineSegment(sketch, "E2603", {"start": v(-15.33, -17.84) * mm, "end": v(-15.35, -17.86) * mm});
            skLineSegment(sketch, "E2604", {"start": v(-15.35, -17.86) * mm, "end": v(-15.36, -17.87) * mm});
            skLineSegment(sketch, "E2605", {"start": v(-15.36, -17.87) * mm, "end": v(-15.37, -17.9) * mm});
            skLineSegment(sketch, "E2606", {"start": v(-15.37, -17.9) * mm, "end": v(-15.38, -17.91) * mm});
            skLineSegment(sketch, "E2607", {"start": v(-15.38, -17.91) * mm, "end": v(-15.4, -17.93) * mm});
            skLineSegment(sketch, "E2608", {"start": v(-15.4, -17.93) * mm, "end": v(-15.4, -17.95) * mm});
            skLineSegment(sketch, "E2609", {"start": v(-15.4, -17.95) * mm, "end": v(-15.42, -17.98) * mm});
            skLineSegment(sketch, "E2610", {"start": v(-15.42, -17.98) * mm, "end": v(-15.44, -18.04) * mm});
            skLineSegment(sketch, "E2611", {"start": v(-15.44, -18.04) * mm, "end": v(-15.46, -18.08) * mm});
            skLineSegment(sketch, "E2612", {"start": v(-15.46, -18.08) * mm, "end": v(-15.48, -18.12) * mm});
            skLineSegment(sketch, "E2613", {"start": v(-15.48, -18.12) * mm, "end": v(-15.49, -18.17) * mm});
            skLineSegment(sketch, "E2614", {"start": v(-15.49, -18.17) * mm, "end": v(-15.5, -18.22) * mm});
            skLineSegment(sketch, "E2615", {"start": v(-15.5, -18.22) * mm, "end": v(-15.51, -18.28) * mm});
            skLineSegment(sketch, "E2616", {"start": v(-15.51, -18.28) * mm, "end": v(-15.53, -18.33) * mm});
            skLineSegment(sketch, "E2617", {"start": v(-15.53, -18.33) * mm, "end": v(-15.54, -18.39) * mm});
            skLineSegment(sketch, "E2618", {"start": v(-15.54, -18.39) * mm, "end": v(-15.54, -18.45) * mm});
            skLineSegment(sketch, "E2619", {"start": v(-15.54, -18.45) * mm, "end": v(-15.55, -18.51) * mm});
            skLineSegment(sketch, "E2620", {"start": v(-15.55, -18.51) * mm, "end": v(-15.56, -18.58) * mm});
            skLineSegment(sketch, "E2621", {"start": v(-15.56, -18.58) * mm, "end": v(-15.57, -18.64) * mm});
            skLineSegment(sketch, "E2622", {"start": v(-15.57, -18.64) * mm, "end": v(-15.57, -18.71) * mm});
            skLineSegment(sketch, "E2623", {"start": v(-15.57, -18.71) * mm, "end": v(-15.57, -18.79) * mm});
            skLineSegment(sketch, "E2624", {"start": v(-15.57, -18.79) * mm, "end": v(-15.58, -18.86) * mm});
            skLineSegment(sketch, "E2625", {"start": v(-15.58, -18.86) * mm, "end": v(-15.58, -18.94) * mm});
            skLineSegment(sketch, "E2626", {"start": v(-15.58, -18.94) * mm, "end": v(-15.58, -19.01) * mm});
            skLineSegment(sketch, "E2627", {"start": v(-15.58, -19.01) * mm, "end": v(-15.58, -27.31) * mm});
            skLineSegment(sketch, "E2628", {"start": v(-15.58, -27.31) * mm, "end": v(-15.58, -27.4) * mm});
            skLineSegment(sketch, "E2629", {"start": v(-15.58, -27.4) * mm, "end": v(-15.58, -27.47) * mm});
            skLineSegment(sketch, "E2630", {"start": v(-15.58, -27.47) * mm, "end": v(-15.57, -27.54) * mm});
            skLineSegment(sketch, "E2631", {"start": v(-15.57, -27.54) * mm, "end": v(-15.57, -27.62) * mm});
            skLineSegment(sketch, "E2632", {"start": v(-15.57, -27.62) * mm, "end": v(-15.57, -27.69) * mm});
            skLineSegment(sketch, "E2633", {"start": v(-15.57, -27.69) * mm, "end": v(-15.56, -27.75) * mm});
            skLineSegment(sketch, "E2634", {"start": v(-15.56, -27.75) * mm, "end": v(-15.55, -27.82) * mm});
            skLineSegment(sketch, "E2635", {"start": v(-15.55, -27.82) * mm, "end": v(-15.54, -27.88) * mm});
            skLineSegment(sketch, "E2636", {"start": v(-15.54, -27.88) * mm, "end": v(-15.54, -27.94) * mm});
            skLineSegment(sketch, "E2637", {"start": v(-15.54, -27.94) * mm, "end": v(-15.53, -28) * mm});
            skLineSegment(sketch, "E2638", {"start": v(-15.53, -28) * mm, "end": v(-15.51, -28.05) * mm});
            skLineSegment(sketch, "E2639", {"start": v(-15.51, -28.05) * mm, "end": v(-15.5, -28.1) * mm});
            skLineSegment(sketch, "E2640", {"start": v(-15.5, -28.1) * mm, "end": v(-15.49, -28.16) * mm});
            skLineSegment(sketch, "E2641", {"start": v(-15.49, -28.16) * mm, "end": v(-15.48, -28.2) * mm});
            skLineSegment(sketch, "E2642", {"start": v(-15.48, -28.2) * mm, "end": v(-15.46, -28.25) * mm});
            skLineSegment(sketch, "E2643", {"start": v(-15.46, -28.25) * mm, "end": v(-15.44, -28.3) * mm});
            skLineSegment(sketch, "E2644", {"start": v(-15.44, -28.3) * mm, "end": v(-15.42, -28.35) * mm});
            skLineSegment(sketch, "E2645", {"start": v(-15.42, -28.35) * mm, "end": v(-15.4, -28.37) * mm});
            skLineSegment(sketch, "E2646", {"start": v(-15.4, -28.37) * mm, "end": v(-15.4, -28.4) * mm});
            skLineSegment(sketch, "E2647", {"start": v(-15.4, -28.4) * mm, "end": v(-15.38, -28.42) * mm});
            skLineSegment(sketch, "E2648", {"start": v(-15.38, -28.42) * mm, "end": v(-15.37, -28.44) * mm});
            skLineSegment(sketch, "E2649", {"start": v(-15.37, -28.44) * mm, "end": v(-15.36, -28.46) * mm});
            skLineSegment(sketch, "E2650", {"start": v(-15.36, -28.46) * mm, "end": v(-15.35, -28.47) * mm});
            skLineSegment(sketch, "E2651", {"start": v(-15.35, -28.47) * mm, "end": v(-15.33, -28.49) * mm});
            skLineSegment(sketch, "E2652", {"start": v(-15.33, -28.49) * mm, "end": v(-15.32, -28.5) * mm});
            skLineSegment(sketch, "E2653", {"start": v(-15.32, -28.5) * mm, "end": v(-15.3, -28.52) * mm});
            skLineSegment(sketch, "E2654", {"start": v(-15.3, -28.52) * mm, "end": v(-15.27, -28.54) * mm});
            skLineSegment(sketch, "E2655", {"start": v(-15.27, -28.54) * mm, "end": v(-15.22, -28.57) * mm});
            skLineSegment(sketch, "E2656", {"start": v(-15.22, -28.57) * mm, "end": v(-15.16, -28.61) * mm});
            skLineSegment(sketch, "E2657", {"start": v(-15.16, -28.61) * mm, "end": v(-15.16, -29.57) * mm});
            skLineSegment(sketch, "E2658", {"start": v(-14.8, -29.57) * mm, "end": v(-14.8, -28.61) * mm});
            skLineSegment(sketch, "E2659", {"start": v(-14.8, -28.61) * mm, "end": v(-14.75, -28.57) * mm});
            skLineSegment(sketch, "E2660", {"start": v(-14.75, -28.57) * mm, "end": v(-14.7, -28.54) * mm});
            skLineSegment(sketch, "E2661", {"start": v(-14.7, -28.54) * mm, "end": v(-14.67, -28.52) * mm});
            skLineSegment(sketch, "E2662", {"start": v(-14.67, -28.52) * mm, "end": v(-14.65, -28.5) * mm});
            skLineSegment(sketch, "E2663", {"start": v(-14.65, -28.5) * mm, "end": v(-14.64, -28.49) * mm});
            skLineSegment(sketch, "E2664", {"start": v(-14.64, -28.49) * mm, "end": v(-14.62, -28.47) * mm});
            skLineSegment(sketch, "E2665", {"start": v(-14.62, -28.47) * mm, "end": v(-14.61, -28.46) * mm});
            skLineSegment(sketch, "E2666", {"start": v(-14.61, -28.46) * mm, "end": v(-14.6, -28.44) * mm});
            skLineSegment(sketch, "E2667", {"start": v(-14.6, -28.44) * mm, "end": v(-14.59, -28.42) * mm});
            skLineSegment(sketch, "E2668", {"start": v(-14.59, -28.42) * mm, "end": v(-14.57, -28.4) * mm});
            skLineSegment(sketch, "E2669", {"start": v(-14.57, -28.4) * mm, "end": v(-14.56, -28.37) * mm});
            skLineSegment(sketch, "E2670", {"start": v(-14.56, -28.37) * mm, "end": v(-14.55, -28.35) * mm});
            skLineSegment(sketch, "E2671", {"start": v(-14.55, -28.35) * mm, "end": v(-14.53, -28.3) * mm});
            skLineSegment(sketch, "E2672", {"start": v(-14.53, -28.3) * mm, "end": v(-14.5, -28.25) * mm});
            skLineSegment(sketch, "E2673", {"start": v(-14.5, -28.25) * mm, "end": v(-14.5, -28.2) * mm});
            skLineSegment(sketch, "E2674", {"start": v(-14.5, -28.2) * mm, "end": v(-14.48, -28.16) * mm});
            skLineSegment(sketch, "E2675", {"start": v(-14.48, -28.16) * mm, "end": v(-14.47, -28.1) * mm});
            skLineSegment(sketch, "E2676", {"start": v(-14.47, -28.1) * mm, "end": v(-14.45, -28.05) * mm});
            skLineSegment(sketch, "E2677", {"start": v(-14.45, -28.05) * mm, "end": v(-14.44, -28) * mm});
            skLineSegment(sketch, "E2678", {"start": v(-14.44, -28) * mm, "end": v(-14.43, -27.94) * mm});
            skLineSegment(sketch, "E2679", {"start": v(-14.43, -27.94) * mm, "end": v(-14.42, -27.88) * mm});
            skLineSegment(sketch, "E2680", {"start": v(-14.42, -27.88) * mm, "end": v(-14.42, -27.82) * mm});
            skLineSegment(sketch, "E2681", {"start": v(-14.42, -27.82) * mm, "end": v(-14.4, -27.75) * mm});
            skLineSegment(sketch, "E2682", {"start": v(-14.4, -27.75) * mm, "end": v(-14.4, -27.69) * mm});
            skLineSegment(sketch, "E2683", {"start": v(-14.4, -27.69) * mm, "end": v(-14.4, -27.62) * mm});
            skLineSegment(sketch, "E2684", {"start": v(-14.4, -27.62) * mm, "end": v(-14.4, -27.54) * mm});
            skLineSegment(sketch, "E2685", {"start": v(-14.4, -27.54) * mm, "end": v(-14.4, -27.47) * mm});
            skLineSegment(sketch, "E2686", {"start": v(-14.4, -27.47) * mm, "end": v(-14.4, -27.4) * mm});
            skLineSegment(sketch, "E2687", {"start": v(-14.4, -27.4) * mm, "end": v(-14.4, -27.31) * mm});
            skLineSegment(sketch, "E2688", {"start": v(-14.4, -27.31) * mm, "end": v(-14.4, -19.01) * mm});
            skLineSegment(sketch, "E2689", {"start": v(-14.4, -19.01) * mm, "end": v(-14.4, -18.94) * mm});
            skLineSegment(sketch, "E2690", {"start": v(-14.4, -18.94) * mm, "end": v(-14.4, -18.86) * mm});
            skLineSegment(sketch, "E2691", {"start": v(-14.4, -18.86) * mm, "end": v(-14.4, -18.79) * mm});
            skLineSegment(sketch, "E2692", {"start": v(-14.4, -18.79) * mm, "end": v(-14.4, -18.71) * mm});
            skLineSegment(sketch, "E2693", {"start": v(-14.4, -18.71) * mm, "end": v(-14.4, -18.64) * mm});
            skLineSegment(sketch, "E2694", {"start": v(-14.4, -18.64) * mm, "end": v(-14.4, -18.58) * mm});
            skLineSegment(sketch, "E2695", {"start": v(-14.4, -18.58) * mm, "end": v(-14.42, -18.51) * mm});
            skLineSegment(sketch, "E2696", {"start": v(-14.42, -18.51) * mm, "end": v(-14.42, -18.45) * mm});
            skLineSegment(sketch, "E2697", {"start": v(-14.42, -18.45) * mm, "end": v(-14.43, -18.39) * mm});
            skLineSegment(sketch, "E2698", {"start": v(-14.43, -18.39) * mm, "end": v(-14.44, -18.33) * mm});
            skLineSegment(sketch, "E2699", {"start": v(-14.44, -18.33) * mm, "end": v(-14.45, -18.28) * mm});
            skLineSegment(sketch, "E2700", {"start": v(-14.45, -18.28) * mm, "end": v(-14.47, -18.22) * mm});
            skLineSegment(sketch, "E2701", {"start": v(-14.47, -18.22) * mm, "end": v(-14.48, -18.17) * mm});
            skLineSegment(sketch, "E2702", {"start": v(-14.48, -18.17) * mm, "end": v(-14.5, -18.12) * mm});
            skLineSegment(sketch, "E2703", {"start": v(-14.5, -18.12) * mm, "end": v(-14.5, -18.08) * mm});
            skLineSegment(sketch, "E2704", {"start": v(-14.5, -18.08) * mm, "end": v(-14.53, -18.04) * mm});
            skLineSegment(sketch, "E2705", {"start": v(-14.53, -18.04) * mm, "end": v(-14.55, -17.98) * mm});
            skLineSegment(sketch, "E2706", {"start": v(-14.55, -17.98) * mm, "end": v(-14.56, -17.95) * mm});
            skLineSegment(sketch, "E2707", {"start": v(-14.56, -17.95) * mm, "end": v(-14.57, -17.93) * mm});
            skLineSegment(sketch, "E2708", {"start": v(-14.57, -17.93) * mm, "end": v(-14.59, -17.91) * mm});
            skLineSegment(sketch, "E2709", {"start": v(-14.59, -17.91) * mm, "end": v(-14.6, -17.9) * mm});
            skLineSegment(sketch, "E2710", {"start": v(-14.6, -17.9) * mm, "end": v(-14.61, -17.87) * mm});
            skLineSegment(sketch, "E2711", {"start": v(-14.61, -17.87) * mm, "end": v(-14.62, -17.86) * mm});
            skLineSegment(sketch, "E2712", {"start": v(-14.62, -17.86) * mm, "end": v(-14.64, -17.84) * mm});
            skLineSegment(sketch, "E2713", {"start": v(-14.64, -17.84) * mm, "end": v(-14.65, -17.83) * mm});
            skLineSegment(sketch, "E2714", {"start": v(-14.65, -17.83) * mm, "end": v(-14.67, -17.8) * mm});
            skLineSegment(sketch, "E2715", {"start": v(-14.67, -17.8) * mm, "end": v(-14.7, -17.8) * mm});
            skLineSegment(sketch, "E2716", {"start": v(-14.7, -17.8) * mm, "end": v(-14.75, -17.75) * mm});
            skLineSegment(sketch, "E2717", {"start": v(-14.75, -17.75) * mm, "end": v(-14.8, -17.72) * mm});
            skLineSegment(sketch, "E2718", {"start": v(-14.8, -17.72) * mm, "end": v(-14.8, -16.76) * mm});
            skLineSegment(sketch, "E2719", {"start": v(-14.8, -16.76) * mm, "end": v(-14.74, -16.78) * mm});
            skLineSegment(sketch, "E2720", {"start": v(-14.74, -16.78) * mm, "end": v(-14.68, -16.8) * mm});
            skLineSegment(sketch, "E2721", {"start": v(-14.68, -16.8) * mm, "end": v(-14.63, -16.82) * mm});
            skLineSegment(sketch, "E2722", {"start": v(-14.63, -16.82) * mm, "end": v(-14.57, -16.84) * mm});
            skLineSegment(sketch, "E2723", {"start": v(-14.57, -16.84) * mm, "end": v(-14.51, -16.87) * mm});
            skLineSegment(sketch, "E2724", {"start": v(-14.51, -16.87) * mm, "end": v(-14.45, -16.9) * mm});
            skLineSegment(sketch, "E2725", {"start": v(-14.45, -16.9) * mm, "end": v(-14.4, -16.93) * mm});
            skLineSegment(sketch, "E2726", {"start": v(-14.4, -16.93) * mm, "end": v(-14.34, -16.96) * mm});
            skLineSegment(sketch, "E2727", {"start": v(-14.34, -16.96) * mm, "end": v(-14.29, -17) * mm});
            skLineSegment(sketch, "E2728", {"start": v(-14.29, -17) * mm, "end": v(-14.24, -17.03) * mm});
            skLineSegment(sketch, "E2729", {"start": v(-14.24, -17.03) * mm, "end": v(-14.18, -17.07) * mm});
            skLineSegment(sketch, "E2730", {"start": v(-14.18, -17.07) * mm, "end": v(-14.13, -17.11) * mm});
            skLineSegment(sketch, "E2731", {"start": v(-14.13, -17.11) * mm, "end": v(-14.08, -17.16) * mm});
            skLineSegment(sketch, "E2732", {"start": v(-14.08, -17.16) * mm, "end": v(-14.03, -17.2) * mm});
            skLineSegment(sketch, "E2733", {"start": v(-14.03, -17.2) * mm, "end": v(-13.98, -17.26) * mm});
            skLineSegment(sketch, "E2734", {"start": v(-13.98, -17.26) * mm, "end": v(-13.94, -17.3) * mm});
            skLineSegment(sketch, "E2735", {"start": v(-13.94, -17.3) * mm, "end": v(-13.89, -17.36) * mm});
            skLineSegment(sketch, "E2736", {"start": v(-13.89, -17.36) * mm, "end": v(-13.84, -17.42) * mm});
            skLineSegment(sketch, "E2737", {"start": v(-13.84, -17.42) * mm, "end": v(-13.8, -17.48) * mm});
            skLineSegment(sketch, "E2738", {"start": v(-13.8, -17.48) * mm, "end": v(-13.75, -17.54) * mm});
            skLineSegment(sketch, "E2739", {"start": v(-13.75, -17.54) * mm, "end": v(-13.7, -17.61) * mm});
            skLineSegment(sketch, "E2740", {"start": v(-13.7, -17.61) * mm, "end": v(-13.66, -17.68) * mm});
            skLineSegment(sketch, "E2741", {"start": v(-13.66, -17.68) * mm, "end": v(-13.61, -17.75) * mm});
            skLineSegment(sketch, "E2742", {"start": v(-13.61, -17.75) * mm, "end": v(-13.57, -17.83) * mm});
            skLineSegment(sketch, "E2743", {"start": v(-13.57, -17.83) * mm, "end": v(-13.53, -17.9) * mm});
            skLineSegment(sketch, "E2744", {"start": v(-13.53, -17.9) * mm, "end": v(-13.48, -17.99) * mm});
            skLineSegment(sketch, "E2745", {"start": v(-13.48, -17.99) * mm, "end": v(-13.44, -18.07) * mm});
            skLineSegment(sketch, "E2746", {"start": v(-13.44, -18.07) * mm, "end": v(-13.4, -18.16) * mm});
            skLineSegment(sketch, "E2747", {"start": v(-13.4, -18.16) * mm, "end": v(-13.36, -18.25) * mm});
            skLineSegment(sketch, "E2748", {"start": v(-13.36, -18.25) * mm, "end": v(-13.31, -18.34) * mm});
            skLineSegment(sketch, "E2749", {"start": v(-13.31, -18.34) * mm, "end": v(-13.27, -18.44) * mm});
            skLineSegment(sketch, "E2750", {"start": v(-13.27, -18.44) * mm, "end": v(-13.23, -18.54) * mm});
            skLineSegment(sketch, "E2751", {"start": v(-13.23, -18.54) * mm, "end": v(-13.19, -18.65) * mm});
            skLineSegment(sketch, "E2752", {"start": v(-13.19, -18.65) * mm, "end": v(-13.14, -18.76) * mm});
            skLineSegment(sketch, "E2753", {"start": v(-13.14, -18.76) * mm, "end": v(-13.1, -18.88) * mm});
            skLineSegment(sketch, "E2754", {"start": v(-13.1, -18.88) * mm, "end": v(-13.06, -19) * mm});
            skLineSegment(sketch, "E2755", {"start": v(-13.06, -19) * mm, "end": v(-13.02, -19.12) * mm});
            skLineSegment(sketch, "E2756", {"start": v(-13.02, -19.12) * mm, "end": v(-12.99, -19.24) * mm});
            skLineSegment(sketch, "E2757", {"start": v(-12.99, -19.24) * mm, "end": v(-12.95, -19.37) * mm});
            skLineSegment(sketch, "E2758", {"start": v(-12.95, -19.37) * mm, "end": v(-12.92, -19.5) * mm});
            skLineSegment(sketch, "E2759", {"start": v(-12.92, -19.5) * mm, "end": v(-12.88, -19.62) * mm});
            skLineSegment(sketch, "E2760", {"start": v(-12.88, -19.62) * mm, "end": v(-12.85, -19.75) * mm});
            skLineSegment(sketch, "E2761", {"start": v(-12.85, -19.75) * mm, "end": v(-12.82, -19.89) * mm});
            skLineSegment(sketch, "E2762", {"start": v(-12.82, -19.89) * mm, "end": v(-12.8, -20.03) * mm});
            skLineSegment(sketch, "E2763", {"start": v(-12.8, -20.03) * mm, "end": v(-12.76, -20.17) * mm});
            skLineSegment(sketch, "E2764", {"start": v(-12.76, -20.17) * mm, "end": v(-12.74, -20.3) * mm});
            skLineSegment(sketch, "E2765", {"start": v(-12.74, -20.3) * mm, "end": v(-12.71, -20.45) * mm});
            skLineSegment(sketch, "E2766", {"start": v(-12.71, -20.45) * mm, "end": v(-12.69, -20.6) * mm});
            skLineSegment(sketch, "E2767", {"start": v(-12.69, -20.6) * mm, "end": v(-12.66, -20.75) * mm});
            skLineSegment(sketch, "E2768", {"start": v(-12.66, -20.75) * mm, "end": v(-12.64, -20.9) * mm});
            skLineSegment(sketch, "E2769", {"start": v(-12.64, -20.9) * mm, "end": v(-12.62, -21.05) * mm});
            skLineSegment(sketch, "E2770", {"start": v(-12.62, -21.05) * mm, "end": v(-12.6, -21.2) * mm});
            skLineSegment(sketch, "E2771", {"start": v(-12.6, -21.2) * mm, "end": v(-12.59, -21.36) * mm});
            skLineSegment(sketch, "E2772", {"start": v(-12.59, -21.36) * mm, "end": v(-12.57, -21.51) * mm});
            skLineSegment(sketch, "E2773", {"start": v(-12.57, -21.51) * mm, "end": v(-12.56, -21.67) * mm});
            skLineSegment(sketch, "E2774", {"start": v(-12.56, -21.67) * mm, "end": v(-12.55, -21.83) * mm});
            skLineSegment(sketch, "E2775", {"start": v(-12.55, -21.83) * mm, "end": v(-12.54, -21.99) * mm});
            skLineSegment(sketch, "E2776", {"start": v(-12.54, -21.99) * mm, "end": v(-12.53, -22.15) * mm});
            skLineSegment(sketch, "E2777", {"start": v(-12.53, -22.15) * mm, "end": v(-12.52, -22.32) * mm});
            skLineSegment(sketch, "E2778", {"start": v(-12.52, -22.32) * mm, "end": v(-12.51, -22.48) * mm});
            skLineSegment(sketch, "E2779", {"start": v(-12.51, -22.48) * mm, "end": v(-12.5, -22.65) * mm});
            skLineSegment(sketch, "E2780", {"start": v(-12.5, -22.65) * mm, "end": v(-12.5, -22.82) * mm});
            skLineSegment(sketch, "E2781", {"start": v(-12.5, -22.82) * mm, "end": v(-12.5, -22.99) * mm});
            skLineSegment(sketch, "E2782", {"start": v(-12.5, -22.99) * mm, "end": v(-12.5, -23.16) * mm});
            skLineSegment(sketch, "E2783", {"start": v(-12.5, -23.16) * mm, "end": v(-12.5, -23.33) * mm});
            skLineSegment(sketch, "E2784", {"start": v(-12.5, -23.33) * mm, "end": v(-12.5, -23.5) * mm});
            skLineSegment(sketch, "E2785", {"start": v(-12.5, -23.5) * mm, "end": v(-12.5, -23.67) * mm});
            skLineSegment(sketch, "E2786", {"start": v(-12.5, -23.67) * mm, "end": v(-12.51, -23.84) * mm});
            skLineSegment(sketch, "E2787", {"start": v(-12.51, -23.84) * mm, "end": v(-12.52, -24) * mm});
            skLineSegment(sketch, "E2788", {"start": v(-12.52, -24) * mm, "end": v(-12.53, -24.17) * mm});
            skLineSegment(sketch, "E2789", {"start": v(-12.53, -24.17) * mm, "end": v(-12.54, -24.34) * mm});
            skLineSegment(sketch, "E2790", {"start": v(-12.54, -24.34) * mm, "end": v(-12.55, -24.5) * mm});
            skLineSegment(sketch, "E2791", {"start": v(-12.55, -24.5) * mm, "end": v(-12.56, -24.66) * mm});
            skLineSegment(sketch, "E2792", {"start": v(-12.56, -24.66) * mm, "end": v(-12.57, -24.82) * mm});
            skLineSegment(sketch, "E2793", {"start": v(-12.57, -24.82) * mm, "end": v(-12.59, -24.97) * mm});
            skLineSegment(sketch, "E2794", {"start": v(-12.59, -24.97) * mm, "end": v(-12.6, -25.13) * mm});
            skLineSegment(sketch, "E2795", {"start": v(-12.6, -25.13) * mm, "end": v(-12.62, -25.28) * mm});
            skLineSegment(sketch, "E2796", {"start": v(-12.62, -25.28) * mm, "end": v(-12.64, -25.43) * mm});
            skLineSegment(sketch, "E2797", {"start": v(-12.64, -25.43) * mm, "end": v(-12.66, -25.58) * mm});
            skLineSegment(sketch, "E2798", {"start": v(-12.66, -25.58) * mm, "end": v(-12.69, -25.73) * mm});
            skLineSegment(sketch, "E2799", {"start": v(-12.69, -25.73) * mm, "end": v(-12.71, -25.88) * mm});
            skLineSegment(sketch, "E2800", {"start": v(-12.71, -25.88) * mm, "end": v(-12.74, -26.02) * mm});
            skLineSegment(sketch, "E2801", {"start": v(-12.74, -26.02) * mm, "end": v(-12.76, -26.16) * mm});
            skLineSegment(sketch, "E2802", {"start": v(-12.76, -26.16) * mm, "end": v(-12.8, -26.3) * mm});
            skLineSegment(sketch, "E2803", {"start": v(-12.8, -26.3) * mm, "end": v(-12.82, -26.44) * mm});
            skLineSegment(sketch, "E2804", {"start": v(-12.82, -26.44) * mm, "end": v(-12.85, -26.57) * mm});
            skLineSegment(sketch, "E2805", {"start": v(-12.85, -26.57) * mm, "end": v(-12.88, -26.7) * mm});
            skLineSegment(sketch, "E2806", {"start": v(-12.88, -26.7) * mm, "end": v(-12.92, -26.84) * mm});
            skLineSegment(sketch, "E2807", {"start": v(-12.92, -26.84) * mm, "end": v(-12.95, -26.96) * mm});
            skLineSegment(sketch, "E2808", {"start": v(-12.95, -26.96) * mm, "end": v(-12.99, -27.09) * mm});
            skLineSegment(sketch, "E2809", {"start": v(-12.99, -27.09) * mm, "end": v(-13.02, -27.21) * mm});
            skLineSegment(sketch, "E2810", {"start": v(-13.02, -27.21) * mm, "end": v(-13.06, -27.33) * mm});
            skLineSegment(sketch, "E2811", {"start": v(-13.06, -27.33) * mm, "end": v(-13.1, -27.45) * mm});
            skLineSegment(sketch, "E2812", {"start": v(-13.1, -27.45) * mm, "end": v(-13.14, -27.57) * mm});
            skLineSegment(sketch, "E2813", {"start": v(-13.14, -27.57) * mm, "end": v(-13.19, -27.68) * mm});
            skLineSegment(sketch, "E2814", {"start": v(-13.19, -27.68) * mm, "end": v(-13.23, -27.8) * mm});
            skLineSegment(sketch, "E2815", {"start": v(-13.23, -27.8) * mm, "end": v(-13.27, -27.89) * mm});
            skLineSegment(sketch, "E2816", {"start": v(-13.27, -27.89) * mm, "end": v(-13.31, -27.99) * mm});
            skLineSegment(sketch, "E2817", {"start": v(-13.31, -27.99) * mm, "end": v(-13.36, -28.08) * mm});
            skLineSegment(sketch, "E2818", {"start": v(-13.36, -28.08) * mm, "end": v(-13.4, -28.17) * mm});
            skLineSegment(sketch, "E2819", {"start": v(-13.4, -28.17) * mm, "end": v(-13.44, -28.26) * mm});
            skLineSegment(sketch, "E2820", {"start": v(-13.44, -28.26) * mm, "end": v(-13.48, -28.34) * mm});
            skLineSegment(sketch, "E2821", {"start": v(-13.48, -28.34) * mm, "end": v(-13.53, -28.42) * mm});
            skLineSegment(sketch, "E2822", {"start": v(-13.53, -28.42) * mm, "end": v(-13.57, -28.5) * mm});
            skLineSegment(sketch, "E2823", {"start": v(-13.57, -28.5) * mm, "end": v(-13.61, -28.58) * mm});
            skLineSegment(sketch, "E2824", {"start": v(-13.61, -28.58) * mm, "end": v(-13.66, -28.65) * mm});
            skLineSegment(sketch, "E2825", {"start": v(-13.66, -28.65) * mm, "end": v(-13.7, -28.72) * mm});
            skLineSegment(sketch, "E2826", {"start": v(-13.7, -28.72) * mm, "end": v(-13.75, -28.79) * mm});
            skLineSegment(sketch, "E2827", {"start": v(-13.75, -28.79) * mm, "end": v(-13.8, -28.85) * mm});
            skLineSegment(sketch, "E2828", {"start": v(-13.8, -28.85) * mm, "end": v(-13.84, -28.9) * mm});
            skLineSegment(sketch, "E2829", {"start": v(-13.84, -28.9) * mm, "end": v(-13.89, -28.97) * mm});
            skLineSegment(sketch, "E2830", {"start": v(-13.89, -28.97) * mm, "end": v(-13.94, -29.02) * mm});
            skLineSegment(sketch, "E2831", {"start": v(-13.94, -29.02) * mm, "end": v(-13.98, -29.07) * mm});
            skLineSegment(sketch, "E2832", {"start": v(-13.98, -29.07) * mm, "end": v(-14.03, -29.12) * mm});
            skLineSegment(sketch, "E2833", {"start": v(-14.03, -29.12) * mm, "end": v(-14.08, -29.17) * mm});
            skLineSegment(sketch, "E2834", {"start": v(-14.08, -29.17) * mm, "end": v(-14.13, -29.22) * mm});
            skLineSegment(sketch, "E2835", {"start": v(-14.13, -29.22) * mm, "end": v(-14.18, -29.26) * mm});
            skLineSegment(sketch, "E2836", {"start": v(-14.18, -29.26) * mm, "end": v(-14.24, -29.3) * mm});
            skLineSegment(sketch, "E2837", {"start": v(-14.24, -29.3) * mm, "end": v(-14.29, -29.34) * mm});
            skLineSegment(sketch, "E2838", {"start": v(-14.29, -29.34) * mm, "end": v(-14.34, -29.37) * mm});
            skLineSegment(sketch, "E2839", {"start": v(-14.34, -29.37) * mm, "end": v(-14.4, -29.4) * mm});
            skLineSegment(sketch, "E2840", {"start": v(-14.4, -29.4) * mm, "end": v(-14.45, -29.43) * mm});
            skLineSegment(sketch, "E2841", {"start": v(-14.45, -29.43) * mm, "end": v(-14.51, -29.46) * mm});
            skLineSegment(sketch, "E2842", {"start": v(-14.51, -29.46) * mm, "end": v(-14.57, -29.49) * mm});
            skLineSegment(sketch, "E2843", {"start": v(-14.57, -29.49) * mm, "end": v(-14.63, -29.51) * mm});
            skLineSegment(sketch, "E2844", {"start": v(-14.63, -29.51) * mm, "end": v(-14.68, -29.53) * mm});
            skLineSegment(sketch, "E2845", {"start": v(-14.68, -29.53) * mm, "end": v(-14.74, -29.55) * mm});
            skLineSegment(sketch, "E2846", {"start": v(-14.74, -29.55) * mm, "end": v(-14.8, -29.57) * mm});
            skArc(sketch, "E2847", {"start": v(16.38, -27.97) * mm, "mid": v(18.37, -25.31) * mm, "end": v(20.2, -22.54) * mm});
            skCircle(sketch, "E2848", {"center": v(0, 32.38) * mm, "radius": 1.59 * mm});
            skCircle(sketch, "E2849", {"center": v(0, -32.61) * mm, "radius": 1.59 * mm});
            skLineSegment(sketch, "E2850", {"start": v(228.6, 3.07) * mm, "end": v(228.6, 1.07) * mm});
            skLineSegment(sketch, "E2851", {"start": v(228.6, 1.07) * mm, "end": v(228.58, -0.92) * mm});
            skLineSegment(sketch, "E2852", {"start": v(228.58, -0.92) * mm, "end": v(228.56, -2.91) * mm});
            skLineSegment(sketch, "E2853", {"start": v(228.56, -2.91) * mm, "end": v(228.53, -4.9) * mm});
            skLineSegment(sketch, "E2854", {"start": v(228.53, -4.9) * mm, "end": v(228.5, -6.88) * mm});
            skLineSegment(sketch, "E2855", {"start": v(228.5, -6.88) * mm, "end": v(228.45, -8.85) * mm});
            skLineSegment(sketch, "E2856", {"start": v(228.45, -8.85) * mm, "end": v(228.4, -10.82) * mm});
            skLineSegment(sketch, "E2857", {"start": v(228.4, -10.82) * mm, "end": v(228.33, -12.79) * mm});
            skLineSegment(sketch, "E2858", {"start": v(228.33, -12.79) * mm, "end": v(228.26, -14.75) * mm});
            skLineSegment(sketch, "E2859", {"start": v(228.26, -14.75) * mm, "end": v(228.18, -16.7) * mm});
            skLineSegment(sketch, "E2860", {"start": v(228.18, -16.7) * mm, "end": v(228.09, -18.65) * mm});
            skLineSegment(sketch, "E2861", {"start": v(228.09, -18.65) * mm, "end": v(227.99, -20.6) * mm});
            skLineSegment(sketch, "E2862", {"start": v(227.99, -20.6) * mm, "end": v(227.88, -22.54) * mm});
            skLineSegment(sketch, "E2863", {"start": v(227.88, -22.54) * mm, "end": v(227.77, -24.48) * mm});
            skLineSegment(sketch, "E2864", {"start": v(227.77, -24.48) * mm, "end": v(227.65, -26.4) * mm});
            skLineSegment(sketch, "E2865", {"start": v(227.65, -26.4) * mm, "end": v(227.52, -28.33) * mm});
            skLineSegment(sketch, "E2866", {"start": v(227.52, -28.33) * mm, "end": v(227.38, -30.26) * mm});
            skLineSegment(sketch, "E2867", {"start": v(227.38, -30.26) * mm, "end": v(227.23, -32.17) * mm});
            skLineSegment(sketch, "E2868", {"start": v(227.23, -32.17) * mm, "end": v(227.07, -34.08) * mm});
            skLineSegment(sketch, "E2869", {"start": v(227.07, -34.08) * mm, "end": v(226.9, -36) * mm});
            skLineSegment(sketch, "E2870", {"start": v(226.9, -36) * mm, "end": v(226.73, -37.9) * mm});
            skLineSegment(sketch, "E2871", {"start": v(226.73, -37.9) * mm, "end": v(226.55, -39.8) * mm});
            skLineSegment(sketch, "E2872", {"start": v(226.55, -39.8) * mm, "end": v(226.36, -41.68) * mm});
            skLineSegment(sketch, "E2873", {"start": v(226.36, -41.68) * mm, "end": v(226.16, -43.57) * mm});
            skLineSegment(sketch, "E2874", {"start": v(226.16, -43.57) * mm, "end": v(225.95, -45.45) * mm});
            skLineSegment(sketch, "E2875", {"start": v(225.95, -45.45) * mm, "end": v(225.73, -47.33) * mm});
            skLineSegment(sketch, "E2876", {"start": v(225.73, -47.33) * mm, "end": v(225.51, -49.2) * mm});
            skLineSegment(sketch, "E2877", {"start": v(225.51, -49.2) * mm, "end": v(225.28, -51.07) * mm});
            skLineSegment(sketch, "E2878", {"start": v(225.28, -51.07) * mm, "end": v(225.04, -52.94) * mm});
            skLineSegment(sketch, "E2879", {"start": v(225.04, -52.94) * mm, "end": v(224.79, -54.8) * mm});
            skLineSegment(sketch, "E2880", {"start": v(224.79, -54.8) * mm, "end": v(224.53, -56.65) * mm});
            skLineSegment(sketch, "E2881", {"start": v(224.53, -56.65) * mm, "end": v(224.26, -58.5) * mm});
            skLineSegment(sketch, "E2882", {"start": v(224.26, -58.5) * mm, "end": v(223.98, -60.35) * mm});
            skLineSegment(sketch, "E2883", {"start": v(223.98, -60.35) * mm, "end": v(223.7, -62.18) * mm});
            skLineSegment(sketch, "E2884", {"start": v(223.7, -62.18) * mm, "end": v(223.4, -64.02) * mm});
            skLineSegment(sketch, "E2885", {"start": v(223.4, -64.02) * mm, "end": v(223.1, -65.85) * mm});
            skLineSegment(sketch, "E2886", {"start": v(223.1, -65.85) * mm, "end": v(222.8, -67.67) * mm});
            skLineSegment(sketch, "E2887", {"start": v(222.8, -67.67) * mm, "end": v(222.48, -69.5) * mm});
            skLineSegment(sketch, "E2888", {"start": v(222.48, -69.5) * mm, "end": v(222.15, -71.31) * mm});
            skLineSegment(sketch, "E2889", {"start": v(222.15, -71.31) * mm, "end": v(221.82, -73.12) * mm});
            skLineSegment(sketch, "E2890", {"start": v(221.82, -73.12) * mm, "end": v(221.48, -74.93) * mm});
            skLineSegment(sketch, "E2891", {"start": v(221.48, -74.93) * mm, "end": v(221.12, -76.73) * mm});
            skLineSegment(sketch, "E2892", {"start": v(221.12, -76.73) * mm, "end": v(220.76, -78.52) * mm});
            skLineSegment(sketch, "E2893", {"start": v(220.76, -78.52) * mm, "end": v(220.4, -80.31) * mm});
            skLineSegment(sketch, "E2894", {"start": v(220.4, -80.31) * mm, "end": v(220.02, -82.1) * mm});
            skLineSegment(sketch, "E2895", {"start": v(220.02, -82.1) * mm, "end": v(219.63, -83.88) * mm});
            skLineSegment(sketch, "E2896", {"start": v(219.63, -83.88) * mm, "end": v(219.24, -85.66) * mm});
            skLineSegment(sketch, "E2897", {"start": v(219.24, -85.66) * mm, "end": v(218.84, -87.43) * mm});
            skLineSegment(sketch, "E2898", {"start": v(218.84, -87.43) * mm, "end": v(218.42, -89.2) * mm});
            skLineSegment(sketch, "E2899", {"start": v(218.42, -89.2) * mm, "end": v(218, -90.96) * mm});
            skLineSegment(sketch, "E2900", {"start": v(218, -90.96) * mm, "end": v(217.58, -92.72) * mm});
            skLineSegment(sketch, "E2901", {"start": v(217.58, -92.72) * mm, "end": v(217.14, -94.47) * mm});
            skLineSegment(sketch, "E2902", {"start": v(217.14, -94.47) * mm, "end": v(216.7, -96.22) * mm});
            skLineSegment(sketch, "E2903", {"start": v(216.7, -96.22) * mm, "end": v(216.24, -97.96) * mm});
            skLineSegment(sketch, "E2904", {"start": v(216.24, -97.96) * mm, "end": v(215.78, -99.7) * mm});
            skLineSegment(sketch, "E2905", {"start": v(215.78, -99.7) * mm, "end": v(215.3, -101.43) * mm});
            skLineSegment(sketch, "E2906", {"start": v(215.3, -101.43) * mm, "end": v(214.83, -103.16) * mm});
            skLineSegment(sketch, "E2907", {"start": v(214.83, -103.16) * mm, "end": v(214.34, -104.89) * mm});
            skLineSegment(sketch, "E2908", {"start": v(214.34, -104.89) * mm, "end": v(213.85, -106.6) * mm});
            skLineSegment(sketch, "E2909", {"start": v(213.85, -106.6) * mm, "end": v(213.34, -108.32) * mm});
            skLineSegment(sketch, "E2910", {"start": v(213.34, -108.32) * mm, "end": v(212.83, -110.03) * mm});
            skLineSegment(sketch, "E2911", {"start": v(212.83, -110.03) * mm, "end": v(212.3, -111.73) * mm});
            skLineSegment(sketch, "E2912", {"start": v(212.3, -111.73) * mm, "end": v(211.78, -113.43) * mm});
            skLineSegment(sketch, "E2913", {"start": v(211.78, -113.43) * mm, "end": v(211.24, -115.13) * mm});
            skLineSegment(sketch, "E2914", {"start": v(211.24, -115.13) * mm, "end": v(210.7, -116.82) * mm});
            skLineSegment(sketch, "E2915", {"start": v(210.7, -116.82) * mm, "end": v(210.14, -118.5) * mm});
            skLineSegment(sketch, "E2916", {"start": v(210.14, -118.5) * mm, "end": v(209.57, -120.18) * mm});
            skLineSegment(sketch, "E2917", {"start": v(209.57, -120.18) * mm, "end": v(209, -121.86) * mm});
            skLineSegment(sketch, "E2918", {"start": v(209, -121.86) * mm, "end": v(208.42, -123.53) * mm});
            skLineSegment(sketch, "E2919", {"start": v(208.42, -123.53) * mm, "end": v(207.83, -125.2) * mm});
            skLineSegment(sketch, "E2920", {"start": v(207.83, -125.2) * mm, "end": v(207.24, -126.85) * mm});
            skLineSegment(sketch, "E2921", {"start": v(207.24, -126.85) * mm, "end": v(206.63, -128.5) * mm});
            skLineSegment(sketch, "E2922", {"start": v(206.63, -128.5) * mm, "end": v(206.01, -130.16) * mm});
            skLineSegment(sketch, "E2923", {"start": v(206.01, -130.16) * mm, "end": v(205.4, -131.8) * mm});
            skLineSegment(sketch, "E2924", {"start": v(205.4, -131.8) * mm, "end": v(204.76, -133.45) * mm});
            skLineSegment(sketch, "E2925", {"start": v(204.76, -133.45) * mm, "end": v(204.12, -135.09) * mm});
            skLineSegment(sketch, "E2926", {"start": v(204.12, -135.09) * mm, "end": v(203.47, -136.72) * mm});
            skLineSegment(sketch, "E2927", {"start": v(203.47, -136.72) * mm, "end": v(202.81, -138.34) * mm});
            skLineSegment(sketch, "E2928", {"start": v(202.81, -138.34) * mm, "end": v(202.15, -139.97) * mm});
            skLineSegment(sketch, "E2929", {"start": v(202.15, -139.97) * mm, "end": v(201.48, -141.58) * mm});
            skLineSegment(sketch, "E2930", {"start": v(201.48, -141.58) * mm, "end": v(200.8, -143.2) * mm});
            skLineSegment(sketch, "E2931", {"start": v(200.8, -143.2) * mm, "end": v(200.1, -144.8) * mm});
            skLineSegment(sketch, "E2932", {"start": v(200.1, -144.8) * mm, "end": v(199.4, -146.4) * mm});
            skLineSegment(sketch, "E2933", {"start": v(199.4, -146.4) * mm, "end": v(198.7, -148) * mm});
            skLineSegment(sketch, "E2934", {"start": v(198.7, -148) * mm, "end": v(197.98, -149.6) * mm});
            skLineSegment(sketch, "E2935", {"start": v(197.98, -149.6) * mm, "end": v(197.25, -151.19) * mm});
            skLineSegment(sketch, "E2936", {"start": v(197.25, -151.19) * mm, "end": v(196.52, -152.77) * mm});
            skLineSegment(sketch, "E2937", {"start": v(196.52, -152.77) * mm, "end": v(195.78, -154.35) * mm});
            skLineSegment(sketch, "E2938", {"start": v(195.78, -154.35) * mm, "end": v(195.03, -155.92) * mm});
            skLineSegment(sketch, "E2939", {"start": v(195.03, -155.92) * mm, "end": v(194.27, -157.5) * mm});
            skLineSegment(sketch, "E2940", {"start": v(194.27, -157.5) * mm, "end": v(193.5, -159.06) * mm});
            skLineSegment(sketch, "E2941", {"start": v(193.5, -159.06) * mm, "end": v(192.73, -160.62) * mm});
            skLineSegment(sketch, "E2942", {"start": v(192.73, -160.62) * mm, "end": v(191.94, -162.17) * mm});
            skLineSegment(sketch, "E2943", {"start": v(191.94, -162.17) * mm, "end": v(191.15, -163.72) * mm});
            skLineSegment(sketch, "E2944", {"start": v(191.15, -163.72) * mm, "end": v(190.35, -165.27) * mm});
            skLineSegment(sketch, "E2945", {"start": v(190.35, -165.27) * mm, "end": v(189.54, -166.8) * mm});
            skLineSegment(sketch, "E2946", {"start": v(189.54, -166.8) * mm, "end": v(188.72, -168.34) * mm});
            skLineSegment(sketch, "E2947", {"start": v(188.72, -168.34) * mm, "end": v(187.9, -169.87) * mm});
            skLineSegment(sketch, "E2948", {"start": v(187.9, -169.87) * mm, "end": v(187.06, -171.4) * mm});
            skLineSegment(sketch, "E2949", {"start": v(187.06, -171.4) * mm, "end": v(186.22, -172.92) * mm});
            skLineSegment(sketch, "E2950", {"start": v(186.22, -172.92) * mm, "end": v(185.37, -174.43) * mm});
            skLineSegment(sketch, "E2951", {"start": v(185.37, -174.43) * mm, "end": v(184.5, -175.95) * mm});
            skLineSegment(sketch, "E2952", {"start": v(184.5, -175.95) * mm, "end": v(183.64, -177.45) * mm});
            skLineSegment(sketch, "E2953", {"start": v(183.64, -177.45) * mm, "end": v(182.76, -178.95) * mm});
            skLineSegment(sketch, "E2954", {"start": v(182.76, -178.95) * mm, "end": v(181.87, -180.45) * mm});
            skLineSegment(sketch, "E2955", {"start": v(181.87, -180.45) * mm, "end": v(180.98, -181.94) * mm});
            skLineSegment(sketch, "E2956", {"start": v(180.98, -181.94) * mm, "end": v(180.08, -183.43) * mm});
            skLineSegment(sketch, "E2957", {"start": v(180.08, -183.43) * mm, "end": v(179.17, -184.91) * mm});
            skLineSegment(sketch, "E2958", {"start": v(179.17, -184.91) * mm, "end": v(178.25, -186.39) * mm});
            skLineSegment(sketch, "E2959", {"start": v(178.25, -186.39) * mm, "end": v(177.32, -187.86) * mm});
            skLineSegment(sketch, "E2960", {"start": v(177.32, -187.86) * mm, "end": v(176.38, -189.33) * mm});
            skLineSegment(sketch, "E2961", {"start": v(176.38, -189.33) * mm, "end": v(175.44, -190.8) * mm});
            skLineSegment(sketch, "E2962", {"start": v(175.44, -190.8) * mm, "end": v(174.48, -192.25) * mm});
            skLineSegment(sketch, "E2963", {"start": v(174.48, -192.25) * mm, "end": v(173.52, -193.7) * mm});
            skLineSegment(sketch, "E2964", {"start": v(173.52, -193.7) * mm, "end": v(172.55, -195.15) * mm});
            skLineSegment(sketch, "E2965", {"start": v(172.55, -195.15) * mm, "end": v(171.57, -196.6) * mm});
            skLineSegment(sketch, "E2966", {"start": v(171.57, -196.6) * mm, "end": v(170.58, -198.03) * mm});
            skLineSegment(sketch, "E2967", {"start": v(170.58, -198.03) * mm, "end": v(169.59, -199.47) * mm});
            skLineSegment(sketch, "E2968", {"start": v(169.59, -199.47) * mm, "end": v(168.58, -200.9) * mm});
            skLineSegment(sketch, "E2969", {"start": v(168.58, -200.9) * mm, "end": v(167.57, -202.32) * mm});
            skLineSegment(sketch, "E2970", {"start": v(167.57, -202.32) * mm, "end": v(166.55, -203.74) * mm});
            skLineSegment(sketch, "E2971", {"start": v(166.55, -203.74) * mm, "end": v(165.52, -205.15) * mm});
            skLineSegment(sketch, "E2972", {"start": v(165.52, -205.15) * mm, "end": v(164.48, -206.56) * mm});
            skLineSegment(sketch, "E2973", {"start": v(164.48, -206.56) * mm, "end": v(163.43, -207.97) * mm});
            skLineSegment(sketch, "E2974", {"start": v(163.43, -207.97) * mm, "end": v(162.38, -209.37) * mm});
            skLineSegment(sketch, "E2975", {"start": v(162.38, -209.37) * mm, "end": v(161.31, -210.76) * mm});
            skLineSegment(sketch, "E2976", {"start": v(161.31, -210.76) * mm, "end": v(160.24, -212.15) * mm});
            skLineSegment(sketch, "E2977", {"start": v(160.24, -212.15) * mm, "end": v(159.16, -213.54) * mm});
            skLineSegment(sketch, "E2978", {"start": v(159.16, -213.54) * mm, "end": v(158.33, -214.99) * mm});
            skLineSegment(sketch, "E2979", {"start": v(158.33, -214.99) * mm, "end": v(157.5, -216.43) * mm});
            skLineSegment(sketch, "E2980", {"start": v(157.5, -216.43) * mm, "end": v(156.65, -217.85) * mm});
            skLineSegment(sketch, "E2981", {"start": v(156.65, -217.85) * mm, "end": v(155.8, -219.27) * mm});
            skLineSegment(sketch, "E2982", {"start": v(155.8, -219.27) * mm, "end": v(154.93, -220.67) * mm});
            skLineSegment(sketch, "E2983", {"start": v(154.93, -220.67) * mm, "end": v(154.06, -222.06) * mm});
            skLineSegment(sketch, "E2984", {"start": v(154.06, -222.06) * mm, "end": v(153.17, -223.44) * mm});
            skLineSegment(sketch, "E2985", {"start": v(153.17, -223.44) * mm, "end": v(152.28, -224.81) * mm});
            skLineSegment(sketch, "E2986", {"start": v(152.28, -224.81) * mm, "end": v(151.37, -226.17) * mm});
            skLineSegment(sketch, "E2987", {"start": v(151.37, -226.17) * mm, "end": v(150.46, -227.52) * mm});
            skLineSegment(sketch, "E2988", {"start": v(150.46, -227.52) * mm, "end": v(149.54, -228.85) * mm});
            skLineSegment(sketch, "E2989", {"start": v(149.54, -228.85) * mm, "end": v(148.6, -230.17) * mm});
            skLineSegment(sketch, "E2990", {"start": v(148.6, -230.17) * mm, "end": v(147.66, -231.49) * mm});
            skLineSegment(sketch, "E2991", {"start": v(147.66, -231.49) * mm, "end": v(146.7, -232.79) * mm});
            skLineSegment(sketch, "E2992", {"start": v(146.7, -232.79) * mm, "end": v(145.75, -234.08) * mm});
            skLineSegment(sketch, "E2993", {"start": v(145.75, -234.08) * mm, "end": v(144.78, -235.35) * mm});
            skLineSegment(sketch, "E2994", {"start": v(144.78, -235.35) * mm, "end": v(143.8, -236.62) * mm});
            skLineSegment(sketch, "E2995", {"start": v(143.8, -236.62) * mm, "end": v(142.8, -237.88) * mm});
            skLineSegment(sketch, "E2996", {"start": v(142.8, -237.88) * mm, "end": v(141.8, -239.12) * mm});
            skLineSegment(sketch, "E2997", {"start": v(141.8, -239.12) * mm, "end": v(140.8, -240.35) * mm});
            skLineSegment(sketch, "E2998", {"start": v(140.8, -240.35) * mm, "end": v(139.77, -241.58) * mm});
            skLineSegment(sketch, "E2999", {"start": v(139.77, -241.58) * mm, "end": v(138.74, -242.79) * mm});
            skLineSegment(sketch, "E3000", {"start": v(138.74, -242.79) * mm, "end": v(137.7, -243.98) * mm});
            skLineSegment(sketch, "E3001", {"start": v(137.7, -243.98) * mm, "end": v(136.66, -245.17) * mm});
            skLineSegment(sketch, "E3002", {"start": v(136.66, -245.17) * mm, "end": v(135.6, -246.35) * mm});
            skLineSegment(sketch, "E3003", {"start": v(135.6, -246.35) * mm, "end": v(134.53, -247.51) * mm});
            skLineSegment(sketch, "E3004", {"start": v(134.53, -247.51) * mm, "end": v(133.45, -248.67) * mm});
            skLineSegment(sketch, "E3005", {"start": v(133.45, -248.67) * mm, "end": v(132.37, -249.8) * mm});
            skLineSegment(sketch, "E3006", {"start": v(132.37, -249.8) * mm, "end": v(131.27, -250.94) * mm});
            skLineSegment(sketch, "E3007", {"start": v(131.27, -250.94) * mm, "end": v(130.16, -252.06) * mm});
            skLineSegment(sketch, "E3008", {"start": v(130.16, -252.06) * mm, "end": v(129.04, -253.16) * mm});
            skLineSegment(sketch, "E3009", {"start": v(129.04, -253.16) * mm, "end": v(127.92, -254.26) * mm});
            skLineSegment(sketch, "E3010", {"start": v(127.92, -254.26) * mm, "end": v(126.78, -255.35) * mm});
            skLineSegment(sketch, "E3011", {"start": v(126.78, -255.35) * mm, "end": v(125.64, -256.42) * mm});
            skLineSegment(sketch, "E3012", {"start": v(125.64, -256.42) * mm, "end": v(124.48, -257.48) * mm});
            skLineSegment(sketch, "E3013", {"start": v(124.48, -257.48) * mm, "end": v(123.32, -258.53) * mm});
            skLineSegment(sketch, "E3014", {"start": v(123.32, -258.53) * mm, "end": v(122.14, -259.57) * mm});
            skLineSegment(sketch, "E3015", {"start": v(122.14, -259.57) * mm, "end": v(120.96, -260.6) * mm});
            skLineSegment(sketch, "E3016", {"start": v(120.96, -260.6) * mm, "end": v(119.77, -261.62) * mm});
            skLineSegment(sketch, "E3017", {"start": v(119.77, -261.62) * mm, "end": v(118.56, -262.62) * mm});
            skLineSegment(sketch, "E3018", {"start": v(118.56, -262.62) * mm, "end": v(117.35, -263.62) * mm});
            skLineSegment(sketch, "E3019", {"start": v(117.35, -263.62) * mm, "end": v(116.13, -264.6) * mm});
            skLineSegment(sketch, "E3020", {"start": v(116.13, -264.6) * mm, "end": v(114.9, -265.57) * mm});
            skLineSegment(sketch, "E3021", {"start": v(114.9, -265.57) * mm, "end": v(113.65, -266.53) * mm});
            skLineSegment(sketch, "E3022", {"start": v(113.65, -266.53) * mm, "end": v(112.4, -267.48) * mm});
            skLineSegment(sketch, "E3023", {"start": v(112.4, -267.48) * mm, "end": v(111.14, -268.42) * mm});
            skLineSegment(sketch, "E3024", {"start": v(111.14, -268.42) * mm, "end": v(109.87, -269.34) * mm});
            skLineSegment(sketch, "E3025", {"start": v(109.87, -269.34) * mm, "end": v(108.59, -270.26) * mm});
            skLineSegment(sketch, "E3026", {"start": v(108.59, -270.26) * mm, "end": v(107.3, -271.16) * mm});
            skLineSegment(sketch, "E3027", {"start": v(107.3, -271.16) * mm, "end": v(106, -272.05) * mm});
            skLineSegment(sketch, "E3028", {"start": v(106, -272.05) * mm, "end": v(104.69, -272.93) * mm});
            skLineSegment(sketch, "E3029", {"start": v(104.69, -272.93) * mm, "end": v(103.37, -273.8) * mm});
            skLineSegment(sketch, "E3030", {"start": v(103.37, -273.8) * mm, "end": v(102.04, -274.66) * mm});
            skLineSegment(sketch, "E3031", {"start": v(102.04, -274.66) * mm, "end": v(100.7, -275.5) * mm});
            skLineSegment(sketch, "E3032", {"start": v(100.7, -275.5) * mm, "end": v(99.35, -276.34) * mm});
            skLineSegment(sketch, "E3033", {"start": v(99.35, -276.34) * mm, "end": v(98, -277.17) * mm});
            skLineSegment(sketch, "E3034", {"start": v(98, -277.17) * mm, "end": v(96.63, -277.98) * mm});
            skLineSegment(sketch, "E3035", {"start": v(96.63, -277.98) * mm, "end": v(95.25, -278.78) * mm});
            skLineSegment(sketch, "E3036", {"start": v(95.25, -278.78) * mm, "end": v(93.86, -279.57) * mm});
            skLineSegment(sketch, "E3037", {"start": v(93.86, -279.57) * mm, "end": v(92.47, -280.35) * mm});
            skLineSegment(sketch, "E3038", {"start": v(92.47, -280.35) * mm, "end": v(91.06, -281.11) * mm});
            skLineSegment(sketch, "E3039", {"start": v(91.06, -281.11) * mm, "end": v(89.64, -281.87) * mm});
            skLineSegment(sketch, "E3040", {"start": v(89.64, -281.87) * mm, "end": v(88.22, -282.61) * mm});
            skLineSegment(sketch, "E3041", {"start": v(88.22, -282.61) * mm, "end": v(86.78, -283.35) * mm});
            skLineSegment(sketch, "E3042", {"start": v(86.78, -283.35) * mm, "end": v(85.34, -284.07) * mm});
            skLineSegment(sketch, "E3043", {"start": v(85.34, -284.07) * mm, "end": v(83.88, -284.78) * mm});
            skLineSegment(sketch, "E3044", {"start": v(83.88, -284.78) * mm, "end": v(82.42, -285.48) * mm});
            skLineSegment(sketch, "E3045", {"start": v(82.42, -285.48) * mm, "end": v(80.94, -286.16) * mm});
            skLineSegment(sketch, "E3046", {"start": v(80.94, -286.16) * mm, "end": v(79.46, -286.84) * mm});
            skLineSegment(sketch, "E3047", {"start": v(79.46, -286.84) * mm, "end": v(77.97, -287.5) * mm});
            skLineSegment(sketch, "E3048", {"start": v(77.97, -287.5) * mm, "end": v(76.46, -288.16) * mm});
            skLineSegment(sketch, "E3049", {"start": v(76.46, -288.16) * mm, "end": v(74.95, -288.8) * mm});
            skLineSegment(sketch, "E3050", {"start": v(74.95, -288.8) * mm, "end": v(73.43, -289.43) * mm});
            skLineSegment(sketch, "E3051", {"start": v(73.43, -289.43) * mm, "end": v(71.9, -290.05) * mm});
            skLineSegment(sketch, "E3052", {"start": v(71.9, -290.05) * mm, "end": v(70.36, -290.66) * mm});
            skLineSegment(sketch, "E3053", {"start": v(70.36, -290.66) * mm, "end": v(68.8, -291.25) * mm});
            skLineSegment(sketch, "E3054", {"start": v(68.8, -291.25) * mm, "end": v(67.24, -291.84) * mm});
            skLineSegment(sketch, "E3055", {"start": v(67.24, -291.84) * mm, "end": v(65.67, -292.41) * mm});
            skLineSegment(sketch, "E3056", {"start": v(65.67, -292.41) * mm, "end": v(64.1, -292.98) * mm});
            skLineSegment(sketch, "E3057", {"start": v(64.1, -292.98) * mm, "end": v(62.5, -293.53) * mm});
            skLineSegment(sketch, "E3058", {"start": v(62.5, -293.53) * mm, "end": v(60.9, -294.07) * mm});
            skLineSegment(sketch, "E3059", {"start": v(60.9, -294.07) * mm, "end": v(59.3, -294.6) * mm});
            skLineSegment(sketch, "E3060", {"start": v(59.3, -294.6) * mm, "end": v(57.68, -295.11) * mm});
            skLineSegment(sketch, "E3061", {"start": v(57.68, -295.11) * mm, "end": v(56.05, -295.62) * mm});
            skLineSegment(sketch, "E3062", {"start": v(56.05, -295.62) * mm, "end": v(54.4, -296.11) * mm});
            skLineSegment(sketch, "E3063", {"start": v(54.4, -296.11) * mm, "end": v(52.76, -296.6) * mm});
            skLineSegment(sketch, "E3064", {"start": v(52.76, -296.6) * mm, "end": v(51.1, -297.07) * mm});
            skLineSegment(sketch, "E3065", {"start": v(51.1, -297.07) * mm, "end": v(49.44, -297.53) * mm});
            skLineSegment(sketch, "E3066", {"start": v(49.44, -297.53) * mm, "end": v(47.76, -297.98) * mm});
            skLineSegment(sketch, "E3067", {"start": v(47.76, -297.98) * mm, "end": v(46.07, -298.41) * mm});
            skLineSegment(sketch, "E3068", {"start": v(46.07, -298.41) * mm, "end": v(44.38, -298.84) * mm});
            skLineSegment(sketch, "E3069", {"start": v(44.38, -298.84) * mm, "end": v(42.67, -299.25) * mm});
            skLineSegment(sketch, "E3070", {"start": v(42.67, -299.25) * mm, "end": v(40.96, -299.66) * mm});
            skLineSegment(sketch, "E3071", {"start": v(40.96, -299.66) * mm, "end": v(39.23, -300.05) * mm});
            skLineSegment(sketch, "E3072", {"start": v(39.23, -300.05) * mm, "end": v(37.5, -300.43) * mm});
            skLineSegment(sketch, "E3073", {"start": v(37.5, -300.43) * mm, "end": v(35.75, -300.8) * mm});
            skLineSegment(sketch, "E3074", {"start": v(35.75, -300.8) * mm, "end": v(34, -301.16) * mm});
            skLineSegment(sketch, "E3075", {"start": v(34, -301.16) * mm, "end": v(32.23, -301.5) * mm});
            skLineSegment(sketch, "E3076", {"start": v(32.23, -301.5) * mm, "end": v(30.46, -301.84) * mm});
            skLineSegment(sketch, "E3077", {"start": v(30.46, -301.84) * mm, "end": v(28.68, -302.16) * mm});
            skLineSegment(sketch, "E3078", {"start": v(28.68, -302.16) * mm, "end": v(26.88, -302.47) * mm});
            skLineSegment(sketch, "E3079", {"start": v(26.88, -302.47) * mm, "end": v(25.08, -302.78) * mm});
            skLineSegment(sketch, "E3080", {"start": v(25.08, -302.78) * mm, "end": v(23.27, -303.07) * mm});
            skLineSegment(sketch, "E3081", {"start": v(23.27, -303.07) * mm, "end": v(21.45, -303.34) * mm});
            skLineSegment(sketch, "E3082", {"start": v(21.45, -303.34) * mm, "end": v(19.62, -303.61) * mm});
            skLineSegment(sketch, "E3083", {"start": v(19.62, -303.61) * mm, "end": v(17.78, -303.87) * mm});
            skLineSegment(sketch, "E3084", {"start": v(17.78, -303.87) * mm, "end": v(15.92, -304.11) * mm});
            skLineSegment(sketch, "E3085", {"start": v(15.92, -304.11) * mm, "end": v(14.06, -304.34) * mm});
            skLineSegment(sketch, "E3086", {"start": v(14.06, -304.34) * mm, "end": v(12.2, -304.57) * mm});
            skLineSegment(sketch, "E3087", {"start": v(12.2, -304.57) * mm, "end": v(10.31, -304.78) * mm});
            skLineSegment(sketch, "E3088", {"start": v(10.31, -304.78) * mm, "end": v(8.42, -304.97) * mm});
            skLineSegment(sketch, "E3089", {"start": v(8.42, -304.97) * mm, "end": v(6.53, -305.16) * mm});
            skLineSegment(sketch, "E3090", {"start": v(6.53, -305.16) * mm, "end": v(4.62, -305.34) * mm});
            skLineSegment(sketch, "E3091", {"start": v(4.62, -305.34) * mm, "end": v(2.7, -305.5) * mm});
            skLineSegment(sketch, "E3092", {"start": v(2.7, -305.5) * mm, "end": v(0.77, -305.66) * mm});
            skLineSegment(sketch, "E3093", {"start": v(0.77, -305.66) * mm, "end": v(-1.17, -305.8) * mm});
            skLineSegment(sketch, "E3094", {"start": v(-1.17, -305.8) * mm, "end": v(-3.11, -305.93) * mm});
            skLineSegment(sketch, "E3095", {"start": v(-3.11, -305.93) * mm, "end": v(-5.07, -306.05) * mm});
            skLineSegment(sketch, "E3096", {"start": v(-5.07, -306.05) * mm, "end": v(-7.04, -306.16) * mm});
            skLineSegment(sketch, "E3097", {"start": v(-7.04, -306.16) * mm, "end": v(-9.01, -306.25) * mm});
            skLineSegment(sketch, "E3098", {"start": v(-9.01, -306.25) * mm, "end": v(-11, -306.34) * mm});
            skLineSegment(sketch, "E3099", {"start": v(-11, -306.34) * mm, "end": v(-13, -306.41) * mm});
            skLineSegment(sketch, "E3100", {"start": v(-13, -306.41) * mm, "end": v(-15, -306.47) * mm});
            skLineSegment(sketch, "E3101", {"start": v(-15, -306.47) * mm, "end": v(-17.02, -306.53) * mm});
            skLineSegment(sketch, "E3102", {"start": v(-17.02, -306.53) * mm, "end": v(-19.04, -306.56) * mm});
            skLineSegment(sketch, "E3103", {"start": v(-19.04, -306.56) * mm, "end": v(-21.08, -306.6) * mm});
            skLineSegment(sketch, "E3104", {"start": v(-21.08, -306.6) * mm, "end": v(-23.12, -306.61) * mm});
            skLineSegment(sketch, "E3105", {"start": v(-23.12, -306.61) * mm, "end": v(-25.17, -306.62) * mm});
            skLineSegment(sketch, "E3106", {"start": v(-25.17, -306.62) * mm, "end": v(-228.6, -306.62) * mm});
            skLineSegment(sketch, "E3107", {"start": v(-228.6, -306.62) * mm, "end": v(-228.6, -272.15) * mm});
            skLineSegment(sketch, "E3108", {"start": v(-228.6, -272.15) * mm, "end": v(-205.42, -272.15) * mm});
            skLineSegment(sketch, "E3109", {"start": v(-205.42, -272.15) * mm, "end": v(-204.67, -272.14) * mm});
            skLineSegment(sketch, "E3110", {"start": v(-204.67, -272.14) * mm, "end": v(-203.92, -272.13) * mm});
            skLineSegment(sketch, "E3111", {"start": v(-203.92, -272.13) * mm, "end": v(-203.18, -272.1) * mm});
            skLineSegment(sketch, "E3112", {"start": v(-203.18, -272.1) * mm, "end": v(-202.45, -272.07) * mm});
            skLineSegment(sketch, "E3113", {"start": v(-202.45, -272.07) * mm, "end": v(-201.72, -272.03) * mm});
            skLineSegment(sketch, "E3114", {"start": v(-201.72, -272.03) * mm, "end": v(-201, -271.97) * mm});
            skLineSegment(sketch, "E3115", {"start": v(-201, -271.97) * mm, "end": v(-200.29, -271.9) * mm});
            skLineSegment(sketch, "E3116", {"start": v(-200.29, -271.9) * mm, "end": v(-199.58, -271.84) * mm});
            skLineSegment(sketch, "E3117", {"start": v(-199.58, -271.84) * mm, "end": v(-198.88, -271.75) * mm});
            skLineSegment(sketch, "E3118", {"start": v(-198.88, -271.75) * mm, "end": v(-198.2, -271.66) * mm});
            skLineSegment(sketch, "E3119", {"start": v(-198.2, -271.66) * mm, "end": v(-197.5, -271.56) * mm});
            skLineSegment(sketch, "E3120", {"start": v(-197.5, -271.56) * mm, "end": v(-196.83, -271.44) * mm});
            skLineSegment(sketch, "E3121", {"start": v(-196.83, -271.44) * mm, "end": v(-196.16, -271.32) * mm});
            skLineSegment(sketch, "E3122", {"start": v(-196.16, -271.32) * mm, "end": v(-195.5, -271.19) * mm});
            skLineSegment(sketch, "E3123", {"start": v(-195.5, -271.19) * mm, "end": v(-194.84, -271.05) * mm});
            skLineSegment(sketch, "E3124", {"start": v(-194.84, -271.05) * mm, "end": v(-194.2, -270.9) * mm});
            skLineSegment(sketch, "E3125", {"start": v(-194.2, -270.9) * mm, "end": v(-193.55, -270.73) * mm});
            skLineSegment(sketch, "E3126", {"start": v(-193.55, -270.73) * mm, "end": v(-192.92, -270.56) * mm});
            skLineSegment(sketch, "E3127", {"start": v(-192.92, -270.56) * mm, "end": v(-192.29, -270.38) * mm});
            skLineSegment(sketch, "E3128", {"start": v(-192.29, -270.38) * mm, "end": v(-191.67, -270.2) * mm});
            skLineSegment(sketch, "E3129", {"start": v(-191.67, -270.2) * mm, "end": v(-191.06, -269.99) * mm});
            skLineSegment(sketch, "E3130", {"start": v(-191.06, -269.99) * mm, "end": v(-190.45, -269.78) * mm});
            skLineSegment(sketch, "E3131", {"start": v(-190.45, -269.78) * mm, "end": v(-189.85, -269.56) * mm});
            skLineSegment(sketch, "E3132", {"start": v(-189.85, -269.56) * mm, "end": v(-189.26, -269.33) * mm});
            skLineSegment(sketch, "E3133", {"start": v(-189.26, -269.33) * mm, "end": v(-188.68, -269.09) * mm});
            skLineSegment(sketch, "E3134", {"start": v(-188.68, -269.09) * mm, "end": v(-188.1, -268.84) * mm});
            skLineSegment(sketch, "E3135", {"start": v(-188.1, -268.84) * mm, "end": v(-187.53, -268.58) * mm});
            skLineSegment(sketch, "E3136", {"start": v(-187.53, -268.58) * mm, "end": v(-186.96, -268.3) * mm});
            skLineSegment(sketch, "E3137", {"start": v(-186.96, -268.3) * mm, "end": v(-186.4, -268.03) * mm});
            skLineSegment(sketch, "E3138", {"start": v(-186.4, -268.03) * mm, "end": v(-185.86, -267.74) * mm});
            skLineSegment(sketch, "E3139", {"start": v(-185.86, -267.74) * mm, "end": v(-185.32, -267.44) * mm});
            skLineSegment(sketch, "E3140", {"start": v(-185.32, -267.44) * mm, "end": v(-184.78, -267.13) * mm});
            skLineSegment(sketch, "E3141", {"start": v(-184.78, -267.13) * mm, "end": v(-184.25, -266.81) * mm});
            skLineSegment(sketch, "E3142", {"start": v(-184.25, -266.81) * mm, "end": v(-183.73, -266.49) * mm});
            skLineSegment(sketch, "E3143", {"start": v(-183.73, -266.49) * mm, "end": v(-183.22, -266.15) * mm});
            skLineSegment(sketch, "E3144", {"start": v(-183.22, -266.15) * mm, "end": v(-182.71, -265.8) * mm});
            skLineSegment(sketch, "E3145", {"start": v(-182.71, -265.8) * mm, "end": v(-182.22, -265.44) * mm});
            skLineSegment(sketch, "E3146", {"start": v(-182.22, -265.44) * mm, "end": v(-181.72, -265.08) * mm});
            skLineSegment(sketch, "E3147", {"start": v(-181.72, -265.08) * mm, "end": v(-181.24, -264.7) * mm});
            skLineSegment(sketch, "E3148", {"start": v(-181.24, -264.7) * mm, "end": v(-180.76, -264.31) * mm});
            skLineSegment(sketch, "E3149", {"start": v(-180.76, -264.31) * mm, "end": v(-180.29, -263.91) * mm});
            skLineSegment(sketch, "E3150", {"start": v(-180.29, -263.91) * mm, "end": v(-179.83, -263.5) * mm});
            skLineSegment(sketch, "E3151", {"start": v(-179.83, -263.5) * mm, "end": v(-179.37, -263.1) * mm});
            skLineSegment(sketch, "E3152", {"start": v(-179.37, -263.1) * mm, "end": v(-178.92, -262.67) * mm});
            skLineSegment(sketch, "E3153", {"start": v(-178.92, -262.67) * mm, "end": v(-178.48, -262.23) * mm});
            skLineSegment(sketch, "E3154", {"start": v(-178.48, -262.23) * mm, "end": v(-178.04, -261.78) * mm});
            skLineSegment(sketch, "E3155", {"start": v(-178.04, -261.78) * mm, "end": v(-177.61, -261.33) * mm});
            skLineSegment(sketch, "E3156", {"start": v(-177.61, -261.33) * mm, "end": v(-177.2, -260.86) * mm});
            skLineSegment(sketch, "E3157", {"start": v(-177.2, -260.86) * mm, "end": v(-176.78, -260.39) * mm});
            skLineSegment(sketch, "E3158", {"start": v(-176.78, -260.39) * mm, "end": v(-176.37, -259.9) * mm});
            skLineSegment(sketch, "E3159", {"start": v(-176.37, -259.9) * mm, "end": v(-175.97, -259.4) * mm});
            skLineSegment(sketch, "E3160", {"start": v(-175.97, -259.4) * mm, "end": v(-175.58, -258.9) * mm});
            skLineSegment(sketch, "E3161", {"start": v(-175.58, -258.9) * mm, "end": v(-175.2, -258.39) * mm});
            skLineSegment(sketch, "E3162", {"start": v(-175.2, -258.39) * mm, "end": v(-174.82, -257.86) * mm});
            skLineSegment(sketch, "E3163", {"start": v(-174.82, -257.86) * mm, "end": v(-174.44, -257.33) * mm});
            skLineSegment(sketch, "E3164", {"start": v(-174.44, -257.33) * mm, "end": v(-174.08, -256.79) * mm});
            skLineSegment(sketch, "E3165", {"start": v(-174.08, -256.79) * mm, "end": v(-173.72, -256.23) * mm});
            skLineSegment(sketch, "E3166", {"start": v(-173.72, -256.23) * mm, "end": v(-173.37, -255.67) * mm});
            skLineSegment(sketch, "E3167", {"start": v(-173.37, -255.67) * mm, "end": v(-173.03, -255.1) * mm});
            skLineSegment(sketch, "E3168", {"start": v(-173.03, -255.1) * mm, "end": v(-172.7, -254.51) * mm});
            skLineSegment(sketch, "E3169", {"start": v(-172.7, -254.51) * mm, "end": v(-172.37, -253.92) * mm});
            skLineSegment(sketch, "E3170", {"start": v(-172.37, -253.92) * mm, "end": v(-172.05, -253.32) * mm});
            skLineSegment(sketch, "E3171", {"start": v(-172.05, -253.32) * mm, "end": v(-171.73, -252.7) * mm});
            skLineSegment(sketch, "E3172", {"start": v(-171.73, -252.7) * mm, "end": v(-171.42, -252.08) * mm});
            skLineSegment(sketch, "E3173", {"start": v(-171.42, -252.08) * mm, "end": v(-171.23, -251.69) * mm});
            skLineSegment(sketch, "E3174", {"start": v(-171.23, -251.69) * mm, "end": v(-171.05, -251.28) * mm});
            skLineSegment(sketch, "E3175", {"start": v(-171.05, -251.28) * mm, "end": v(-170.87, -250.85) * mm});
            skLineSegment(sketch, "E3176", {"start": v(-170.87, -250.85) * mm, "end": v(-170.69, -250.4) * mm});
            skLineSegment(sketch, "E3177", {"start": v(-170.69, -250.4) * mm, "end": v(-170.5, -249.93) * mm});
            skLineSegment(sketch, "E3178", {"start": v(-170.5, -249.93) * mm, "end": v(-170.33, -249.45) * mm});
            skLineSegment(sketch, "E3179", {"start": v(-170.33, -249.45) * mm, "end": v(-170.16, -248.95) * mm});
            skLineSegment(sketch, "E3180", {"start": v(-170.16, -248.95) * mm, "end": v(-170, -248.44) * mm});
            skLineSegment(sketch, "E3181", {"start": v(-170, -248.44) * mm, "end": v(-169.83, -247.9) * mm});
            skLineSegment(sketch, "E3182", {"start": v(-169.83, -247.9) * mm, "end": v(-169.67, -247.35) * mm});
            skLineSegment(sketch, "E3183", {"start": v(-169.67, -247.35) * mm, "end": v(-169.35, -246.2) * mm});
            skLineSegment(sketch, "E3184", {"start": v(-169.35, -246.2) * mm, "end": v(-169.05, -244.98) * mm});
            skLineSegment(sketch, "E3185", {"start": v(-169.05, -244.98) * mm, "end": v(-168.75, -243.7) * mm});
            skLineSegment(sketch, "E3186", {"start": v(-168.75, -243.7) * mm, "end": v(-168.47, -242.33) * mm});
            skLineSegment(sketch, "E3187", {"start": v(-168.47, -242.33) * mm, "end": v(-168.2, -240.9) * mm});
            skLineSegment(sketch, "E3188", {"start": v(-168.2, -240.9) * mm, "end": v(-167.95, -239.4) * mm});
            skLineSegment(sketch, "E3189", {"start": v(-167.95, -239.4) * mm, "end": v(-167.7, -237.84) * mm});
            skLineSegment(sketch, "E3190", {"start": v(-167.7, -237.84) * mm, "end": v(-167.47, -236.2) * mm});
            skLineSegment(sketch, "E3191", {"start": v(-167.47, -236.2) * mm, "end": v(-167.25, -234.5) * mm});
            skLineSegment(sketch, "E3192", {"start": v(-167.25, -234.5) * mm, "end": v(-167.04, -232.73) * mm});
            skLineSegment(sketch, "E3193", {"start": v(-167.04, -232.73) * mm, "end": v(-166.85, -230.9) * mm});
            skLineSegment(sketch, "E3194", {"start": v(-166.85, -230.9) * mm, "end": v(-166.66, -228.98) * mm});
            skLineSegment(sketch, "E3195", {"start": v(-166.66, -228.98) * mm, "end": v(-166.49, -227) * mm});
            skLineSegment(sketch, "E3196", {"start": v(-166.49, -227) * mm, "end": v(-166.33, -224.96) * mm});
            skLineSegment(sketch, "E3197", {"start": v(-166.33, -224.96) * mm, "end": v(-166.18, -222.84) * mm});
            skLineSegment(sketch, "E3198", {"start": v(-166.18, -222.84) * mm, "end": v(-166.04, -220.66) * mm});
            skLineSegment(sketch, "E3199", {"start": v(-166.04, -220.66) * mm, "end": v(-165.92, -218.4) * mm});
            skLineSegment(sketch, "E3200", {"start": v(-165.92, -218.4) * mm, "end": v(-165.8, -216.08) * mm});
            skLineSegment(sketch, "E3201", {"start": v(-165.8, -216.08) * mm, "end": v(-165.7, -213.69) * mm});
            skLineSegment(sketch, "E3202", {"start": v(-165.7, -213.69) * mm, "end": v(-165.61, -211.23) * mm});
            skLineSegment(sketch, "E3203", {"start": v(-165.61, -211.23) * mm, "end": v(-165.54, -208.7) * mm});
            skLineSegment(sketch, "E3204", {"start": v(-165.54, -208.7) * mm, "end": v(-165.47, -206.1) * mm});
            skLineSegment(sketch, "E3205", {"start": v(-165.47, -206.1) * mm, "end": v(-165.42, -203.43) * mm});
            skLineSegment(sketch, "E3206", {"start": v(-165.42, -203.43) * mm, "end": v(-165.37, -200.7) * mm});
            skLineSegment(sketch, "E3207", {"start": v(-165.37, -200.7) * mm, "end": v(-165.34, -197.9) * mm});
            skLineSegment(sketch, "E3208", {"start": v(-165.34, -197.9) * mm, "end": v(-165.33, -195.02) * mm});
            skLineSegment(sketch, "E3209", {"start": v(-165.33, -195.02) * mm, "end": v(-165.32, -192.08) * mm});
            skLineSegment(sketch, "E3210", {"start": v(-165.32, -192.08) * mm, "end": v(-165.32, 192.08) * mm});
            skLineSegment(sketch, "E3211", {"start": v(-165.32, 192.08) * mm, "end": v(-165.33, 195.3) * mm});
            skLineSegment(sketch, "E3212", {"start": v(-165.33, 195.3) * mm, "end": v(-165.36, 198.48) * mm});
            skLineSegment(sketch, "E3213", {"start": v(-165.36, 198.48) * mm, "end": v(-165.4, 201.6) * mm});
            skLineSegment(sketch, "E3214", {"start": v(-165.4, 201.6) * mm, "end": v(-165.46, 204.66) * mm});
            skLineSegment(sketch, "E3215", {"start": v(-165.46, 204.66) * mm, "end": v(-165.54, 207.67) * mm});
            skLineSegment(sketch, "E3216", {"start": v(-165.54, 207.67) * mm, "end": v(-165.64, 210.62) * mm});
            skLineSegment(sketch, "E3217", {"start": v(-165.64, 210.62) * mm, "end": v(-165.76, 213.52) * mm});
            skLineSegment(sketch, "E3218", {"start": v(-165.76, 213.52) * mm, "end": v(-165.89, 216.37) * mm});
            skLineSegment(sketch, "E3219", {"start": v(-165.89, 216.37) * mm, "end": v(-166.04, 219.16) * mm});
            skLineSegment(sketch, "E3220", {"start": v(-166.04, 219.16) * mm, "end": v(-166.2, 221.9) * mm});
            skLineSegment(sketch, "E3221", {"start": v(-166.2, 221.9) * mm, "end": v(-166.4, 224.57) * mm});
            skLineSegment(sketch, "E3222", {"start": v(-166.4, 224.57) * mm, "end": v(-166.6, 227.2) * mm});
            skLineSegment(sketch, "E3223", {"start": v(-166.6, 227.2) * mm, "end": v(-166.82, 229.77) * mm});
            skLineSegment(sketch, "E3224", {"start": v(-166.82, 229.77) * mm, "end": v(-167.06, 232.29) * mm});
            skLineSegment(sketch, "E3225", {"start": v(-167.06, 232.29) * mm, "end": v(-167.32, 234.75) * mm});
            skLineSegment(sketch, "E3226", {"start": v(-167.32, 234.75) * mm, "end": v(-167.6, 237.16) * mm});
            skLineSegment(sketch, "E3227", {"start": v(-167.6, 237.16) * mm, "end": v(-167.88, 239.51) * mm});
            skLineSegment(sketch, "E3228", {"start": v(-167.88, 239.51) * mm, "end": v(-168.2, 241.8) * mm});
            skLineSegment(sketch, "E3229", {"start": v(-168.2, 241.8) * mm, "end": v(-168.52, 244.05) * mm});
            skLineSegment(sketch, "E3230", {"start": v(-168.52, 244.05) * mm, "end": v(-168.87, 246.24) * mm});
            skLineSegment(sketch, "E3231", {"start": v(-168.87, 246.24) * mm, "end": v(-169.23, 248.38) * mm});
            skLineSegment(sketch, "E3232", {"start": v(-169.23, 248.38) * mm, "end": v(-169.61, 250.46) * mm});
            skLineSegment(sketch, "E3233", {"start": v(-169.61, 250.46) * mm, "end": v(-170.01, 252.48) * mm});
            skLineSegment(sketch, "E3234", {"start": v(-170.01, 252.48) * mm, "end": v(-170.43, 254.45) * mm});
            skLineSegment(sketch, "E3235", {"start": v(-170.43, 254.45) * mm, "end": v(-170.87, 256.36) * mm});
            skLineSegment(sketch, "E3236", {"start": v(-170.87, 256.36) * mm, "end": v(-171.32, 258.23) * mm});
            skLineSegment(sketch, "E3237", {"start": v(-171.32, 258.23) * mm, "end": v(-171.55, 259.14) * mm});
            skLineSegment(sketch, "E3238", {"start": v(-171.55, 259.14) * mm, "end": v(-171.79, 260.03) * mm});
            skLineSegment(sketch, "E3239", {"start": v(-171.79, 260.03) * mm, "end": v(-172.03, 260.91) * mm});
            skLineSegment(sketch, "E3240", {"start": v(-172.03, 260.91) * mm, "end": v(-172.28, 261.78) * mm});
            skLineSegment(sketch, "E3241", {"start": v(-172.28, 261.78) * mm, "end": v(-172.53, 262.64) * mm});
            skLineSegment(sketch, "E3242", {"start": v(-172.53, 262.64) * mm, "end": v(-172.78, 263.48) * mm});
            skLineSegment(sketch, "E3243", {"start": v(-172.78, 263.48) * mm, "end": v(-173.04, 264.3) * mm});
            skLineSegment(sketch, "E3244", {"start": v(-173.04, 264.3) * mm, "end": v(-173.3, 265.12) * mm});
            skLineSegment(sketch, "E3245", {"start": v(-173.3, 265.12) * mm, "end": v(-173.57, 265.92) * mm});
            skLineSegment(sketch, "E3246", {"start": v(-173.57, 265.92) * mm, "end": v(-173.85, 266.7) * mm});
            skLineSegment(sketch, "E3247", {"start": v(-173.85, 266.7) * mm, "end": v(-174.12, 267.48) * mm});
            skLineSegment(sketch, "E3248", {"start": v(-174.12, 267.48) * mm, "end": v(-174.4, 268.24) * mm});
            skLineSegment(sketch, "E3249", {"start": v(-174.4, 268.24) * mm, "end": v(-174.99, 268.48) * mm});
            skLineSegment(sketch, "E3250", {"start": v(-174.99, 268.48) * mm, "end": v(-175.6, 268.71) * mm});
            skLineSegment(sketch, "E3251", {"start": v(-175.6, 268.71) * mm, "end": v(-176.22, 268.94) * mm});
            skLineSegment(sketch, "E3252", {"start": v(-176.22, 268.94) * mm, "end": v(-176.88, 269.16) * mm});
            skLineSegment(sketch, "E3253", {"start": v(-176.88, 269.16) * mm, "end": v(-177.56, 269.37) * mm});
            skLineSegment(sketch, "E3254", {"start": v(-177.56, 269.37) * mm, "end": v(-178.26, 269.57) * mm});
            skLineSegment(sketch, "E3255", {"start": v(-178.26, 269.57) * mm, "end": v(-179, 269.76) * mm});
            skLineSegment(sketch, "E3256", {"start": v(-179, 269.76) * mm, "end": v(-179.75, 269.95) * mm});
            skLineSegment(sketch, "E3257", {"start": v(-179.75, 269.95) * mm, "end": v(-180.53, 270.13) * mm});
            skLineSegment(sketch, "E3258", {"start": v(-180.53, 270.13) * mm, "end": v(-181.33, 270.3) * mm});
            skLineSegment(sketch, "E3259", {"start": v(-181.33, 270.3) * mm, "end": v(-182.17, 270.47) * mm});
            skLineSegment(sketch, "E3260", {"start": v(-182.17, 270.47) * mm, "end": v(-183.02, 270.62) * mm});
            skLineSegment(sketch, "E3261", {"start": v(-183.02, 270.62) * mm, "end": v(-183.9, 270.77) * mm});
            skLineSegment(sketch, "E3262", {"start": v(-183.9, 270.77) * mm, "end": v(-184.8, 270.91) * mm});
            skLineSegment(sketch, "E3263", {"start": v(-184.8, 270.91) * mm, "end": v(-185.74, 271.05) * mm});
            skLineSegment(sketch, "E3264", {"start": v(-185.74, 271.05) * mm, "end": v(-186.7, 271.17) * mm});
            skLineSegment(sketch, "E3265", {"start": v(-186.7, 271.17) * mm, "end": v(-187.68, 271.3) * mm});
            skLineSegment(sketch, "E3266", {"start": v(-187.68, 271.3) * mm, "end": v(-188.69, 271.4) * mm});
            skLineSegment(sketch, "E3267", {"start": v(-188.69, 271.4) * mm, "end": v(-189.72, 271.5) * mm});
            skLineSegment(sketch, "E3268", {"start": v(-189.72, 271.5) * mm, "end": v(-190.78, 271.6) * mm});
            skLineSegment(sketch, "E3269", {"start": v(-190.78, 271.6) * mm, "end": v(-191.86, 271.69) * mm});
            skLineSegment(sketch, "E3270", {"start": v(-191.86, 271.69) * mm, "end": v(-192.97, 271.77) * mm});
            skLineSegment(sketch, "E3271", {"start": v(-192.97, 271.77) * mm, "end": v(-194.1, 271.84) * mm});
            skLineSegment(sketch, "E3272", {"start": v(-194.1, 271.84) * mm, "end": v(-195.26, 271.9) * mm});
            skLineSegment(sketch, "E3273", {"start": v(-195.26, 271.9) * mm, "end": v(-196.44, 271.96) * mm});
            skLineSegment(sketch, "E3274", {"start": v(-196.44, 271.96) * mm, "end": v(-197.65, 272.01) * mm});
            skLineSegment(sketch, "E3275", {"start": v(-197.65, 272.01) * mm, "end": v(-198.88, 272.05) * mm});
            skLineSegment(sketch, "E3276", {"start": v(-198.88, 272.05) * mm, "end": v(-200.14, 272.09) * mm});
            skLineSegment(sketch, "E3277", {"start": v(-200.14, 272.09) * mm, "end": v(-201.42, 272.12) * mm});
            skLineSegment(sketch, "E3278", {"start": v(-201.42, 272.12) * mm, "end": v(-202.73, 272.13) * mm});
            skLineSegment(sketch, "E3279", {"start": v(-202.73, 272.13) * mm, "end": v(-204.07, 272.15) * mm});
            skLineSegment(sketch, "E3280", {"start": v(-204.07, 272.15) * mm, "end": v(-205.42, 272.15) * mm});
            skLineSegment(sketch, "E3281", {"start": v(-205.42, 272.15) * mm, "end": v(-228.6, 272.15) * mm});
            skLineSegment(sketch, "E3282", {"start": v(-228.6, 272.15) * mm, "end": v(-228.6, 306.62) * mm});
            skLineSegment(sketch, "E3283", {"start": v(-228.6, 306.62) * mm, "end": v(-42.7, 306.62) * mm});
            skLineSegment(sketch, "E3284", {"start": v(-42.7, 306.62) * mm, "end": v(-40.03, 306.61) * mm});
            skLineSegment(sketch, "E3285", {"start": v(-40.03, 306.61) * mm, "end": v(-37.37, 306.6) * mm});
            skLineSegment(sketch, "E3286", {"start": v(-37.37, 306.6) * mm, "end": v(-34.72, 306.57) * mm});
            skLineSegment(sketch, "E3287", {"start": v(-34.72, 306.57) * mm, "end": v(-32.1, 306.53) * mm});
            skLineSegment(sketch, "E3288", {"start": v(-32.1, 306.53) * mm, "end": v(-29.5, 306.48) * mm});
            skLineSegment(sketch, "E3289", {"start": v(-29.5, 306.48) * mm, "end": v(-26.9, 306.42) * mm});
            skLineSegment(sketch, "E3290", {"start": v(-26.9, 306.42) * mm, "end": v(-24.34, 306.35) * mm});
            skLineSegment(sketch, "E3291", {"start": v(-24.34, 306.35) * mm, "end": v(-21.79, 306.27) * mm});
            skLineSegment(sketch, "E3292", {"start": v(-21.79, 306.27) * mm, "end": v(-19.26, 306.18) * mm});
            skLineSegment(sketch, "E3293", {"start": v(-19.26, 306.18) * mm, "end": v(-16.74, 306.08) * mm});
            skLineSegment(sketch, "E3294", {"start": v(-16.74, 306.08) * mm, "end": v(-14.25, 305.96) * mm});
            skLineSegment(sketch, "E3295", {"start": v(-14.25, 305.96) * mm, "end": v(-11.77, 305.84) * mm});
            skLineSegment(sketch, "E3296", {"start": v(-11.77, 305.84) * mm, "end": v(-9.31, 305.7) * mm});
            skLineSegment(sketch, "E3297", {"start": v(-9.31, 305.7) * mm, "end": v(-6.87, 305.56) * mm});
            skLineSegment(sketch, "E3298", {"start": v(-6.87, 305.56) * mm, "end": v(-4.45, 305.4) * mm});
            skLineSegment(sketch, "E3299", {"start": v(-4.45, 305.4) * mm, "end": v(-2.05, 305.24) * mm});
            skLineSegment(sketch, "E3300", {"start": v(-2.05, 305.24) * mm, "end": v(0.34, 305.06) * mm});
            skLineSegment(sketch, "E3301", {"start": v(0.34, 305.06) * mm, "end": v(2.7, 304.87) * mm});
            skLineSegment(sketch, "E3302", {"start": v(2.7, 304.87) * mm, "end": v(5.05, 304.67) * mm});
            skLineSegment(sketch, "E3303", {"start": v(5.05, 304.67) * mm, "end": v(7.38, 304.46) * mm});
            skLineSegment(sketch, "E3304", {"start": v(7.38, 304.46) * mm, "end": v(9.69, 304.24) * mm});
            skLineSegment(sketch, "E3305", {"start": v(9.69, 304.24) * mm, "end": v(11.98, 304) * mm});
            skLineSegment(sketch, "E3306", {"start": v(11.98, 304) * mm, "end": v(14.26, 303.77) * mm});
            skLineSegment(sketch, "E3307", {"start": v(14.26, 303.77) * mm, "end": v(16.51, 303.51) * mm});
            skLineSegment(sketch, "E3308", {"start": v(16.51, 303.51) * mm, "end": v(18.75, 303.25) * mm});
            skLineSegment(sketch, "E3309", {"start": v(18.75, 303.25) * mm, "end": v(20.97, 302.97) * mm});
            skLineSegment(sketch, "E3310", {"start": v(20.97, 302.97) * mm, "end": v(23.17, 302.69) * mm});
            skLineSegment(sketch, "E3311", {"start": v(23.17, 302.69) * mm, "end": v(25.35, 302.4) * mm});
            skLineSegment(sketch, "E3312", {"start": v(25.35, 302.4) * mm, "end": v(27.51, 302.08) * mm});
            skLineSegment(sketch, "E3313", {"start": v(27.51, 302.08) * mm, "end": v(29.66, 301.77) * mm});
            skLineSegment(sketch, "E3314", {"start": v(29.66, 301.77) * mm, "end": v(31.79, 301.44) * mm});
            skLineSegment(sketch, "E3315", {"start": v(31.79, 301.44) * mm, "end": v(33.9, 301.1) * mm});
            skLineSegment(sketch, "E3316", {"start": v(33.9, 301.1) * mm, "end": v(35.99, 300.75) * mm});
            skLineSegment(sketch, "E3317", {"start": v(35.99, 300.75) * mm, "end": v(38.06, 300.39) * mm});
            skLineSegment(sketch, "E3318", {"start": v(38.06, 300.39) * mm, "end": v(40.11, 300.01) * mm});
            skLineSegment(sketch, "E3319", {"start": v(40.11, 300.01) * mm, "end": v(42.14, 299.63) * mm});
            skLineSegment(sketch, "E3320", {"start": v(42.14, 299.63) * mm, "end": v(44.16, 299.24) * mm});
            skLineSegment(sketch, "E3321", {"start": v(44.16, 299.24) * mm, "end": v(46.16, 298.83) * mm});
            skLineSegment(sketch, "E3322", {"start": v(46.16, 298.83) * mm, "end": v(48.14, 298.42) * mm});
            skLineSegment(sketch, "E3323", {"start": v(48.14, 298.42) * mm, "end": v(50.1, 298) * mm});
            skLineSegment(sketch, "E3324", {"start": v(50.1, 298) * mm, "end": v(52.04, 297.56) * mm});
            skLineSegment(sketch, "E3325", {"start": v(52.04, 297.56) * mm, "end": v(53.97, 297.1) * mm});
            skLineSegment(sketch, "E3326", {"start": v(53.97, 297.1) * mm, "end": v(55.87, 296.65) * mm});
            skLineSegment(sketch, "E3327", {"start": v(55.87, 296.65) * mm, "end": v(57.76, 296.18) * mm});
            skLineSegment(sketch, "E3328", {"start": v(57.76, 296.18) * mm, "end": v(59.63, 295.7) * mm});
            skLineSegment(sketch, "E3329", {"start": v(59.63, 295.7) * mm, "end": v(61.48, 295.21) * mm});
            skLineSegment(sketch, "E3330", {"start": v(61.48, 295.21) * mm, "end": v(63.31, 294.71) * mm});
            skLineSegment(sketch, "E3331", {"start": v(63.31, 294.71) * mm, "end": v(65.13, 294.2) * mm});
            skLineSegment(sketch, "E3332", {"start": v(65.13, 294.2) * mm, "end": v(66.92, 293.68) * mm});
            skLineSegment(sketch, "E3333", {"start": v(66.92, 293.68) * mm, "end": v(68.7, 293.14) * mm});
            skLineSegment(sketch, "E3334", {"start": v(68.7, 293.14) * mm, "end": v(70.46, 292.6) * mm});
            skLineSegment(sketch, "E3335", {"start": v(70.46, 292.6) * mm, "end": v(72.2, 292.04) * mm});
            skLineSegment(sketch, "E3336", {"start": v(72.2, 292.04) * mm, "end": v(73.92, 291.48) * mm});
            skLineSegment(sketch, "E3337", {"start": v(73.92, 291.48) * mm, "end": v(75.62, 290.9) * mm});
            skLineSegment(sketch, "E3338", {"start": v(75.62, 290.9) * mm, "end": v(77.3, 290.31) * mm});
            skLineSegment(sketch, "E3339", {"start": v(77.3, 290.31) * mm, "end": v(78.97, 289.72) * mm});
            skLineSegment(sketch, "E3340", {"start": v(78.97, 289.72) * mm, "end": v(80.62, 289.1) * mm});
            skLineSegment(sketch, "E3341", {"start": v(80.62, 289.1) * mm, "end": v(82.25, 288.49) * mm});
            skLineSegment(sketch, "E3342", {"start": v(82.25, 288.49) * mm, "end": v(83.86, 287.86) * mm});
            skLineSegment(sketch, "E3343", {"start": v(83.86, 287.86) * mm, "end": v(85.45, 287.22) * mm});
            skLineSegment(sketch, "E3344", {"start": v(85.45, 287.22) * mm, "end": v(87.03, 286.56) * mm});
            skLineSegment(sketch, "E3345", {"start": v(87.03, 286.56) * mm, "end": v(88.59, 285.9) * mm});
            skLineSegment(sketch, "E3346", {"start": v(88.59, 285.9) * mm, "end": v(90.12, 285.23) * mm});
            skLineSegment(sketch, "E3347", {"start": v(90.12, 285.23) * mm, "end": v(91.64, 284.54) * mm});
            skLineSegment(sketch, "E3348", {"start": v(91.64, 284.54) * mm, "end": v(93.75, 283.58) * mm});
            skLineSegment(sketch, "E3349", {"start": v(93.75, 283.58) * mm, "end": v(95.84, 282.58) * mm});
            skLineSegment(sketch, "E3350", {"start": v(95.84, 282.58) * mm, "end": v(97.92, 281.57) * mm});
            skLineSegment(sketch, "E3351", {"start": v(97.92, 281.57) * mm, "end": v(99.99, 280.52) * mm});
            skLineSegment(sketch, "E3352", {"start": v(99.99, 280.52) * mm, "end": v(102.04, 279.45) * mm});
            skLineSegment(sketch, "E3353", {"start": v(102.04, 279.45) * mm, "end": v(104.07, 278.36) * mm});
            skLineSegment(sketch, "E3354", {"start": v(104.07, 278.36) * mm, "end": v(106.09, 277.24) * mm});
            skLineSegment(sketch, "E3355", {"start": v(106.09, 277.24) * mm, "end": v(108.1, 276.1) * mm});
            skLineSegment(sketch, "E3356", {"start": v(108.1, 276.1) * mm, "end": v(110.08, 274.92) * mm});
            skLineSegment(sketch, "E3357", {"start": v(110.08, 274.92) * mm, "end": v(112.05, 273.72) * mm});
            skLineSegment(sketch, "E3358", {"start": v(112.05, 273.72) * mm, "end": v(114.01, 272.5) * mm});
            skLineSegment(sketch, "E3359", {"start": v(114.01, 272.5) * mm, "end": v(115.96, 271.25) * mm});
            skLineSegment(sketch, "E3360", {"start": v(115.96, 271.25) * mm, "end": v(117.88, 269.97) * mm});
            skLineSegment(sketch, "E3361", {"start": v(117.88, 269.97) * mm, "end": v(119.8, 268.67) * mm});
            skLineSegment(sketch, "E3362", {"start": v(119.8, 268.67) * mm, "end": v(121.7, 267.35) * mm});
            skLineSegment(sketch, "E3363", {"start": v(121.7, 267.35) * mm, "end": v(123.58, 266) * mm});
            skLineSegment(sketch, "E3364", {"start": v(123.58, 266) * mm, "end": v(125.45, 264.62) * mm});
            skLineSegment(sketch, "E3365", {"start": v(125.45, 264.62) * mm, "end": v(127.3, 263.21) * mm});
            skLineSegment(sketch, "E3366", {"start": v(127.3, 263.21) * mm, "end": v(129.14, 261.79) * mm});
            skLineSegment(sketch, "E3367", {"start": v(129.14, 261.79) * mm, "end": v(130.96, 260.33) * mm});
            skLineSegment(sketch, "E3368", {"start": v(130.96, 260.33) * mm, "end": v(132.77, 258.85) * mm});
            skLineSegment(sketch, "E3369", {"start": v(132.77, 258.85) * mm, "end": v(134.57, 257.34) * mm});
            skLineSegment(sketch, "E3370", {"start": v(134.57, 257.34) * mm, "end": v(136.34, 255.81) * mm});
            skLineSegment(sketch, "E3371", {"start": v(136.34, 255.81) * mm, "end": v(138.1, 254.25) * mm});
            skLineSegment(sketch, "E3372", {"start": v(138.1, 254.25) * mm, "end": v(139.86, 252.67) * mm});
            skLineSegment(sketch, "E3373", {"start": v(139.86, 252.67) * mm, "end": v(141.6, 251.06) * mm});
            skLineSegment(sketch, "E3374", {"start": v(141.6, 251.06) * mm, "end": v(143.3, 249.43) * mm});
            skLineSegment(sketch, "E3375", {"start": v(143.3, 249.43) * mm, "end": v(145.01, 247.77) * mm});
            skLineSegment(sketch, "E3376", {"start": v(145.01, 247.77) * mm, "end": v(146.7, 246.08) * mm});
            skLineSegment(sketch, "E3377", {"start": v(146.7, 246.08) * mm, "end": v(148.37, 244.37) * mm});
            skLineSegment(sketch, "E3378", {"start": v(148.37, 244.37) * mm, "end": v(150.03, 242.63) * mm});
            skLineSegment(sketch, "E3379", {"start": v(150.03, 242.63) * mm, "end": v(151.68, 240.87) * mm});
            skLineSegment(sketch, "E3380", {"start": v(151.68, 240.87) * mm, "end": v(153.3, 239.08) * mm});
            skLineSegment(sketch, "E3381", {"start": v(153.3, 239.08) * mm, "end": v(154.92, 237.26) * mm});
            skLineSegment(sketch, "E3382", {"start": v(154.92, 237.26) * mm, "end": v(156.52, 235.42) * mm});
            skLineSegment(sketch, "E3383", {"start": v(156.52, 235.42) * mm, "end": v(158.1, 233.56) * mm});
            skLineSegment(sketch, "E3384", {"start": v(158.1, 233.56) * mm, "end": v(159.67, 231.67) * mm});
            skLineSegment(sketch, "E3385", {"start": v(159.67, 231.67) * mm, "end": v(161.22, 229.75) * mm});
            skLineSegment(sketch, "E3386", {"start": v(161.22, 229.75) * mm, "end": v(162.76, 227.8) * mm});
            skLineSegment(sketch, "E3387", {"start": v(162.76, 227.8) * mm, "end": v(164.28, 225.84) * mm});
            skLineSegment(sketch, "E3388", {"start": v(164.28, 225.84) * mm, "end": v(165.79, 223.84) * mm});
            skLineSegment(sketch, "E3389", {"start": v(165.79, 223.84) * mm, "end": v(167.28, 221.82) * mm});
            skLineSegment(sketch, "E3390", {"start": v(167.28, 221.82) * mm, "end": v(168.76, 219.77) * mm});
            skLineSegment(sketch, "E3391", {"start": v(168.76, 219.77) * mm, "end": v(170.22, 217.7) * mm});
            skLineSegment(sketch, "E3392", {"start": v(170.22, 217.7) * mm, "end": v(171.67, 215.6) * mm});
            skLineSegment(sketch, "E3393", {"start": v(171.67, 215.6) * mm, "end": v(173.1, 213.48) * mm});
            skLineSegment(sketch, "E3394", {"start": v(173.1, 213.48) * mm, "end": v(174.52, 211.33) * mm});
            skLineSegment(sketch, "E3395", {"start": v(174.52, 211.33) * mm, "end": v(175.93, 209.16) * mm});
            skLineSegment(sketch, "E3396", {"start": v(175.93, 209.16) * mm, "end": v(177.31, 206.96) * mm});
            skLineSegment(sketch, "E3397", {"start": v(177.31, 206.96) * mm, "end": v(178.69, 204.73) * mm});
            skLineSegment(sketch, "E3398", {"start": v(178.69, 204.73) * mm, "end": v(180.05, 202.48) * mm});
            skLineSegment(sketch, "E3399", {"start": v(180.05, 202.48) * mm, "end": v(181.39, 200.2) * mm});
            skLineSegment(sketch, "E3400", {"start": v(181.39, 200.2) * mm, "end": v(182.72, 197.9) * mm});
            skLineSegment(sketch, "E3401", {"start": v(182.72, 197.9) * mm, "end": v(184.03, 195.57) * mm});
            skLineSegment(sketch, "E3402", {"start": v(184.03, 195.57) * mm, "end": v(185.33, 193.22) * mm});
            skLineSegment(sketch, "E3403", {"start": v(185.33, 193.22) * mm, "end": v(186.61, 190.84) * mm});
            skLineSegment(sketch, "E3404", {"start": v(186.61, 190.84) * mm, "end": v(187.88, 188.43) * mm});
            skLineSegment(sketch, "E3405", {"start": v(187.88, 188.43) * mm, "end": v(189.13, 186) * mm});
            skLineSegment(sketch, "E3406", {"start": v(189.13, 186) * mm, "end": v(190.37, 183.54) * mm});
            skLineSegment(sketch, "E3407", {"start": v(190.37, 183.54) * mm, "end": v(191.6, 181.06) * mm});
            skLineSegment(sketch, "E3408", {"start": v(191.6, 181.06) * mm, "end": v(192.8, 178.55) * mm});
            skLineSegment(sketch, "E3409", {"start": v(192.8, 178.55) * mm, "end": v(194, 176.02) * mm});
            skLineSegment(sketch, "E3410", {"start": v(194, 176.02) * mm, "end": v(195.17, 173.46) * mm});
            skLineSegment(sketch, "E3411", {"start": v(195.17, 173.46) * mm, "end": v(196.33, 170.87) * mm});
            skLineSegment(sketch, "E3412", {"start": v(196.33, 170.87) * mm, "end": v(197.33, 168.58) * mm});
            skLineSegment(sketch, "E3413", {"start": v(197.33, 168.58) * mm, "end": v(198.32, 166.28) * mm});
            skLineSegment(sketch, "E3414", {"start": v(198.32, 166.28) * mm, "end": v(199.29, 163.96) * mm});
            skLineSegment(sketch, "E3415", {"start": v(199.29, 163.96) * mm, "end": v(200.24, 161.64) * mm});
            skLineSegment(sketch, "E3416", {"start": v(200.24, 161.64) * mm, "end": v(201.18, 159.3) * mm});
            skLineSegment(sketch, "E3417", {"start": v(201.18, 159.3) * mm, "end": v(202.1, 156.96) * mm});
            skLineSegment(sketch, "E3418", {"start": v(202.1, 156.96) * mm, "end": v(203, 154.6) * mm});
            skLineSegment(sketch, "E3419", {"start": v(203, 154.6) * mm, "end": v(203.9, 152.24) * mm});
            skLineSegment(sketch, "E3420", {"start": v(203.9, 152.24) * mm, "end": v(204.77, 149.87) * mm});
            skLineSegment(sketch, "E3421", {"start": v(204.77, 149.87) * mm, "end": v(205.63, 147.48) * mm});
            skLineSegment(sketch, "E3422", {"start": v(205.63, 147.48) * mm, "end": v(206.47, 145.09) * mm});
            skLineSegment(sketch, "E3423", {"start": v(206.47, 145.09) * mm, "end": v(207.3, 142.68) * mm});
            skLineSegment(sketch, "E3424", {"start": v(207.3, 142.68) * mm, "end": v(208.11, 140.26) * mm});
            skLineSegment(sketch, "E3425", {"start": v(208.11, 140.26) * mm, "end": v(208.9, 137.84) * mm});
            skLineSegment(sketch, "E3426", {"start": v(208.9, 137.84) * mm, "end": v(209.69, 135.4) * mm});
            skLineSegment(sketch, "E3427", {"start": v(209.69, 135.4) * mm, "end": v(210.45, 132.95) * mm});
            skLineSegment(sketch, "E3428", {"start": v(210.45, 132.95) * mm, "end": v(211.2, 130.49) * mm});
            skLineSegment(sketch, "E3429", {"start": v(211.2, 130.49) * mm, "end": v(211.93, 128.02) * mm});
            skLineSegment(sketch, "E3430", {"start": v(211.93, 128.02) * mm, "end": v(212.65, 125.54) * mm});
            skLineSegment(sketch, "E3431", {"start": v(212.65, 125.54) * mm, "end": v(213.35, 123.05) * mm});
            skLineSegment(sketch, "E3432", {"start": v(213.35, 123.05) * mm, "end": v(214.03, 120.55) * mm});
            skLineSegment(sketch, "E3433", {"start": v(214.03, 120.55) * mm, "end": v(214.7, 118.04) * mm});
            skLineSegment(sketch, "E3434", {"start": v(214.7, 118.04) * mm, "end": v(215.36, 115.51) * mm});
            skLineSegment(sketch, "E3435", {"start": v(215.36, 115.51) * mm, "end": v(216, 112.98) * mm});
            skLineSegment(sketch, "E3436", {"start": v(216, 112.98) * mm, "end": v(216.62, 110.44) * mm});
            skLineSegment(sketch, "E3437", {"start": v(216.62, 110.44) * mm, "end": v(217.22, 107.88) * mm});
            skLineSegment(sketch, "E3438", {"start": v(217.22, 107.88) * mm, "end": v(217.82, 105.32) * mm});
            skLineSegment(sketch, "E3439", {"start": v(217.82, 105.32) * mm, "end": v(218.4, 102.75) * mm});
            skLineSegment(sketch, "E3440", {"start": v(218.4, 102.75) * mm, "end": v(218.95, 100.16) * mm});
            skLineSegment(sketch, "E3441", {"start": v(218.95, 100.16) * mm, "end": v(219.5, 97.56) * mm});
            skLineSegment(sketch, "E3442", {"start": v(219.5, 97.56) * mm, "end": v(220.02, 94.96) * mm});
            skLineSegment(sketch, "E3443", {"start": v(220.02, 94.96) * mm, "end": v(220.53, 92.34) * mm});
            skLineSegment(sketch, "E3444", {"start": v(220.53, 92.34) * mm, "end": v(221.03, 89.71) * mm});
            skLineSegment(sketch, "E3445", {"start": v(221.03, 89.71) * mm, "end": v(221.51, 87.08) * mm});
            skLineSegment(sketch, "E3446", {"start": v(221.51, 87.08) * mm, "end": v(221.98, 84.43) * mm});
            skLineSegment(sketch, "E3447", {"start": v(221.98, 84.43) * mm, "end": v(222.42, 81.77) * mm});
            skLineSegment(sketch, "E3448", {"start": v(222.42, 81.77) * mm, "end": v(222.86, 79.1) * mm});
            skLineSegment(sketch, "E3449", {"start": v(222.86, 79.1) * mm, "end": v(223.27, 76.42) * mm});
            skLineSegment(sketch, "E3450", {"start": v(223.27, 76.42) * mm, "end": v(223.68, 73.73) * mm});
            skLineSegment(sketch, "E3451", {"start": v(223.68, 73.73) * mm, "end": v(224.06, 71.03) * mm});
            skLineSegment(sketch, "E3452", {"start": v(224.06, 71.03) * mm, "end": v(224.43, 68.32) * mm});
            skLineSegment(sketch, "E3453", {"start": v(224.43, 68.32) * mm, "end": v(224.79, 65.6) * mm});
            skLineSegment(sketch, "E3454", {"start": v(224.79, 65.6) * mm, "end": v(225.13, 62.87) * mm});
            skLineSegment(sketch, "E3455", {"start": v(225.13, 62.87) * mm, "end": v(225.45, 60.12) * mm});
            skLineSegment(sketch, "E3456", {"start": v(225.45, 60.12) * mm, "end": v(225.76, 57.37) * mm});
            skLineSegment(sketch, "E3457", {"start": v(225.76, 57.37) * mm, "end": v(226.05, 54.6) * mm});
            skLineSegment(sketch, "E3458", {"start": v(226.05, 54.6) * mm, "end": v(226.32, 51.83) * mm});
            skLineSegment(sketch, "E3459", {"start": v(226.32, 51.83) * mm, "end": v(226.58, 49.05) * mm});
            skLineSegment(sketch, "E3460", {"start": v(226.58, 49.05) * mm, "end": v(226.83, 46.25) * mm});
            skLineSegment(sketch, "E3461", {"start": v(226.83, 46.25) * mm, "end": v(227.06, 43.45) * mm});
            skLineSegment(sketch, "E3462", {"start": v(227.06, 43.45) * mm, "end": v(227.27, 40.63) * mm});
            skLineSegment(sketch, "E3463", {"start": v(227.27, 40.63) * mm, "end": v(227.47, 37.8) * mm});
            skLineSegment(sketch, "E3464", {"start": v(227.47, 37.8) * mm, "end": v(227.65, 34.97) * mm});
            skLineSegment(sketch, "E3465", {"start": v(227.65, 34.97) * mm, "end": v(227.81, 32.12) * mm});
            skLineSegment(sketch, "E3466", {"start": v(227.81, 32.12) * mm, "end": v(227.96, 29.26) * mm});
            skLineSegment(sketch, "E3467", {"start": v(227.96, 29.26) * mm, "end": v(228.1, 26.4) * mm});
            skLineSegment(sketch, "E3468", {"start": v(228.1, 26.4) * mm, "end": v(228.21, 23.52) * mm});
            skLineSegment(sketch, "E3469", {"start": v(228.21, 23.52) * mm, "end": v(228.32, 20.63) * mm});
            skLineSegment(sketch, "E3470", {"start": v(228.32, 20.63) * mm, "end": v(228.4, 17.73) * mm});
            skLineSegment(sketch, "E3471", {"start": v(228.4, 17.73) * mm, "end": v(228.47, 14.82) * mm});
            skLineSegment(sketch, "E3472", {"start": v(228.47, 14.82) * mm, "end": v(228.53, 11.9) * mm});
            skLineSegment(sketch, "E3473", {"start": v(228.53, 11.9) * mm, "end": v(228.57, 8.96) * mm});
            skLineSegment(sketch, "E3474", {"start": v(228.57, 8.96) * mm, "end": v(228.6, 6.02) * mm});
            skLineSegment(sketch, "E3475", {"start": v(228.6, 6.02) * mm, "end": v(228.6, 3.07) * mm});
            skLineSegment(sketch, "E3476", {"start": v(141.14, -1.12) * mm, "end": v(141.12, 2.37) * mm});
            skLineSegment(sketch, "E3477", {"start": v(141.12, 2.37) * mm, "end": v(141.1, 5.85) * mm});
            skLineSegment(sketch, "E3478", {"start": v(141.1, 5.85) * mm, "end": v(141.04, 9.32) * mm});
            skLineSegment(sketch, "E3479", {"start": v(141.04, 9.32) * mm, "end": v(140.96, 12.77) * mm});
            skLineSegment(sketch, "E3480", {"start": v(140.96, 12.77) * mm, "end": v(140.86, 16.21) * mm});
            skLineSegment(sketch, "E3481", {"start": v(140.86, 16.21) * mm, "end": v(140.74, 19.64) * mm});
            skLineSegment(sketch, "E3482", {"start": v(140.74, 19.64) * mm, "end": v(140.6, 23.05) * mm});
            skLineSegment(sketch, "E3483", {"start": v(140.6, 23.05) * mm, "end": v(140.43, 26.45) * mm});
            skLineSegment(sketch, "E3484", {"start": v(140.43, 26.45) * mm, "end": v(140.24, 29.84) * mm});
            skLineSegment(sketch, "E3485", {"start": v(140.24, 29.84) * mm, "end": v(140.03, 33.22) * mm});
            skLineSegment(sketch, "E3486", {"start": v(140.03, 33.22) * mm, "end": v(139.8, 36.58) * mm});
            skLineSegment(sketch, "E3487", {"start": v(139.8, 36.58) * mm, "end": v(139.55, 39.93) * mm});
            skLineSegment(sketch, "E3488", {"start": v(139.55, 39.93) * mm, "end": v(139.27, 43.26) * mm});
            skLineSegment(sketch, "E3489", {"start": v(139.27, 43.26) * mm, "end": v(138.97, 46.59) * mm});
            skLineSegment(sketch, "E3490", {"start": v(138.97, 46.59) * mm, "end": v(138.65, 49.9) * mm});
            skLineSegment(sketch, "E3491", {"start": v(138.65, 49.9) * mm, "end": v(138.31, 53.2) * mm});
            skLineSegment(sketch, "E3492", {"start": v(138.31, 53.2) * mm, "end": v(137.95, 56.48) * mm});
            skLineSegment(sketch, "E3493", {"start": v(137.95, 56.48) * mm, "end": v(137.56, 59.75) * mm});
            skLineSegment(sketch, "E3494", {"start": v(137.56, 59.75) * mm, "end": v(137.15, 63) * mm});
            skLineSegment(sketch, "E3495", {"start": v(137.15, 63) * mm, "end": v(136.72, 66.25) * mm});
            skLineSegment(sketch, "E3496", {"start": v(136.72, 66.25) * mm, "end": v(136.27, 69.49) * mm});
            skLineSegment(sketch, "E3497", {"start": v(136.27, 69.49) * mm, "end": v(135.8, 72.7) * mm});
            skLineSegment(sketch, "E3498", {"start": v(135.8, 72.7) * mm, "end": v(135.3, 75.91) * mm});
            skLineSegment(sketch, "E3499", {"start": v(135.3, 75.91) * mm, "end": v(134.78, 79.1) * mm});
            skLineSegment(sketch, "E3500", {"start": v(134.78, 79.1) * mm, "end": v(134.24, 82.29) * mm});
            skLineSegment(sketch, "E3501", {"start": v(134.24, 82.29) * mm, "end": v(133.68, 85.45) * mm});
            skLineSegment(sketch, "E3502", {"start": v(133.68, 85.45) * mm, "end": v(133.1, 88.6) * mm});
            skLineSegment(sketch, "E3503", {"start": v(133.1, 88.6) * mm, "end": v(132.49, 91.75) * mm});
            skLineSegment(sketch, "E3504", {"start": v(132.49, 91.75) * mm, "end": v(131.86, 94.88) * mm});
            skLineSegment(sketch, "E3505", {"start": v(131.86, 94.88) * mm, "end": v(131.2, 98) * mm});
            skLineSegment(sketch, "E3506", {"start": v(131.2, 98) * mm, "end": v(130.53, 101.1) * mm});
            skLineSegment(sketch, "E3507", {"start": v(130.53, 101.1) * mm, "end": v(129.84, 104.19) * mm});
            skLineSegment(sketch, "E3508", {"start": v(129.84, 104.19) * mm, "end": v(129.12, 107.26) * mm});
            skLineSegment(sketch, "E3509", {"start": v(129.12, 107.26) * mm, "end": v(128.38, 110.33) * mm});
            skLineSegment(sketch, "E3510", {"start": v(128.38, 110.33) * mm, "end": v(127.62, 113.38) * mm});
            skLineSegment(sketch, "E3511", {"start": v(127.62, 113.38) * mm, "end": v(126.84, 116.42) * mm});
            skLineSegment(sketch, "E3512", {"start": v(126.84, 116.42) * mm, "end": v(126.03, 119.44) * mm});
            skLineSegment(sketch, "E3513", {"start": v(126.03, 119.44) * mm, "end": v(125.2, 122.45) * mm});
            skLineSegment(sketch, "E3514", {"start": v(125.2, 122.45) * mm, "end": v(124.35, 125.45) * mm});
            skLineSegment(sketch, "E3515", {"start": v(124.35, 125.45) * mm, "end": v(123.48, 128.44) * mm});
            skLineSegment(sketch, "E3516", {"start": v(123.48, 128.44) * mm, "end": v(122.59, 131.4) * mm});
            skLineSegment(sketch, "E3517", {"start": v(122.59, 131.4) * mm, "end": v(121.67, 134.37) * mm});
            skLineSegment(sketch, "E3518", {"start": v(121.67, 134.37) * mm, "end": v(120.74, 137.32) * mm});
            skLineSegment(sketch, "E3519", {"start": v(120.74, 137.32) * mm, "end": v(119.78, 140.25) * mm});
            skLineSegment(sketch, "E3520", {"start": v(119.78, 140.25) * mm, "end": v(118.8, 143.17) * mm});
            skLineSegment(sketch, "E3521", {"start": v(118.8, 143.17) * mm, "end": v(117.79, 146.08) * mm});
            skLineSegment(sketch, "E3522", {"start": v(117.79, 146.08) * mm, "end": v(116.76, 148.98) * mm});
            skLineSegment(sketch, "E3523", {"start": v(116.76, 148.98) * mm, "end": v(115.72, 151.86) * mm});
            skLineSegment(sketch, "E3524", {"start": v(115.72, 151.86) * mm, "end": v(114.64, 154.73) * mm});
            skLineSegment(sketch, "E3525", {"start": v(114.64, 154.73) * mm, "end": v(113.55, 157.58) * mm});
            skLineSegment(sketch, "E3526", {"start": v(113.55, 157.58) * mm, "end": v(112.44, 160.43) * mm});
            skLineSegment(sketch, "E3527", {"start": v(112.44, 160.43) * mm, "end": v(111.3, 163.26) * mm});
            skLineSegment(sketch, "E3528", {"start": v(111.3, 163.26) * mm, "end": v(110.14, 166.07) * mm});
            skLineSegment(sketch, "E3529", {"start": v(110.14, 166.07) * mm, "end": v(108.96, 168.88) * mm});
            skLineSegment(sketch, "E3530", {"start": v(108.96, 168.88) * mm, "end": v(107.76, 171.67) * mm});
            skLineSegment(sketch, "E3531", {"start": v(107.76, 171.67) * mm, "end": v(106.54, 174.45) * mm});
            skLineSegment(sketch, "E3532", {"start": v(106.54, 174.45) * mm, "end": v(105.29, 177.21) * mm});
            skLineSegment(sketch, "E3533", {"start": v(105.29, 177.21) * mm, "end": v(104.02, 179.97) * mm});
            skLineSegment(sketch, "E3534", {"start": v(104.02, 179.97) * mm, "end": v(102.73, 182.7) * mm});
            skLineSegment(sketch, "E3535", {"start": v(102.73, 182.7) * mm, "end": v(101.42, 185.43) * mm});
            skLineSegment(sketch, "E3536", {"start": v(101.42, 185.43) * mm, "end": v(100.08, 188.15) * mm});
            skLineSegment(sketch, "E3537", {"start": v(100.08, 188.15) * mm, "end": v(98.72, 190.85) * mm});
            skLineSegment(sketch, "E3538", {"start": v(98.72, 190.85) * mm, "end": v(97.34, 193.53) * mm});
            skLineSegment(sketch, "E3539", {"start": v(97.34, 193.53) * mm, "end": v(95.94, 196.2) * mm});
            skLineSegment(sketch, "E3540", {"start": v(95.94, 196.2) * mm, "end": v(95.24, 197.13) * mm});
            skLineSegment(sketch, "E3541", {"start": v(95.24, 197.13) * mm, "end": v(94.53, 198.05) * mm});
            skLineSegment(sketch, "E3542", {"start": v(94.53, 198.05) * mm, "end": v(93.82, 198.96) * mm});
            skLineSegment(sketch, "E3543", {"start": v(93.82, 198.96) * mm, "end": v(93.1, 199.86) * mm});
            skLineSegment(sketch, "E3544", {"start": v(93.1, 199.86) * mm, "end": v(92.38, 200.76) * mm});
            skLineSegment(sketch, "E3545", {"start": v(92.38, 200.76) * mm, "end": v(91.65, 201.65) * mm});
            skLineSegment(sketch, "E3546", {"start": v(91.65, 201.65) * mm, "end": v(90.92, 202.53) * mm});
            skLineSegment(sketch, "E3547", {"start": v(90.92, 202.53) * mm, "end": v(90.18, 203.4) * mm});
            skLineSegment(sketch, "E3548", {"start": v(90.18, 203.4) * mm, "end": v(89.44, 204.27) * mm});
            skLineSegment(sketch, "E3549", {"start": v(89.44, 204.27) * mm, "end": v(88.7, 205.12) * mm});
            skLineSegment(sketch, "E3550", {"start": v(88.7, 205.12) * mm, "end": v(87.95, 205.98) * mm});
            skLineSegment(sketch, "E3551", {"start": v(87.95, 205.98) * mm, "end": v(87.2, 206.82) * mm});
            skLineSegment(sketch, "E3552", {"start": v(87.2, 206.82) * mm, "end": v(86.44, 207.66) * mm});
            skLineSegment(sketch, "E3553", {"start": v(86.44, 207.66) * mm, "end": v(85.68, 208.49) * mm});
            skLineSegment(sketch, "E3554", {"start": v(85.68, 208.49) * mm, "end": v(84.91, 209.31) * mm});
            skLineSegment(sketch, "E3555", {"start": v(84.91, 209.31) * mm, "end": v(84.14, 210.13) * mm});
            skLineSegment(sketch, "E3556", {"start": v(84.14, 210.13) * mm, "end": v(83.37, 210.93) * mm});
            skLineSegment(sketch, "E3557", {"start": v(83.37, 210.93) * mm, "end": v(82.6, 211.74) * mm});
            skLineSegment(sketch, "E3558", {"start": v(82.6, 211.74) * mm, "end": v(81.8, 212.53) * mm});
            skLineSegment(sketch, "E3559", {"start": v(81.8, 212.53) * mm, "end": v(81.02, 213.32) * mm});
            skLineSegment(sketch, "E3560", {"start": v(81.02, 213.32) * mm, "end": v(80.23, 214.1) * mm});
            skLineSegment(sketch, "E3561", {"start": v(80.23, 214.1) * mm, "end": v(79.43, 214.87) * mm});
            skLineSegment(sketch, "E3562", {"start": v(79.43, 214.87) * mm, "end": v(78.63, 215.63) * mm});
            skLineSegment(sketch, "E3563", {"start": v(78.63, 215.63) * mm, "end": v(77.83, 216.39) * mm});
            skLineSegment(sketch, "E3564", {"start": v(77.83, 216.39) * mm, "end": v(77.02, 217.14) * mm});
            skLineSegment(sketch, "E3565", {"start": v(77.02, 217.14) * mm, "end": v(76.2, 217.88) * mm});
            skLineSegment(sketch, "E3566", {"start": v(76.2, 217.88) * mm, "end": v(75.38, 218.62) * mm});
            skLineSegment(sketch, "E3567", {"start": v(75.38, 218.62) * mm, "end": v(74.56, 219.35) * mm});
            skLineSegment(sketch, "E3568", {"start": v(74.56, 219.35) * mm, "end": v(73.73, 220.07) * mm});
            skLineSegment(sketch, "E3569", {"start": v(73.73, 220.07) * mm, "end": v(72.9, 220.78) * mm});
            skLineSegment(sketch, "E3570", {"start": v(72.9, 220.78) * mm, "end": v(72.07, 221.49) * mm});
            skLineSegment(sketch, "E3571", {"start": v(72.07, 221.49) * mm, "end": v(71.23, 222.19) * mm});
            skLineSegment(sketch, "E3572", {"start": v(71.23, 222.19) * mm, "end": v(70.38, 222.88) * mm});
            skLineSegment(sketch, "E3573", {"start": v(70.38, 222.88) * mm, "end": v(69.53, 223.56) * mm});
            skLineSegment(sketch, "E3574", {"start": v(69.53, 223.56) * mm, "end": v(68.68, 224.24) * mm});
            skLineSegment(sketch, "E3575", {"start": v(68.68, 224.24) * mm, "end": v(67.82, 224.91) * mm});
            skLineSegment(sketch, "E3576", {"start": v(67.82, 224.91) * mm, "end": v(66.96, 225.58) * mm});
            skLineSegment(sketch, "E3577", {"start": v(66.96, 225.58) * mm, "end": v(66.1, 226.23) * mm});
            skLineSegment(sketch, "E3578", {"start": v(66.1, 226.23) * mm, "end": v(65.22, 226.88) * mm});
            skLineSegment(sketch, "E3579", {"start": v(65.22, 226.88) * mm, "end": v(64.35, 227.52) * mm});
            skLineSegment(sketch, "E3580", {"start": v(64.35, 227.52) * mm, "end": v(63.47, 228.16) * mm});
            skLineSegment(sketch, "E3581", {"start": v(63.47, 228.16) * mm, "end": v(62.59, 228.78) * mm});
            skLineSegment(sketch, "E3582", {"start": v(62.59, 228.78) * mm, "end": v(61.7, 229.4) * mm});
            skLineSegment(sketch, "E3583", {"start": v(61.7, 229.4) * mm, "end": v(60.8, 230.02) * mm});
            skLineSegment(sketch, "E3584", {"start": v(60.8, 230.02) * mm, "end": v(59.9, 230.62) * mm});
            skLineSegment(sketch, "E3585", {"start": v(59.9, 230.62) * mm, "end": v(59, 231.22) * mm});
            skLineSegment(sketch, "E3586", {"start": v(59, 231.22) * mm, "end": v(58.1, 231.8) * mm});
            skLineSegment(sketch, "E3587", {"start": v(58.1, 231.8) * mm, "end": v(57.2, 232.4) * mm});
            skLineSegment(sketch, "E3588", {"start": v(57.2, 232.4) * mm, "end": v(56.28, 232.97) * mm});
            skLineSegment(sketch, "E3589", {"start": v(56.28, 232.97) * mm, "end": v(55.36, 233.54) * mm});
            skLineSegment(sketch, "E3590", {"start": v(55.36, 233.54) * mm, "end": v(54.44, 234.1) * mm});
            skLineSegment(sketch, "E3591", {"start": v(54.44, 234.1) * mm, "end": v(53.5, 234.65) * mm});
            skLineSegment(sketch, "E3592", {"start": v(53.5, 234.65) * mm, "end": v(52.58, 235.2) * mm});
            skLineSegment(sketch, "E3593", {"start": v(52.58, 235.2) * mm, "end": v(51.64, 235.74) * mm});
            skLineSegment(sketch, "E3594", {"start": v(51.64, 235.74) * mm, "end": v(50.7, 236.27) * mm});
            skLineSegment(sketch, "E3595", {"start": v(50.7, 236.27) * mm, "end": v(49.75, 236.8) * mm});
            skLineSegment(sketch, "E3596", {"start": v(49.75, 236.8) * mm, "end": v(48.8, 237.32) * mm});
            skLineSegment(sketch, "E3597", {"start": v(48.8, 237.32) * mm, "end": v(47.85, 237.83) * mm});
            skLineSegment(sketch, "E3598", {"start": v(47.85, 237.83) * mm, "end": v(46.9, 238.33) * mm});
            skLineSegment(sketch, "E3599", {"start": v(46.9, 238.33) * mm, "end": v(45.93, 238.83) * mm});
            skLineSegment(sketch, "E3600", {"start": v(45.93, 238.83) * mm, "end": v(44.96, 239.32) * mm});
            skLineSegment(sketch, "E3601", {"start": v(44.96, 239.32) * mm, "end": v(44, 239.8) * mm});
            skLineSegment(sketch, "E3602", {"start": v(44, 239.8) * mm, "end": v(43.02, 240.28) * mm});
            skLineSegment(sketch, "E3603", {"start": v(43.02, 240.28) * mm, "end": v(42.04, 240.74) * mm});
            skLineSegment(sketch, "E3604", {"start": v(42.04, 240.74) * mm, "end": v(41.05, 241.2) * mm});
            skLineSegment(sketch, "E3605", {"start": v(41.05, 241.2) * mm, "end": v(40.07, 241.66) * mm});
            skLineSegment(sketch, "E3606", {"start": v(40.07, 241.66) * mm, "end": v(39.07, 242.1) * mm});
            skLineSegment(sketch, "E3607", {"start": v(39.07, 242.1) * mm, "end": v(38.07, 242.54) * mm});
            skLineSegment(sketch, "E3608", {"start": v(38.07, 242.54) * mm, "end": v(37.07, 242.97) * mm});
            skLineSegment(sketch, "E3609", {"start": v(37.07, 242.97) * mm, "end": v(36.07, 243.4) * mm});
            skLineSegment(sketch, "E3610", {"start": v(36.07, 243.4) * mm, "end": v(35.06, 243.81) * mm});
            skLineSegment(sketch, "E3611", {"start": v(35.06, 243.81) * mm, "end": v(34.04, 244.22) * mm});
            skLineSegment(sketch, "E3612", {"start": v(34.04, 244.22) * mm, "end": v(33.02, 244.62) * mm});
            skLineSegment(sketch, "E3613", {"start": v(33.02, 244.62) * mm, "end": v(32, 245.02) * mm});
            skLineSegment(sketch, "E3614", {"start": v(32, 245.02) * mm, "end": v(30.97, 245.4) * mm});
            skLineSegment(sketch, "E3615", {"start": v(30.97, 245.4) * mm, "end": v(29.94, 245.79) * mm});
            skLineSegment(sketch, "E3616", {"start": v(29.94, 245.79) * mm, "end": v(28.9, 246.16) * mm});
            skLineSegment(sketch, "E3617", {"start": v(28.9, 246.16) * mm, "end": v(27.86, 246.53) * mm});
            skLineSegment(sketch, "E3618", {"start": v(27.86, 246.53) * mm, "end": v(26.82, 246.89) * mm});
            skLineSegment(sketch, "E3619", {"start": v(26.82, 246.89) * mm, "end": v(25.77, 247.24) * mm});
            skLineSegment(sketch, "E3620", {"start": v(25.77, 247.24) * mm, "end": v(24.71, 247.58) * mm});
            skLineSegment(sketch, "E3621", {"start": v(24.71, 247.58) * mm, "end": v(23.65, 247.92) * mm});
            skLineSegment(sketch, "E3622", {"start": v(23.65, 247.92) * mm, "end": v(22.6, 248.25) * mm});
            skLineSegment(sketch, "E3623", {"start": v(22.6, 248.25) * mm, "end": v(21.52, 248.57) * mm});
            skLineSegment(sketch, "E3624", {"start": v(21.52, 248.57) * mm, "end": v(20.45, 248.89) * mm});
            skLineSegment(sketch, "E3625", {"start": v(20.45, 248.89) * mm, "end": v(19.38, 249.2) * mm});
            skLineSegment(sketch, "E3626", {"start": v(19.38, 249.2) * mm, "end": v(18.3, 249.5) * mm});
            skLineSegment(sketch, "E3627", {"start": v(18.3, 249.5) * mm, "end": v(17.21, 249.79) * mm});
            skLineSegment(sketch, "E3628", {"start": v(17.21, 249.79) * mm, "end": v(16.12, 250.08) * mm});
            skLineSegment(sketch, "E3629", {"start": v(16.12, 250.08) * mm, "end": v(15.03, 250.35) * mm});
            skLineSegment(sketch, "E3630", {"start": v(15.03, 250.35) * mm, "end": v(13.93, 250.63) * mm});
            skLineSegment(sketch, "E3631", {"start": v(13.93, 250.63) * mm, "end": v(12.83, 250.9) * mm});
            skLineSegment(sketch, "E3632", {"start": v(12.83, 250.9) * mm, "end": v(11.72, 251.15) * mm});
            skLineSegment(sketch, "E3633", {"start": v(11.72, 251.15) * mm, "end": v(10.61, 251.4) * mm});
            skLineSegment(sketch, "E3634", {"start": v(10.61, 251.4) * mm, "end": v(9.5, 251.64) * mm});
            skLineSegment(sketch, "E3635", {"start": v(9.5, 251.64) * mm, "end": v(8.38, 251.88) * mm});
            skLineSegment(sketch, "E3636", {"start": v(8.38, 251.88) * mm, "end": v(7.25, 252.1) * mm});
            skLineSegment(sketch, "E3637", {"start": v(7.25, 252.1) * mm, "end": v(6.12, 252.33) * mm});
            skLineSegment(sketch, "E3638", {"start": v(6.12, 252.33) * mm, "end": v(5, 252.54) * mm});
            skLineSegment(sketch, "E3639", {"start": v(5, 252.54) * mm, "end": v(3.85, 252.75) * mm});
            skLineSegment(sketch, "E3640", {"start": v(3.85, 252.75) * mm, "end": v(2.71, 252.95) * mm});
            skLineSegment(sketch, "E3641", {"start": v(2.71, 252.95) * mm, "end": v(1.57, 253.14) * mm});
            skLineSegment(sketch, "E3642", {"start": v(1.57, 253.14) * mm, "end": v(0.42, 253.32) * mm});
            skLineSegment(sketch, "E3643", {"start": v(0.42, 253.32) * mm, "end": v(-0.74, 253.5) * mm});
            skLineSegment(sketch, "E3644", {"start": v(-0.74, 253.5) * mm, "end": v(-1.9, 253.67) * mm});
            skLineSegment(sketch, "E3645", {"start": v(-1.9, 253.67) * mm, "end": v(-3.06, 253.83) * mm});
            skLineSegment(sketch, "E3646", {"start": v(-3.06, 253.83) * mm, "end": v(-4.23, 253.99) * mm});
            skLineSegment(sketch, "E3647", {"start": v(-4.23, 253.99) * mm, "end": v(-5.4, 254.14) * mm});
            skLineSegment(sketch, "E3648", {"start": v(-5.4, 254.14) * mm, "end": v(-6.58, 254.28) * mm});
            skLineSegment(sketch, "E3649", {"start": v(-6.58, 254.28) * mm, "end": v(-7.76, 254.41) * mm});
            skLineSegment(sketch, "E3650", {"start": v(-7.76, 254.41) * mm, "end": v(-8.94, 254.54) * mm});
            skLineSegment(sketch, "E3651", {"start": v(-8.94, 254.54) * mm, "end": v(-10.13, 254.66) * mm});
            skLineSegment(sketch, "E3652", {"start": v(-10.13, 254.66) * mm, "end": v(-12.53, 254.88) * mm});
            skLineSegment(sketch, "E3653", {"start": v(-12.53, 254.88) * mm, "end": v(-14.94, 255.07) * mm});
            skLineSegment(sketch, "E3654", {"start": v(-14.94, 255.07) * mm, "end": v(-17.36, 255.23) * mm});
            skLineSegment(sketch, "E3655", {"start": v(-17.36, 255.23) * mm, "end": v(-19.8, 255.36) * mm});
            skLineSegment(sketch, "E3656", {"start": v(-19.8, 255.36) * mm, "end": v(-22.27, 255.46) * mm});
            skLineSegment(sketch, "E3657", {"start": v(-22.27, 255.46) * mm, "end": v(-24.75, 255.53) * mm});
            skLineSegment(sketch, "E3658", {"start": v(-24.75, 255.53) * mm, "end": v(-27.25, 255.57) * mm});
            skLineSegment(sketch, "E3659", {"start": v(-27.25, 255.57) * mm, "end": v(-29.76, 255.59) * mm});
            skLineSegment(sketch, "E3660", {"start": v(-29.76, 255.59) * mm, "end": v(-31.52, 255.58) * mm});
            skLineSegment(sketch, "E3661", {"start": v(-31.52, 255.58) * mm, "end": v(-33.28, 255.55) * mm});
            skLineSegment(sketch, "E3662", {"start": v(-33.28, 255.55) * mm, "end": v(-35.05, 255.5) * mm});
            skLineSegment(sketch, "E3663", {"start": v(-35.05, 255.5) * mm, "end": v(-36.83, 255.42) * mm});
            skLineSegment(sketch, "E3664", {"start": v(-36.83, 255.42) * mm, "end": v(-38.61, 255.33) * mm});
            skLineSegment(sketch, "E3665", {"start": v(-38.61, 255.33) * mm, "end": v(-40.4, 255.21) * mm});
            skLineSegment(sketch, "E3666", {"start": v(-40.4, 255.21) * mm, "end": v(-42.2, 255.08) * mm});
            skLineSegment(sketch, "E3667", {"start": v(-42.2, 255.08) * mm, "end": v(-44, 254.92) * mm});
            skLineSegment(sketch, "E3668", {"start": v(-44, 254.92) * mm, "end": v(-45.82, 254.75) * mm});
            skLineSegment(sketch, "E3669", {"start": v(-45.82, 254.75) * mm, "end": v(-47.64, 254.55) * mm});
            skLineSegment(sketch, "E3670", {"start": v(-47.64, 254.55) * mm, "end": v(-49.47, 254.33) * mm});
            skLineSegment(sketch, "E3671", {"start": v(-49.47, 254.33) * mm, "end": v(-51.3, 254.1) * mm});
            skLineSegment(sketch, "E3672", {"start": v(-51.3, 254.1) * mm, "end": v(-53.14, 253.84) * mm});
            skLineSegment(sketch, "E3673", {"start": v(-53.14, 253.84) * mm, "end": v(-55, 253.56) * mm});
            skLineSegment(sketch, "E3674", {"start": v(-55, 253.56) * mm, "end": v(-56.85, 253.26) * mm});
            skLineSegment(sketch, "E3675", {"start": v(-56.85, 253.26) * mm, "end": v(-58.7, 252.94) * mm});
            skLineSegment(sketch, "E3676", {"start": v(-58.7, 252.94) * mm, "end": v(-60.58, 252.6) * mm});
            skLineSegment(sketch, "E3677", {"start": v(-60.58, 252.6) * mm, "end": v(-62.45, 252.23) * mm});
            skLineSegment(sketch, "E3678", {"start": v(-62.45, 252.23) * mm, "end": v(-64.33, 251.85) * mm});
            skLineSegment(sketch, "E3679", {"start": v(-64.33, 251.85) * mm, "end": v(-66.22, 251.44) * mm});
            skLineSegment(sketch, "E3680", {"start": v(-66.22, 251.44) * mm, "end": v(-68.12, 251.02) * mm});
            skLineSegment(sketch, "E3681", {"start": v(-68.12, 251.02) * mm, "end": v(-70.03, 250.57) * mm});
            skLineSegment(sketch, "E3682", {"start": v(-70.03, 250.57) * mm, "end": v(-71.94, 250.1) * mm});
            skLineSegment(sketch, "E3683", {"start": v(-71.94, 250.1) * mm, "end": v(-73.85, 249.62) * mm});
            skLineSegment(sketch, "E3684", {"start": v(-73.85, 249.62) * mm, "end": v(-75.78, 249.11) * mm});
            skLineSegment(sketch, "E3685", {"start": v(-75.78, 249.11) * mm, "end": v(-77.71, 248.58) * mm});
            skLineSegment(sketch, "E3686", {"start": v(-77.71, 248.58) * mm, "end": v(-79.65, 248.03) * mm});
            skLineSegment(sketch, "E3687", {"start": v(-79.65, 248.03) * mm, "end": v(-81.6, 247.46) * mm});
            skLineSegment(sketch, "E3688", {"start": v(-81.6, 247.46) * mm, "end": v(-83.55, 246.87) * mm});
            skLineSegment(sketch, "E3689", {"start": v(-83.55, 246.87) * mm, "end": v(-85.51, 246.26) * mm});
            skLineSegment(sketch, "E3690", {"start": v(-85.51, 246.26) * mm, "end": v(-87.48, 245.63) * mm});
            skLineSegment(sketch, "E3691", {"start": v(-87.48, 245.63) * mm, "end": v(-89.45, 244.98) * mm});
            skLineSegment(sketch, "E3692", {"start": v(-89.45, 244.98) * mm, "end": v(-89.45, -247.45) * mm});
            skLineSegment(sketch, "E3693", {"start": v(-89.45, -247.45) * mm, "end": v(-87.28, -248.1) * mm});
            skLineSegment(sketch, "E3694", {"start": v(-87.28, -248.1) * mm, "end": v(-85.13, -248.7) * mm});
            skLineSegment(sketch, "E3695", {"start": v(-85.13, -248.7) * mm, "end": v(-83, -249.3) * mm});
            skLineSegment(sketch, "E3696", {"start": v(-83, -249.3) * mm, "end": v(-80.87, -249.88) * mm});
            skLineSegment(sketch, "E3697", {"start": v(-80.87, -249.88) * mm, "end": v(-78.75, -250.44) * mm});
            skLineSegment(sketch, "E3698", {"start": v(-78.75, -250.44) * mm, "end": v(-76.66, -250.98) * mm});
            skLineSegment(sketch, "E3699", {"start": v(-76.66, -250.98) * mm, "end": v(-74.58, -251.5) * mm});
            skLineSegment(sketch, "E3700", {"start": v(-74.58, -251.5) * mm, "end": v(-72.5, -252) * mm});
            skLineSegment(sketch, "E3701", {"start": v(-72.5, -252) * mm, "end": v(-70.45, -252.47) * mm});
            skLineSegment(sketch, "E3702", {"start": v(-70.45, -252.47) * mm, "end": v(-68.41, -252.92) * mm});
            skLineSegment(sketch, "E3703", {"start": v(-68.41, -252.92) * mm, "end": v(-66.39, -253.36) * mm});
            skLineSegment(sketch, "E3704", {"start": v(-66.39, -253.36) * mm, "end": v(-64.38, -253.77) * mm});
            skLineSegment(sketch, "E3705", {"start": v(-64.38, -253.77) * mm, "end": v(-62.38, -254.17) * mm});
            skLineSegment(sketch, "E3706", {"start": v(-62.38, -254.17) * mm, "end": v(-60.4, -254.54) * mm});
            skLineSegment(sketch, "E3707", {"start": v(-60.4, -254.54) * mm, "end": v(-58.43, -254.9) * mm});
            skLineSegment(sketch, "E3708", {"start": v(-58.43, -254.9) * mm, "end": v(-56.48, -255.23) * mm});
            skLineSegment(sketch, "E3709", {"start": v(-56.48, -255.23) * mm, "end": v(-54.54, -255.55) * mm});
            skLineSegment(sketch, "E3710", {"start": v(-54.54, -255.55) * mm, "end": v(-52.61, -255.84) * mm});
            skLineSegment(sketch, "E3711", {"start": v(-52.61, -255.84) * mm, "end": v(-50.7, -256.11) * mm});
            skLineSegment(sketch, "E3712", {"start": v(-50.7, -256.11) * mm, "end": v(-48.8, -256.37) * mm});
            skLineSegment(sketch, "E3713", {"start": v(-48.8, -256.37) * mm, "end": v(-46.92, -256.6) * mm});
            skLineSegment(sketch, "E3714", {"start": v(-46.92, -256.6) * mm, "end": v(-45.05, -256.81) * mm});
            skLineSegment(sketch, "E3715", {"start": v(-45.05, -256.81) * mm, "end": v(-43.2, -257) * mm});
            skLineSegment(sketch, "E3716", {"start": v(-43.2, -257) * mm, "end": v(-41.36, -257.18) * mm});
            skLineSegment(sketch, "E3717", {"start": v(-41.36, -257.18) * mm, "end": v(-39.53, -257.33) * mm});
            skLineSegment(sketch, "E3718", {"start": v(-39.53, -257.33) * mm, "end": v(-37.72, -257.46) * mm});
            skLineSegment(sketch, "E3719", {"start": v(-37.72, -257.46) * mm, "end": v(-35.93, -257.57) * mm});
            skLineSegment(sketch, "E3720", {"start": v(-35.93, -257.57) * mm, "end": v(-34.14, -257.66) * mm});
            skLineSegment(sketch, "E3721", {"start": v(-34.14, -257.66) * mm, "end": v(-32.38, -257.73) * mm});
            skLineSegment(sketch, "E3722", {"start": v(-32.38, -257.73) * mm, "end": v(-30.62, -257.79) * mm});
            skLineSegment(sketch, "E3723", {"start": v(-30.62, -257.79) * mm, "end": v(-28.88, -257.82) * mm});
            skLineSegment(sketch, "E3724", {"start": v(-28.88, -257.82) * mm, "end": v(-27.16, -257.83) * mm});
            skLineSegment(sketch, "E3725", {"start": v(-27.16, -257.83) * mm, "end": v(-25.93, -257.82) * mm});
            skLineSegment(sketch, "E3726", {"start": v(-25.93, -257.82) * mm, "end": v(-24.7, -257.8) * mm});
            skLineSegment(sketch, "E3727", {"start": v(-24.7, -257.8) * mm, "end": v(-23.48, -257.78) * mm});
            skLineSegment(sketch, "E3728", {"start": v(-23.48, -257.78) * mm, "end": v(-22.26, -257.75) * mm});
            skLineSegment(sketch, "E3729", {"start": v(-22.26, -257.75) * mm, "end": v(-21.05, -257.71) * mm});
            skLineSegment(sketch, "E3730", {"start": v(-21.05, -257.71) * mm, "end": v(-19.84, -257.66) * mm});
            skLineSegment(sketch, "E3731", {"start": v(-19.84, -257.66) * mm, "end": v(-18.64, -257.6) * mm});
            skLineSegment(sketch, "E3732", {"start": v(-18.64, -257.6) * mm, "end": v(-17.43, -257.53) * mm});
            skLineSegment(sketch, "E3733", {"start": v(-17.43, -257.53) * mm, "end": v(-16.24, -257.45) * mm});
            skLineSegment(sketch, "E3734", {"start": v(-16.24, -257.45) * mm, "end": v(-15.04, -257.36) * mm});
            skLineSegment(sketch, "E3735", {"start": v(-15.04, -257.36) * mm, "end": v(-13.85, -257.27) * mm});
            skLineSegment(sketch, "E3736", {"start": v(-13.85, -257.27) * mm, "end": v(-12.67, -257.16) * mm});
            skLineSegment(sketch, "E3737", {"start": v(-12.67, -257.16) * mm, "end": v(-11.49, -257.05) * mm});
            skLineSegment(sketch, "E3738", {"start": v(-11.49, -257.05) * mm, "end": v(-10.31, -256.92) * mm});
            skLineSegment(sketch, "E3739", {"start": v(-10.31, -256.92) * mm, "end": v(-9.14, -256.79) * mm});
            skLineSegment(sketch, "E3740", {"start": v(-9.14, -256.79) * mm, "end": v(-7.97, -256.64) * mm});
            skLineSegment(sketch, "E3741", {"start": v(-7.97, -256.64) * mm, "end": v(-6.8, -256.5) * mm});
            skLineSegment(sketch, "E3742", {"start": v(-6.8, -256.5) * mm, "end": v(-5.64, -256.33) * mm});
            skLineSegment(sketch, "E3743", {"start": v(-5.64, -256.33) * mm, "end": v(-4.48, -256.16) * mm});
            skLineSegment(sketch, "E3744", {"start": v(-4.48, -256.16) * mm, "end": v(-3.33, -255.98) * mm});
            skLineSegment(sketch, "E3745", {"start": v(-3.33, -255.98) * mm, "end": v(-2.18, -255.79) * mm});
            skLineSegment(sketch, "E3746", {"start": v(-2.18, -255.79) * mm, "end": v(-1.04, -255.6) * mm});
            skLineSegment(sketch, "E3747", {"start": v(-1.04, -255.6) * mm, "end": v(0.1, -255.38) * mm});
            skLineSegment(sketch, "E3748", {"start": v(0.1, -255.38) * mm, "end": v(1.24, -255.17) * mm});
            skLineSegment(sketch, "E3749", {"start": v(1.24, -255.17) * mm, "end": v(2.38, -254.94) * mm});
            skLineSegment(sketch, "E3750", {"start": v(2.38, -254.94) * mm, "end": v(3.5, -254.7) * mm});
            skLineSegment(sketch, "E3751", {"start": v(3.5, -254.7) * mm, "end": v(4.63, -254.46) * mm});
            skLineSegment(sketch, "E3752", {"start": v(4.63, -254.46) * mm, "end": v(5.75, -254.2) * mm});
            skLineSegment(sketch, "E3753", {"start": v(5.75, -254.2) * mm, "end": v(6.87, -253.94) * mm});
            skLineSegment(sketch, "E3754", {"start": v(6.87, -253.94) * mm, "end": v(7.98, -253.67) * mm});
            skLineSegment(sketch, "E3755", {"start": v(7.98, -253.67) * mm, "end": v(9.1, -253.39) * mm});
            skLineSegment(sketch, "E3756", {"start": v(9.1, -253.39) * mm, "end": v(10.2, -253.1) * mm});
            skLineSegment(sketch, "E3757", {"start": v(10.2, -253.1) * mm, "end": v(11.3, -252.8) * mm});
            skLineSegment(sketch, "E3758", {"start": v(11.3, -252.8) * mm, "end": v(12.4, -252.49) * mm});
            skLineSegment(sketch, "E3759", {"start": v(12.4, -252.49) * mm, "end": v(13.49, -252.17) * mm});
            skLineSegment(sketch, "E3760", {"start": v(13.49, -252.17) * mm, "end": v(14.58, -251.84) * mm});
            skLineSegment(sketch, "E3761", {"start": v(14.58, -251.84) * mm, "end": v(15.66, -251.5) * mm});
            skLineSegment(sketch, "E3762", {"start": v(15.66, -251.5) * mm, "end": v(16.75, -251.16) * mm});
            skLineSegment(sketch, "E3763", {"start": v(16.75, -251.16) * mm, "end": v(17.82, -250.8) * mm});
            skLineSegment(sketch, "E3764", {"start": v(17.82, -250.8) * mm, "end": v(18.9, -250.44) * mm});
            skLineSegment(sketch, "E3765", {"start": v(18.9, -250.44) * mm, "end": v(19.97, -250.06) * mm});
            skLineSegment(sketch, "E3766", {"start": v(19.97, -250.06) * mm, "end": v(21.03, -249.68) * mm});
            skLineSegment(sketch, "E3767", {"start": v(21.03, -249.68) * mm, "end": v(22.1, -249.28) * mm});
            skLineSegment(sketch, "E3768", {"start": v(22.1, -249.28) * mm, "end": v(23.15, -248.88) * mm});
            skLineSegment(sketch, "E3769", {"start": v(23.15, -248.88) * mm, "end": v(24.2, -248.47) * mm});
            skLineSegment(sketch, "E3770", {"start": v(24.2, -248.47) * mm, "end": v(25.25, -248.05) * mm});
            skLineSegment(sketch, "E3771", {"start": v(25.25, -248.05) * mm, "end": v(26.3, -247.62) * mm});
            skLineSegment(sketch, "E3772", {"start": v(26.3, -247.62) * mm, "end": v(27.34, -247.18) * mm});
            skLineSegment(sketch, "E3773", {"start": v(27.34, -247.18) * mm, "end": v(28.38, -246.74) * mm});
            skLineSegment(sketch, "E3774", {"start": v(28.38, -246.74) * mm, "end": v(29.41, -246.28) * mm});
            skLineSegment(sketch, "E3775", {"start": v(29.41, -246.28) * mm, "end": v(30.44, -245.81) * mm});
            skLineSegment(sketch, "E3776", {"start": v(30.44, -245.81) * mm, "end": v(31.47, -245.34) * mm});
            skLineSegment(sketch, "E3777", {"start": v(31.47, -245.34) * mm, "end": v(32.49, -244.85) * mm});
            skLineSegment(sketch, "E3778", {"start": v(32.49, -244.85) * mm, "end": v(33.5, -244.36) * mm});
            skLineSegment(sketch, "E3779", {"start": v(33.5, -244.36) * mm, "end": v(34.52, -243.85) * mm});
            skLineSegment(sketch, "E3780", {"start": v(34.52, -243.85) * mm, "end": v(35.53, -243.34) * mm});
            skLineSegment(sketch, "E3781", {"start": v(35.53, -243.34) * mm, "end": v(36.53, -242.82) * mm});
            skLineSegment(sketch, "E3782", {"start": v(36.53, -242.82) * mm, "end": v(37.54, -242.29) * mm});
            skLineSegment(sketch, "E3783", {"start": v(37.54, -242.29) * mm, "end": v(38.53, -241.75) * mm});
            skLineSegment(sketch, "E3784", {"start": v(38.53, -241.75) * mm, "end": v(39.53, -241.2) * mm});
            skLineSegment(sketch, "E3785", {"start": v(39.53, -241.2) * mm, "end": v(40.52, -240.64) * mm});
            skLineSegment(sketch, "E3786", {"start": v(40.52, -240.64) * mm, "end": v(41.5, -240.07) * mm});
            skLineSegment(sketch, "E3787", {"start": v(41.5, -240.07) * mm, "end": v(42.48, -239.5) * mm});
            skLineSegment(sketch, "E3788", {"start": v(42.48, -239.5) * mm, "end": v(43.46, -238.9) * mm});
            skLineSegment(sketch, "E3789", {"start": v(43.46, -238.9) * mm, "end": v(44.44, -238.3) * mm});
            skLineSegment(sketch, "E3790", {"start": v(44.44, -238.3) * mm, "end": v(45.4, -237.7) * mm});
            skLineSegment(sketch, "E3791", {"start": v(45.4, -237.7) * mm, "end": v(46.37, -237.1) * mm});
            skLineSegment(sketch, "E3792", {"start": v(46.37, -237.1) * mm, "end": v(47.33, -236.47) * mm});
            skLineSegment(sketch, "E3793", {"start": v(47.33, -236.47) * mm, "end": v(48.29, -235.83) * mm});
            skLineSegment(sketch, "E3794", {"start": v(48.29, -235.83) * mm, "end": v(49.24, -235.2) * mm});
            skLineSegment(sketch, "E3795", {"start": v(49.24, -235.2) * mm, "end": v(50.2, -234.54) * mm});
            skLineSegment(sketch, "E3796", {"start": v(50.2, -234.54) * mm, "end": v(51.14, -233.88) * mm});
            skLineSegment(sketch, "E3797", {"start": v(51.14, -233.88) * mm, "end": v(52.08, -233.2) * mm});
            skLineSegment(sketch, "E3798", {"start": v(52.08, -233.2) * mm, "end": v(53.02, -232.53) * mm});
            skLineSegment(sketch, "E3799", {"start": v(53.02, -232.53) * mm, "end": v(53.95, -231.84) * mm});
            skLineSegment(sketch, "E3800", {"start": v(53.95, -231.84) * mm, "end": v(54.88, -231.15) * mm});
            skLineSegment(sketch, "E3801", {"start": v(54.88, -231.15) * mm, "end": v(55.8, -230.44) * mm});
            skLineSegment(sketch, "E3802", {"start": v(55.8, -230.44) * mm, "end": v(56.73, -229.72) * mm});
            skLineSegment(sketch, "E3803", {"start": v(56.73, -229.72) * mm, "end": v(57.65, -229) * mm});
            skLineSegment(sketch, "E3804", {"start": v(57.65, -229) * mm, "end": v(58.56, -228.26) * mm});
            skLineSegment(sketch, "E3805", {"start": v(58.56, -228.26) * mm, "end": v(59.47, -227.52) * mm});
            skLineSegment(sketch, "E3806", {"start": v(59.47, -227.52) * mm, "end": v(60.38, -226.77) * mm});
            skLineSegment(sketch, "E3807", {"start": v(60.38, -226.77) * mm, "end": v(61.28, -226) * mm});
            skLineSegment(sketch, "E3808", {"start": v(61.28, -226) * mm, "end": v(62.17, -225.23) * mm});
            skLineSegment(sketch, "E3809", {"start": v(62.17, -225.23) * mm, "end": v(63.07, -224.45) * mm});
            skLineSegment(sketch, "E3810", {"start": v(63.07, -224.45) * mm, "end": v(63.96, -223.66) * mm});
            skLineSegment(sketch, "E3811", {"start": v(63.96, -223.66) * mm, "end": v(64.84, -222.86) * mm});
            skLineSegment(sketch, "E3812", {"start": v(64.84, -222.86) * mm, "end": v(65.73, -222.05) * mm});
            skLineSegment(sketch, "E3813", {"start": v(65.73, -222.05) * mm, "end": v(66.6, -221.24) * mm});
            skLineSegment(sketch, "E3814", {"start": v(66.6, -221.24) * mm, "end": v(67.48, -220.41) * mm});
            skLineSegment(sketch, "E3815", {"start": v(67.48, -220.41) * mm, "end": v(68.35, -219.57) * mm});
            skLineSegment(sketch, "E3816", {"start": v(68.35, -219.57) * mm, "end": v(69.21, -218.73) * mm});
            skLineSegment(sketch, "E3817", {"start": v(69.21, -218.73) * mm, "end": v(70.07, -217.87) * mm});
            skLineSegment(sketch, "E3818", {"start": v(70.07, -217.87) * mm, "end": v(70.93, -217.01) * mm});
            skLineSegment(sketch, "E3819", {"start": v(70.93, -217.01) * mm, "end": v(71.79, -216.14) * mm});
            skLineSegment(sketch, "E3820", {"start": v(71.79, -216.14) * mm, "end": v(72.64, -215.25) * mm});
            skLineSegment(sketch, "E3821", {"start": v(72.64, -215.25) * mm, "end": v(73.48, -214.36) * mm});
            skLineSegment(sketch, "E3822", {"start": v(73.48, -214.36) * mm, "end": v(74.32, -213.46) * mm});
            skLineSegment(sketch, "E3823", {"start": v(74.32, -213.46) * mm, "end": v(75.16, -212.55) * mm});
            skLineSegment(sketch, "E3824", {"start": v(75.16, -212.55) * mm, "end": v(76, -211.63) * mm});
            skLineSegment(sketch, "E3825", {"start": v(76, -211.63) * mm, "end": v(76.82, -210.7) * mm});
            skLineSegment(sketch, "E3826", {"start": v(76.82, -210.7) * mm, "end": v(77.65, -209.77) * mm});
            skLineSegment(sketch, "E3827", {"start": v(77.65, -209.77) * mm, "end": v(78.47, -208.82) * mm});
            skLineSegment(sketch, "E3828", {"start": v(78.47, -208.82) * mm, "end": v(79.29, -207.86) * mm});
            skLineSegment(sketch, "E3829", {"start": v(79.29, -207.86) * mm, "end": v(80.1, -206.9) * mm});
            skLineSegment(sketch, "E3830", {"start": v(80.1, -206.9) * mm, "end": v(80.91, -205.92) * mm});
            skLineSegment(sketch, "E3831", {"start": v(80.91, -205.92) * mm, "end": v(81.72, -204.94) * mm});
            skLineSegment(sketch, "E3832", {"start": v(81.72, -204.94) * mm, "end": v(82.52, -203.95) * mm});
            skLineSegment(sketch, "E3833", {"start": v(82.52, -203.95) * mm, "end": v(83.32, -202.94) * mm});
            skLineSegment(sketch, "E3834", {"start": v(83.32, -202.94) * mm, "end": v(84.11, -201.93) * mm});
            skLineSegment(sketch, "E3835", {"start": v(84.11, -201.93) * mm, "end": v(84.9, -200.91) * mm});
            skLineSegment(sketch, "E3836", {"start": v(84.9, -200.91) * mm, "end": v(85.69, -199.88) * mm});
            skLineSegment(sketch, "E3837", {"start": v(85.69, -199.88) * mm, "end": v(86.47, -198.84) * mm});
            skLineSegment(sketch, "E3838", {"start": v(86.47, -198.84) * mm, "end": v(87.25, -197.8) * mm});
            skLineSegment(sketch, "E3839", {"start": v(87.25, -197.8) * mm, "end": v(88.02, -196.74) * mm});
            skLineSegment(sketch, "E3840", {"start": v(88.02, -196.74) * mm, "end": v(88.8, -195.67) * mm});
            skLineSegment(sketch, "E3841", {"start": v(88.8, -195.67) * mm, "end": v(89.56, -194.6) * mm});
            skLineSegment(sketch, "E3842", {"start": v(89.56, -194.6) * mm, "end": v(90.32, -193.5) * mm});
            skLineSegment(sketch, "E3843", {"start": v(90.32, -193.5) * mm, "end": v(91.08, -192.41) * mm});
            skLineSegment(sketch, "E3844", {"start": v(91.08, -192.41) * mm, "end": v(91.83, -191.3) * mm});
            skLineSegment(sketch, "E3845", {"start": v(91.83, -191.3) * mm, "end": v(92.58, -190.2) * mm});
            skLineSegment(sketch, "E3846", {"start": v(92.58, -190.2) * mm, "end": v(93.33, -189.07) * mm});
            skLineSegment(sketch, "E3847", {"start": v(93.33, -189.07) * mm, "end": v(94.07, -187.94) * mm});
            skLineSegment(sketch, "E3848", {"start": v(94.07, -187.94) * mm, "end": v(94.8, -186.8) * mm});
            skLineSegment(sketch, "E3849", {"start": v(94.8, -186.8) * mm, "end": v(95.54, -185.65) * mm});
            skLineSegment(sketch, "E3850", {"start": v(95.54, -185.65) * mm, "end": v(96.27, -184.5) * mm});
            skLineSegment(sketch, "E3851", {"start": v(96.27, -184.5) * mm, "end": v(97, -183.32) * mm});
            skLineSegment(sketch, "E3852", {"start": v(97, -183.32) * mm, "end": v(97.72, -182.14) * mm});
            skLineSegment(sketch, "E3853", {"start": v(97.72, -182.14) * mm, "end": v(99.07, -179.92) * mm});
            skLineSegment(sketch, "E3854", {"start": v(99.07, -179.92) * mm, "end": v(100.4, -177.67) * mm});
            skLineSegment(sketch, "E3855", {"start": v(100.4, -177.67) * mm, "end": v(101.7, -175.4) * mm});
            skLineSegment(sketch, "E3856", {"start": v(101.7, -175.4) * mm, "end": v(102.98, -173.12) * mm});
            skLineSegment(sketch, "E3857", {"start": v(102.98, -173.12) * mm, "end": v(104.24, -170.82) * mm});
            skLineSegment(sketch, "E3858", {"start": v(104.24, -170.82) * mm, "end": v(105.48, -168.5) * mm});
            skLineSegment(sketch, "E3859", {"start": v(105.48, -168.5) * mm, "end": v(106.7, -166.15) * mm});
            skLineSegment(sketch, "E3860", {"start": v(106.7, -166.15) * mm, "end": v(107.9, -163.8) * mm});
            skLineSegment(sketch, "E3861", {"start": v(107.9, -163.8) * mm, "end": v(109.07, -161.41) * mm});
            skLineSegment(sketch, "E3862", {"start": v(109.07, -161.41) * mm, "end": v(110.23, -159.01) * mm});
            skLineSegment(sketch, "E3863", {"start": v(110.23, -159.01) * mm, "end": v(111.36, -156.6) * mm});
            skLineSegment(sketch, "E3864", {"start": v(111.36, -156.6) * mm, "end": v(112.47, -154.16) * mm});
            skLineSegment(sketch, "E3865", {"start": v(112.47, -154.16) * mm, "end": v(113.57, -151.7) * mm});
            skLineSegment(sketch, "E3866", {"start": v(113.57, -151.7) * mm, "end": v(114.64, -149.23) * mm});
            skLineSegment(sketch, "E3867", {"start": v(114.64, -149.23) * mm, "end": v(115.69, -146.73) * mm});
            skLineSegment(sketch, "E3868", {"start": v(115.69, -146.73) * mm, "end": v(116.71, -144.22) * mm});
            skLineSegment(sketch, "E3869", {"start": v(116.71, -144.22) * mm, "end": v(117.72, -141.69) * mm});
            skLineSegment(sketch, "E3870", {"start": v(117.72, -141.69) * mm, "end": v(118.7, -139.14) * mm});
            skLineSegment(sketch, "E3871", {"start": v(118.7, -139.14) * mm, "end": v(119.67, -136.56) * mm});
            skLineSegment(sketch, "E3872", {"start": v(119.67, -136.56) * mm, "end": v(120.61, -133.97) * mm});
            skLineSegment(sketch, "E3873", {"start": v(120.61, -133.97) * mm, "end": v(121.54, -131.37) * mm});
            skLineSegment(sketch, "E3874", {"start": v(121.54, -131.37) * mm, "end": v(122.44, -128.74) * mm});
            skLineSegment(sketch, "E3875", {"start": v(122.44, -128.74) * mm, "end": v(123.32, -126.1) * mm});
            skLineSegment(sketch, "E3876", {"start": v(123.32, -126.1) * mm, "end": v(124.18, -123.42) * mm});
            skLineSegment(sketch, "E3877", {"start": v(124.18, -123.42) * mm, "end": v(125.01, -120.74) * mm});
            skLineSegment(sketch, "E3878", {"start": v(125.01, -120.74) * mm, "end": v(125.83, -118.03) * mm});
            skLineSegment(sketch, "E3879", {"start": v(125.83, -118.03) * mm, "end": v(126.62, -115.31) * mm});
            skLineSegment(sketch, "E3880", {"start": v(126.62, -115.31) * mm, "end": v(127.4, -112.57) * mm});
            skLineSegment(sketch, "E3881", {"start": v(127.4, -112.57) * mm, "end": v(128.15, -109.8) * mm});
            skLineSegment(sketch, "E3882", {"start": v(128.15, -109.8) * mm, "end": v(128.88, -107.03) * mm});
            skLineSegment(sketch, "E3883", {"start": v(128.88, -107.03) * mm, "end": v(129.6, -104.23) * mm});
            skLineSegment(sketch, "E3884", {"start": v(129.6, -104.23) * mm, "end": v(130.28, -101.4) * mm});
            skLineSegment(sketch, "E3885", {"start": v(130.28, -101.4) * mm, "end": v(130.95, -98.57) * mm});
            skLineSegment(sketch, "E3886", {"start": v(130.95, -98.57) * mm, "end": v(131.6, -95.71) * mm});
            skLineSegment(sketch, "E3887", {"start": v(131.6, -95.71) * mm, "end": v(132.22, -92.84) * mm});
            skLineSegment(sketch, "E3888", {"start": v(132.22, -92.84) * mm, "end": v(132.83, -89.94) * mm});
            skLineSegment(sketch, "E3889", {"start": v(132.83, -89.94) * mm, "end": v(133.4, -87.03) * mm});
            skLineSegment(sketch, "E3890", {"start": v(133.4, -87.03) * mm, "end": v(133.97, -84.1) * mm});
            skLineSegment(sketch, "E3891", {"start": v(133.97, -84.1) * mm, "end": v(134.51, -81.14) * mm});
            skLineSegment(sketch, "E3892", {"start": v(134.51, -81.14) * mm, "end": v(135.03, -78.17) * mm});
            skLineSegment(sketch, "E3893", {"start": v(135.03, -78.17) * mm, "end": v(135.53, -75.18) * mm});
            skLineSegment(sketch, "E3894", {"start": v(135.53, -75.18) * mm, "end": v(136, -72.17) * mm});
            skLineSegment(sketch, "E3895", {"start": v(136, -72.17) * mm, "end": v(136.46, -69.14) * mm});
            skLineSegment(sketch, "E3896", {"start": v(136.46, -69.14) * mm, "end": v(136.9, -66.1) * mm});
            skLineSegment(sketch, "E3897", {"start": v(136.9, -66.1) * mm, "end": v(137.3, -63.02) * mm});
            skLineSegment(sketch, "E3898", {"start": v(137.3, -63.02) * mm, "end": v(137.7, -59.94) * mm});
            skLineSegment(sketch, "E3899", {"start": v(137.7, -59.94) * mm, "end": v(138.07, -56.83) * mm});
            skLineSegment(sketch, "E3900", {"start": v(138.07, -56.83) * mm, "end": v(138.42, -53.7) * mm});
            skLineSegment(sketch, "E3901", {"start": v(138.42, -53.7) * mm, "end": v(138.75, -50.56) * mm});
            skLineSegment(sketch, "E3902", {"start": v(138.75, -50.56) * mm, "end": v(139.06, -47.4) * mm});
            skLineSegment(sketch, "E3903", {"start": v(139.06, -47.4) * mm, "end": v(139.34, -44.22) * mm});
            skLineSegment(sketch, "E3904", {"start": v(139.34, -44.22) * mm, "end": v(139.6, -41.02) * mm});
            skLineSegment(sketch, "E3905", {"start": v(139.6, -41.02) * mm, "end": v(139.85, -37.8) * mm});
            skLineSegment(sketch, "E3906", {"start": v(139.85, -37.8) * mm, "end": v(140.08, -34.56) * mm});
            skLineSegment(sketch, "E3907", {"start": v(140.08, -34.56) * mm, "end": v(140.28, -31.3) * mm});
            skLineSegment(sketch, "E3908", {"start": v(140.28, -31.3) * mm, "end": v(140.46, -28.02) * mm});
            skLineSegment(sketch, "E3909", {"start": v(140.46, -28.02) * mm, "end": v(140.62, -24.73) * mm});
            skLineSegment(sketch, "E3910", {"start": v(140.62, -24.73) * mm, "end": v(140.75, -21.41) * mm});
            skLineSegment(sketch, "E3911", {"start": v(140.75, -21.41) * mm, "end": v(140.87, -18.08) * mm});
            skLineSegment(sketch, "E3912", {"start": v(140.87, -18.08) * mm, "end": v(140.97, -14.72) * mm});
            skLineSegment(sketch, "E3913", {"start": v(140.97, -14.72) * mm, "end": v(141.04, -11.35) * mm});
            skLineSegment(sketch, "E3914", {"start": v(141.04, -11.35) * mm, "end": v(141.1, -7.96) * mm});
            skLineSegment(sketch, "E3915", {"start": v(141.1, -7.96) * mm, "end": v(141.13, -4.55) * mm});
            skLineSegment(sketch, "E3916", {"start": v(141.13, -4.55) * mm, "end": v(141.14, -1.12) * mm});
            skLineSegment(sketch, "E3917", {"start": v(-128.57, 150.05) * mm, "end": v(-128.57, 158) * mm});
            skLineSegment(sketch, "E3918", {"start": v(-128.57, 158) * mm, "end": v(-128.26, 158.2) * mm});
            skLineSegment(sketch, "E3919", {"start": v(-128.26, 158.2) * mm, "end": v(-127.96, 158.4) * mm});
            skLineSegment(sketch, "E3920", {"start": v(-127.96, 158.4) * mm, "end": v(-127.7, 158.6) * mm});
            skLineSegment(sketch, "E3921", {"start": v(-127.7, 158.6) * mm, "end": v(-127.44, 158.8) * mm});
            skLineSegment(sketch, "E3922", {"start": v(-127.44, 158.8) * mm, "end": v(-127.2, 159) * mm});
            skLineSegment(sketch, "E3923", {"start": v(-127.2, 159) * mm, "end": v(-127, 159.22) * mm});
            skLineSegment(sketch, "E3924", {"start": v(-127, 159.22) * mm, "end": v(-126.8, 159.43) * mm});
            skLineSegment(sketch, "E3925", {"start": v(-126.8, 159.43) * mm, "end": v(-126.63, 159.64) * mm});
            skLineSegment(sketch, "E3926", {"start": v(-126.63, 159.64) * mm, "end": v(-126.46, 159.87) * mm});
            skLineSegment(sketch, "E3927", {"start": v(-126.46, 159.87) * mm, "end": v(-126.3, 160.13) * mm});
            skLineSegment(sketch, "E3928", {"start": v(-126.3, 160.13) * mm, "end": v(-126.16, 160.4) * mm});
            skLineSegment(sketch, "E3929", {"start": v(-126.16, 160.4) * mm, "end": v(-126, 160.7) * mm});
            skLineSegment(sketch, "E3930", {"start": v(-126, 160.7) * mm, "end": v(-125.87, 161.03) * mm});
            skLineSegment(sketch, "E3931", {"start": v(-125.87, 161.03) * mm, "end": v(-125.74, 161.38) * mm});
            skLineSegment(sketch, "E3932", {"start": v(-125.74, 161.38) * mm, "end": v(-125.6, 161.76) * mm});
            skLineSegment(sketch, "E3933", {"start": v(-125.6, 161.76) * mm, "end": v(-125.48, 162.16) * mm});
            skLineSegment(sketch, "E3934", {"start": v(-125.48, 162.16) * mm, "end": v(-125.36, 162.58) * mm});
            skLineSegment(sketch, "E3935", {"start": v(-125.36, 162.58) * mm, "end": v(-125.25, 163) * mm});
            skLineSegment(sketch, "E3936", {"start": v(-125.25, 163) * mm, "end": v(-125.14, 163.42) * mm});
            skLineSegment(sketch, "E3937", {"start": v(-125.14, 163.42) * mm, "end": v(-125.05, 163.85) * mm});
            skLineSegment(sketch, "E3938", {"start": v(-125.05, 163.85) * mm, "end": v(-124.96, 164.29) * mm});
            skLineSegment(sketch, "E3939", {"start": v(-124.96, 164.29) * mm, "end": v(-124.87, 164.73) * mm});
            skLineSegment(sketch, "E3940", {"start": v(-124.87, 164.73) * mm, "end": v(-124.8, 165.17) * mm});
            skLineSegment(sketch, "E3941", {"start": v(-124.8, 165.17) * mm, "end": v(-124.73, 165.62) * mm});
            skLineSegment(sketch, "E3942", {"start": v(-124.73, 165.62) * mm, "end": v(-124.68, 166.08) * mm});
            skLineSegment(sketch, "E3943", {"start": v(-124.68, 166.08) * mm, "end": v(-124.62, 166.53) * mm});
            skLineSegment(sketch, "E3944", {"start": v(-124.62, 166.53) * mm, "end": v(-124.58, 167) * mm});
            skLineSegment(sketch, "E3945", {"start": v(-124.58, 167) * mm, "end": v(-124.55, 167.47) * mm});
            skLineSegment(sketch, "E3946", {"start": v(-124.55, 167.47) * mm, "end": v(-124.52, 167.94) * mm});
            skLineSegment(sketch, "E3947", {"start": v(-124.52, 167.94) * mm, "end": v(-124.5, 168.42) * mm});
            skLineSegment(sketch, "E3948", {"start": v(-124.5, 168.42) * mm, "end": v(-124.49, 168.9) * mm});
            skLineSegment(sketch, "E3949", {"start": v(-124.49, 168.9) * mm, "end": v(-124.48, 169.4) * mm});
            skLineSegment(sketch, "E3950", {"start": v(-124.48, 169.4) * mm, "end": v(-124.48, 241.98) * mm});
            skLineSegment(sketch, "E3951", {"start": v(-124.48, 241.98) * mm, "end": v(-124.5, 243.66) * mm});
            skLineSegment(sketch, "E3952", {"start": v(-124.5, 243.66) * mm, "end": v(-124.51, 245.08) * mm});
            skLineSegment(sketch, "E3953", {"start": v(-124.51, 245.08) * mm, "end": v(-124.55, 246.23) * mm});
            skLineSegment(sketch, "E3954", {"start": v(-124.55, 246.23) * mm, "end": v(-124.6, 247.13) * mm});
            skLineSegment(sketch, "E3955", {"start": v(-124.6, 247.13) * mm, "end": v(-124.64, 247.5) * mm});
            skLineSegment(sketch, "E3956", {"start": v(-124.64, 247.5) * mm, "end": v(-124.68, 247.87) * mm});
            skLineSegment(sketch, "E3957", {"start": v(-124.68, 247.87) * mm, "end": v(-124.74, 248.22) * mm});
            skLineSegment(sketch, "E3958", {"start": v(-124.74, 248.22) * mm, "end": v(-124.8, 248.55) * mm});
            skLineSegment(sketch, "E3959", {"start": v(-124.8, 248.55) * mm, "end": v(-124.88, 248.88) * mm});
            skLineSegment(sketch, "E3960", {"start": v(-124.88, 248.88) * mm, "end": v(-124.96, 249.19) * mm});
            skLineSegment(sketch, "E3961", {"start": v(-124.96, 249.19) * mm, "end": v(-125.06, 249.48) * mm});
            skLineSegment(sketch, "E3962", {"start": v(-125.06, 249.48) * mm, "end": v(-125.16, 249.76) * mm});
            skLineSegment(sketch, "E3963", {"start": v(-125.16, 249.76) * mm, "end": v(-125.25, 249.97) * mm});
            skLineSegment(sketch, "E3964", {"start": v(-125.25, 249.97) * mm, "end": v(-125.34, 250.17) * mm});
            skLineSegment(sketch, "E3965", {"start": v(-125.34, 250.17) * mm, "end": v(-125.45, 250.36) * mm});
            skLineSegment(sketch, "E3966", {"start": v(-125.45, 250.36) * mm, "end": v(-125.56, 250.55) * mm});
            skLineSegment(sketch, "E3967", {"start": v(-125.56, 250.55) * mm, "end": v(-125.68, 250.73) * mm});
            skLineSegment(sketch, "E3968", {"start": v(-125.68, 250.73) * mm, "end": v(-125.81, 250.9) * mm});
            skLineSegment(sketch, "E3969", {"start": v(-125.81, 250.9) * mm, "end": v(-125.95, 251.07) * mm});
            skLineSegment(sketch, "E3970", {"start": v(-125.95, 251.07) * mm, "end": v(-126.1, 251.24) * mm});
            skLineSegment(sketch, "E3971", {"start": v(-126.1, 251.24) * mm, "end": v(-126.26, 251.4) * mm});
            skLineSegment(sketch, "E3972", {"start": v(-126.26, 251.4) * mm, "end": v(-126.43, 251.55) * mm});
            skLineSegment(sketch, "E3973", {"start": v(-126.43, 251.55) * mm, "end": v(-126.61, 251.7) * mm});
            skLineSegment(sketch, "E3974", {"start": v(-126.61, 251.7) * mm, "end": v(-126.8, 251.84) * mm});
            skLineSegment(sketch, "E3975", {"start": v(-126.8, 251.84) * mm, "end": v(-127, 251.98) * mm});
            skLineSegment(sketch, "E3976", {"start": v(-127, 251.98) * mm, "end": v(-127.2, 252.11) * mm});
            skLineSegment(sketch, "E3977", {"start": v(-127.2, 252.11) * mm, "end": v(-127.42, 252.24) * mm});
            skLineSegment(sketch, "E3978", {"start": v(-127.42, 252.24) * mm, "end": v(-127.65, 252.36) * mm});
            skLineSegment(sketch, "E3979", {"start": v(-127.65, 252.36) * mm, "end": v(-127.65, 260.07) * mm});
            skLineSegment(sketch, "E3980", {"start": v(-127.65, 260.07) * mm, "end": v(-127.17, 259.96) * mm});
            skLineSegment(sketch, "E3981", {"start": v(-127.17, 259.96) * mm, "end": v(-126.7, 259.82) * mm});
            skLineSegment(sketch, "E3982", {"start": v(-126.7, 259.82) * mm, "end": v(-126.22, 259.67) * mm});
            skLineSegment(sketch, "E3983", {"start": v(-126.22, 259.67) * mm, "end": v(-125.75, 259.5) * mm});
            skLineSegment(sketch, "E3984", {"start": v(-125.75, 259.5) * mm, "end": v(-125.3, 259.3) * mm});
            skLineSegment(sketch, "E3985", {"start": v(-125.3, 259.3) * mm, "end": v(-124.83, 259.07) * mm});
            skLineSegment(sketch, "E3986", {"start": v(-124.83, 259.07) * mm, "end": v(-124.38, 258.83) * mm});
            skLineSegment(sketch, "E3987", {"start": v(-124.38, 258.83) * mm, "end": v(-123.92, 258.56) * mm});
            skLineSegment(sketch, "E3988", {"start": v(-123.92, 258.56) * mm, "end": v(-123.48, 258.27) * mm});
            skLineSegment(sketch, "E3989", {"start": v(-123.48, 258.27) * mm, "end": v(-123.03, 257.96) * mm});
            skLineSegment(sketch, "E3990", {"start": v(-123.03, 257.96) * mm, "end": v(-122.59, 257.63) * mm});
            skLineSegment(sketch, "E3991", {"start": v(-122.59, 257.63) * mm, "end": v(-122.15, 257.27) * mm});
            skLineSegment(sketch, "E3992", {"start": v(-122.15, 257.27) * mm, "end": v(-121.72, 256.9) * mm});
            skLineSegment(sketch, "E3993", {"start": v(-121.72, 256.9) * mm, "end": v(-121.29, 256.5) * mm});
            skLineSegment(sketch, "E3994", {"start": v(-121.29, 256.5) * mm, "end": v(-120.86, 256.07) * mm});
            skLineSegment(sketch, "E3995", {"start": v(-120.86, 256.07) * mm, "end": v(-120.44, 255.62) * mm});
            skLineSegment(sketch, "E3996", {"start": v(-120.44, 255.62) * mm, "end": v(-120.02, 255.16) * mm});
            skLineSegment(sketch, "E3997", {"start": v(-120.02, 255.16) * mm, "end": v(-119.61, 254.67) * mm});
            skLineSegment(sketch, "E3998", {"start": v(-119.61, 254.67) * mm, "end": v(-119.2, 254.16) * mm});
            skLineSegment(sketch, "E3999", {"start": v(-119.2, 254.16) * mm, "end": v(-118.8, 253.63) * mm});
            skLineSegment(sketch, "E4000", {"start": v(-118.8, 253.63) * mm, "end": v(-118.41, 253.08) * mm});
            skLineSegment(sketch, "E4001", {"start": v(-118.41, 253.08) * mm, "end": v(-118.02, 252.5) * mm});
            skLineSegment(sketch, "E4002", {"start": v(-118.02, 252.5) * mm, "end": v(-117.64, 251.92) * mm});
            skLineSegment(sketch, "E4003", {"start": v(-117.64, 251.92) * mm, "end": v(-117.26, 251.3) * mm});
            skLineSegment(sketch, "E4004", {"start": v(-117.26, 251.3) * mm, "end": v(-116.89, 250.68) * mm});
            skLineSegment(sketch, "E4005", {"start": v(-116.89, 250.68) * mm, "end": v(-116.52, 250.02) * mm});
            skLineSegment(sketch, "E4006", {"start": v(-116.52, 250.02) * mm, "end": v(-116.16, 249.35) * mm});
            skLineSegment(sketch, "E4007", {"start": v(-116.16, 249.35) * mm, "end": v(-115.8, 248.66) * mm});
            skLineSegment(sketch, "E4008", {"start": v(-115.8, 248.66) * mm, "end": v(-115.45, 247.94) * mm});
            skLineSegment(sketch, "E4009", {"start": v(-115.45, 247.94) * mm, "end": v(-115.1, 247.2) * mm});
            skLineSegment(sketch, "E4010", {"start": v(-115.1, 247.2) * mm, "end": v(-114.77, 246.45) * mm});
            skLineSegment(sketch, "E4011", {"start": v(-114.77, 246.45) * mm, "end": v(-114.44, 245.67) * mm});
            skLineSegment(sketch, "E4012", {"start": v(-114.44, 245.67) * mm, "end": v(-114.07, 244.8) * mm});
            skLineSegment(sketch, "E4013", {"start": v(-114.07, 244.8) * mm, "end": v(-113.72, 243.88) * mm});
            skLineSegment(sketch, "E4014", {"start": v(-113.72, 243.88) * mm, "end": v(-113.37, 242.94) * mm});
            skLineSegment(sketch, "E4015", {"start": v(-113.37, 242.94) * mm, "end": v(-113.04, 241.97) * mm});
            skLineSegment(sketch, "E4016", {"start": v(-113.04, 241.97) * mm, "end": v(-112.72, 240.97) * mm});
            skLineSegment(sketch, "E4017", {"start": v(-112.72, 240.97) * mm, "end": v(-112.4, 239.93) * mm});
            skLineSegment(sketch, "E4018", {"start": v(-112.4, 239.93) * mm, "end": v(-112.1, 238.87) * mm});
            skLineSegment(sketch, "E4019", {"start": v(-112.1, 238.87) * mm, "end": v(-111.81, 237.77) * mm});
            skLineSegment(sketch, "E4020", {"start": v(-111.81, 237.77) * mm, "end": v(-111.53, 236.65) * mm});
            skLineSegment(sketch, "E4021", {"start": v(-111.53, 236.65) * mm, "end": v(-111.26, 235.49) * mm});
            skLineSegment(sketch, "E4022", {"start": v(-111.26, 235.49) * mm, "end": v(-111, 234.3) * mm});
            skLineSegment(sketch, "E4023", {"start": v(-111, 234.3) * mm, "end": v(-110.75, 233.08) * mm});
            skLineSegment(sketch, "E4024", {"start": v(-110.75, 233.08) * mm, "end": v(-110.51, 231.83) * mm});
            skLineSegment(sketch, "E4025", {"start": v(-110.51, 231.83) * mm, "end": v(-110.28, 230.55) * mm});
            skLineSegment(sketch, "E4026", {"start": v(-110.28, 230.55) * mm, "end": v(-110.06, 229.24) * mm});
            skLineSegment(sketch, "E4027", {"start": v(-110.06, 229.24) * mm, "end": v(-109.86, 227.9) * mm});
            skLineSegment(sketch, "E4028", {"start": v(-109.86, 227.9) * mm, "end": v(-109.66, 226.54) * mm});
            skLineSegment(sketch, "E4029", {"start": v(-109.66, 226.54) * mm, "end": v(-109.48, 225.16) * mm});
            skLineSegment(sketch, "E4030", {"start": v(-109.48, 225.16) * mm, "end": v(-109.3, 223.77) * mm});
            skLineSegment(sketch, "E4031", {"start": v(-109.3, 223.77) * mm, "end": v(-109.15, 222.36) * mm});
            skLineSegment(sketch, "E4032", {"start": v(-109.15, 222.36) * mm, "end": v(-109, 220.94) * mm});
            skLineSegment(sketch, "E4033", {"start": v(-109, 220.94) * mm, "end": v(-108.87, 219.5) * mm});
            skLineSegment(sketch, "E4034", {"start": v(-108.87, 219.5) * mm, "end": v(-108.75, 218.06) * mm});
            skLineSegment(sketch, "E4035", {"start": v(-108.75, 218.06) * mm, "end": v(-108.64, 216.6) * mm});
            skLineSegment(sketch, "E4036", {"start": v(-108.64, 216.6) * mm, "end": v(-108.54, 215.12) * mm});
            skLineSegment(sketch, "E4037", {"start": v(-108.54, 215.12) * mm, "end": v(-108.46, 213.63) * mm});
            skLineSegment(sketch, "E4038", {"start": v(-108.46, 213.63) * mm, "end": v(-108.4, 212.13) * mm});
            skLineSegment(sketch, "E4039", {"start": v(-108.4, 212.13) * mm, "end": v(-108.34, 210.6) * mm});
            skLineSegment(sketch, "E4040", {"start": v(-108.34, 210.6) * mm, "end": v(-108.3, 209.07) * mm});
            skLineSegment(sketch, "E4041", {"start": v(-108.3, 209.07) * mm, "end": v(-108.26, 207.53) * mm});
            skLineSegment(sketch, "E4042", {"start": v(-108.26, 207.53) * mm, "end": v(-108.24, 205.97) * mm});
            skLineSegment(sketch, "E4043", {"start": v(-108.24, 205.97) * mm, "end": v(-108.23, 204.39) * mm});
            skLineSegment(sketch, "E4044", {"start": v(-108.23, 204.39) * mm, "end": v(-108.24, 202.7) * mm});
            skLineSegment(sketch, "E4045", {"start": v(-108.24, 202.7) * mm, "end": v(-108.27, 201.05) * mm});
            skLineSegment(sketch, "E4046", {"start": v(-108.27, 201.05) * mm, "end": v(-108.3, 199.42) * mm});
            skLineSegment(sketch, "E4047", {"start": v(-108.3, 199.42) * mm, "end": v(-108.36, 197.8) * mm});
            skLineSegment(sketch, "E4048", {"start": v(-108.36, 197.8) * mm, "end": v(-108.43, 196.21) * mm});
            skLineSegment(sketch, "E4049", {"start": v(-108.43, 196.21) * mm, "end": v(-108.51, 194.64) * mm});
            skLineSegment(sketch, "E4050", {"start": v(-108.51, 194.64) * mm, "end": v(-108.61, 193.1) * mm});
            skLineSegment(sketch, "E4051", {"start": v(-108.61, 193.1) * mm, "end": v(-108.73, 191.57) * mm});
            skLineSegment(sketch, "E4052", {"start": v(-108.73, 191.57) * mm, "end": v(-108.86, 190.07) * mm});
            skLineSegment(sketch, "E4053", {"start": v(-108.86, 190.07) * mm, "end": v(-109, 188.59) * mm});
            skLineSegment(sketch, "E4054", {"start": v(-109, 188.59) * mm, "end": v(-109.17, 187.13) * mm});
            skLineSegment(sketch, "E4055", {"start": v(-109.17, 187.13) * mm, "end": v(-109.34, 185.7) * mm});
            skLineSegment(sketch, "E4056", {"start": v(-109.34, 185.7) * mm, "end": v(-109.54, 184.28) * mm});
            skLineSegment(sketch, "E4057", {"start": v(-109.54, 184.28) * mm, "end": v(-109.74, 182.89) * mm});
            skLineSegment(sketch, "E4058", {"start": v(-109.74, 182.89) * mm, "end": v(-109.97, 181.52) * mm});
            skLineSegment(sketch, "E4059", {"start": v(-109.97, 181.52) * mm, "end": v(-110.2, 180.17) * mm});
            skLineSegment(sketch, "E4060", {"start": v(-110.2, 180.17) * mm, "end": v(-110.46, 178.84) * mm});
            skLineSegment(sketch, "E4061", {"start": v(-110.46, 178.84) * mm, "end": v(-110.73, 177.54) * mm});
            skLineSegment(sketch, "E4062", {"start": v(-110.73, 177.54) * mm, "end": v(-111.01, 176.26) * mm});
            skLineSegment(sketch, "E4063", {"start": v(-111.01, 176.26) * mm, "end": v(-111.31, 175) * mm});
            skLineSegment(sketch, "E4064", {"start": v(-111.31, 175) * mm, "end": v(-111.63, 173.76) * mm});
            skLineSegment(sketch, "E4065", {"start": v(-111.63, 173.76) * mm, "end": v(-111.96, 172.55) * mm});
            skLineSegment(sketch, "E4066", {"start": v(-111.96, 172.55) * mm, "end": v(-112.3, 171.35) * mm});
            skLineSegment(sketch, "E4067", {"start": v(-112.3, 171.35) * mm, "end": v(-112.67, 170.18) * mm});
            skLineSegment(sketch, "E4068", {"start": v(-112.67, 170.18) * mm, "end": v(-113.05, 169.03) * mm});
            skLineSegment(sketch, "E4069", {"start": v(-113.05, 169.03) * mm, "end": v(-113.44, 167.9) * mm});
            skLineSegment(sketch, "E4070", {"start": v(-113.44, 167.9) * mm, "end": v(-113.85, 166.8) * mm});
            skLineSegment(sketch, "E4071", {"start": v(-113.85, 166.8) * mm, "end": v(-114.27, 165.72) * mm});
            skLineSegment(sketch, "E4072", {"start": v(-114.27, 165.72) * mm, "end": v(-114.7, 164.66) * mm});
            skLineSegment(sketch, "E4073", {"start": v(-114.7, 164.66) * mm, "end": v(-115.16, 163.62) * mm});
            skLineSegment(sketch, "E4074", {"start": v(-115.16, 163.62) * mm, "end": v(-115.63, 162.6) * mm});
            skLineSegment(sketch, "E4075", {"start": v(-115.63, 162.6) * mm, "end": v(-116.12, 161.61) * mm});
            skLineSegment(sketch, "E4076", {"start": v(-116.12, 161.61) * mm, "end": v(-116.47, 160.93) * mm});
            skLineSegment(sketch, "E4077", {"start": v(-116.47, 160.93) * mm, "end": v(-116.82, 160.27) * mm});
            skLineSegment(sketch, "E4078", {"start": v(-116.82, 160.27) * mm, "end": v(-117.17, 159.63) * mm});
            skLineSegment(sketch, "E4079", {"start": v(-117.17, 159.63) * mm, "end": v(-117.53, 159.01) * mm});
            skLineSegment(sketch, "E4080", {"start": v(-117.53, 159.01) * mm, "end": v(-117.9, 158.41) * mm});
            skLineSegment(sketch, "E4081", {"start": v(-117.9, 158.41) * mm, "end": v(-118.26, 157.83) * mm});
            skLineSegment(sketch, "E4082", {"start": v(-118.26, 157.83) * mm, "end": v(-118.63, 157.27) * mm});
            skLineSegment(sketch, "E4083", {"start": v(-118.63, 157.27) * mm, "end": v(-119, 156.72) * mm});
            skLineSegment(sketch, "E4084", {"start": v(-119, 156.72) * mm, "end": v(-119.38, 156.2) * mm});
            skLineSegment(sketch, "E4085", {"start": v(-119.38, 156.2) * mm, "end": v(-119.77, 155.7) * mm});
            skLineSegment(sketch, "E4086", {"start": v(-119.77, 155.7) * mm, "end": v(-120.15, 155.21) * mm});
            skLineSegment(sketch, "E4087", {"start": v(-120.15, 155.21) * mm, "end": v(-120.54, 154.75) * mm});
            skLineSegment(sketch, "E4088", {"start": v(-120.54, 154.75) * mm, "end": v(-120.94, 154.3) * mm});
            skLineSegment(sketch, "E4089", {"start": v(-120.94, 154.3) * mm, "end": v(-121.33, 153.87) * mm});
            skLineSegment(sketch, "E4090", {"start": v(-121.33, 153.87) * mm, "end": v(-121.74, 153.47) * mm});
            skLineSegment(sketch, "E4091", {"start": v(-121.74, 153.47) * mm, "end": v(-122.14, 153.08) * mm});
            skLineSegment(sketch, "E4092", {"start": v(-122.14, 153.08) * mm, "end": v(-122.55, 152.71) * mm});
            skLineSegment(sketch, "E4093", {"start": v(-122.55, 152.71) * mm, "end": v(-122.96, 152.37) * mm});
            skLineSegment(sketch, "E4094", {"start": v(-122.96, 152.37) * mm, "end": v(-123.36, 152.05) * mm});
            skLineSegment(sketch, "E4095", {"start": v(-123.36, 152.05) * mm, "end": v(-123.77, 151.75) * mm});
            skLineSegment(sketch, "E4096", {"start": v(-123.77, 151.75) * mm, "end": v(-124.17, 151.48) * mm});
            skLineSegment(sketch, "E4097", {"start": v(-124.17, 151.48) * mm, "end": v(-124.57, 151.23) * mm});
            skLineSegment(sketch, "E4098", {"start": v(-124.57, 151.23) * mm, "end": v(-124.98, 151) * mm});
            skLineSegment(sketch, "E4099", {"start": v(-124.98, 151) * mm, "end": v(-125.38, 150.8) * mm});
            skLineSegment(sketch, "E4100", {"start": v(-125.38, 150.8) * mm, "end": v(-125.78, 150.63) * mm});
            skLineSegment(sketch, "E4101", {"start": v(-125.78, 150.63) * mm, "end": v(-126.18, 150.48) * mm});
            skLineSegment(sketch, "E4102", {"start": v(-126.18, 150.48) * mm, "end": v(-126.58, 150.35) * mm});
            skLineSegment(sketch, "E4103", {"start": v(-126.58, 150.35) * mm, "end": v(-126.98, 150.24) * mm});
            skLineSegment(sketch, "E4104", {"start": v(-126.98, 150.24) * mm, "end": v(-127.38, 150.16) * mm});
            skLineSegment(sketch, "E4105", {"start": v(-127.38, 150.16) * mm, "end": v(-127.77, 150.1) * mm});
            skLineSegment(sketch, "E4106", {"start": v(-127.77, 150.1) * mm, "end": v(-128.17, 150.06) * mm});
            skLineSegment(sketch, "E4107", {"start": v(-128.17, 150.06) * mm, "end": v(-128.57, 150.05) * mm});
            skLineSegment(sketch, "E4108", {"start": v(-131.57, 158) * mm, "end": v(-131.57, 150.05) * mm});
            skLineSegment(sketch, "E4109", {"start": v(-131.57, 150.05) * mm, "end": v(-132.06, 150.06) * mm});
            skLineSegment(sketch, "E4110", {"start": v(-132.06, 150.06) * mm, "end": v(-132.56, 150.1) * mm});
            skLineSegment(sketch, "E4111", {"start": v(-132.56, 150.1) * mm, "end": v(-133.06, 150.18) * mm});
            skLineSegment(sketch, "E4112", {"start": v(-133.06, 150.18) * mm, "end": v(-133.56, 150.29) * mm});
            skLineSegment(sketch, "E4113", {"start": v(-133.56, 150.29) * mm, "end": v(-134.06, 150.42) * mm});
            skLineSegment(sketch, "E4114", {"start": v(-134.06, 150.42) * mm, "end": v(-134.56, 150.58) * mm});
            skLineSegment(sketch, "E4115", {"start": v(-134.56, 150.58) * mm, "end": v(-135.06, 150.77) * mm});
            skLineSegment(sketch, "E4116", {"start": v(-135.06, 150.77) * mm, "end": v(-135.56, 151) * mm});
            skLineSegment(sketch, "E4117", {"start": v(-135.56, 151) * mm, "end": v(-136.06, 151.24) * mm});
            skLineSegment(sketch, "E4118", {"start": v(-136.06, 151.24) * mm, "end": v(-136.57, 151.52) * mm});
            skLineSegment(sketch, "E4119", {"start": v(-136.57, 151.52) * mm, "end": v(-137.07, 151.83) * mm});
            skLineSegment(sketch, "E4120", {"start": v(-137.07, 151.83) * mm, "end": v(-137.58, 152.17) * mm});
            skLineSegment(sketch, "E4121", {"start": v(-137.58, 152.17) * mm, "end": v(-138.09, 152.54) * mm});
            skLineSegment(sketch, "E4122", {"start": v(-138.09, 152.54) * mm, "end": v(-138.6, 152.94) * mm});
            skLineSegment(sketch, "E4123", {"start": v(-138.6, 152.94) * mm, "end": v(-139.1, 153.37) * mm});
            skLineSegment(sketch, "E4124", {"start": v(-139.1, 153.37) * mm, "end": v(-139.61, 153.82) * mm});
            skLineSegment(sketch, "E4125", {"start": v(-139.61, 153.82) * mm, "end": v(-140.04, 154.24) * mm});
            skLineSegment(sketch, "E4126", {"start": v(-140.04, 154.24) * mm, "end": v(-140.45, 154.66) * mm});
            skLineSegment(sketch, "E4127", {"start": v(-140.45, 154.66) * mm, "end": v(-140.85, 155.1) * mm});
            skLineSegment(sketch, "E4128", {"start": v(-140.85, 155.1) * mm, "end": v(-141.24, 155.56) * mm});
            skLineSegment(sketch, "E4129", {"start": v(-141.24, 155.56) * mm, "end": v(-141.62, 156.03) * mm});
            skLineSegment(sketch, "E4130", {"start": v(-141.62, 156.03) * mm, "end": v(-141.98, 156.51) * mm});
            skLineSegment(sketch, "E4131", {"start": v(-141.98, 156.51) * mm, "end": v(-142.34, 157.01) * mm});
            skLineSegment(sketch, "E4132", {"start": v(-142.34, 157.01) * mm, "end": v(-142.68, 157.53) * mm});
            skLineSegment(sketch, "E4133", {"start": v(-142.68, 157.53) * mm, "end": v(-143.01, 158.06) * mm});
            skLineSegment(sketch, "E4134", {"start": v(-143.01, 158.06) * mm, "end": v(-143.33, 158.6) * mm});
            skLineSegment(sketch, "E4135", {"start": v(-143.33, 158.6) * mm, "end": v(-143.64, 159.17) * mm});
            skLineSegment(sketch, "E4136", {"start": v(-143.64, 159.17) * mm, "end": v(-143.93, 159.74) * mm});
            skLineSegment(sketch, "E4137", {"start": v(-143.93, 159.74) * mm, "end": v(-144.22, 160.34) * mm});
            skLineSegment(sketch, "E4138", {"start": v(-144.22, 160.34) * mm, "end": v(-144.49, 160.94) * mm});
            skLineSegment(sketch, "E4139", {"start": v(-144.49, 160.94) * mm, "end": v(-144.75, 161.56) * mm});
            skLineSegment(sketch, "E4140", {"start": v(-144.75, 161.56) * mm, "end": v(-145, 162.2) * mm});
            skLineSegment(sketch, "E4141", {"start": v(-145, 162.2) * mm, "end": v(-145.23, 162.85) * mm});
            skLineSegment(sketch, "E4142", {"start": v(-145.23, 162.85) * mm, "end": v(-145.45, 163.5) * mm});
            skLineSegment(sketch, "E4143", {"start": v(-145.45, 163.5) * mm, "end": v(-145.66, 164.16) * mm});
            skLineSegment(sketch, "E4144", {"start": v(-145.66, 164.16) * mm, "end": v(-145.85, 164.83) * mm});
            skLineSegment(sketch, "E4145", {"start": v(-145.85, 164.83) * mm, "end": v(-146.02, 165.5) * mm});
            skLineSegment(sketch, "E4146", {"start": v(-146.02, 165.5) * mm, "end": v(-146.18, 166.18) * mm});
            skLineSegment(sketch, "E4147", {"start": v(-146.18, 166.18) * mm, "end": v(-146.32, 166.86) * mm});
            skLineSegment(sketch, "E4148", {"start": v(-146.32, 166.86) * mm, "end": v(-146.45, 167.56) * mm});
            skLineSegment(sketch, "E4149", {"start": v(-146.45, 167.56) * mm, "end": v(-146.57, 168.26) * mm});
            skLineSegment(sketch, "E4150", {"start": v(-146.57, 168.26) * mm, "end": v(-146.66, 168.96) * mm});
            skLineSegment(sketch, "E4151", {"start": v(-146.66, 168.96) * mm, "end": v(-146.75, 169.67) * mm});
            skLineSegment(sketch, "E4152", {"start": v(-146.75, 169.67) * mm, "end": v(-146.82, 170.4) * mm});
            skLineSegment(sketch, "E4153", {"start": v(-146.82, 170.4) * mm, "end": v(-146.87, 171.12) * mm});
            skLineSegment(sketch, "E4154", {"start": v(-146.87, 171.12) * mm, "end": v(-146.9, 171.85) * mm});
            skLineSegment(sketch, "E4155", {"start": v(-146.9, 171.85) * mm, "end": v(-146.93, 172.58) * mm});
            skLineSegment(sketch, "E4156", {"start": v(-146.93, 172.58) * mm, "end": v(-146.94, 173.33) * mm});
            skLineSegment(sketch, "E4157", {"start": v(-146.94, 173.33) * mm, "end": v(-146.93, 174.13) * mm});
            skLineSegment(sketch, "E4158", {"start": v(-146.93, 174.13) * mm, "end": v(-146.9, 174.93) * mm});
            skLineSegment(sketch, "E4159", {"start": v(-146.9, 174.93) * mm, "end": v(-146.86, 175.7) * mm});
            skLineSegment(sketch, "E4160", {"start": v(-146.86, 175.7) * mm, "end": v(-146.8, 176.46) * mm});
            skLineSegment(sketch, "E4161", {"start": v(-146.8, 176.46) * mm, "end": v(-146.72, 177.2) * mm});
            skLineSegment(sketch, "E4162", {"start": v(-146.72, 177.2) * mm, "end": v(-146.62, 177.92) * mm});
            skLineSegment(sketch, "E4163", {"start": v(-146.62, 177.92) * mm, "end": v(-146.5, 178.63) * mm});
            skLineSegment(sketch, "E4164", {"start": v(-146.5, 178.63) * mm, "end": v(-146.38, 179.32) * mm});
            skLineSegment(sketch, "E4165", {"start": v(-146.38, 179.32) * mm, "end": v(-146.23, 180) * mm});
            skLineSegment(sketch, "E4166", {"start": v(-146.23, 180) * mm, "end": v(-146.06, 180.66) * mm});
            skLineSegment(sketch, "E4167", {"start": v(-146.06, 180.66) * mm, "end": v(-145.88, 181.3) * mm});
            skLineSegment(sketch, "E4168", {"start": v(-145.88, 181.3) * mm, "end": v(-145.68, 181.92) * mm});
            skLineSegment(sketch, "E4169", {"start": v(-145.68, 181.92) * mm, "end": v(-145.46, 182.53) * mm});
            skLineSegment(sketch, "E4170", {"start": v(-145.46, 182.53) * mm, "end": v(-145.22, 183.12) * mm});
            skLineSegment(sketch, "E4171", {"start": v(-145.22, 183.12) * mm, "end": v(-144.97, 183.7) * mm});
            skLineSegment(sketch, "E4172", {"start": v(-144.97, 183.7) * mm, "end": v(-144.7, 184.26) * mm});
            skLineSegment(sketch, "E4173", {"start": v(-144.7, 184.26) * mm, "end": v(-144.41, 184.8) * mm});
            skLineSegment(sketch, "E4174", {"start": v(-144.41, 184.8) * mm, "end": v(-144.12, 185.3) * mm});
            skLineSegment(sketch, "E4175", {"start": v(-144.12, 185.3) * mm, "end": v(-143.82, 185.75) * mm});
            skLineSegment(sketch, "E4176", {"start": v(-143.82, 185.75) * mm, "end": v(-143.5, 186.18) * mm});
            skLineSegment(sketch, "E4177", {"start": v(-143.5, 186.18) * mm, "end": v(-143.19, 186.58) * mm});
            skLineSegment(sketch, "E4178", {"start": v(-143.19, 186.58) * mm, "end": v(-142.86, 186.94) * mm});
            skLineSegment(sketch, "E4179", {"start": v(-142.86, 186.94) * mm, "end": v(-142.7, 187.1) * mm});
            skLineSegment(sketch, "E4180", {"start": v(-142.7, 187.1) * mm, "end": v(-142.52, 187.27) * mm});
            skLineSegment(sketch, "E4181", {"start": v(-142.52, 187.27) * mm, "end": v(-142.35, 187.42) * mm});
            skLineSegment(sketch, "E4182", {"start": v(-142.35, 187.42) * mm, "end": v(-142.17, 187.56) * mm});
            skLineSegment(sketch, "E4183", {"start": v(-142.17, 187.56) * mm, "end": v(-142, 187.7) * mm});
            skLineSegment(sketch, "E4184", {"start": v(-142, 187.7) * mm, "end": v(-141.82, 187.82) * mm});
            skLineSegment(sketch, "E4185", {"start": v(-141.82, 187.82) * mm, "end": v(-141.64, 187.94) * mm});
            skLineSegment(sketch, "E4186", {"start": v(-141.64, 187.94) * mm, "end": v(-141.46, 188.04) * mm});
            skLineSegment(sketch, "E4187", {"start": v(-141.46, 188.04) * mm, "end": v(-141.27, 188.14) * mm});
            skLineSegment(sketch, "E4188", {"start": v(-141.27, 188.14) * mm, "end": v(-141.08, 188.23) * mm});
            skLineSegment(sketch, "E4189", {"start": v(-141.08, 188.23) * mm, "end": v(-140.9, 188.31) * mm});
            skLineSegment(sketch, "E4190", {"start": v(-140.9, 188.31) * mm, "end": v(-140.7, 188.39) * mm});
            skLineSegment(sketch, "E4191", {"start": v(-140.7, 188.39) * mm, "end": v(-140.51, 188.45) * mm});
            skLineSegment(sketch, "E4192", {"start": v(-140.51, 188.45) * mm, "end": v(-140.31, 188.5) * mm});
            skLineSegment(sketch, "E4193", {"start": v(-140.31, 188.5) * mm, "end": v(-140.12, 188.55) * mm});
            skLineSegment(sketch, "E4194", {"start": v(-140.12, 188.55) * mm, "end": v(-139.92, 188.6) * mm});
            skLineSegment(sketch, "E4195", {"start": v(-139.92, 188.6) * mm, "end": v(-139.71, 188.62) * mm});
            skLineSegment(sketch, "E4196", {"start": v(-139.71, 188.62) * mm, "end": v(-139.5, 188.64) * mm});
            skLineSegment(sketch, "E4197", {"start": v(-139.5, 188.64) * mm, "end": v(-139.3, 188.66) * mm});
            skLineSegment(sketch, "E4198", {"start": v(-139.3, 188.66) * mm, "end": v(-139.1, 188.66) * mm});
            skLineSegment(sketch, "E4199", {"start": v(-139.1, 188.66) * mm, "end": v(-138.73, 188.65) * mm});
            skLineSegment(sketch, "E4200", {"start": v(-138.73, 188.65) * mm, "end": v(-138.37, 188.6) * mm});
            skLineSegment(sketch, "E4201", {"start": v(-138.37, 188.6) * mm, "end": v(-138.19, 188.57) * mm});
            skLineSegment(sketch, "E4202", {"start": v(-138.19, 188.57) * mm, "end": v(-138.01, 188.53) * mm});
            skLineSegment(sketch, "E4203", {"start": v(-138.01, 188.53) * mm, "end": v(-137.67, 188.42) * mm});
            skLineSegment(sketch, "E4204", {"start": v(-137.67, 188.42) * mm, "end": v(-137.33, 188.29) * mm});
            skLineSegment(sketch, "E4205", {"start": v(-137.33, 188.29) * mm, "end": v(-137, 188.13) * mm});
            skLineSegment(sketch, "E4206", {"start": v(-137, 188.13) * mm, "end": v(-136.67, 187.93) * mm});
            skLineSegment(sketch, "E4207", {"start": v(-136.67, 187.93) * mm, "end": v(-136.35, 187.7) * mm});
            skLineSegment(sketch, "E4208", {"start": v(-136.35, 187.7) * mm, "end": v(-136.03, 187.46) * mm});
            skLineSegment(sketch, "E4209", {"start": v(-136.03, 187.46) * mm, "end": v(-135.73, 187.17) * mm});
            skLineSegment(sketch, "E4210", {"start": v(-135.73, 187.17) * mm, "end": v(-135.43, 186.86) * mm});
            skLineSegment(sketch, "E4211", {"start": v(-135.43, 186.86) * mm, "end": v(-135.13, 186.52) * mm});
            skLineSegment(sketch, "E4212", {"start": v(-135.13, 186.52) * mm, "end": v(-134.85, 186.14) * mm});
            skLineSegment(sketch, "E4213", {"start": v(-134.85, 186.14) * mm, "end": v(-134.57, 185.74) * mm});
            skLineSegment(sketch, "E4214", {"start": v(-134.57, 185.74) * mm, "end": v(-134.3, 185.3) * mm});
            skLineSegment(sketch, "E4215", {"start": v(-134.3, 185.3) * mm, "end": v(-134.03, 184.85) * mm});
            skLineSegment(sketch, "E4216", {"start": v(-134.03, 184.85) * mm, "end": v(-133.78, 184.36) * mm});
            skLineSegment(sketch, "E4217", {"start": v(-133.78, 184.36) * mm, "end": v(-133.54, 183.87) * mm});
            skLineSegment(sketch, "E4218", {"start": v(-133.54, 183.87) * mm, "end": v(-133.32, 183.36) * mm});
            skLineSegment(sketch, "E4219", {"start": v(-133.32, 183.36) * mm, "end": v(-133.11, 182.84) * mm});
            skLineSegment(sketch, "E4220", {"start": v(-133.11, 182.84) * mm, "end": v(-132.92, 182.3) * mm});
            skLineSegment(sketch, "E4221", {"start": v(-132.92, 182.3) * mm, "end": v(-132.75, 181.76) * mm});
            skLineSegment(sketch, "E4222", {"start": v(-132.75, 181.76) * mm, "end": v(-132.6, 181.2) * mm});
            skLineSegment(sketch, "E4223", {"start": v(-132.6, 181.2) * mm, "end": v(-132.45, 180.63) * mm});
            skLineSegment(sketch, "E4224", {"start": v(-132.45, 180.63) * mm, "end": v(-132.33, 180.05) * mm});
            skLineSegment(sketch, "E4225", {"start": v(-132.33, 180.05) * mm, "end": v(-132.22, 179.45) * mm});
            skLineSegment(sketch, "E4226", {"start": v(-132.22, 179.45) * mm, "end": v(-132.13, 178.84) * mm});
            skLineSegment(sketch, "E4227", {"start": v(-132.13, 178.84) * mm, "end": v(-132.06, 178.22) * mm});
            skLineSegment(sketch, "E4228", {"start": v(-132.06, 178.22) * mm, "end": v(-132, 177.59) * mm});
            skLineSegment(sketch, "E4229", {"start": v(-132, 177.59) * mm, "end": v(-131.96, 176.94) * mm});
            skLineSegment(sketch, "E4230", {"start": v(-131.96, 176.94) * mm, "end": v(-131.94, 176.28) * mm});
            skLineSegment(sketch, "E4231", {"start": v(-131.94, 176.28) * mm, "end": v(-131.93, 175.6) * mm});
            skLineSegment(sketch, "E4232", {"start": v(-131.93, 175.6) * mm, "end": v(-131.94, 174.7) * mm});
            skLineSegment(sketch, "E4233", {"start": v(-131.94, 174.7) * mm, "end": v(-131.99, 173.83) * mm});
            skLineSegment(sketch, "E4234", {"start": v(-131.99, 173.83) * mm, "end": v(-132.02, 173.4) * mm});
            skLineSegment(sketch, "E4235", {"start": v(-132.02, 173.4) * mm, "end": v(-132.06, 173) * mm});
            skLineSegment(sketch, "E4236", {"start": v(-132.06, 173) * mm, "end": v(-132.1, 172.58) * mm});
            skLineSegment(sketch, "E4237", {"start": v(-132.1, 172.58) * mm, "end": v(-132.16, 172.19) * mm});
            skLineSegment(sketch, "E4238", {"start": v(-132.16, 172.19) * mm, "end": v(-132.22, 171.8) * mm});
            skLineSegment(sketch, "E4239", {"start": v(-132.22, 171.8) * mm, "end": v(-132.29, 171.42) * mm});
            skLineSegment(sketch, "E4240", {"start": v(-132.29, 171.42) * mm, "end": v(-132.36, 171.05) * mm});
            skLineSegment(sketch, "E4241", {"start": v(-132.36, 171.05) * mm, "end": v(-132.45, 170.68) * mm});
            skLineSegment(sketch, "E4242", {"start": v(-132.45, 170.68) * mm, "end": v(-132.54, 170.33) * mm});
            skLineSegment(sketch, "E4243", {"start": v(-132.54, 170.33) * mm, "end": v(-132.63, 169.98) * mm});
            skLineSegment(sketch, "E4244", {"start": v(-132.63, 169.98) * mm, "end": v(-132.74, 169.65) * mm});
            skLineSegment(sketch, "E4245", {"start": v(-132.74, 169.65) * mm, "end": v(-132.85, 169.32) * mm});
            skLineSegment(sketch, "E4246", {"start": v(-132.85, 169.32) * mm, "end": v(-134.13, 165.7) * mm});
            skLineSegment(sketch, "E4247", {"start": v(-134.13, 165.7) * mm, "end": v(-134.25, 165.35) * mm});
            skLineSegment(sketch, "E4248", {"start": v(-134.25, 165.35) * mm, "end": v(-134.36, 165) * mm});
            skLineSegment(sketch, "E4249", {"start": v(-134.36, 165) * mm, "end": v(-134.45, 164.65) * mm});
            skLineSegment(sketch, "E4250", {"start": v(-134.45, 164.65) * mm, "end": v(-134.52, 164.3) * mm});
            skLineSegment(sketch, "E4251", {"start": v(-134.52, 164.3) * mm, "end": v(-134.58, 163.96) * mm});
            skLineSegment(sketch, "E4252", {"start": v(-134.58, 163.96) * mm, "end": v(-134.62, 163.62) * mm});
            skLineSegment(sketch, "E4253", {"start": v(-134.62, 163.62) * mm, "end": v(-134.64, 163.28) * mm});
            skLineSegment(sketch, "E4254", {"start": v(-134.64, 163.28) * mm, "end": v(-134.65, 162.95) * mm});
            skLineSegment(sketch, "E4255", {"start": v(-134.65, 162.95) * mm, "end": v(-134.65, 162.66) * mm});
            skLineSegment(sketch, "E4256", {"start": v(-134.65, 162.66) * mm, "end": v(-134.63, 162.39) * mm});
            skLineSegment(sketch, "E4257", {"start": v(-134.63, 162.39) * mm, "end": v(-134.6, 162.11) * mm});
            skLineSegment(sketch, "E4258", {"start": v(-134.6, 162.11) * mm, "end": v(-134.57, 161.85) * mm});
            skLineSegment(sketch, "E4259", {"start": v(-134.57, 161.85) * mm, "end": v(-134.53, 161.58) * mm});
            skLineSegment(sketch, "E4260", {"start": v(-134.53, 161.58) * mm, "end": v(-134.48, 161.33) * mm});
            skLineSegment(sketch, "E4261", {"start": v(-134.48, 161.33) * mm, "end": v(-134.41, 161.07) * mm});
            skLineSegment(sketch, "E4262", {"start": v(-134.41, 161.07) * mm, "end": v(-134.34, 160.82) * mm});
            skLineSegment(sketch, "E4263", {"start": v(-134.34, 160.82) * mm, "end": v(-134.26, 160.58) * mm});
            skLineSegment(sketch, "E4264", {"start": v(-134.26, 160.58) * mm, "end": v(-134.17, 160.34) * mm});
            skLineSegment(sketch, "E4265", {"start": v(-134.17, 160.34) * mm, "end": v(-134.06, 160.1) * mm});
            skLineSegment(sketch, "E4266", {"start": v(-134.06, 160.1) * mm, "end": v(-133.95, 159.88) * mm});
            skLineSegment(sketch, "E4267", {"start": v(-133.95, 159.88) * mm, "end": v(-133.83, 159.66) * mm});
            skLineSegment(sketch, "E4268", {"start": v(-133.83, 159.66) * mm, "end": v(-133.7, 159.44) * mm});
            skLineSegment(sketch, "E4269", {"start": v(-133.7, 159.44) * mm, "end": v(-133.56, 159.22) * mm});
            skLineSegment(sketch, "E4270", {"start": v(-133.56, 159.22) * mm, "end": v(-133.4, 159.01) * mm});
            skLineSegment(sketch, "E4271", {"start": v(-133.4, 159.01) * mm, "end": v(-133.25, 158.83) * mm});
            skLineSegment(sketch, "E4272", {"start": v(-133.25, 158.83) * mm, "end": v(-133.07, 158.66) * mm});
            skLineSegment(sketch, "E4273", {"start": v(-133.07, 158.66) * mm, "end": v(-132.87, 158.5) * mm});
            skLineSegment(sketch, "E4274", {"start": v(-132.87, 158.5) * mm, "end": v(-132.65, 158.37) * mm});
            skLineSegment(sketch, "E4275", {"start": v(-132.65, 158.37) * mm, "end": v(-132.4, 158.25) * mm});
            skLineSegment(sketch, "E4276", {"start": v(-132.4, 158.25) * mm, "end": v(-132.15, 158.15) * mm});
            skLineSegment(sketch, "E4277", {"start": v(-132.15, 158.15) * mm, "end": v(-131.87, 158.06) * mm});
            skLineSegment(sketch, "E4278", {"start": v(-131.87, 158.06) * mm, "end": v(-131.57, 158) * mm});
            skLineSegment(sketch, "E4279", {"start": v(-127.65, 209.58) * mm, "end": v(-127.65, 200.54) * mm});
            skLineSegment(sketch, "E4280", {"start": v(-127.65, 200.54) * mm, "end": v(-128.2, 199.96) * mm});
            skLineSegment(sketch, "E4281", {"start": v(-128.2, 199.96) * mm, "end": v(-128.73, 199.43) * mm});
            skLineSegment(sketch, "E4282", {"start": v(-128.73, 199.43) * mm, "end": v(-129.27, 198.93) * mm});
            skLineSegment(sketch, "E4283", {"start": v(-129.27, 198.93) * mm, "end": v(-129.8, 198.47) * mm});
            skLineSegment(sketch, "E4284", {"start": v(-129.8, 198.47) * mm, "end": v(-130.35, 198.05) * mm});
            skLineSegment(sketch, "E4285", {"start": v(-130.35, 198.05) * mm, "end": v(-130.88, 197.66) * mm});
            skLineSegment(sketch, "E4286", {"start": v(-130.88, 197.66) * mm, "end": v(-131.4, 197.31) * mm});
            skLineSegment(sketch, "E4287", {"start": v(-131.4, 197.31) * mm, "end": v(-131.67, 197.15) * mm});
            skLineSegment(sketch, "E4288", {"start": v(-131.67, 197.15) * mm, "end": v(-131.94, 197) * mm});
            skLineSegment(sketch, "E4289", {"start": v(-131.94, 197) * mm, "end": v(-132.2, 196.85) * mm});
            skLineSegment(sketch, "E4290", {"start": v(-132.2, 196.85) * mm, "end": v(-132.47, 196.72) * mm});
            skLineSegment(sketch, "E4291", {"start": v(-132.47, 196.72) * mm, "end": v(-132.73, 196.6) * mm});
            skLineSegment(sketch, "E4292", {"start": v(-132.73, 196.6) * mm, "end": v(-132.99, 196.48) * mm});
            skLineSegment(sketch, "E4293", {"start": v(-132.99, 196.48) * mm, "end": v(-133.25, 196.38) * mm});
            skLineSegment(sketch, "E4294", {"start": v(-133.25, 196.38) * mm, "end": v(-133.51, 196.28) * mm});
            skLineSegment(sketch, "E4295", {"start": v(-133.51, 196.28) * mm, "end": v(-133.77, 196.2) * mm});
            skLineSegment(sketch, "E4296", {"start": v(-133.77, 196.2) * mm, "end": v(-134.03, 196.11) * mm});
            skLineSegment(sketch, "E4297", {"start": v(-134.03, 196.11) * mm, "end": v(-134.3, 196.04) * mm});
            skLineSegment(sketch, "E4298", {"start": v(-134.3, 196.04) * mm, "end": v(-134.55, 195.98) * mm});
            skLineSegment(sketch, "E4299", {"start": v(-134.55, 195.98) * mm, "end": v(-134.8, 195.93) * mm});
            skLineSegment(sketch, "E4300", {"start": v(-134.8, 195.93) * mm, "end": v(-135.07, 195.9) * mm});
            skLineSegment(sketch, "E4301", {"start": v(-135.07, 195.9) * mm, "end": v(-135.32, 195.86) * mm});
            skLineSegment(sketch, "E4302", {"start": v(-135.32, 195.86) * mm, "end": v(-135.58, 195.84) * mm});
            skLineSegment(sketch, "E4303", {"start": v(-135.58, 195.84) * mm, "end": v(-135.84, 195.82) * mm});
            skLineSegment(sketch, "E4304", {"start": v(-135.84, 195.82) * mm, "end": v(-136.1, 195.82) * mm});
            skLineSegment(sketch, "E4305", {"start": v(-136.1, 195.82) * mm, "end": v(-136.4, 195.83) * mm});
            skLineSegment(sketch, "E4306", {"start": v(-136.4, 195.83) * mm, "end": v(-136.71, 195.85) * mm});
            skLineSegment(sketch, "E4307", {"start": v(-136.71, 195.85) * mm, "end": v(-137.02, 195.88) * mm});
            skLineSegment(sketch, "E4308", {"start": v(-137.02, 195.88) * mm, "end": v(-137.33, 195.94) * mm});
            skLineSegment(sketch, "E4309", {"start": v(-137.33, 195.94) * mm, "end": v(-137.64, 196) * mm});
            skLineSegment(sketch, "E4310", {"start": v(-137.64, 196) * mm, "end": v(-137.95, 196.08) * mm});
            skLineSegment(sketch, "E4311", {"start": v(-137.95, 196.08) * mm, "end": v(-138.27, 196.18) * mm});
            skLineSegment(sketch, "E4312", {"start": v(-138.27, 196.18) * mm, "end": v(-138.58, 196.29) * mm});
            skLineSegment(sketch, "E4313", {"start": v(-138.58, 196.29) * mm, "end": v(-138.89, 196.42) * mm});
            skLineSegment(sketch, "E4314", {"start": v(-138.89, 196.42) * mm, "end": v(-139.2, 196.56) * mm});
            skLineSegment(sketch, "E4315", {"start": v(-139.2, 196.56) * mm, "end": v(-139.51, 196.7) * mm});
            skLineSegment(sketch, "E4316", {"start": v(-139.51, 196.7) * mm, "end": v(-139.82, 196.88) * mm});
            skLineSegment(sketch, "E4317", {"start": v(-139.82, 196.88) * mm, "end": v(-140.14, 197.06) * mm});
            skLineSegment(sketch, "E4318", {"start": v(-140.14, 197.06) * mm, "end": v(-140.45, 197.26) * mm});
            skLineSegment(sketch, "E4319", {"start": v(-140.45, 197.26) * mm, "end": v(-140.76, 197.48) * mm});
            skLineSegment(sketch, "E4320", {"start": v(-140.76, 197.48) * mm, "end": v(-141.07, 197.7) * mm});
            skLineSegment(sketch, "E4321", {"start": v(-141.07, 197.7) * mm, "end": v(-141.38, 197.95) * mm});
            skLineSegment(sketch, "E4322", {"start": v(-141.38, 197.95) * mm, "end": v(-141.69, 198.2) * mm});
            skLineSegment(sketch, "E4323", {"start": v(-141.69, 198.2) * mm, "end": v(-142, 198.46) * mm});
            skLineSegment(sketch, "E4324", {"start": v(-142, 198.46) * mm, "end": v(-142.29, 198.74) * mm});
            skLineSegment(sketch, "E4325", {"start": v(-142.29, 198.74) * mm, "end": v(-142.58, 199.02) * mm});
            skLineSegment(sketch, "E4326", {"start": v(-142.58, 199.02) * mm, "end": v(-142.86, 199.32) * mm});
            skLineSegment(sketch, "E4327", {"start": v(-142.86, 199.32) * mm, "end": v(-143.14, 199.63) * mm});
            skLineSegment(sketch, "E4328", {"start": v(-143.14, 199.63) * mm, "end": v(-143.42, 199.95) * mm});
            skLineSegment(sketch, "E4329", {"start": v(-143.42, 199.95) * mm, "end": v(-143.7, 200.28) * mm});
            skLineSegment(sketch, "E4330", {"start": v(-143.7, 200.28) * mm, "end": v(-143.96, 200.62) * mm});
            skLineSegment(sketch, "E4331", {"start": v(-143.96, 200.62) * mm, "end": v(-144.22, 200.97) * mm});
            skLineSegment(sketch, "E4332", {"start": v(-144.22, 200.97) * mm, "end": v(-144.48, 201.33) * mm});
            skLineSegment(sketch, "E4333", {"start": v(-144.48, 201.33) * mm, "end": v(-144.73, 201.7) * mm});
            skLineSegment(sketch, "E4334", {"start": v(-144.73, 201.7) * mm, "end": v(-144.98, 202.1) * mm});
            skLineSegment(sketch, "E4335", {"start": v(-144.98, 202.1) * mm, "end": v(-145.22, 202.49) * mm});
            skLineSegment(sketch, "E4336", {"start": v(-145.22, 202.49) * mm, "end": v(-145.46, 202.9) * mm});
            skLineSegment(sketch, "E4337", {"start": v(-145.46, 202.9) * mm, "end": v(-145.71, 203.37) * mm});
            skLineSegment(sketch, "E4338", {"start": v(-145.71, 203.37) * mm, "end": v(-145.96, 203.86) * mm});
            skLineSegment(sketch, "E4339", {"start": v(-145.96, 203.86) * mm, "end": v(-146.2, 204.37) * mm});
            skLineSegment(sketch, "E4340", {"start": v(-146.2, 204.37) * mm, "end": v(-146.44, 204.88) * mm});
            skLineSegment(sketch, "E4341", {"start": v(-146.44, 204.88) * mm, "end": v(-146.67, 205.41) * mm});
            skLineSegment(sketch, "E4342", {"start": v(-146.67, 205.41) * mm, "end": v(-146.89, 205.95) * mm});
            skLineSegment(sketch, "E4343", {"start": v(-146.89, 205.95) * mm, "end": v(-147.1, 206.5) * mm});
            skLineSegment(sketch, "E4344", {"start": v(-147.1, 206.5) * mm, "end": v(-147.3, 207.07) * mm});
            skLineSegment(sketch, "E4345", {"start": v(-147.3, 207.07) * mm, "end": v(-147.5, 207.65) * mm});
            skLineSegment(sketch, "E4346", {"start": v(-147.5, 207.65) * mm, "end": v(-147.7, 208.24) * mm});
            skLineSegment(sketch, "E4347", {"start": v(-147.7, 208.24) * mm, "end": v(-147.88, 208.85) * mm});
            skLineSegment(sketch, "E4348", {"start": v(-147.88, 208.85) * mm, "end": v(-148.06, 209.46) * mm});
            skLineSegment(sketch, "E4349", {"start": v(-148.06, 209.46) * mm, "end": v(-148.23, 210.1) * mm});
            skLineSegment(sketch, "E4350", {"start": v(-148.23, 210.1) * mm, "end": v(-148.4, 210.74) * mm});
            skLineSegment(sketch, "E4351", {"start": v(-148.4, 210.74) * mm, "end": v(-148.55, 211.39) * mm});
            skLineSegment(sketch, "E4352", {"start": v(-148.55, 211.39) * mm, "end": v(-148.7, 212.06) * mm});
            skLineSegment(sketch, "E4353", {"start": v(-148.7, 212.06) * mm, "end": v(-148.84, 212.73) * mm});
            skLineSegment(sketch, "E4354", {"start": v(-148.84, 212.73) * mm, "end": v(-148.97, 213.42) * mm});
            skLineSegment(sketch, "E4355", {"start": v(-148.97, 213.42) * mm, "end": v(-149.1, 214.1) * mm});
            skLineSegment(sketch, "E4356", {"start": v(-149.1, 214.1) * mm, "end": v(-149.2, 214.8) * mm});
            skLineSegment(sketch, "E4357", {"start": v(-149.2, 214.8) * mm, "end": v(-149.31, 215.5) * mm});
            skLineSegment(sketch, "E4358", {"start": v(-149.31, 215.5) * mm, "end": v(-149.4, 216.2) * mm});
            skLineSegment(sketch, "E4359", {"start": v(-149.4, 216.2) * mm, "end": v(-149.5, 216.91) * mm});
            skLineSegment(sketch, "E4360", {"start": v(-149.5, 216.91) * mm, "end": v(-149.57, 217.63) * mm});
            skLineSegment(sketch, "E4361", {"start": v(-149.57, 217.63) * mm, "end": v(-149.64, 218.35) * mm});
            skLineSegment(sketch, "E4362", {"start": v(-149.64, 218.35) * mm, "end": v(-149.7, 219.08) * mm});
            skLineSegment(sketch, "E4363", {"start": v(-149.7, 219.08) * mm, "end": v(-149.75, 219.82) * mm});
            skLineSegment(sketch, "E4364", {"start": v(-149.75, 219.82) * mm, "end": v(-149.79, 220.56) * mm});
            skLineSegment(sketch, "E4365", {"start": v(-149.79, 220.56) * mm, "end": v(-149.82, 221.3) * mm});
            skLineSegment(sketch, "E4366", {"start": v(-149.82, 221.3) * mm, "end": v(-149.84, 222.06) * mm});
            skLineSegment(sketch, "E4367", {"start": v(-149.84, 222.06) * mm, "end": v(-149.85, 222.81) * mm});
            skLineSegment(sketch, "E4368", {"start": v(-149.85, 222.81) * mm, "end": v(-149.86, 223.58) * mm});
            skLineSegment(sketch, "E4369", {"start": v(-149.86, 223.58) * mm, "end": v(-149.85, 224.68) * mm});
            skLineSegment(sketch, "E4370", {"start": v(-149.85, 224.68) * mm, "end": v(-149.83, 225.77) * mm});
            skLineSegment(sketch, "E4371", {"start": v(-149.83, 225.77) * mm, "end": v(-149.79, 226.86) * mm});
            skLineSegment(sketch, "E4372", {"start": v(-149.79, 226.86) * mm, "end": v(-149.73, 227.94) * mm});
            skLineSegment(sketch, "E4373", {"start": v(-149.73, 227.94) * mm, "end": v(-149.66, 229.02) * mm});
            skLineSegment(sketch, "E4374", {"start": v(-149.66, 229.02) * mm, "end": v(-149.57, 230.1) * mm});
            skLineSegment(sketch, "E4375", {"start": v(-149.57, 230.1) * mm, "end": v(-149.46, 231.16) * mm});
            skLineSegment(sketch, "E4376", {"start": v(-149.46, 231.16) * mm, "end": v(-149.34, 232.23) * mm});
            skLineSegment(sketch, "E4377", {"start": v(-149.34, 232.23) * mm, "end": v(-149.2, 233.29) * mm});
            skLineSegment(sketch, "E4378", {"start": v(-149.2, 233.29) * mm, "end": v(-149.05, 234.34) * mm});
            skLineSegment(sketch, "E4379", {"start": v(-149.05, 234.34) * mm, "end": v(-148.88, 235.4) * mm});
            skLineSegment(sketch, "E4380", {"start": v(-148.88, 235.4) * mm, "end": v(-148.7, 236.43) * mm});
            skLineSegment(sketch, "E4381", {"start": v(-148.7, 236.43) * mm, "end": v(-148.5, 237.47) * mm});
            skLineSegment(sketch, "E4382", {"start": v(-148.5, 237.47) * mm, "end": v(-148.28, 238.5) * mm});
            skLineSegment(sketch, "E4383", {"start": v(-148.28, 238.5) * mm, "end": v(-148.05, 239.54) * mm});
            skLineSegment(sketch, "E4384", {"start": v(-148.05, 239.54) * mm, "end": v(-147.8, 240.56) * mm});
            skLineSegment(sketch, "E4385", {"start": v(-147.8, 240.56) * mm, "end": v(-147.54, 241.57) * mm});
            skLineSegment(sketch, "E4386", {"start": v(-147.54, 241.57) * mm, "end": v(-147.26, 242.55) * mm});
            skLineSegment(sketch, "E4387", {"start": v(-147.26, 242.55) * mm, "end": v(-146.98, 243.5) * mm});
            skLineSegment(sketch, "E4388", {"start": v(-146.98, 243.5) * mm, "end": v(-146.68, 244.43) * mm});
            skLineSegment(sketch, "E4389", {"start": v(-146.68, 244.43) * mm, "end": v(-146.38, 245.33) * mm});
            skLineSegment(sketch, "E4390", {"start": v(-146.38, 245.33) * mm, "end": v(-146.06, 246.2) * mm});
            skLineSegment(sketch, "E4391", {"start": v(-146.06, 246.2) * mm, "end": v(-145.74, 247.04) * mm});
            skLineSegment(sketch, "E4392", {"start": v(-145.74, 247.04) * mm, "end": v(-145.4, 247.86) * mm});
            skLineSegment(sketch, "E4393", {"start": v(-145.4, 247.86) * mm, "end": v(-145.05, 248.64) * mm});
            skLineSegment(sketch, "E4394", {"start": v(-145.05, 248.64) * mm, "end": v(-144.7, 249.4) * mm});
            skLineSegment(sketch, "E4395", {"start": v(-144.7, 249.4) * mm, "end": v(-144.33, 250.14) * mm});
            skLineSegment(sketch, "E4396", {"start": v(-144.33, 250.14) * mm, "end": v(-143.95, 250.84) * mm});
            skLineSegment(sketch, "E4397", {"start": v(-143.95, 250.84) * mm, "end": v(-143.56, 251.52) * mm});
            skLineSegment(sketch, "E4398", {"start": v(-143.56, 251.52) * mm, "end": v(-143.16, 252.17) * mm});
            skLineSegment(sketch, "E4399", {"start": v(-143.16, 252.17) * mm, "end": v(-142.75, 252.79) * mm});
            skLineSegment(sketch, "E4400", {"start": v(-142.75, 252.79) * mm, "end": v(-142.33, 253.38) * mm});
            skLineSegment(sketch, "E4401", {"start": v(-142.33, 253.38) * mm, "end": v(-142.02, 253.8) * mm});
            skLineSegment(sketch, "E4402", {"start": v(-142.02, 253.8) * mm, "end": v(-141.7, 254.2) * mm});
            skLineSegment(sketch, "E4403", {"start": v(-141.7, 254.2) * mm, "end": v(-141.39, 254.58) * mm});
            skLineSegment(sketch, "E4404", {"start": v(-141.39, 254.58) * mm, "end": v(-141.07, 254.95) * mm});
            skLineSegment(sketch, "E4405", {"start": v(-141.07, 254.95) * mm, "end": v(-140.74, 255.3) * mm});
            skLineSegment(sketch, "E4406", {"start": v(-140.74, 255.3) * mm, "end": v(-140.41, 255.65) * mm});
            skLineSegment(sketch, "E4407", {"start": v(-140.41, 255.65) * mm, "end": v(-140.08, 255.99) * mm});
            skLineSegment(sketch, "E4408", {"start": v(-140.08, 255.99) * mm, "end": v(-139.74, 256.3) * mm});
            skLineSegment(sketch, "E4409", {"start": v(-139.74, 256.3) * mm, "end": v(-139.4, 256.61) * mm});
            skLineSegment(sketch, "E4410", {"start": v(-139.4, 256.61) * mm, "end": v(-139.06, 256.9) * mm});
            skLineSegment(sketch, "E4411", {"start": v(-139.06, 256.9) * mm, "end": v(-138.71, 257.19) * mm});
            skLineSegment(sketch, "E4412", {"start": v(-138.71, 257.19) * mm, "end": v(-138.36, 257.45) * mm});
            skLineSegment(sketch, "E4413", {"start": v(-138.36, 257.45) * mm, "end": v(-138.01, 257.7) * mm});
            skLineSegment(sketch, "E4414", {"start": v(-138.01, 257.7) * mm, "end": v(-137.65, 257.95) * mm});
            skLineSegment(sketch, "E4415", {"start": v(-137.65, 257.95) * mm, "end": v(-137.3, 258.18) * mm});
            skLineSegment(sketch, "E4416", {"start": v(-137.3, 258.18) * mm, "end": v(-136.93, 258.4) * mm});
            skLineSegment(sketch, "E4417", {"start": v(-136.93, 258.4) * mm, "end": v(-136.56, 258.6) * mm});
            skLineSegment(sketch, "E4418", {"start": v(-136.56, 258.6) * mm, "end": v(-136.2, 258.79) * mm});
            skLineSegment(sketch, "E4419", {"start": v(-136.2, 258.79) * mm, "end": v(-135.82, 258.96) * mm});
            skLineSegment(sketch, "E4420", {"start": v(-135.82, 258.96) * mm, "end": v(-135.44, 259.13) * mm});
            skLineSegment(sketch, "E4421", {"start": v(-135.44, 259.13) * mm, "end": v(-135.06, 259.28) * mm});
            skLineSegment(sketch, "E4422", {"start": v(-135.06, 259.28) * mm, "end": v(-134.68, 259.41) * mm});
            skLineSegment(sketch, "E4423", {"start": v(-134.68, 259.41) * mm, "end": v(-134.3, 259.54) * mm});
            skLineSegment(sketch, "E4424", {"start": v(-134.3, 259.54) * mm, "end": v(-133.9, 259.65) * mm});
            skLineSegment(sketch, "E4425", {"start": v(-133.9, 259.65) * mm, "end": v(-133.5, 259.75) * mm});
            skLineSegment(sketch, "E4426", {"start": v(-133.5, 259.75) * mm, "end": v(-133.1, 259.83) * mm});
            skLineSegment(sketch, "E4427", {"start": v(-133.1, 259.83) * mm, "end": v(-132.7, 259.9) * mm});
            skLineSegment(sketch, "E4428", {"start": v(-132.7, 259.9) * mm, "end": v(-132.3, 259.96) * mm});
            skLineSegment(sketch, "E4429", {"start": v(-132.3, 259.96) * mm, "end": v(-131.9, 260) * mm});
            skLineSegment(sketch, "E4430", {"start": v(-131.9, 260) * mm, "end": v(-131.48, 260.04) * mm});
            skLineSegment(sketch, "E4431", {"start": v(-131.48, 260.04) * mm, "end": v(-131.07, 260.06) * mm});
            skLineSegment(sketch, "E4432", {"start": v(-131.07, 260.06) * mm, "end": v(-130.65, 260.07) * mm});
            skLineSegment(sketch, "E4433", {"start": v(-130.65, 260.07) * mm, "end": v(-130.65, 252.36) * mm});
            skLineSegment(sketch, "E4434", {"start": v(-130.65, 252.36) * mm, "end": v(-130.84, 252.26) * mm});
            skLineSegment(sketch, "E4435", {"start": v(-130.84, 252.26) * mm, "end": v(-131.02, 252.15) * mm});
            skLineSegment(sketch, "E4436", {"start": v(-131.02, 252.15) * mm, "end": v(-131.2, 252.03) * mm});
            skLineSegment(sketch, "E4437", {"start": v(-131.2, 252.03) * mm, "end": v(-131.37, 251.9) * mm});
            skLineSegment(sketch, "E4438", {"start": v(-131.37, 251.9) * mm, "end": v(-131.54, 251.78) * mm});
            skLineSegment(sketch, "E4439", {"start": v(-131.54, 251.78) * mm, "end": v(-131.7, 251.64) * mm});
            skLineSegment(sketch, "E4440", {"start": v(-131.7, 251.64) * mm, "end": v(-131.85, 251.5) * mm});
            skLineSegment(sketch, "E4441", {"start": v(-131.85, 251.5) * mm, "end": v(-132, 251.34) * mm});
            skLineSegment(sketch, "E4442", {"start": v(-132, 251.34) * mm, "end": v(-132.13, 251.18) * mm});
            skLineSegment(sketch, "E4443", {"start": v(-132.13, 251.18) * mm, "end": v(-132.26, 251) * mm});
            skLineSegment(sketch, "E4444", {"start": v(-132.26, 251) * mm, "end": v(-132.39, 250.83) * mm});
            skLineSegment(sketch, "E4445", {"start": v(-132.39, 250.83) * mm, "end": v(-132.5, 250.65) * mm});
            skLineSegment(sketch, "E4446", {"start": v(-132.5, 250.65) * mm, "end": v(-132.62, 250.46) * mm});
            skLineSegment(sketch, "E4447", {"start": v(-132.62, 250.46) * mm, "end": v(-132.72, 250.26) * mm});
            skLineSegment(sketch, "E4448", {"start": v(-132.72, 250.26) * mm, "end": v(-132.82, 250.06) * mm});
            skLineSegment(sketch, "E4449", {"start": v(-132.82, 250.06) * mm, "end": v(-132.9, 249.84) * mm});
            skLineSegment(sketch, "E4450", {"start": v(-132.9, 249.84) * mm, "end": v(-133, 249.62) * mm});
            skLineSegment(sketch, "E4451", {"start": v(-133, 249.62) * mm, "end": v(-133.07, 249.39) * mm});
            skLineSegment(sketch, "E4452", {"start": v(-133.07, 249.39) * mm, "end": v(-133.15, 249.14) * mm});
            skLineSegment(sketch, "E4453", {"start": v(-133.15, 249.14) * mm, "end": v(-133.22, 248.88) * mm});
            skLineSegment(sketch, "E4454", {"start": v(-133.22, 248.88) * mm, "end": v(-133.28, 248.6) * mm});
            skLineSegment(sketch, "E4455", {"start": v(-133.28, 248.6) * mm, "end": v(-133.34, 248.32) * mm});
            skLineSegment(sketch, "E4456", {"start": v(-133.34, 248.32) * mm, "end": v(-133.43, 247.72) * mm});
            skLineSegment(sketch, "E4457", {"start": v(-133.43, 247.72) * mm, "end": v(-133.51, 247.07) * mm});
            skLineSegment(sketch, "E4458", {"start": v(-133.51, 247.07) * mm, "end": v(-133.57, 246.36) * mm});
            skLineSegment(sketch, "E4459", {"start": v(-133.57, 246.36) * mm, "end": v(-133.6, 245.61) * mm});
            skLineSegment(sketch, "E4460", {"start": v(-133.6, 245.61) * mm, "end": v(-133.6, 244.8) * mm});
            skLineSegment(sketch, "E4461", {"start": v(-133.6, 244.8) * mm, "end": v(-133.6, 214.85) * mm});
            skLineSegment(sketch, "E4462", {"start": v(-133.6, 214.85) * mm, "end": v(-133.6, 213.99) * mm});
            skLineSegment(sketch, "E4463", {"start": v(-133.6, 213.99) * mm, "end": v(-133.56, 213.17) * mm});
            skLineSegment(sketch, "E4464", {"start": v(-133.56, 213.17) * mm, "end": v(-133.5, 212.41) * mm});
            skLineSegment(sketch, "E4465", {"start": v(-133.5, 212.41) * mm, "end": v(-133.42, 211.7) * mm});
            skLineSegment(sketch, "E4466", {"start": v(-133.42, 211.7) * mm, "end": v(-133.37, 211.35) * mm});
            skLineSegment(sketch, "E4467", {"start": v(-133.37, 211.35) * mm, "end": v(-133.31, 211.02) * mm});
            skLineSegment(sketch, "E4468", {"start": v(-133.31, 211.02) * mm, "end": v(-133.25, 210.7) * mm});
            skLineSegment(sketch, "E4469", {"start": v(-133.25, 210.7) * mm, "end": v(-133.18, 210.4) * mm});
            skLineSegment(sketch, "E4470", {"start": v(-133.18, 210.4) * mm, "end": v(-133.1, 210.11) * mm});
            skLineSegment(sketch, "E4471", {"start": v(-133.1, 210.11) * mm, "end": v(-133.03, 209.83) * mm});
            skLineSegment(sketch, "E4472", {"start": v(-133.03, 209.83) * mm, "end": v(-132.94, 209.56) * mm});
            skLineSegment(sketch, "E4473", {"start": v(-132.94, 209.56) * mm, "end": v(-132.85, 209.3) * mm});
            skLineSegment(sketch, "E4474", {"start": v(-132.85, 209.3) * mm, "end": v(-132.75, 209.06) * mm});
            skLineSegment(sketch, "E4475", {"start": v(-132.75, 209.06) * mm, "end": v(-132.65, 208.84) * mm});
            skLineSegment(sketch, "E4476", {"start": v(-132.65, 208.84) * mm, "end": v(-132.55, 208.63) * mm});
            skLineSegment(sketch, "E4477", {"start": v(-132.55, 208.63) * mm, "end": v(-132.44, 208.43) * mm});
            skLineSegment(sketch, "E4478", {"start": v(-132.44, 208.43) * mm, "end": v(-132.32, 208.25) * mm});
            skLineSegment(sketch, "E4479", {"start": v(-132.32, 208.25) * mm, "end": v(-132.2, 208.1) * mm});
            skLineSegment(sketch, "E4480", {"start": v(-132.2, 208.1) * mm, "end": v(-132.08, 207.95) * mm});
            skLineSegment(sketch, "E4481", {"start": v(-132.08, 207.95) * mm, "end": v(-131.96, 207.82) * mm});
            skLineSegment(sketch, "E4482", {"start": v(-131.96, 207.82) * mm, "end": v(-131.83, 207.7) * mm});
            skLineSegment(sketch, "E4483", {"start": v(-131.83, 207.7) * mm, "end": v(-131.7, 207.61) * mm});
            skLineSegment(sketch, "E4484", {"start": v(-131.7, 207.61) * mm, "end": v(-131.56, 207.53) * mm});
            skLineSegment(sketch, "E4485", {"start": v(-131.56, 207.53) * mm, "end": v(-131.42, 207.47) * mm});
            skLineSegment(sketch, "E4486", {"start": v(-131.42, 207.47) * mm, "end": v(-131.27, 207.42) * mm});
            skLineSegment(sketch, "E4487", {"start": v(-131.27, 207.42) * mm, "end": v(-131.12, 207.4) * mm});
            skLineSegment(sketch, "E4488", {"start": v(-131.12, 207.4) * mm, "end": v(-130.97, 207.38) * mm});
            skLineSegment(sketch, "E4489", {"start": v(-130.97, 207.38) * mm, "end": v(-130.8, 207.38) * mm});
            skLineSegment(sketch, "E4490", {"start": v(-130.8, 207.38) * mm, "end": v(-130.65, 207.4) * mm});
            skLineSegment(sketch, "E4491", {"start": v(-130.65, 207.4) * mm, "end": v(-130.5, 207.43) * mm});
            skLineSegment(sketch, "E4492", {"start": v(-130.5, 207.43) * mm, "end": v(-130.33, 207.48) * mm});
            skLineSegment(sketch, "E4493", {"start": v(-130.33, 207.48) * mm, "end": v(-130.16, 207.54) * mm});
            skLineSegment(sketch, "E4494", {"start": v(-130.16, 207.54) * mm, "end": v(-129.98, 207.63) * mm});
            skLineSegment(sketch, "E4495", {"start": v(-129.98, 207.63) * mm, "end": v(-129.8, 207.72) * mm});
            skLineSegment(sketch, "E4496", {"start": v(-129.8, 207.72) * mm, "end": v(-129.61, 207.84) * mm});
            skLineSegment(sketch, "E4497", {"start": v(-129.61, 207.84) * mm, "end": v(-129.42, 207.97) * mm});
            skLineSegment(sketch, "E4498", {"start": v(-129.42, 207.97) * mm, "end": v(-129.22, 208.11) * mm});
            skLineSegment(sketch, "E4499", {"start": v(-129.22, 208.11) * mm, "end": v(-129, 208.27) * mm});
            skLineSegment(sketch, "E4500", {"start": v(-129, 208.27) * mm, "end": v(-128.8, 208.45) * mm});
            skLineSegment(sketch, "E4501", {"start": v(-128.8, 208.45) * mm, "end": v(-128.58, 208.65) * mm});
            skLineSegment(sketch, "E4502", {"start": v(-128.58, 208.65) * mm, "end": v(-128.12, 209.08) * mm});
            skLineSegment(sketch, "E4503", {"start": v(-128.12, 209.08) * mm, "end": v(-127.65, 209.58) * mm});
            skLineSegment(sketch, "E4504", {"start": v(-121, 126.17) * mm, "end": v(-121, 33.77) * mm});
            skLineSegment(sketch, "E4505", {"start": v(-121, 33.77) * mm, "end": v(-120.99, 33.03) * mm});
            skLineSegment(sketch, "E4506", {"start": v(-120.99, 33.03) * mm, "end": v(-120.96, 32.34) * mm});
            skLineSegment(sketch, "E4507", {"start": v(-120.96, 32.34) * mm, "end": v(-120.91, 31.71) * mm});
            skLineSegment(sketch, "E4508", {"start": v(-120.91, 31.71) * mm, "end": v(-120.85, 31.13) * mm});
            skLineSegment(sketch, "E4509", {"start": v(-120.85, 31.13) * mm, "end": v(-120.76, 30.61) * mm});
            skLineSegment(sketch, "E4510", {"start": v(-120.76, 30.61) * mm, "end": v(-120.66, 30.14) * mm});
            skLineSegment(sketch, "E4511", {"start": v(-120.66, 30.14) * mm, "end": v(-120.6, 29.93) * mm});
            skLineSegment(sketch, "E4512", {"start": v(-120.6, 29.93) * mm, "end": v(-120.54, 29.73) * mm});
            skLineSegment(sketch, "E4513", {"start": v(-120.54, 29.73) * mm, "end": v(-120.47, 29.54) * mm});
            skLineSegment(sketch, "E4514", {"start": v(-120.47, 29.54) * mm, "end": v(-120.4, 29.37) * mm});
            skLineSegment(sketch, "E4515", {"start": v(-120.4, 29.37) * mm, "end": v(-120.24, 29) * mm});
            skLineSegment(sketch, "E4516", {"start": v(-120.24, 29) * mm, "end": v(-120.16, 28.86) * mm});
            skLineSegment(sketch, "E4517", {"start": v(-120.16, 28.86) * mm, "end": v(-120.09, 28.73) * mm});
            skLineSegment(sketch, "E4518", {"start": v(-120.09, 28.73) * mm, "end": v(-120.01, 28.61) * mm});
            skLineSegment(sketch, "E4519", {"start": v(-120.01, 28.61) * mm, "end": v(-119.94, 28.52) * mm});
            skLineSegment(sketch, "E4520", {"start": v(-119.94, 28.52) * mm, "end": v(-119.87, 28.44) * mm});
            skLineSegment(sketch, "E4521", {"start": v(-119.87, 28.44) * mm, "end": v(-119.8, 28.38) * mm});
            skLineSegment(sketch, "E4522", {"start": v(-119.8, 28.38) * mm, "end": v(-119.58, 28.25) * mm});
            skLineSegment(sketch, "E4523", {"start": v(-119.58, 28.25) * mm, "end": v(-119.2, 28.04) * mm});
            skLineSegment(sketch, "E4524", {"start": v(-119.2, 28.04) * mm, "end": v(-118.66, 27.76) * mm});
            skLineSegment(sketch, "E4525", {"start": v(-118.66, 27.76) * mm, "end": v(-117.96, 27.4) * mm});
            skLineSegment(sketch, "E4526", {"start": v(-117.96, 27.4) * mm, "end": v(-117.72, 27.28) * mm});
            skLineSegment(sketch, "E4527", {"start": v(-117.72, 27.28) * mm, "end": v(-117.5, 27.14) * mm});
            skLineSegment(sketch, "E4528", {"start": v(-117.5, 27.14) * mm, "end": v(-117.3, 26.98) * mm});
            skLineSegment(sketch, "E4529", {"start": v(-117.3, 26.98) * mm, "end": v(-117.12, 26.8) * mm});
            skLineSegment(sketch, "E4530", {"start": v(-117.12, 26.8) * mm, "end": v(-116.94, 26.6) * mm});
            skLineSegment(sketch, "E4531", {"start": v(-116.94, 26.6) * mm, "end": v(-116.79, 26.39) * mm});
            skLineSegment(sketch, "E4532", {"start": v(-116.79, 26.39) * mm, "end": v(-116.64, 26.15) * mm});
            skLineSegment(sketch, "E4533", {"start": v(-116.64, 26.15) * mm, "end": v(-116.52, 25.89) * mm});
            skLineSegment(sketch, "E4534", {"start": v(-116.52, 25.89) * mm, "end": v(-116.4, 25.6) * mm});
            skLineSegment(sketch, "E4535", {"start": v(-116.4, 25.6) * mm, "end": v(-116.3, 25.3) * mm});
            skLineSegment(sketch, "E4536", {"start": v(-116.3, 25.3) * mm, "end": v(-116.22, 24.98) * mm});
            skLineSegment(sketch, "E4537", {"start": v(-116.22, 24.98) * mm, "end": v(-116.16, 24.64) * mm});
            skLineSegment(sketch, "E4538", {"start": v(-116.16, 24.64) * mm, "end": v(-116.1, 24.28) * mm});
            skLineSegment(sketch, "E4539", {"start": v(-116.1, 24.28) * mm, "end": v(-116.07, 23.9) * mm});
            skLineSegment(sketch, "E4540", {"start": v(-116.07, 23.9) * mm, "end": v(-116.04, 23.5) * mm});
            skLineSegment(sketch, "E4541", {"start": v(-116.04, 23.5) * mm, "end": v(-116.04, 23.07) * mm});
            skLineSegment(sketch, "E4542", {"start": v(-116.04, 23.07) * mm, "end": v(-116.04, 22.82) * mm});
            skLineSegment(sketch, "E4543", {"start": v(-116.04, 22.82) * mm, "end": v(-116.05, 22.58) * mm});
            skLineSegment(sketch, "E4544", {"start": v(-116.05, 22.58) * mm, "end": v(-116.07, 22.34) * mm});
            skLineSegment(sketch, "E4545", {"start": v(-116.07, 22.34) * mm, "end": v(-116.1, 22.1) * mm});
            skLineSegment(sketch, "E4546", {"start": v(-116.1, 22.1) * mm, "end": v(-116.14, 21.87) * mm});
            skLineSegment(sketch, "E4547", {"start": v(-116.14, 21.87) * mm, "end": v(-116.18, 21.65) * mm});
            skLineSegment(sketch, "E4548", {"start": v(-116.18, 21.65) * mm, "end": v(-116.23, 21.44) * mm});
            skLineSegment(sketch, "E4549", {"start": v(-116.23, 21.44) * mm, "end": v(-116.3, 21.23) * mm});
            skLineSegment(sketch, "E4550", {"start": v(-116.3, 21.23) * mm, "end": v(-116.36, 21.02) * mm});
            skLineSegment(sketch, "E4551", {"start": v(-116.36, 21.02) * mm, "end": v(-116.44, 20.83) * mm});
            skLineSegment(sketch, "E4552", {"start": v(-116.44, 20.83) * mm, "end": v(-116.53, 20.63) * mm});
            skLineSegment(sketch, "E4553", {"start": v(-116.53, 20.63) * mm, "end": v(-116.62, 20.45) * mm});
            skLineSegment(sketch, "E4554", {"start": v(-116.62, 20.45) * mm, "end": v(-116.72, 20.27) * mm});
            skLineSegment(sketch, "E4555", {"start": v(-116.72, 20.27) * mm, "end": v(-116.83, 20.1) * mm});
            skLineSegment(sketch, "E4556", {"start": v(-116.83, 20.1) * mm, "end": v(-116.95, 19.93) * mm});
            skLineSegment(sketch, "E4557", {"start": v(-116.95, 19.93) * mm, "end": v(-117.08, 19.77) * mm});
            skLineSegment(sketch, "E4558", {"start": v(-117.08, 19.77) * mm, "end": v(-117.17, 19.66) * mm});
            skLineSegment(sketch, "E4559", {"start": v(-117.17, 19.66) * mm, "end": v(-117.28, 19.55) * mm});
            skLineSegment(sketch, "E4560", {"start": v(-117.28, 19.55) * mm, "end": v(-117.4, 19.45) * mm});
            skLineSegment(sketch, "E4561", {"start": v(-117.4, 19.45) * mm, "end": v(-117.52, 19.36) * mm});
            skLineSegment(sketch, "E4562", {"start": v(-117.52, 19.36) * mm, "end": v(-117.65, 19.27) * mm});
            skLineSegment(sketch, "E4563", {"start": v(-117.65, 19.27) * mm, "end": v(-117.79, 19.2) * mm});
            skLineSegment(sketch, "E4564", {"start": v(-117.79, 19.2) * mm, "end": v(-117.93, 19.13) * mm});
            skLineSegment(sketch, "E4565", {"start": v(-117.93, 19.13) * mm, "end": v(-118.09, 19.06) * mm});
            skLineSegment(sketch, "E4566", {"start": v(-118.09, 19.06) * mm, "end": v(-118.25, 19) * mm});
            skLineSegment(sketch, "E4567", {"start": v(-118.25, 19) * mm, "end": v(-118.42, 18.96) * mm});
            skLineSegment(sketch, "E4568", {"start": v(-118.42, 18.96) * mm, "end": v(-118.6, 18.92) * mm});
            skLineSegment(sketch, "E4569", {"start": v(-118.6, 18.92) * mm, "end": v(-118.78, 18.89) * mm});
            skLineSegment(sketch, "E4570", {"start": v(-118.78, 18.89) * mm, "end": v(-118.97, 18.86) * mm});
            skLineSegment(sketch, "E4571", {"start": v(-118.97, 18.86) * mm, "end": v(-119.17, 18.84) * mm});
            skLineSegment(sketch, "E4572", {"start": v(-119.17, 18.84) * mm, "end": v(-119.38, 18.83) * mm});
            skLineSegment(sketch, "E4573", {"start": v(-119.38, 18.83) * mm, "end": v(-119.6, 18.83) * mm});
            skLineSegment(sketch, "E4574", {"start": v(-119.6, 18.83) * mm, "end": v(-120.96, 18.83) * mm});
            skLineSegment(sketch, "E4575", {"start": v(-120.96, 18.83) * mm, "end": v(-136.33, 18.83) * mm});
            skLineSegment(sketch, "E4576", {"start": v(-136.33, 18.83) * mm, "end": v(-137.65, 18.83) * mm});
            skLineSegment(sketch, "E4577", {"start": v(-137.65, 18.83) * mm, "end": v(-137.87, 18.83) * mm});
            skLineSegment(sketch, "E4578", {"start": v(-137.87, 18.83) * mm, "end": v(-138.08, 18.84) * mm});
            skLineSegment(sketch, "E4579", {"start": v(-138.08, 18.84) * mm, "end": v(-138.29, 18.86) * mm});
            skLineSegment(sketch, "E4580", {"start": v(-138.29, 18.86) * mm, "end": v(-138.48, 18.89) * mm});
            skLineSegment(sketch, "E4581", {"start": v(-138.48, 18.89) * mm, "end": v(-138.67, 18.92) * mm});
            skLineSegment(sketch, "E4582", {"start": v(-138.67, 18.92) * mm, "end": v(-138.85, 18.96) * mm});
            skLineSegment(sketch, "E4583", {"start": v(-138.85, 18.96) * mm, "end": v(-139.02, 19) * mm});
            skLineSegment(sketch, "E4584", {"start": v(-139.02, 19) * mm, "end": v(-139.18, 19.06) * mm});
            skLineSegment(sketch, "E4585", {"start": v(-139.18, 19.06) * mm, "end": v(-139.33, 19.13) * mm});
            skLineSegment(sketch, "E4586", {"start": v(-139.33, 19.13) * mm, "end": v(-139.48, 19.2) * mm});
            skLineSegment(sketch, "E4587", {"start": v(-139.48, 19.2) * mm, "end": v(-139.61, 19.27) * mm});
            skLineSegment(sketch, "E4588", {"start": v(-139.61, 19.27) * mm, "end": v(-139.74, 19.36) * mm});
            skLineSegment(sketch, "E4589", {"start": v(-139.74, 19.36) * mm, "end": v(-139.86, 19.45) * mm});
            skLineSegment(sketch, "E4590", {"start": v(-139.86, 19.45) * mm, "end": v(-139.97, 19.55) * mm});
            skLineSegment(sketch, "E4591", {"start": v(-139.97, 19.55) * mm, "end": v(-140.08, 19.66) * mm});
            skLineSegment(sketch, "E4592", {"start": v(-140.08, 19.66) * mm, "end": v(-140.17, 19.77) * mm});
            skLineSegment(sketch, "E4593", {"start": v(-140.17, 19.77) * mm, "end": v(-140.3, 19.93) * mm});
            skLineSegment(sketch, "E4594", {"start": v(-140.3, 19.93) * mm, "end": v(-140.41, 20.1) * mm});
            skLineSegment(sketch, "E4595", {"start": v(-140.41, 20.1) * mm, "end": v(-140.52, 20.27) * mm});
            skLineSegment(sketch, "E4596", {"start": v(-140.52, 20.27) * mm, "end": v(-140.62, 20.45) * mm});
            skLineSegment(sketch, "E4597", {"start": v(-140.62, 20.45) * mm, "end": v(-140.72, 20.63) * mm});
            skLineSegment(sketch, "E4598", {"start": v(-140.72, 20.63) * mm, "end": v(-140.8, 20.83) * mm});
            skLineSegment(sketch, "E4599", {"start": v(-140.8, 20.83) * mm, "end": v(-140.88, 21.02) * mm});
            skLineSegment(sketch, "E4600", {"start": v(-140.88, 21.02) * mm, "end": v(-140.95, 21.23) * mm});
            skLineSegment(sketch, "E4601", {"start": v(-140.95, 21.23) * mm, "end": v(-141.01, 21.44) * mm});
            skLineSegment(sketch, "E4602", {"start": v(-141.01, 21.44) * mm, "end": v(-141.06, 21.65) * mm});
            skLineSegment(sketch, "E4603", {"start": v(-141.06, 21.65) * mm, "end": v(-141.1, 21.87) * mm});
            skLineSegment(sketch, "E4604", {"start": v(-141.1, 21.87) * mm, "end": v(-141.15, 22.1) * mm});
            skLineSegment(sketch, "E4605", {"start": v(-141.15, 22.1) * mm, "end": v(-141.17, 22.34) * mm});
            skLineSegment(sketch, "E4606", {"start": v(-141.17, 22.34) * mm, "end": v(-141.2, 22.58) * mm});
            skLineSegment(sketch, "E4607", {"start": v(-141.2, 22.58) * mm, "end": v(-141.2, 22.82) * mm});
            skLineSegment(sketch, "E4608", {"start": v(-141.2, 22.82) * mm, "end": v(-141.21, 23.07) * mm});
            skLineSegment(sketch, "E4609", {"start": v(-141.21, 23.07) * mm, "end": v(-141.2, 23.5) * mm});
            skLineSegment(sketch, "E4610", {"start": v(-141.2, 23.5) * mm, "end": v(-141.18, 23.9) * mm});
            skLineSegment(sketch, "E4611", {"start": v(-141.18, 23.9) * mm, "end": v(-141.14, 24.28) * mm});
            skLineSegment(sketch, "E4612", {"start": v(-141.14, 24.28) * mm, "end": v(-141.1, 24.64) * mm});
            skLineSegment(sketch, "E4613", {"start": v(-141.1, 24.64) * mm, "end": v(-141.02, 24.98) * mm});
            skLineSegment(sketch, "E4614", {"start": v(-141.02, 24.98) * mm, "end": v(-140.94, 25.3) * mm});
            skLineSegment(sketch, "E4615", {"start": v(-140.94, 25.3) * mm, "end": v(-140.84, 25.6) * mm});
            skLineSegment(sketch, "E4616", {"start": v(-140.84, 25.6) * mm, "end": v(-140.73, 25.89) * mm});
            skLineSegment(sketch, "E4617", {"start": v(-140.73, 25.89) * mm, "end": v(-140.6, 26.15) * mm});
            skLineSegment(sketch, "E4618", {"start": v(-140.6, 26.15) * mm, "end": v(-140.46, 26.39) * mm});
            skLineSegment(sketch, "E4619", {"start": v(-140.46, 26.39) * mm, "end": v(-140.3, 26.6) * mm});
            skLineSegment(sketch, "E4620", {"start": v(-140.3, 26.6) * mm, "end": v(-140.13, 26.8) * mm});
            skLineSegment(sketch, "E4621", {"start": v(-140.13, 26.8) * mm, "end": v(-139.94, 26.98) * mm});
            skLineSegment(sketch, "E4622", {"start": v(-139.94, 26.98) * mm, "end": v(-139.74, 27.14) * mm});
            skLineSegment(sketch, "E4623", {"start": v(-139.74, 27.14) * mm, "end": v(-139.52, 27.28) * mm});
            skLineSegment(sketch, "E4624", {"start": v(-139.52, 27.28) * mm, "end": v(-139.29, 27.4) * mm});
            skLineSegment(sketch, "E4625", {"start": v(-139.29, 27.4) * mm, "end": v(-138.59, 27.76) * mm});
            skLineSegment(sketch, "E4626", {"start": v(-138.59, 27.76) * mm, "end": v(-138.05, 28.04) * mm});
            skLineSegment(sketch, "E4627", {"start": v(-138.05, 28.04) * mm, "end": v(-137.67, 28.25) * mm});
            skLineSegment(sketch, "E4628", {"start": v(-137.67, 28.25) * mm, "end": v(-137.45, 28.38) * mm});
            skLineSegment(sketch, "E4629", {"start": v(-137.45, 28.38) * mm, "end": v(-137.38, 28.44) * mm});
            skLineSegment(sketch, "E4630", {"start": v(-137.38, 28.44) * mm, "end": v(-137.3, 28.52) * mm});
            skLineSegment(sketch, "E4631", {"start": v(-137.3, 28.52) * mm, "end": v(-137.24, 28.61) * mm});
            skLineSegment(sketch, "E4632", {"start": v(-137.24, 28.61) * mm, "end": v(-137.17, 28.73) * mm});
            skLineSegment(sketch, "E4633", {"start": v(-137.17, 28.73) * mm, "end": v(-137.1, 28.86) * mm});
            skLineSegment(sketch, "E4634", {"start": v(-137.1, 28.86) * mm, "end": v(-137.03, 29) * mm});
            skLineSegment(sketch, "E4635", {"start": v(-137.03, 29) * mm, "end": v(-136.89, 29.37) * mm});
            skLineSegment(sketch, "E4636", {"start": v(-136.89, 29.37) * mm, "end": v(-136.82, 29.54) * mm});
            skLineSegment(sketch, "E4637", {"start": v(-136.82, 29.54) * mm, "end": v(-136.75, 29.73) * mm});
            skLineSegment(sketch, "E4638", {"start": v(-136.75, 29.73) * mm, "end": v(-136.68, 29.93) * mm});
            skLineSegment(sketch, "E4639", {"start": v(-136.68, 29.93) * mm, "end": v(-136.63, 30.14) * mm});
            skLineSegment(sketch, "E4640", {"start": v(-136.63, 30.14) * mm, "end": v(-136.52, 30.61) * mm});
            skLineSegment(sketch, "E4641", {"start": v(-136.52, 30.61) * mm, "end": v(-136.44, 31.13) * mm});
            skLineSegment(sketch, "E4642", {"start": v(-136.44, 31.13) * mm, "end": v(-136.37, 31.71) * mm});
            skLineSegment(sketch, "E4643", {"start": v(-136.37, 31.71) * mm, "end": v(-136.32, 32.34) * mm});
            skLineSegment(sketch, "E4644", {"start": v(-136.32, 32.34) * mm, "end": v(-136.3, 33.03) * mm});
            skLineSegment(sketch, "E4645", {"start": v(-136.3, 33.03) * mm, "end": v(-136.29, 33.77) * mm});
            skLineSegment(sketch, "E4646", {"start": v(-136.29, 33.77) * mm, "end": v(-136.29, 107.38) * mm});
            skLineSegment(sketch, "E4647", {"start": v(-136.29, 107.38) * mm, "end": v(-136.3, 108.36) * mm});
            skLineSegment(sketch, "E4648", {"start": v(-136.3, 108.36) * mm, "end": v(-136.31, 109.28) * mm});
            skLineSegment(sketch, "E4649", {"start": v(-136.31, 109.28) * mm, "end": v(-136.35, 110.13) * mm});
            skLineSegment(sketch, "E4650", {"start": v(-136.35, 110.13) * mm, "end": v(-136.4, 110.91) * mm});
            skLineSegment(sketch, "E4651", {"start": v(-136.4, 110.91) * mm, "end": v(-136.45, 111.63) * mm});
            skLineSegment(sketch, "E4652", {"start": v(-136.45, 111.63) * mm, "end": v(-136.52, 112.27) * mm});
            skLineSegment(sketch, "E4653", {"start": v(-136.52, 112.27) * mm, "end": v(-136.6, 112.85) * mm});
            skLineSegment(sketch, "E4654", {"start": v(-136.6, 112.85) * mm, "end": v(-136.7, 113.35) * mm});
            skLineSegment(sketch, "E4655", {"start": v(-136.7, 113.35) * mm, "end": v(-136.82, 113.8) * mm});
            skLineSegment(sketch, "E4656", {"start": v(-136.82, 113.8) * mm, "end": v(-136.88, 114) * mm});
            skLineSegment(sketch, "E4657", {"start": v(-136.88, 114) * mm, "end": v(-136.95, 114.2) * mm});
            skLineSegment(sketch, "E4658", {"start": v(-136.95, 114.2) * mm, "end": v(-137.02, 114.37) * mm});
            skLineSegment(sketch, "E4659", {"start": v(-137.02, 114.37) * mm, "end": v(-137.1, 114.53) * mm});
            skLineSegment(sketch, "E4660", {"start": v(-137.1, 114.53) * mm, "end": v(-137.17, 114.69) * mm});
            skLineSegment(sketch, "E4661", {"start": v(-137.17, 114.69) * mm, "end": v(-137.25, 114.83) * mm});
            skLineSegment(sketch, "E4662", {"start": v(-137.25, 114.83) * mm, "end": v(-137.34, 114.95) * mm});
            skLineSegment(sketch, "E4663", {"start": v(-137.34, 114.95) * mm, "end": v(-137.43, 115.07) * mm});
            skLineSegment(sketch, "E4664", {"start": v(-137.43, 115.07) * mm, "end": v(-137.52, 115.17) * mm});
            skLineSegment(sketch, "E4665", {"start": v(-137.52, 115.17) * mm, "end": v(-137.62, 115.25) * mm});
            skLineSegment(sketch, "E4666", {"start": v(-137.62, 115.25) * mm, "end": v(-137.72, 115.33) * mm});
            skLineSegment(sketch, "E4667", {"start": v(-137.72, 115.33) * mm, "end": v(-137.83, 115.4) * mm});
            skLineSegment(sketch, "E4668", {"start": v(-137.83, 115.4) * mm, "end": v(-137.94, 115.44) * mm});
            skLineSegment(sketch, "E4669", {"start": v(-137.94, 115.44) * mm, "end": v(-138.05, 115.47) * mm});
            skLineSegment(sketch, "E4670", {"start": v(-138.05, 115.47) * mm, "end": v(-139.45, 115.87) * mm});
            skLineSegment(sketch, "E4671", {"start": v(-139.45, 115.87) * mm, "end": v(-139.68, 115.95) * mm});
            skLineSegment(sketch, "E4672", {"start": v(-139.68, 115.95) * mm, "end": v(-139.9, 116.05) * mm});
            skLineSegment(sketch, "E4673", {"start": v(-139.9, 116.05) * mm, "end": v(-140.09, 116.17) * mm});
            skLineSegment(sketch, "E4674", {"start": v(-140.09, 116.17) * mm, "end": v(-140.27, 116.31) * mm});
            skLineSegment(sketch, "E4675", {"start": v(-140.27, 116.31) * mm, "end": v(-140.44, 116.47) * mm});
            skLineSegment(sketch, "E4676", {"start": v(-140.44, 116.47) * mm, "end": v(-140.6, 116.66) * mm});
            skLineSegment(sketch, "E4677", {"start": v(-140.6, 116.66) * mm, "end": v(-140.74, 116.86) * mm});
            skLineSegment(sketch, "E4678", {"start": v(-140.74, 116.86) * mm, "end": v(-140.86, 117.09) * mm});
            skLineSegment(sketch, "E4679", {"start": v(-140.86, 117.09) * mm, "end": v(-140.97, 117.33) * mm});
            skLineSegment(sketch, "E4680", {"start": v(-140.97, 117.33) * mm, "end": v(-141.07, 117.6) * mm});
            skLineSegment(sketch, "E4681", {"start": v(-141.07, 117.6) * mm, "end": v(-141.15, 117.89) * mm});
            skLineSegment(sketch, "E4682", {"start": v(-141.15, 117.89) * mm, "end": v(-141.21, 118.2) * mm});
            skLineSegment(sketch, "E4683", {"start": v(-141.21, 118.2) * mm, "end": v(-141.26, 118.53) * mm});
            skLineSegment(sketch, "E4684", {"start": v(-141.26, 118.53) * mm, "end": v(-141.3, 118.88) * mm});
            skLineSegment(sketch, "E4685", {"start": v(-141.3, 118.88) * mm, "end": v(-141.32, 119.25) * mm});
            skLineSegment(sketch, "E4686", {"start": v(-141.32, 119.25) * mm, "end": v(-141.33, 119.64) * mm});
            skLineSegment(sketch, "E4687", {"start": v(-141.33, 119.64) * mm, "end": v(-141.33, 119.95) * mm});
            skLineSegment(sketch, "E4688", {"start": v(-141.33, 119.95) * mm, "end": v(-141.31, 120.25) * mm});
            skLineSegment(sketch, "E4689", {"start": v(-141.31, 120.25) * mm, "end": v(-141.29, 120.55) * mm});
            skLineSegment(sketch, "E4690", {"start": v(-141.29, 120.55) * mm, "end": v(-141.26, 120.83) * mm});
            skLineSegment(sketch, "E4691", {"start": v(-141.26, 120.83) * mm, "end": v(-141.21, 121.1) * mm});
            skLineSegment(sketch, "E4692", {"start": v(-141.21, 121.1) * mm, "end": v(-141.16, 121.38) * mm});
            skLineSegment(sketch, "E4693", {"start": v(-141.16, 121.38) * mm, "end": v(-141.1, 121.63) * mm});
            skLineSegment(sketch, "E4694", {"start": v(-141.1, 121.63) * mm, "end": v(-141.03, 121.88) * mm});
            skLineSegment(sketch, "E4695", {"start": v(-141.03, 121.88) * mm, "end": v(-140.95, 122.13) * mm});
            skLineSegment(sketch, "E4696", {"start": v(-140.95, 122.13) * mm, "end": v(-140.86, 122.36) * mm});
            skLineSegment(sketch, "E4697", {"start": v(-140.86, 122.36) * mm, "end": v(-140.76, 122.58) * mm});
            skLineSegment(sketch, "E4698", {"start": v(-140.76, 122.58) * mm, "end": v(-140.65, 122.8) * mm});
            skLineSegment(sketch, "E4699", {"start": v(-140.65, 122.8) * mm, "end": v(-140.54, 123) * mm});
            skLineSegment(sketch, "E4700", {"start": v(-140.54, 123) * mm, "end": v(-140.41, 123.2) * mm});
            skLineSegment(sketch, "E4701", {"start": v(-140.41, 123.2) * mm, "end": v(-140.28, 123.4) * mm});
            skLineSegment(sketch, "E4702", {"start": v(-140.28, 123.4) * mm, "end": v(-140.13, 123.57) * mm});
            skLineSegment(sketch, "E4703", {"start": v(-140.13, 123.57) * mm, "end": v(-140.05, 123.65) * mm});
            skLineSegment(sketch, "E4704", {"start": v(-140.05, 123.65) * mm, "end": v(-139.96, 123.73) * mm});
            skLineSegment(sketch, "E4705", {"start": v(-139.96, 123.73) * mm, "end": v(-139.86, 123.8) * mm});
            skLineSegment(sketch, "E4706", {"start": v(-139.86, 123.8) * mm, "end": v(-139.75, 123.86) * mm});
            skLineSegment(sketch, "E4707", {"start": v(-139.75, 123.86) * mm, "end": v(-139.5, 124) * mm});
            skLineSegment(sketch, "E4708", {"start": v(-139.5, 124) * mm, "end": v(-139.2, 124.1) * mm});
            skLineSegment(sketch, "E4709", {"start": v(-139.2, 124.1) * mm, "end": v(-138.88, 124.2) * mm});
            skLineSegment(sketch, "E4710", {"start": v(-138.88, 124.2) * mm, "end": v(-138.5, 124.3) * mm});
            skLineSegment(sketch, "E4711", {"start": v(-138.5, 124.3) * mm, "end": v(-138.1, 124.37) * mm});
            skLineSegment(sketch, "E4712", {"start": v(-138.1, 124.37) * mm, "end": v(-137.65, 124.44) * mm});
            skLineSegment(sketch, "E4713", {"start": v(-137.65, 124.44) * mm, "end": v(-121, 126.17) * mm});
            skLineSegment(sketch, "E4714", {"start": v(-130.7, -17.28) * mm, "end": v(-130.9, -17.5) * mm});
            skLineSegment(sketch, "E4715", {"start": v(-130.9, -17.5) * mm, "end": v(-131.1, -17.72) * mm});
            skLineSegment(sketch, "E4716", {"start": v(-131.1, -17.72) * mm, "end": v(-131.3, -17.94) * mm});
            skLineSegment(sketch, "E4717", {"start": v(-131.3, -17.94) * mm, "end": v(-131.47, -18.16) * mm});
            skLineSegment(sketch, "E4718", {"start": v(-131.47, -18.16) * mm, "end": v(-131.64, -18.39) * mm});
            skLineSegment(sketch, "E4719", {"start": v(-131.64, -18.39) * mm, "end": v(-131.8, -18.61) * mm});
            skLineSegment(sketch, "E4720", {"start": v(-131.8, -18.61) * mm, "end": v(-131.94, -18.84) * mm});
            skLineSegment(sketch, "E4721", {"start": v(-131.94, -18.84) * mm, "end": v(-132.08, -19.07) * mm});
            skLineSegment(sketch, "E4722", {"start": v(-132.08, -19.07) * mm, "end": v(-132.21, -19.3) * mm});
            skLineSegment(sketch, "E4723", {"start": v(-132.21, -19.3) * mm, "end": v(-132.34, -19.54) * mm});
            skLineSegment(sketch, "E4724", {"start": v(-132.34, -19.54) * mm, "end": v(-132.45, -19.77) * mm});
            skLineSegment(sketch, "E4725", {"start": v(-132.45, -19.77) * mm, "end": v(-132.55, -20.01) * mm});
            skLineSegment(sketch, "E4726", {"start": v(-132.55, -20.01) * mm, "end": v(-132.64, -20.25) * mm});
            skLineSegment(sketch, "E4727", {"start": v(-132.64, -20.25) * mm, "end": v(-132.73, -20.5) * mm});
            skLineSegment(sketch, "E4728", {"start": v(-132.73, -20.5) * mm, "end": v(-132.8, -20.73) * mm});
            skLineSegment(sketch, "E4729", {"start": v(-132.8, -20.73) * mm, "end": v(-132.86, -20.98) * mm});
            skLineSegment(sketch, "E4730", {"start": v(-132.86, -20.98) * mm, "end": v(-132.92, -21.24) * mm});
            skLineSegment(sketch, "E4731", {"start": v(-132.92, -21.24) * mm, "end": v(-132.98, -21.52) * mm});
            skLineSegment(sketch, "E4732", {"start": v(-132.98, -21.52) * mm, "end": v(-133.07, -22.17) * mm});
            skLineSegment(sketch, "E4733", {"start": v(-133.07, -22.17) * mm, "end": v(-133.16, -22.92) * mm});
            skLineSegment(sketch, "E4734", {"start": v(-133.16, -22.92) * mm, "end": v(-133.22, -23.77) * mm});
            skLineSegment(sketch, "E4735", {"start": v(-133.22, -23.77) * mm, "end": v(-133.28, -24.73) * mm});
            skLineSegment(sketch, "E4736", {"start": v(-133.28, -24.73) * mm, "end": v(-133.31, -25.79) * mm});
            skLineSegment(sketch, "E4737", {"start": v(-133.31, -25.79) * mm, "end": v(-133.34, -26.95) * mm});
            skLineSegment(sketch, "E4738", {"start": v(-133.34, -26.95) * mm, "end": v(-133.34, -28.21) * mm});
            skLineSegment(sketch, "E4739", {"start": v(-133.34, -28.21) * mm, "end": v(-133.34, -49.92) * mm});
            skLineSegment(sketch, "E4740", {"start": v(-133.34, -49.92) * mm, "end": v(-133.34, -50.56) * mm});
            skLineSegment(sketch, "E4741", {"start": v(-133.34, -50.56) * mm, "end": v(-133.31, -51.2) * mm});
            skLineSegment(sketch, "E4742", {"start": v(-133.31, -51.2) * mm, "end": v(-133.28, -51.83) * mm});
            skLineSegment(sketch, "E4743", {"start": v(-133.28, -51.83) * mm, "end": v(-133.22, -52.45) * mm});
            skLineSegment(sketch, "E4744", {"start": v(-133.22, -52.45) * mm, "end": v(-133.16, -53.07) * mm});
            skLineSegment(sketch, "E4745", {"start": v(-133.16, -53.07) * mm, "end": v(-133.07, -53.68) * mm});
            skLineSegment(sketch, "E4746", {"start": v(-133.07, -53.68) * mm, "end": v(-132.98, -54.28) * mm});
            skLineSegment(sketch, "E4747", {"start": v(-132.98, -54.28) * mm, "end": v(-132.86, -54.87) * mm});
            skLineSegment(sketch, "E4748", {"start": v(-132.86, -54.87) * mm, "end": v(-132.77, -55.25) * mm});
            skLineSegment(sketch, "E4749", {"start": v(-132.77, -55.25) * mm, "end": v(-132.68, -55.61) * mm});
            skLineSegment(sketch, "E4750", {"start": v(-132.68, -55.61) * mm, "end": v(-132.58, -55.95) * mm});
            skLineSegment(sketch, "E4751", {"start": v(-132.58, -55.95) * mm, "end": v(-132.48, -56.27) * mm});
            skLineSegment(sketch, "E4752", {"start": v(-132.48, -56.27) * mm, "end": v(-132.37, -56.56) * mm});
            skLineSegment(sketch, "E4753", {"start": v(-132.37, -56.56) * mm, "end": v(-132.27, -56.83) * mm});
            skLineSegment(sketch, "E4754", {"start": v(-132.27, -56.83) * mm, "end": v(-132.16, -57.08) * mm});
            skLineSegment(sketch, "E4755", {"start": v(-132.16, -57.08) * mm, "end": v(-132.04, -57.31) * mm});
            skLineSegment(sketch, "E4756", {"start": v(-132.04, -57.31) * mm, "end": v(-131.92, -57.52) * mm});
            skLineSegment(sketch, "E4757", {"start": v(-131.92, -57.52) * mm, "end": v(-131.79, -57.73) * mm});
            skLineSegment(sketch, "E4758", {"start": v(-131.79, -57.73) * mm, "end": v(-131.64, -57.94) * mm});
            skLineSegment(sketch, "E4759", {"start": v(-131.64, -57.94) * mm, "end": v(-131.48, -58.14) * mm});
            skLineSegment(sketch, "E4760", {"start": v(-131.48, -58.14) * mm, "end": v(-131.3, -58.33) * mm});
            skLineSegment(sketch, "E4761", {"start": v(-131.3, -58.33) * mm, "end": v(-131.12, -58.52) * mm});
            skLineSegment(sketch, "E4762", {"start": v(-131.12, -58.52) * mm, "end": v(-130.92, -58.7) * mm});
            skLineSegment(sketch, "E4763", {"start": v(-130.92, -58.7) * mm, "end": v(-130.7, -58.88) * mm});
            skLineSegment(sketch, "E4764", {"start": v(-130.7, -58.88) * mm, "end": v(-130.7, -67.14) * mm});
            skLineSegment(sketch, "E4765", {"start": v(-130.7, -67.14) * mm, "end": v(-130.88, -67.28) * mm});
            skLineSegment(sketch, "E4766", {"start": v(-130.88, -67.28) * mm, "end": v(-131.05, -67.43) * mm});
            skLineSegment(sketch, "E4767", {"start": v(-131.05, -67.43) * mm, "end": v(-131.21, -67.58) * mm});
            skLineSegment(sketch, "E4768", {"start": v(-131.21, -67.58) * mm, "end": v(-131.37, -67.74) * mm});
            skLineSegment(sketch, "E4769", {"start": v(-131.37, -67.74) * mm, "end": v(-131.52, -67.91) * mm});
            skLineSegment(sketch, "E4770", {"start": v(-131.52, -67.91) * mm, "end": v(-131.67, -68.09) * mm});
            skLineSegment(sketch, "E4771", {"start": v(-131.67, -68.09) * mm, "end": v(-131.8, -68.27) * mm});
            skLineSegment(sketch, "E4772", {"start": v(-131.8, -68.27) * mm, "end": v(-131.93, -68.46) * mm});
            skLineSegment(sketch, "E4773", {"start": v(-131.93, -68.46) * mm, "end": v(-132.06, -68.65) * mm});
            skLineSegment(sketch, "E4774", {"start": v(-132.06, -68.65) * mm, "end": v(-132.18, -68.85) * mm});
            skLineSegment(sketch, "E4775", {"start": v(-132.18, -68.85) * mm, "end": v(-132.29, -69.06) * mm});
            skLineSegment(sketch, "E4776", {"start": v(-132.29, -69.06) * mm, "end": v(-132.4, -69.28) * mm});
            skLineSegment(sketch, "E4777", {"start": v(-132.4, -69.28) * mm, "end": v(-132.49, -69.5) * mm});
            skLineSegment(sketch, "E4778", {"start": v(-132.49, -69.5) * mm, "end": v(-132.58, -69.73) * mm});
            skLineSegment(sketch, "E4779", {"start": v(-132.58, -69.73) * mm, "end": v(-132.67, -69.96) * mm});
            skLineSegment(sketch, "E4780", {"start": v(-132.67, -69.96) * mm, "end": v(-132.74, -70.2) * mm});
            skLineSegment(sketch, "E4781", {"start": v(-132.74, -70.2) * mm, "end": v(-132.82, -70.46) * mm});
            skLineSegment(sketch, "E4782", {"start": v(-132.82, -70.46) * mm, "end": v(-132.88, -70.72) * mm});
            skLineSegment(sketch, "E4783", {"start": v(-132.88, -70.72) * mm, "end": v(-133, -71.3) * mm});
            skLineSegment(sketch, "E4784", {"start": v(-133, -71.3) * mm, "end": v(-133.1, -71.91) * mm});
            skLineSegment(sketch, "E4785", {"start": v(-133.1, -71.91) * mm, "end": v(-133.2, -72.59) * mm});
            skLineSegment(sketch, "E4786", {"start": v(-133.2, -72.59) * mm, "end": v(-133.26, -73.3) * mm});
            skLineSegment(sketch, "E4787", {"start": v(-133.26, -73.3) * mm, "end": v(-133.3, -74.08) * mm});
            skLineSegment(sketch, "E4788", {"start": v(-133.3, -74.08) * mm, "end": v(-133.33, -74.91) * mm});
            skLineSegment(sketch, "E4789", {"start": v(-133.33, -74.91) * mm, "end": v(-133.34, -75.8) * mm});
            skLineSegment(sketch, "E4790", {"start": v(-133.34, -75.8) * mm, "end": v(-133.34, -102.68) * mm});
            skLineSegment(sketch, "E4791", {"start": v(-133.34, -102.68) * mm, "end": v(-133.34, -103.46) * mm});
            skLineSegment(sketch, "E4792", {"start": v(-133.34, -103.46) * mm, "end": v(-133.31, -104.2) * mm});
            skLineSegment(sketch, "E4793", {"start": v(-133.31, -104.2) * mm, "end": v(-133.27, -104.92) * mm});
            skLineSegment(sketch, "E4794", {"start": v(-133.27, -104.92) * mm, "end": v(-133.21, -105.61) * mm});
            skLineSegment(sketch, "E4795", {"start": v(-133.21, -105.61) * mm, "end": v(-133.14, -106.28) * mm});
            skLineSegment(sketch, "E4796", {"start": v(-133.14, -106.28) * mm, "end": v(-133.05, -106.92) * mm});
            skLineSegment(sketch, "E4797", {"start": v(-133.05, -106.92) * mm, "end": v(-132.95, -107.53) * mm});
            skLineSegment(sketch, "E4798", {"start": v(-132.95, -107.53) * mm, "end": v(-132.82, -108.11) * mm});
            skLineSegment(sketch, "E4799", {"start": v(-132.82, -108.11) * mm, "end": v(-132.74, -108.47) * mm});
            skLineSegment(sketch, "E4800", {"start": v(-132.74, -108.47) * mm, "end": v(-132.66, -108.8) * mm});
            skLineSegment(sketch, "E4801", {"start": v(-132.66, -108.8) * mm, "end": v(-132.57, -109.12) * mm});
            skLineSegment(sketch, "E4802", {"start": v(-132.57, -109.12) * mm, "end": v(-132.47, -109.4) * mm});
            skLineSegment(sketch, "E4803", {"start": v(-132.47, -109.4) * mm, "end": v(-132.38, -109.67) * mm});
            skLineSegment(sketch, "E4804", {"start": v(-132.38, -109.67) * mm, "end": v(-132.28, -109.9) * mm});
            skLineSegment(sketch, "E4805", {"start": v(-132.28, -109.9) * mm, "end": v(-132.17, -110.12) * mm});
            skLineSegment(sketch, "E4806", {"start": v(-132.17, -110.12) * mm, "end": v(-132.06, -110.31) * mm});
            skLineSegment(sketch, "E4807", {"start": v(-132.06, -110.31) * mm, "end": v(-131.95, -110.49) * mm});
            skLineSegment(sketch, "E4808", {"start": v(-131.95, -110.49) * mm, "end": v(-131.82, -110.65) * mm});
            skLineSegment(sketch, "E4809", {"start": v(-131.82, -110.65) * mm, "end": v(-131.67, -110.81) * mm});
            skLineSegment(sketch, "E4810", {"start": v(-131.67, -110.81) * mm, "end": v(-131.51, -110.96) * mm});
            skLineSegment(sketch, "E4811", {"start": v(-131.51, -110.96) * mm, "end": v(-131.34, -111.1) * mm});
            skLineSegment(sketch, "E4812", {"start": v(-131.34, -111.1) * mm, "end": v(-131.16, -111.24) * mm});
            skLineSegment(sketch, "E4813", {"start": v(-131.16, -111.24) * mm, "end": v(-130.96, -111.37) * mm});
            skLineSegment(sketch, "E4814", {"start": v(-130.96, -111.37) * mm, "end": v(-130.74, -111.5) * mm});
            skLineSegment(sketch, "E4815", {"start": v(-130.74, -111.5) * mm, "end": v(-130.74, -119.67) * mm});
            skLineSegment(sketch, "E4816", {"start": v(-130.74, -119.67) * mm, "end": v(-131.54, -119.6) * mm});
            skLineSegment(sketch, "E4817", {"start": v(-131.54, -119.6) * mm, "end": v(-131.98, -119.59) * mm});
            skLineSegment(sketch, "E4818", {"start": v(-131.98, -119.59) * mm, "end": v(-132.43, -119.57) * mm});
            skLineSegment(sketch, "E4819", {"start": v(-132.43, -119.57) * mm, "end": v(-132.87, -119.53) * mm});
            skLineSegment(sketch, "E4820", {"start": v(-132.87, -119.53) * mm, "end": v(-133.31, -119.49) * mm});
            skLineSegment(sketch, "E4821", {"start": v(-133.31, -119.49) * mm, "end": v(-133.76, -119.43) * mm});
            skLineSegment(sketch, "E4822", {"start": v(-133.76, -119.43) * mm, "end": v(-134.2, -119.36) * mm});
            skLineSegment(sketch, "E4823", {"start": v(-134.2, -119.36) * mm, "end": v(-134.66, -119.28) * mm});
            skLineSegment(sketch, "E4824", {"start": v(-134.66, -119.28) * mm, "end": v(-135.1, -119.18) * mm});
            skLineSegment(sketch, "E4825", {"start": v(-135.1, -119.18) * mm, "end": v(-135.56, -119.07) * mm});
            skLineSegment(sketch, "E4826", {"start": v(-135.56, -119.07) * mm, "end": v(-136, -118.95) * mm});
            skLineSegment(sketch, "E4827", {"start": v(-136, -118.95) * mm, "end": v(-136.46, -118.81) * mm});
            skLineSegment(sketch, "E4828", {"start": v(-136.46, -118.81) * mm, "end": v(-136.92, -118.66) * mm});
            skLineSegment(sketch, "E4829", {"start": v(-136.92, -118.66) * mm, "end": v(-137.37, -118.5) * mm});
            skLineSegment(sketch, "E4830", {"start": v(-137.37, -118.5) * mm, "end": v(-137.83, -118.33) * mm});
            skLineSegment(sketch, "E4831", {"start": v(-137.83, -118.33) * mm, "end": v(-138.29, -118.14) * mm});
            skLineSegment(sketch, "E4832", {"start": v(-138.29, -118.14) * mm, "end": v(-138.75, -117.94) * mm});
            skLineSegment(sketch, "E4833", {"start": v(-138.75, -117.94) * mm, "end": v(-139.3, -117.68) * mm});
            skLineSegment(sketch, "E4834", {"start": v(-139.3, -117.68) * mm, "end": v(-139.82, -117.41) * mm});
            skLineSegment(sketch, "E4835", {"start": v(-139.82, -117.41) * mm, "end": v(-140.32, -117.14) * mm});
            skLineSegment(sketch, "E4836", {"start": v(-140.32, -117.14) * mm, "end": v(-140.8, -116.85) * mm});
            skLineSegment(sketch, "E4837", {"start": v(-140.8, -116.85) * mm, "end": v(-141.24, -116.56) * mm});
            skLineSegment(sketch, "E4838", {"start": v(-141.24, -116.56) * mm, "end": v(-141.67, -116.25) * mm});
            skLineSegment(sketch, "E4839", {"start": v(-141.67, -116.25) * mm, "end": v(-142.07, -115.94) * mm});
            skLineSegment(sketch, "E4840", {"start": v(-142.07, -115.94) * mm, "end": v(-142.45, -115.62) * mm});
            skLineSegment(sketch, "E4841", {"start": v(-142.45, -115.62) * mm, "end": v(-142.81, -115.28) * mm});
            skLineSegment(sketch, "E4842", {"start": v(-142.81, -115.28) * mm, "end": v(-143.17, -114.92) * mm});
            skLineSegment(sketch, "E4843", {"start": v(-143.17, -114.92) * mm, "end": v(-143.53, -114.52) * mm});
            skLineSegment(sketch, "E4844", {"start": v(-143.53, -114.52) * mm, "end": v(-143.89, -114.1) * mm});
            skLineSegment(sketch, "E4845", {"start": v(-143.89, -114.1) * mm, "end": v(-144.24, -113.65) * mm});
            skLineSegment(sketch, "E4846", {"start": v(-144.24, -113.65) * mm, "end": v(-144.58, -113.17) * mm});
            skLineSegment(sketch, "E4847", {"start": v(-144.58, -113.17) * mm, "end": v(-144.93, -112.66) * mm});
            skLineSegment(sketch, "E4848", {"start": v(-144.93, -112.66) * mm, "end": v(-145.27, -112.12) * mm});
            skLineSegment(sketch, "E4849", {"start": v(-145.27, -112.12) * mm, "end": v(-145.55, -111.65) * mm});
            skLineSegment(sketch, "E4850", {"start": v(-145.55, -111.65) * mm, "end": v(-145.82, -111.17) * mm});
            skLineSegment(sketch, "E4851", {"start": v(-145.82, -111.17) * mm, "end": v(-146.08, -110.68) * mm});
            skLineSegment(sketch, "E4852", {"start": v(-146.08, -110.68) * mm, "end": v(-146.33, -110.17) * mm});
            skLineSegment(sketch, "E4853", {"start": v(-146.33, -110.17) * mm, "end": v(-146.57, -109.66) * mm});
            skLineSegment(sketch, "E4854", {"start": v(-146.57, -109.66) * mm, "end": v(-146.8, -109.14) * mm});
            skLineSegment(sketch, "E4855", {"start": v(-146.8, -109.14) * mm, "end": v(-147.03, -108.6) * mm});
            skLineSegment(sketch, "E4856", {"start": v(-147.03, -108.6) * mm, "end": v(-147.25, -108.07) * mm});
            skLineSegment(sketch, "E4857", {"start": v(-147.25, -108.07) * mm, "end": v(-147.46, -107.51) * mm});
            skLineSegment(sketch, "E4858", {"start": v(-147.46, -107.51) * mm, "end": v(-147.66, -106.95) * mm});
            skLineSegment(sketch, "E4859", {"start": v(-147.66, -106.95) * mm, "end": v(-147.85, -106.38) * mm});
            skLineSegment(sketch, "E4860", {"start": v(-147.85, -106.38) * mm, "end": v(-148.03, -105.8) * mm});
            skLineSegment(sketch, "E4861", {"start": v(-148.03, -105.8) * mm, "end": v(-148.2, -105.2) * mm});
            skLineSegment(sketch, "E4862", {"start": v(-148.2, -105.2) * mm, "end": v(-148.36, -104.6) * mm});
            skLineSegment(sketch, "E4863", {"start": v(-148.36, -104.6) * mm, "end": v(-148.52, -104) * mm});
            skLineSegment(sketch, "E4864", {"start": v(-148.52, -104) * mm, "end": v(-148.66, -103.37) * mm});
            skLineSegment(sketch, "E4865", {"start": v(-148.66, -103.37) * mm, "end": v(-148.8, -102.74) * mm});
            skLineSegment(sketch, "E4866", {"start": v(-148.8, -102.74) * mm, "end": v(-148.93, -102.1) * mm});
            skLineSegment(sketch, "E4867", {"start": v(-148.93, -102.1) * mm, "end": v(-149.05, -101.45) * mm});
            skLineSegment(sketch, "E4868", {"start": v(-149.05, -101.45) * mm, "end": v(-149.16, -100.79) * mm});
            skLineSegment(sketch, "E4869", {"start": v(-149.16, -100.79) * mm, "end": v(-149.26, -100.11) * mm});
            skLineSegment(sketch, "E4870", {"start": v(-149.26, -100.11) * mm, "end": v(-149.35, -99.43) * mm});
            skLineSegment(sketch, "E4871", {"start": v(-149.35, -99.43) * mm, "end": v(-149.44, -98.74) * mm});
            skLineSegment(sketch, "E4872", {"start": v(-149.44, -98.74) * mm, "end": v(-149.51, -98.04) * mm});
            skLineSegment(sketch, "E4873", {"start": v(-149.51, -98.04) * mm, "end": v(-149.58, -97.33) * mm});
            skLineSegment(sketch, "E4874", {"start": v(-149.58, -97.33) * mm, "end": v(-149.64, -96.6) * mm});
            skLineSegment(sketch, "E4875", {"start": v(-149.64, -96.6) * mm, "end": v(-149.68, -95.88) * mm});
            skLineSegment(sketch, "E4876", {"start": v(-149.68, -95.88) * mm, "end": v(-149.72, -95.13) * mm});
            skLineSegment(sketch, "E4877", {"start": v(-149.72, -95.13) * mm, "end": v(-149.75, -94.38) * mm});
            skLineSegment(sketch, "E4878", {"start": v(-149.75, -94.38) * mm, "end": v(-149.78, -93.62) * mm});
            skLineSegment(sketch, "E4879", {"start": v(-149.78, -93.62) * mm, "end": v(-149.79, -92.85) * mm});
            skLineSegment(sketch, "E4880", {"start": v(-149.79, -92.85) * mm, "end": v(-149.8, -92.07) * mm});
            skLineSegment(sketch, "E4881", {"start": v(-149.8, -92.07) * mm, "end": v(-149.79, -91.2) * mm});
            skLineSegment(sketch, "E4882", {"start": v(-149.79, -91.2) * mm, "end": v(-149.77, -90.34) * mm});
            skLineSegment(sketch, "E4883", {"start": v(-149.77, -90.34) * mm, "end": v(-149.74, -89.49) * mm});
            skLineSegment(sketch, "E4884", {"start": v(-149.74, -89.49) * mm, "end": v(-149.7, -88.64) * mm});
            skLineSegment(sketch, "E4885", {"start": v(-149.7, -88.64) * mm, "end": v(-149.66, -87.8) * mm});
            skLineSegment(sketch, "E4886", {"start": v(-149.66, -87.8) * mm, "end": v(-149.6, -86.99) * mm});
            skLineSegment(sketch, "E4887", {"start": v(-149.6, -86.99) * mm, "end": v(-149.52, -86.17) * mm});
            skLineSegment(sketch, "E4888", {"start": v(-149.52, -86.17) * mm, "end": v(-149.44, -85.36) * mm});
            skLineSegment(sketch, "E4889", {"start": v(-149.44, -85.36) * mm, "end": v(-149.34, -84.57) * mm});
            skLineSegment(sketch, "E4890", {"start": v(-149.34, -84.57) * mm, "end": v(-149.24, -83.78) * mm});
            skLineSegment(sketch, "E4891", {"start": v(-149.24, -83.78) * mm, "end": v(-149.12, -83) * mm});
            skLineSegment(sketch, "E4892", {"start": v(-149.12, -83) * mm, "end": v(-149, -82.23) * mm});
            skLineSegment(sketch, "E4893", {"start": v(-149, -82.23) * mm, "end": v(-148.86, -81.47) * mm});
            skLineSegment(sketch, "E4894", {"start": v(-148.86, -81.47) * mm, "end": v(-148.7, -80.72) * mm});
            skLineSegment(sketch, "E4895", {"start": v(-148.7, -80.72) * mm, "end": v(-148.55, -79.98) * mm});
            skLineSegment(sketch, "E4896", {"start": v(-148.55, -79.98) * mm, "end": v(-148.37, -79.25) * mm});
            skLineSegment(sketch, "E4897", {"start": v(-148.37, -79.25) * mm, "end": v(-148.2, -78.53) * mm});
            skLineSegment(sketch, "E4898", {"start": v(-148.2, -78.53) * mm, "end": v(-148, -77.83) * mm});
            skLineSegment(sketch, "E4899", {"start": v(-148, -77.83) * mm, "end": v(-147.8, -77.14) * mm});
            skLineSegment(sketch, "E4900", {"start": v(-147.8, -77.14) * mm, "end": v(-147.59, -76.46) * mm});
            skLineSegment(sketch, "E4901", {"start": v(-147.59, -76.46) * mm, "end": v(-147.37, -75.8) * mm});
            skLineSegment(sketch, "E4902", {"start": v(-147.37, -75.8) * mm, "end": v(-147.14, -75.16) * mm});
            skLineSegment(sketch, "E4903", {"start": v(-147.14, -75.16) * mm, "end": v(-146.9, -74.53) * mm});
            skLineSegment(sketch, "E4904", {"start": v(-146.9, -74.53) * mm, "end": v(-146.65, -73.92) * mm});
            skLineSegment(sketch, "E4905", {"start": v(-146.65, -73.92) * mm, "end": v(-146.39, -73.33) * mm});
            skLineSegment(sketch, "E4906", {"start": v(-146.39, -73.33) * mm, "end": v(-146.12, -72.74) * mm});
            skLineSegment(sketch, "E4907", {"start": v(-146.12, -72.74) * mm, "end": v(-145.84, -72.18) * mm});
            skLineSegment(sketch, "E4908", {"start": v(-145.84, -72.18) * mm, "end": v(-145.56, -71.63) * mm});
            skLineSegment(sketch, "E4909", {"start": v(-145.56, -71.63) * mm, "end": v(-145.26, -71.1) * mm});
            skLineSegment(sketch, "E4910", {"start": v(-145.26, -71.1) * mm, "end": v(-144.95, -70.57) * mm});
            skLineSegment(sketch, "E4911", {"start": v(-144.95, -70.57) * mm, "end": v(-144.64, -70.07) * mm});
            skLineSegment(sketch, "E4912", {"start": v(-144.64, -70.07) * mm, "end": v(-144.31, -69.58) * mm});
            skLineSegment(sketch, "E4913", {"start": v(-144.31, -69.58) * mm, "end": v(-143.94, -69.04) * mm});
            skLineSegment(sketch, "E4914", {"start": v(-143.94, -69.04) * mm, "end": v(-143.56, -68.53) * mm});
            skLineSegment(sketch, "E4915", {"start": v(-143.56, -68.53) * mm, "end": v(-143.18, -68.04) * mm});
            skLineSegment(sketch, "E4916", {"start": v(-143.18, -68.04) * mm, "end": v(-142.8, -67.57) * mm});
            skLineSegment(sketch, "E4917", {"start": v(-142.8, -67.57) * mm, "end": v(-142.4, -67.13) * mm});
            skLineSegment(sketch, "E4918", {"start": v(-142.4, -67.13) * mm, "end": v(-142.01, -66.72) * mm});
            skLineSegment(sketch, "E4919", {"start": v(-142.01, -66.72) * mm, "end": v(-141.61, -66.33) * mm});
            skLineSegment(sketch, "E4920", {"start": v(-141.61, -66.33) * mm, "end": v(-141.2, -65.96) * mm});
            skLineSegment(sketch, "E4921", {"start": v(-141.2, -65.96) * mm, "end": v(-140.79, -65.6) * mm});
            skLineSegment(sketch, "E4922", {"start": v(-140.79, -65.6) * mm, "end": v(-140.32, -65.24) * mm});
            skLineSegment(sketch, "E4923", {"start": v(-140.32, -65.24) * mm, "end": v(-139.83, -64.87) * mm});
            skLineSegment(sketch, "E4924", {"start": v(-139.83, -64.87) * mm, "end": v(-139.3, -64.49) * mm});
            skLineSegment(sketch, "E4925", {"start": v(-139.3, -64.49) * mm, "end": v(-138.72, -64.1) * mm});
            skLineSegment(sketch, "E4926", {"start": v(-138.72, -64.1) * mm, "end": v(-138.11, -63.7) * mm});
            skLineSegment(sketch, "E4927", {"start": v(-138.11, -63.7) * mm, "end": v(-137.47, -63.3) * mm});
            skLineSegment(sketch, "E4928", {"start": v(-137.47, -63.3) * mm, "end": v(-136.79, -62.9) * mm});
            skLineSegment(sketch, "E4929", {"start": v(-136.79, -62.9) * mm, "end": v(-137.45, -62.5) * mm});
            skLineSegment(sketch, "E4930", {"start": v(-137.45, -62.5) * mm, "end": v(-138.08, -62.11) * mm});
            skLineSegment(sketch, "E4931", {"start": v(-138.08, -62.11) * mm, "end": v(-138.67, -61.73) * mm});
            skLineSegment(sketch, "E4932", {"start": v(-138.67, -61.73) * mm, "end": v(-139.22, -61.35) * mm});
            skLineSegment(sketch, "E4933", {"start": v(-139.22, -61.35) * mm, "end": v(-139.74, -60.97) * mm});
            skLineSegment(sketch, "E4934", {"start": v(-139.74, -60.97) * mm, "end": v(-140.23, -60.6) * mm});
            skLineSegment(sketch, "E4935", {"start": v(-140.23, -60.6) * mm, "end": v(-140.68, -60.23) * mm});
            skLineSegment(sketch, "E4936", {"start": v(-140.68, -60.23) * mm, "end": v(-141.09, -59.87) * mm});
            skLineSegment(sketch, "E4937", {"start": v(-141.09, -59.87) * mm, "end": v(-141.48, -59.5) * mm});
            skLineSegment(sketch, "E4938", {"start": v(-141.48, -59.5) * mm, "end": v(-141.87, -59.1) * mm});
            skLineSegment(sketch, "E4939", {"start": v(-141.87, -59.1) * mm, "end": v(-142.24, -58.67) * mm});
            skLineSegment(sketch, "E4940", {"start": v(-142.24, -58.67) * mm, "end": v(-142.61, -58.22) * mm});
            skLineSegment(sketch, "E4941", {"start": v(-142.61, -58.22) * mm, "end": v(-142.98, -57.76) * mm});
            skLineSegment(sketch, "E4942", {"start": v(-142.98, -57.76) * mm, "end": v(-143.34, -57.26) * mm});
            skLineSegment(sketch, "E4943", {"start": v(-143.34, -57.26) * mm, "end": v(-143.69, -56.75) * mm});
            skLineSegment(sketch, "E4944", {"start": v(-143.69, -56.75) * mm, "end": v(-144.03, -56.2) * mm});
            skLineSegment(sketch, "E4945", {"start": v(-144.03, -56.2) * mm, "end": v(-144.29, -55.77) * mm});
            skLineSegment(sketch, "E4946", {"start": v(-144.29, -55.77) * mm, "end": v(-144.54, -55.33) * mm});
            skLineSegment(sketch, "E4947", {"start": v(-144.54, -55.33) * mm, "end": v(-144.78, -54.87) * mm});
            skLineSegment(sketch, "E4948", {"start": v(-144.78, -54.87) * mm, "end": v(-145.02, -54.4) * mm});
            skLineSegment(sketch, "E4949", {"start": v(-145.02, -54.4) * mm, "end": v(-145.24, -53.93) * mm});
            skLineSegment(sketch, "E4950", {"start": v(-145.24, -53.93) * mm, "end": v(-145.46, -53.45) * mm});
            skLineSegment(sketch, "E4951", {"start": v(-145.46, -53.45) * mm, "end": v(-145.67, -52.96) * mm});
            skLineSegment(sketch, "E4952", {"start": v(-145.67, -52.96) * mm, "end": v(-145.87, -52.45) * mm});
            skLineSegment(sketch, "E4953", {"start": v(-145.87, -52.45) * mm, "end": v(-146.06, -51.94) * mm});
            skLineSegment(sketch, "E4954", {"start": v(-146.06, -51.94) * mm, "end": v(-146.25, -51.42) * mm});
            skLineSegment(sketch, "E4955", {"start": v(-146.25, -51.42) * mm, "end": v(-146.42, -50.9) * mm});
            skLineSegment(sketch, "E4956", {"start": v(-146.42, -50.9) * mm, "end": v(-146.6, -50.36) * mm});
            skLineSegment(sketch, "E4957", {"start": v(-146.6, -50.36) * mm, "end": v(-146.75, -49.8) * mm});
            skLineSegment(sketch, "E4958", {"start": v(-146.75, -49.8) * mm, "end": v(-146.9, -49.25) * mm});
            skLineSegment(sketch, "E4959", {"start": v(-146.9, -49.25) * mm, "end": v(-147.05, -48.68) * mm});
            skLineSegment(sketch, "E4960", {"start": v(-147.05, -48.68) * mm, "end": v(-147.18, -48.1) * mm});
            skLineSegment(sketch, "E4961", {"start": v(-147.18, -48.1) * mm, "end": v(-147.3, -47.52) * mm});
            skLineSegment(sketch, "E4962", {"start": v(-147.3, -47.52) * mm, "end": v(-147.43, -46.93) * mm});
            skLineSegment(sketch, "E4963", {"start": v(-147.43, -46.93) * mm, "end": v(-147.54, -46.33) * mm});
            skLineSegment(sketch, "E4964", {"start": v(-147.54, -46.33) * mm, "end": v(-147.64, -45.72) * mm});
            skLineSegment(sketch, "E4965", {"start": v(-147.64, -45.72) * mm, "end": v(-147.74, -45.1) * mm});
            skLineSegment(sketch, "E4966", {"start": v(-147.74, -45.1) * mm, "end": v(-147.82, -44.46) * mm});
            skLineSegment(sketch, "E4967", {"start": v(-147.82, -44.46) * mm, "end": v(-147.9, -43.82) * mm});
            skLineSegment(sketch, "E4968", {"start": v(-147.9, -43.82) * mm, "end": v(-147.97, -43.17) * mm});
            skLineSegment(sketch, "E4969", {"start": v(-147.97, -43.17) * mm, "end": v(-148.03, -42.52) * mm});
            skLineSegment(sketch, "E4970", {"start": v(-148.03, -42.52) * mm, "end": v(-148.09, -41.85) * mm});
            skLineSegment(sketch, "E4971", {"start": v(-148.09, -41.85) * mm, "end": v(-148.13, -41.17) * mm});
            skLineSegment(sketch, "E4972", {"start": v(-148.13, -41.17) * mm, "end": v(-148.17, -40.49) * mm});
            skLineSegment(sketch, "E4973", {"start": v(-148.17, -40.49) * mm, "end": v(-148.2, -39.8) * mm});
            skLineSegment(sketch, "E4974", {"start": v(-148.2, -39.8) * mm, "end": v(-148.22, -39.09) * mm});
            skLineSegment(sketch, "E4975", {"start": v(-148.22, -39.09) * mm, "end": v(-148.23, -38.37) * mm});
            skLineSegment(sketch, "E4976", {"start": v(-148.23, -38.37) * mm, "end": v(-148.23, -37.65) * mm});
            skLineSegment(sketch, "E4977", {"start": v(-148.23, -37.65) * mm, "end": v(-148.23, -36.7) * mm});
            skLineSegment(sketch, "E4978", {"start": v(-148.23, -36.7) * mm, "end": v(-148.2, -35.76) * mm});
            skLineSegment(sketch, "E4979", {"start": v(-148.2, -35.76) * mm, "end": v(-148.17, -34.84) * mm});
            skLineSegment(sketch, "E4980", {"start": v(-148.17, -34.84) * mm, "end": v(-148.11, -33.92) * mm});
            skLineSegment(sketch, "E4981", {"start": v(-148.11, -33.92) * mm, "end": v(-148.05, -33.02) * mm});
            skLineSegment(sketch, "E4982", {"start": v(-148.05, -33.02) * mm, "end": v(-147.96, -32.12) * mm});
            skLineSegment(sketch, "E4983", {"start": v(-147.96, -32.12) * mm, "end": v(-147.87, -31.24) * mm});
            skLineSegment(sketch, "E4984", {"start": v(-147.87, -31.24) * mm, "end": v(-147.75, -30.37) * mm});
            skLineSegment(sketch, "E4985", {"start": v(-147.75, -30.37) * mm, "end": v(-147.63, -29.5) * mm});
            skLineSegment(sketch, "E4986", {"start": v(-147.63, -29.5) * mm, "end": v(-147.48, -28.65) * mm});
            skLineSegment(sketch, "E4987", {"start": v(-147.48, -28.65) * mm, "end": v(-147.33, -27.81) * mm});
            skLineSegment(sketch, "E4988", {"start": v(-147.33, -27.81) * mm, "end": v(-147.15, -26.98) * mm});
            skLineSegment(sketch, "E4989", {"start": v(-147.15, -26.98) * mm, "end": v(-146.97, -26.16) * mm});
            skLineSegment(sketch, "E4990", {"start": v(-146.97, -26.16) * mm, "end": v(-146.76, -25.36) * mm});
            skLineSegment(sketch, "E4991", {"start": v(-146.76, -25.36) * mm, "end": v(-146.54, -24.56) * mm});
            skLineSegment(sketch, "E4992", {"start": v(-146.54, -24.56) * mm, "end": v(-146.31, -23.77) * mm});
            skLineSegment(sketch, "E4993", {"start": v(-146.31, -23.77) * mm, "end": v(-146.07, -23) * mm});
            skLineSegment(sketch, "E4994", {"start": v(-146.07, -23) * mm, "end": v(-145.8, -22.25) * mm});
            skLineSegment(sketch, "E4995", {"start": v(-145.8, -22.25) * mm, "end": v(-145.54, -21.52) * mm});
            skLineSegment(sketch, "E4996", {"start": v(-145.54, -21.52) * mm, "end": v(-145.26, -20.82) * mm});
            skLineSegment(sketch, "E4997", {"start": v(-145.26, -20.82) * mm, "end": v(-144.97, -20.14) * mm});
            skLineSegment(sketch, "E4998", {"start": v(-144.97, -20.14) * mm, "end": v(-144.66, -19.47) * mm});
            skLineSegment(sketch, "E4999", {"start": v(-144.66, -19.47) * mm, "end": v(-144.35, -18.83) * mm});
            skLineSegment(sketch, "E5000", {"start": v(-144.35, -18.83) * mm, "end": v(-144.02, -18.22) * mm});
            skLineSegment(sketch, "E5001", {"start": v(-144.02, -18.22) * mm, "end": v(-143.68, -17.62) * mm});
            skLineSegment(sketch, "E5002", {"start": v(-143.68, -17.62) * mm, "end": v(-143.33, -17.05) * mm});
            skLineSegment(sketch, "E5003", {"start": v(-143.33, -17.05) * mm, "end": v(-142.97, -16.5) * mm});
            skLineSegment(sketch, "E5004", {"start": v(-142.97, -16.5) * mm, "end": v(-142.6, -15.96) * mm});
            skLineSegment(sketch, "E5005", {"start": v(-142.6, -15.96) * mm, "end": v(-142.21, -15.45) * mm});
            skLineSegment(sketch, "E5006", {"start": v(-142.21, -15.45) * mm, "end": v(-141.82, -14.97) * mm});
            skLineSegment(sketch, "E5007", {"start": v(-141.82, -14.97) * mm, "end": v(-141.4, -14.5) * mm});
            skLineSegment(sketch, "E5008", {"start": v(-141.4, -14.5) * mm, "end": v(-140.99, -14.06) * mm});
            skLineSegment(sketch, "E5009", {"start": v(-140.99, -14.06) * mm, "end": v(-140.75, -13.82) * mm});
            skLineSegment(sketch, "E5010", {"start": v(-140.75, -13.82) * mm, "end": v(-140.5, -13.6) * mm});
            skLineSegment(sketch, "E5011", {"start": v(-140.5, -13.6) * mm, "end": v(-140.25, -13.37) * mm});
            skLineSegment(sketch, "E5012", {"start": v(-140.25, -13.37) * mm, "end": v(-140, -13.15) * mm});
            skLineSegment(sketch, "E5013", {"start": v(-140, -13.15) * mm, "end": v(-139.74, -12.94) * mm});
            skLineSegment(sketch, "E5014", {"start": v(-139.74, -12.94) * mm, "end": v(-139.47, -12.73) * mm});
            skLineSegment(sketch, "E5015", {"start": v(-139.47, -12.73) * mm, "end": v(-139.2, -12.53) * mm});
            skLineSegment(sketch, "E5016", {"start": v(-139.2, -12.53) * mm, "end": v(-138.92, -12.34) * mm});
            skLineSegment(sketch, "E5017", {"start": v(-138.92, -12.34) * mm, "end": v(-138.64, -12.15) * mm});
            skLineSegment(sketch, "E5018", {"start": v(-138.64, -12.15) * mm, "end": v(-138.35, -11.97) * mm});
            skLineSegment(sketch, "E5019", {"start": v(-138.35, -11.97) * mm, "end": v(-138.06, -11.8) * mm});
            skLineSegment(sketch, "E5020", {"start": v(-138.06, -11.8) * mm, "end": v(-137.76, -11.63) * mm});
            skLineSegment(sketch, "E5021", {"start": v(-137.76, -11.63) * mm, "end": v(-137.46, -11.47) * mm});
            skLineSegment(sketch, "E5022", {"start": v(-137.46, -11.47) * mm, "end": v(-137.15, -11.32) * mm});
            skLineSegment(sketch, "E5023", {"start": v(-137.15, -11.32) * mm, "end": v(-136.84, -11.17) * mm});
            skLineSegment(sketch, "E5024", {"start": v(-136.84, -11.17) * mm, "end": v(-136.52, -11.03) * mm});
            skLineSegment(sketch, "E5025", {"start": v(-136.52, -11.03) * mm, "end": v(-136.2, -10.9) * mm});
            skLineSegment(sketch, "E5026", {"start": v(-136.2, -10.9) * mm, "end": v(-135.86, -10.77) * mm});
            skLineSegment(sketch, "E5027", {"start": v(-135.86, -10.77) * mm, "end": v(-135.53, -10.65) * mm});
            skLineSegment(sketch, "E5028", {"start": v(-135.53, -10.65) * mm, "end": v(-135.19, -10.53) * mm});
            skLineSegment(sketch, "E5029", {"start": v(-135.19, -10.53) * mm, "end": v(-134.84, -10.42) * mm});
            skLineSegment(sketch, "E5030", {"start": v(-134.84, -10.42) * mm, "end": v(-134.5, -10.32) * mm});
            skLineSegment(sketch, "E5031", {"start": v(-134.5, -10.32) * mm, "end": v(-133.78, -10.14) * mm});
            skLineSegment(sketch, "E5032", {"start": v(-133.78, -10.14) * mm, "end": v(-133.04, -9.98) * mm});
            skLineSegment(sketch, "E5033", {"start": v(-133.04, -9.98) * mm, "end": v(-132.28, -9.84) * mm});
            skLineSegment(sketch, "E5034", {"start": v(-132.28, -9.84) * mm, "end": v(-131.5, -9.74) * mm});
            skLineSegment(sketch, "E5035", {"start": v(-131.5, -9.74) * mm, "end": v(-130.7, -9.66) * mm});
            skLineSegment(sketch, "E5036", {"start": v(-130.7, -9.66) * mm, "end": v(-130.7, -17.28) * mm});
            skLineSegment(sketch, "E5037", {"start": v(-127.94, -17.28) * mm, "end": v(-127.94, -9.66) * mm});
            skLineSegment(sketch, "E5038", {"start": v(-127.94, -9.66) * mm, "end": v(-127.14, -9.74) * mm});
            skLineSegment(sketch, "E5039", {"start": v(-127.14, -9.74) * mm, "end": v(-126.35, -9.84) * mm});
            skLineSegment(sketch, "E5040", {"start": v(-126.35, -9.84) * mm, "end": v(-125.6, -9.98) * mm});
            skLineSegment(sketch, "E5041", {"start": v(-125.6, -9.98) * mm, "end": v(-124.85, -10.14) * mm});
            skLineSegment(sketch, "E5042", {"start": v(-124.85, -10.14) * mm, "end": v(-124.13, -10.32) * mm});
            skLineSegment(sketch, "E5043", {"start": v(-124.13, -10.32) * mm, "end": v(-123.78, -10.42) * mm});
            skLineSegment(sketch, "E5044", {"start": v(-123.78, -10.42) * mm, "end": v(-123.43, -10.53) * mm});
            skLineSegment(sketch, "E5045", {"start": v(-123.43, -10.53) * mm, "end": v(-123.09, -10.65) * mm});
            skLineSegment(sketch, "E5046", {"start": v(-123.09, -10.65) * mm, "end": v(-122.75, -10.77) * mm});
            skLineSegment(sketch, "E5047", {"start": v(-122.75, -10.77) * mm, "end": v(-122.42, -10.9) * mm});
            skLineSegment(sketch, "E5048", {"start": v(-122.42, -10.9) * mm, "end": v(-122.1, -11.03) * mm});
            skLineSegment(sketch, "E5049", {"start": v(-122.1, -11.03) * mm, "end": v(-121.78, -11.17) * mm});
            skLineSegment(sketch, "E5050", {"start": v(-121.78, -11.17) * mm, "end": v(-121.46, -11.32) * mm});
            skLineSegment(sketch, "E5051", {"start": v(-121.46, -11.32) * mm, "end": v(-121.15, -11.47) * mm});
            skLineSegment(sketch, "E5052", {"start": v(-121.15, -11.47) * mm, "end": v(-120.85, -11.63) * mm});
            skLineSegment(sketch, "E5053", {"start": v(-120.85, -11.63) * mm, "end": v(-120.55, -11.8) * mm});
            skLineSegment(sketch, "E5054", {"start": v(-120.55, -11.8) * mm, "end": v(-120.26, -11.97) * mm});
            skLineSegment(sketch, "E5055", {"start": v(-120.26, -11.97) * mm, "end": v(-119.97, -12.15) * mm});
            skLineSegment(sketch, "E5056", {"start": v(-119.97, -12.15) * mm, "end": v(-119.69, -12.34) * mm});
            skLineSegment(sketch, "E5057", {"start": v(-119.69, -12.34) * mm, "end": v(-119.4, -12.53) * mm});
            skLineSegment(sketch, "E5058", {"start": v(-119.4, -12.53) * mm, "end": v(-119.14, -12.73) * mm});
            skLineSegment(sketch, "E5059", {"start": v(-119.14, -12.73) * mm, "end": v(-118.87, -12.94) * mm});
            skLineSegment(sketch, "E5060", {"start": v(-118.87, -12.94) * mm, "end": v(-118.6, -13.15) * mm});
            skLineSegment(sketch, "E5061", {"start": v(-118.6, -13.15) * mm, "end": v(-118.35, -13.37) * mm});
            skLineSegment(sketch, "E5062", {"start": v(-118.35, -13.37) * mm, "end": v(-118.1, -13.6) * mm});
            skLineSegment(sketch, "E5063", {"start": v(-118.1, -13.6) * mm, "end": v(-117.86, -13.82) * mm});
            skLineSegment(sketch, "E5064", {"start": v(-117.86, -13.82) * mm, "end": v(-117.61, -14.06) * mm});
            skLineSegment(sketch, "E5065", {"start": v(-117.61, -14.06) * mm, "end": v(-117.2, -14.5) * mm});
            skLineSegment(sketch, "E5066", {"start": v(-117.2, -14.5) * mm, "end": v(-116.79, -14.97) * mm});
            skLineSegment(sketch, "E5067", {"start": v(-116.79, -14.97) * mm, "end": v(-116.4, -15.45) * mm});
            skLineSegment(sketch, "E5068", {"start": v(-116.4, -15.45) * mm, "end": v(-116, -15.96) * mm});
            skLineSegment(sketch, "E5069", {"start": v(-116, -15.96) * mm, "end": v(-115.63, -16.5) * mm});
            skLineSegment(sketch, "E5070", {"start": v(-115.63, -16.5) * mm, "end": v(-115.27, -17.05) * mm});
            skLineSegment(sketch, "E5071", {"start": v(-115.27, -17.05) * mm, "end": v(-114.92, -17.62) * mm});
            skLineSegment(sketch, "E5072", {"start": v(-114.92, -17.62) * mm, "end": v(-114.58, -18.22) * mm});
            skLineSegment(sketch, "E5073", {"start": v(-114.58, -18.22) * mm, "end": v(-114.26, -18.83) * mm});
            skLineSegment(sketch, "E5074", {"start": v(-114.26, -18.83) * mm, "end": v(-113.94, -19.47) * mm});
            skLineSegment(sketch, "E5075", {"start": v(-113.94, -19.47) * mm, "end": v(-113.64, -20.14) * mm});
            skLineSegment(sketch, "E5076", {"start": v(-113.64, -20.14) * mm, "end": v(-113.34, -20.82) * mm});
            skLineSegment(sketch, "E5077", {"start": v(-113.34, -20.82) * mm, "end": v(-113.06, -21.52) * mm});
            skLineSegment(sketch, "E5078", {"start": v(-113.06, -21.52) * mm, "end": v(-112.8, -22.25) * mm});
            skLineSegment(sketch, "E5079", {"start": v(-112.8, -22.25) * mm, "end": v(-112.54, -23) * mm});
            skLineSegment(sketch, "E5080", {"start": v(-112.54, -23) * mm, "end": v(-112.3, -23.77) * mm});
            skLineSegment(sketch, "E5081", {"start": v(-112.3, -23.77) * mm, "end": v(-112.06, -24.56) * mm});
            skLineSegment(sketch, "E5082", {"start": v(-112.06, -24.56) * mm, "end": v(-111.84, -25.36) * mm});
            skLineSegment(sketch, "E5083", {"start": v(-111.84, -25.36) * mm, "end": v(-111.64, -26.16) * mm});
            skLineSegment(sketch, "E5084", {"start": v(-111.64, -26.16) * mm, "end": v(-111.45, -26.98) * mm});
            skLineSegment(sketch, "E5085", {"start": v(-111.45, -26.98) * mm, "end": v(-111.28, -27.81) * mm});
            skLineSegment(sketch, "E5086", {"start": v(-111.28, -27.81) * mm, "end": v(-111.12, -28.65) * mm});
            skLineSegment(sketch, "E5087", {"start": v(-111.12, -28.65) * mm, "end": v(-110.98, -29.5) * mm});
            skLineSegment(sketch, "E5088", {"start": v(-110.98, -29.5) * mm, "end": v(-110.85, -30.37) * mm});
            skLineSegment(sketch, "E5089", {"start": v(-110.85, -30.37) * mm, "end": v(-110.74, -31.24) * mm});
            skLineSegment(sketch, "E5090", {"start": v(-110.74, -31.24) * mm, "end": v(-110.64, -32.12) * mm});
            skLineSegment(sketch, "E5091", {"start": v(-110.64, -32.12) * mm, "end": v(-110.56, -33.02) * mm});
            skLineSegment(sketch, "E5092", {"start": v(-110.56, -33.02) * mm, "end": v(-110.5, -33.92) * mm});
            skLineSegment(sketch, "E5093", {"start": v(-110.5, -33.92) * mm, "end": v(-110.44, -34.84) * mm});
            skLineSegment(sketch, "E5094", {"start": v(-110.44, -34.84) * mm, "end": v(-110.4, -35.76) * mm});
            skLineSegment(sketch, "E5095", {"start": v(-110.4, -35.76) * mm, "end": v(-110.38, -36.7) * mm});
            skLineSegment(sketch, "E5096", {"start": v(-110.38, -36.7) * mm, "end": v(-110.37, -37.65) * mm});
            skLineSegment(sketch, "E5097", {"start": v(-110.37, -37.65) * mm, "end": v(-110.37, -38.37) * mm});
            skLineSegment(sketch, "E5098", {"start": v(-110.37, -38.37) * mm, "end": v(-110.39, -39.09) * mm});
            skLineSegment(sketch, "E5099", {"start": v(-110.39, -39.09) * mm, "end": v(-110.4, -39.8) * mm});
            skLineSegment(sketch, "E5100", {"start": v(-110.4, -39.8) * mm, "end": v(-110.44, -40.49) * mm});
            skLineSegment(sketch, "E5101", {"start": v(-110.44, -40.49) * mm, "end": v(-110.47, -41.17) * mm});
            skLineSegment(sketch, "E5102", {"start": v(-110.47, -41.17) * mm, "end": v(-110.52, -41.85) * mm});
            skLineSegment(sketch, "E5103", {"start": v(-110.52, -41.85) * mm, "end": v(-110.57, -42.52) * mm});
            skLineSegment(sketch, "E5104", {"start": v(-110.57, -42.52) * mm, "end": v(-110.63, -43.17) * mm});
            skLineSegment(sketch, "E5105", {"start": v(-110.63, -43.17) * mm, "end": v(-110.7, -43.82) * mm});
            skLineSegment(sketch, "E5106", {"start": v(-110.7, -43.82) * mm, "end": v(-110.78, -44.46) * mm});
            skLineSegment(sketch, "E5107", {"start": v(-110.78, -44.46) * mm, "end": v(-110.87, -45.1) * mm});
            skLineSegment(sketch, "E5108", {"start": v(-110.87, -45.1) * mm, "end": v(-110.96, -45.72) * mm});
            skLineSegment(sketch, "E5109", {"start": v(-110.96, -45.72) * mm, "end": v(-111.06, -46.33) * mm});
            skLineSegment(sketch, "E5110", {"start": v(-111.06, -46.33) * mm, "end": v(-111.17, -46.93) * mm});
            skLineSegment(sketch, "E5111", {"start": v(-111.17, -46.93) * mm, "end": v(-111.3, -47.52) * mm});
            skLineSegment(sketch, "E5112", {"start": v(-111.3, -47.52) * mm, "end": v(-111.42, -48.1) * mm});
            skLineSegment(sketch, "E5113", {"start": v(-111.42, -48.1) * mm, "end": v(-111.56, -48.68) * mm});
            skLineSegment(sketch, "E5114", {"start": v(-111.56, -48.68) * mm, "end": v(-111.7, -49.25) * mm});
            skLineSegment(sketch, "E5115", {"start": v(-111.7, -49.25) * mm, "end": v(-111.85, -49.8) * mm});
            skLineSegment(sketch, "E5116", {"start": v(-111.85, -49.8) * mm, "end": v(-112.01, -50.36) * mm});
            skLineSegment(sketch, "E5117", {"start": v(-112.01, -50.36) * mm, "end": v(-112.18, -50.9) * mm});
            skLineSegment(sketch, "E5118", {"start": v(-112.18, -50.9) * mm, "end": v(-112.36, -51.42) * mm});
            skLineSegment(sketch, "E5119", {"start": v(-112.36, -51.42) * mm, "end": v(-112.54, -51.94) * mm});
            skLineSegment(sketch, "E5120", {"start": v(-112.54, -51.94) * mm, "end": v(-112.73, -52.45) * mm});
            skLineSegment(sketch, "E5121", {"start": v(-112.73, -52.45) * mm, "end": v(-112.94, -52.96) * mm});
            skLineSegment(sketch, "E5122", {"start": v(-112.94, -52.96) * mm, "end": v(-113.14, -53.45) * mm});
            skLineSegment(sketch, "E5123", {"start": v(-113.14, -53.45) * mm, "end": v(-113.36, -53.93) * mm});
            skLineSegment(sketch, "E5124", {"start": v(-113.36, -53.93) * mm, "end": v(-113.59, -54.4) * mm});
            skLineSegment(sketch, "E5125", {"start": v(-113.59, -54.4) * mm, "end": v(-113.82, -54.87) * mm});
            skLineSegment(sketch, "E5126", {"start": v(-113.82, -54.87) * mm, "end": v(-114.06, -55.33) * mm});
            skLineSegment(sketch, "E5127", {"start": v(-114.06, -55.33) * mm, "end": v(-114.31, -55.77) * mm});
            skLineSegment(sketch, "E5128", {"start": v(-114.31, -55.77) * mm, "end": v(-114.57, -56.2) * mm});
            skLineSegment(sketch, "E5129", {"start": v(-114.57, -56.2) * mm, "end": v(-114.92, -56.75) * mm});
            skLineSegment(sketch, "E5130", {"start": v(-114.92, -56.75) * mm, "end": v(-115.27, -57.26) * mm});
            skLineSegment(sketch, "E5131", {"start": v(-115.27, -57.26) * mm, "end": v(-115.62, -57.76) * mm});
            skLineSegment(sketch, "E5132", {"start": v(-115.62, -57.76) * mm, "end": v(-115.99, -58.22) * mm});
            skLineSegment(sketch, "E5133", {"start": v(-115.99, -58.22) * mm, "end": v(-116.36, -58.67) * mm});
            skLineSegment(sketch, "E5134", {"start": v(-116.36, -58.67) * mm, "end": v(-116.74, -59.1) * mm});
            skLineSegment(sketch, "E5135", {"start": v(-116.74, -59.1) * mm, "end": v(-117.12, -59.5) * mm});
            skLineSegment(sketch, "E5136", {"start": v(-117.12, -59.5) * mm, "end": v(-117.51, -59.87) * mm});
            skLineSegment(sketch, "E5137", {"start": v(-117.51, -59.87) * mm, "end": v(-117.93, -60.23) * mm});
            skLineSegment(sketch, "E5138", {"start": v(-117.93, -60.23) * mm, "end": v(-118.38, -60.6) * mm});
            skLineSegment(sketch, "E5139", {"start": v(-118.38, -60.6) * mm, "end": v(-118.86, -60.97) * mm});
            skLineSegment(sketch, "E5140", {"start": v(-118.86, -60.97) * mm, "end": v(-119.38, -61.35) * mm});
            skLineSegment(sketch, "E5141", {"start": v(-119.38, -61.35) * mm, "end": v(-119.94, -61.73) * mm});
            skLineSegment(sketch, "E5142", {"start": v(-119.94, -61.73) * mm, "end": v(-120.53, -62.11) * mm});
            skLineSegment(sketch, "E5143", {"start": v(-120.53, -62.11) * mm, "end": v(-121.15, -62.5) * mm});
            skLineSegment(sketch, "E5144", {"start": v(-121.15, -62.5) * mm, "end": v(-121.82, -62.9) * mm});
            skLineSegment(sketch, "E5145", {"start": v(-121.82, -62.9) * mm, "end": v(-121.14, -63.3) * mm});
            skLineSegment(sketch, "E5146", {"start": v(-121.14, -63.3) * mm, "end": v(-120.5, -63.7) * mm});
            skLineSegment(sketch, "E5147", {"start": v(-120.5, -63.7) * mm, "end": v(-119.88, -64.1) * mm});
            skLineSegment(sketch, "E5148", {"start": v(-119.88, -64.1) * mm, "end": v(-119.31, -64.49) * mm});
            skLineSegment(sketch, "E5149", {"start": v(-119.31, -64.49) * mm, "end": v(-118.78, -64.87) * mm});
            skLineSegment(sketch, "E5150", {"start": v(-118.78, -64.87) * mm, "end": v(-118.28, -65.24) * mm});
            skLineSegment(sketch, "E5151", {"start": v(-118.28, -65.24) * mm, "end": v(-117.82, -65.6) * mm});
            skLineSegment(sketch, "E5152", {"start": v(-117.82, -65.6) * mm, "end": v(-117.4, -65.96) * mm});
            skLineSegment(sketch, "E5153", {"start": v(-117.4, -65.96) * mm, "end": v(-117, -66.33) * mm});
            skLineSegment(sketch, "E5154", {"start": v(-117, -66.33) * mm, "end": v(-116.6, -66.72) * mm});
            skLineSegment(sketch, "E5155", {"start": v(-116.6, -66.72) * mm, "end": v(-116.2, -67.13) * mm});
            skLineSegment(sketch, "E5156", {"start": v(-116.2, -67.13) * mm, "end": v(-115.8, -67.57) * mm});
            skLineSegment(sketch, "E5157", {"start": v(-115.8, -67.57) * mm, "end": v(-115.42, -68.04) * mm});
            skLineSegment(sketch, "E5158", {"start": v(-115.42, -68.04) * mm, "end": v(-115.04, -68.53) * mm});
            skLineSegment(sketch, "E5159", {"start": v(-115.04, -68.53) * mm, "end": v(-114.67, -69.04) * mm});
            skLineSegment(sketch, "E5160", {"start": v(-114.67, -69.04) * mm, "end": v(-114.3, -69.58) * mm});
            skLineSegment(sketch, "E5161", {"start": v(-114.3, -69.58) * mm, "end": v(-113.97, -70.07) * mm});
            skLineSegment(sketch, "E5162", {"start": v(-113.97, -70.07) * mm, "end": v(-113.65, -70.57) * mm});
            skLineSegment(sketch, "E5163", {"start": v(-113.65, -70.57) * mm, "end": v(-113.35, -71.1) * mm});
            skLineSegment(sketch, "E5164", {"start": v(-113.35, -71.1) * mm, "end": v(-113.05, -71.63) * mm});
            skLineSegment(sketch, "E5165", {"start": v(-113.05, -71.63) * mm, "end": v(-112.76, -72.18) * mm});
            skLineSegment(sketch, "E5166", {"start": v(-112.76, -72.18) * mm, "end": v(-112.48, -72.74) * mm});
            skLineSegment(sketch, "E5167", {"start": v(-112.48, -72.74) * mm, "end": v(-112.22, -73.33) * mm});
            skLineSegment(sketch, "E5168", {"start": v(-112.22, -73.33) * mm, "end": v(-111.96, -73.92) * mm});
            skLineSegment(sketch, "E5169", {"start": v(-111.96, -73.92) * mm, "end": v(-111.7, -74.53) * mm});
            skLineSegment(sketch, "E5170", {"start": v(-111.7, -74.53) * mm, "end": v(-111.47, -75.16) * mm});
            skLineSegment(sketch, "E5171", {"start": v(-111.47, -75.16) * mm, "end": v(-111.24, -75.8) * mm});
            skLineSegment(sketch, "E5172", {"start": v(-111.24, -75.8) * mm, "end": v(-111.02, -76.46) * mm});
            skLineSegment(sketch, "E5173", {"start": v(-111.02, -76.46) * mm, "end": v(-110.8, -77.14) * mm});
            skLineSegment(sketch, "E5174", {"start": v(-110.8, -77.14) * mm, "end": v(-110.6, -77.83) * mm});
            skLineSegment(sketch, "E5175", {"start": v(-110.6, -77.83) * mm, "end": v(-110.41, -78.53) * mm});
            skLineSegment(sketch, "E5176", {"start": v(-110.41, -78.53) * mm, "end": v(-110.23, -79.25) * mm});
            skLineSegment(sketch, "E5177", {"start": v(-110.23, -79.25) * mm, "end": v(-110.06, -79.98) * mm});
            skLineSegment(sketch, "E5178", {"start": v(-110.06, -79.98) * mm, "end": v(-109.9, -80.72) * mm});
            skLineSegment(sketch, "E5179", {"start": v(-109.9, -80.72) * mm, "end": v(-109.75, -81.47) * mm});
            skLineSegment(sketch, "E5180", {"start": v(-109.75, -81.47) * mm, "end": v(-109.6, -82.23) * mm});
            skLineSegment(sketch, "E5181", {"start": v(-109.6, -82.23) * mm, "end": v(-109.48, -83) * mm});
            skLineSegment(sketch, "E5182", {"start": v(-109.48, -83) * mm, "end": v(-109.36, -83.78) * mm});
            skLineSegment(sketch, "E5183", {"start": v(-109.36, -83.78) * mm, "end": v(-109.26, -84.57) * mm});
            skLineSegment(sketch, "E5184", {"start": v(-109.26, -84.57) * mm, "end": v(-109.16, -85.36) * mm});
            skLineSegment(sketch, "E5185", {"start": v(-109.16, -85.36) * mm, "end": v(-109.08, -86.17) * mm});
            skLineSegment(sketch, "E5186", {"start": v(-109.08, -86.17) * mm, "end": v(-109, -86.99) * mm});
            skLineSegment(sketch, "E5187", {"start": v(-109, -86.99) * mm, "end": v(-108.95, -87.8) * mm});
            skLineSegment(sketch, "E5188", {"start": v(-108.95, -87.8) * mm, "end": v(-108.9, -88.64) * mm});
            skLineSegment(sketch, "E5189", {"start": v(-108.9, -88.64) * mm, "end": v(-108.86, -89.49) * mm});
            skLineSegment(sketch, "E5190", {"start": v(-108.86, -89.49) * mm, "end": v(-108.83, -90.34) * mm});
            skLineSegment(sketch, "E5191", {"start": v(-108.83, -90.34) * mm, "end": v(-108.82, -91.2) * mm});
            skLineSegment(sketch, "E5192", {"start": v(-108.82, -91.2) * mm, "end": v(-108.8, -92.07) * mm});
            skLineSegment(sketch, "E5193", {"start": v(-108.8, -92.07) * mm, "end": v(-108.81, -92.85) * mm});
            skLineSegment(sketch, "E5194", {"start": v(-108.81, -92.85) * mm, "end": v(-108.83, -93.62) * mm});
            skLineSegment(sketch, "E5195", {"start": v(-108.83, -93.62) * mm, "end": v(-108.85, -94.38) * mm});
            skLineSegment(sketch, "E5196", {"start": v(-108.85, -94.38) * mm, "end": v(-108.88, -95.13) * mm});
            skLineSegment(sketch, "E5197", {"start": v(-108.88, -95.13) * mm, "end": v(-108.92, -95.88) * mm});
            skLineSegment(sketch, "E5198", {"start": v(-108.92, -95.88) * mm, "end": v(-108.97, -96.6) * mm});
            skLineSegment(sketch, "E5199", {"start": v(-108.97, -96.6) * mm, "end": v(-109.03, -97.33) * mm});
            skLineSegment(sketch, "E5200", {"start": v(-109.03, -97.33) * mm, "end": v(-109.1, -98.04) * mm});
            skLineSegment(sketch, "E5201", {"start": v(-109.1, -98.04) * mm, "end": v(-109.17, -98.74) * mm});
            skLineSegment(sketch, "E5202", {"start": v(-109.17, -98.74) * mm, "end": v(-109.25, -99.43) * mm});
            skLineSegment(sketch, "E5203", {"start": v(-109.25, -99.43) * mm, "end": v(-109.34, -100.11) * mm});
            skLineSegment(sketch, "E5204", {"start": v(-109.34, -100.11) * mm, "end": v(-109.45, -100.79) * mm});
            skLineSegment(sketch, "E5205", {"start": v(-109.45, -100.79) * mm, "end": v(-109.56, -101.45) * mm});
            skLineSegment(sketch, "E5206", {"start": v(-109.56, -101.45) * mm, "end": v(-109.68, -102.1) * mm});
            skLineSegment(sketch, "E5207", {"start": v(-109.68, -102.1) * mm, "end": v(-109.8, -102.74) * mm});
            skLineSegment(sketch, "E5208", {"start": v(-109.8, -102.74) * mm, "end": v(-109.94, -103.37) * mm});
            skLineSegment(sketch, "E5209", {"start": v(-109.94, -103.37) * mm, "end": v(-110.09, -104) * mm});
            skLineSegment(sketch, "E5210", {"start": v(-110.09, -104) * mm, "end": v(-110.24, -104.6) * mm});
            skLineSegment(sketch, "E5211", {"start": v(-110.24, -104.6) * mm, "end": v(-110.4, -105.2) * mm});
            skLineSegment(sketch, "E5212", {"start": v(-110.4, -105.2) * mm, "end": v(-110.58, -105.8) * mm});
            skLineSegment(sketch, "E5213", {"start": v(-110.58, -105.8) * mm, "end": v(-110.76, -106.38) * mm});
            skLineSegment(sketch, "E5214", {"start": v(-110.76, -106.38) * mm, "end": v(-110.95, -106.95) * mm});
            skLineSegment(sketch, "E5215", {"start": v(-110.95, -106.95) * mm, "end": v(-111.15, -107.51) * mm});
            skLineSegment(sketch, "E5216", {"start": v(-111.15, -107.51) * mm, "end": v(-111.35, -108.07) * mm});
            skLineSegment(sketch, "E5217", {"start": v(-111.35, -108.07) * mm, "end": v(-111.57, -108.6) * mm});
            skLineSegment(sketch, "E5218", {"start": v(-111.57, -108.6) * mm, "end": v(-111.8, -109.14) * mm});
            skLineSegment(sketch, "E5219", {"start": v(-111.8, -109.14) * mm, "end": v(-112.03, -109.66) * mm});
            skLineSegment(sketch, "E5220", {"start": v(-112.03, -109.66) * mm, "end": v(-112.27, -110.17) * mm});
            skLineSegment(sketch, "E5221", {"start": v(-112.27, -110.17) * mm, "end": v(-112.52, -110.68) * mm});
            skLineSegment(sketch, "E5222", {"start": v(-112.52, -110.68) * mm, "end": v(-112.78, -111.17) * mm});
            skLineSegment(sketch, "E5223", {"start": v(-112.78, -111.17) * mm, "end": v(-113.05, -111.65) * mm});
            skLineSegment(sketch, "E5224", {"start": v(-113.05, -111.65) * mm, "end": v(-113.33, -112.12) * mm});
            skLineSegment(sketch, "E5225", {"start": v(-113.33, -112.12) * mm, "end": v(-113.67, -112.68) * mm});
            skLineSegment(sketch, "E5226", {"start": v(-113.67, -112.68) * mm, "end": v(-114.02, -113.2) * mm});
            skLineSegment(sketch, "E5227", {"start": v(-114.02, -113.2) * mm, "end": v(-114.37, -113.7) * mm});
            skLineSegment(sketch, "E5228", {"start": v(-114.37, -113.7) * mm, "end": v(-114.72, -114.16) * mm});
            skLineSegment(sketch, "E5229", {"start": v(-114.72, -114.16) * mm, "end": v(-115.07, -114.59) * mm});
            skLineSegment(sketch, "E5230", {"start": v(-115.07, -114.59) * mm, "end": v(-115.43, -114.99) * mm});
            skLineSegment(sketch, "E5231", {"start": v(-115.43, -114.99) * mm, "end": v(-115.8, -115.36) * mm});
            skLineSegment(sketch, "E5232", {"start": v(-115.8, -115.36) * mm, "end": v(-116.15, -115.7) * mm});
            skLineSegment(sketch, "E5233", {"start": v(-116.15, -115.7) * mm, "end": v(-116.53, -116.02) * mm});
            skLineSegment(sketch, "E5234", {"start": v(-116.53, -116.02) * mm, "end": v(-116.93, -116.33) * mm});
            skLineSegment(sketch, "E5235", {"start": v(-116.93, -116.33) * mm, "end": v(-117.36, -116.62) * mm});
            skLineSegment(sketch, "E5236", {"start": v(-117.36, -116.62) * mm, "end": v(-117.81, -116.9) * mm});
            skLineSegment(sketch, "E5237", {"start": v(-117.81, -116.9) * mm, "end": v(-118.29, -117.18) * mm});
            skLineSegment(sketch, "E5238", {"start": v(-118.29, -117.18) * mm, "end": v(-118.78, -117.45) * mm});
            skLineSegment(sketch, "E5239", {"start": v(-118.78, -117.45) * mm, "end": v(-119.3, -117.7) * mm});
            skLineSegment(sketch, "E5240", {"start": v(-119.3, -117.7) * mm, "end": v(-119.86, -117.94) * mm});
            skLineSegment(sketch, "E5241", {"start": v(-119.86, -117.94) * mm, "end": v(-120.26, -118.1) * mm});
            skLineSegment(sketch, "E5242", {"start": v(-120.26, -118.1) * mm, "end": v(-120.66, -118.26) * mm});
            skLineSegment(sketch, "E5243", {"start": v(-120.66, -118.26) * mm, "end": v(-121.07, -118.4) * mm});
            skLineSegment(sketch, "E5244", {"start": v(-121.07, -118.4) * mm, "end": v(-121.5, -118.55) * mm});
            skLineSegment(sketch, "E5245", {"start": v(-121.5, -118.55) * mm, "end": v(-121.92, -118.68) * mm});
            skLineSegment(sketch, "E5246", {"start": v(-121.92, -118.68) * mm, "end": v(-122.36, -118.8) * mm});
            skLineSegment(sketch, "E5247", {"start": v(-122.36, -118.8) * mm, "end": v(-122.8, -118.91) * mm});
            skLineSegment(sketch, "E5248", {"start": v(-122.8, -118.91) * mm, "end": v(-123.25, -119.02) * mm});
            skLineSegment(sketch, "E5249", {"start": v(-123.25, -119.02) * mm, "end": v(-123.7, -119.12) * mm});
            skLineSegment(sketch, "E5250", {"start": v(-123.7, -119.12) * mm, "end": v(-124.17, -119.21) * mm});
            skLineSegment(sketch, "E5251", {"start": v(-124.17, -119.21) * mm, "end": v(-124.64, -119.3) * mm});
            skLineSegment(sketch, "E5252", {"start": v(-124.64, -119.3) * mm, "end": v(-125.12, -119.37) * mm});
            skLineSegment(sketch, "E5253", {"start": v(-125.12, -119.37) * mm, "end": v(-125.6, -119.44) * mm});
            skLineSegment(sketch, "E5254", {"start": v(-125.6, -119.44) * mm, "end": v(-126.1, -119.5) * mm});
            skLineSegment(sketch, "E5255", {"start": v(-126.1, -119.5) * mm, "end": v(-126.6, -119.55) * mm});
            skLineSegment(sketch, "E5256", {"start": v(-126.6, -119.55) * mm, "end": v(-127.1, -119.6) * mm});
            skLineSegment(sketch, "E5257", {"start": v(-127.1, -119.6) * mm, "end": v(-127.66, -119.67) * mm});
            skLineSegment(sketch, "E5258", {"start": v(-127.66, -119.67) * mm, "end": v(-127.66, -111.5) * mm});
            skLineSegment(sketch, "E5259", {"start": v(-127.66, -111.5) * mm, "end": v(-127.45, -111.37) * mm});
            skLineSegment(sketch, "E5260", {"start": v(-127.45, -111.37) * mm, "end": v(-127.25, -111.24) * mm});
            skLineSegment(sketch, "E5261", {"start": v(-127.25, -111.24) * mm, "end": v(-127.06, -111.1) * mm});
            skLineSegment(sketch, "E5262", {"start": v(-127.06, -111.1) * mm, "end": v(-126.9, -110.96) * mm});
            skLineSegment(sketch, "E5263", {"start": v(-126.9, -110.96) * mm, "end": v(-126.73, -110.81) * mm});
            skLineSegment(sketch, "E5264", {"start": v(-126.73, -110.81) * mm, "end": v(-126.59, -110.65) * mm});
            skLineSegment(sketch, "E5265", {"start": v(-126.59, -110.65) * mm, "end": v(-126.46, -110.49) * mm});
            skLineSegment(sketch, "E5266", {"start": v(-126.46, -110.49) * mm, "end": v(-126.34, -110.31) * mm});
            skLineSegment(sketch, "E5267", {"start": v(-126.34, -110.31) * mm, "end": v(-126.23, -110.12) * mm});
            skLineSegment(sketch, "E5268", {"start": v(-126.23, -110.12) * mm, "end": v(-126.13, -109.9) * mm});
            skLineSegment(sketch, "E5269", {"start": v(-126.13, -109.9) * mm, "end": v(-126.03, -109.67) * mm});
            skLineSegment(sketch, "E5270", {"start": v(-126.03, -109.67) * mm, "end": v(-125.93, -109.4) * mm});
            skLineSegment(sketch, "E5271", {"start": v(-125.93, -109.4) * mm, "end": v(-125.84, -109.12) * mm});
            skLineSegment(sketch, "E5272", {"start": v(-125.84, -109.12) * mm, "end": v(-125.75, -108.8) * mm});
            skLineSegment(sketch, "E5273", {"start": v(-125.75, -108.8) * mm, "end": v(-125.66, -108.47) * mm});
            skLineSegment(sketch, "E5274", {"start": v(-125.66, -108.47) * mm, "end": v(-125.58, -108.11) * mm});
            skLineSegment(sketch, "E5275", {"start": v(-125.58, -108.11) * mm, "end": v(-125.46, -107.53) * mm});
            skLineSegment(sketch, "E5276", {"start": v(-125.46, -107.53) * mm, "end": v(-125.35, -106.92) * mm});
            skLineSegment(sketch, "E5277", {"start": v(-125.35, -106.92) * mm, "end": v(-125.26, -106.28) * mm});
            skLineSegment(sketch, "E5278", {"start": v(-125.26, -106.28) * mm, "end": v(-125.19, -105.61) * mm});
            skLineSegment(sketch, "E5279", {"start": v(-125.19, -105.61) * mm, "end": v(-125.13, -104.92) * mm});
            skLineSegment(sketch, "E5280", {"start": v(-125.13, -104.92) * mm, "end": v(-125.1, -104.2) * mm});
            skLineSegment(sketch, "E5281", {"start": v(-125.1, -104.2) * mm, "end": v(-125.07, -103.46) * mm});
            skLineSegment(sketch, "E5282", {"start": v(-125.07, -103.46) * mm, "end": v(-125.06, -102.68) * mm});
            skLineSegment(sketch, "E5283", {"start": v(-125.06, -102.68) * mm, "end": v(-125.06, -75.8) * mm});
            skLineSegment(sketch, "E5284", {"start": v(-125.06, -75.8) * mm, "end": v(-125.08, -75.37) * mm});
            skLineSegment(sketch, "E5285", {"start": v(-125.08, -75.37) * mm, "end": v(-125.12, -74.82) * mm});
            skLineSegment(sketch, "E5286", {"start": v(-125.12, -74.82) * mm, "end": v(-125.2, -74.13) * mm});
            skLineSegment(sketch, "E5287", {"start": v(-125.2, -74.13) * mm, "end": v(-125.32, -73.31) * mm});
            skLineSegment(sketch, "E5288", {"start": v(-125.32, -73.31) * mm, "end": v(-125.45, -72.47) * mm});
            skLineSegment(sketch, "E5289", {"start": v(-125.45, -72.47) * mm, "end": v(-125.57, -71.71) * mm});
            skLineSegment(sketch, "E5290", {"start": v(-125.57, -71.71) * mm, "end": v(-125.7, -71.04) * mm});
            skLineSegment(sketch, "E5291", {"start": v(-125.7, -71.04) * mm, "end": v(-125.82, -70.44) * mm});
            skLineSegment(sketch, "E5292", {"start": v(-125.82, -70.44) * mm, "end": v(-125.9, -70.16) * mm});
            skLineSegment(sketch, "E5293", {"start": v(-125.9, -70.16) * mm, "end": v(-125.99, -69.88) * mm});
            skLineSegment(sketch, "E5294", {"start": v(-125.99, -69.88) * mm, "end": v(-126.08, -69.62) * mm});
            skLineSegment(sketch, "E5295", {"start": v(-126.08, -69.62) * mm, "end": v(-126.17, -69.38) * mm});
            skLineSegment(sketch, "E5296", {"start": v(-126.17, -69.38) * mm, "end": v(-126.27, -69.15) * mm});
            skLineSegment(sketch, "E5297", {"start": v(-126.27, -69.15) * mm, "end": v(-126.37, -68.94) * mm});
            skLineSegment(sketch, "E5298", {"start": v(-126.37, -68.94) * mm, "end": v(-126.47, -68.74) * mm});
            skLineSegment(sketch, "E5299", {"start": v(-126.47, -68.74) * mm, "end": v(-126.58, -68.56) * mm});
            skLineSegment(sketch, "E5300", {"start": v(-126.58, -68.56) * mm, "end": v(-126.7, -68.38) * mm});
            skLineSegment(sketch, "E5301", {"start": v(-126.7, -68.38) * mm, "end": v(-126.83, -68.2) * mm});
            skLineSegment(sketch, "E5302", {"start": v(-126.83, -68.2) * mm, "end": v(-126.98, -68.02) * mm});
            skLineSegment(sketch, "E5303", {"start": v(-126.98, -68.02) * mm, "end": v(-127.14, -67.85) * mm});
            skLineSegment(sketch, "E5304", {"start": v(-127.14, -67.85) * mm, "end": v(-127.32, -67.67) * mm});
            skLineSegment(sketch, "E5305", {"start": v(-127.32, -67.67) * mm, "end": v(-127.51, -67.5) * mm});
            skLineSegment(sketch, "E5306", {"start": v(-127.51, -67.5) * mm, "end": v(-127.72, -67.32) * mm});
            skLineSegment(sketch, "E5307", {"start": v(-127.72, -67.32) * mm, "end": v(-127.94, -67.14) * mm});
            skLineSegment(sketch, "E5308", {"start": v(-127.94, -67.14) * mm, "end": v(-127.94, -58.88) * mm});
            skLineSegment(sketch, "E5309", {"start": v(-127.94, -58.88) * mm, "end": v(-127.7, -58.69) * mm});
            skLineSegment(sketch, "E5310", {"start": v(-127.7, -58.69) * mm, "end": v(-127.5, -58.49) * mm});
            skLineSegment(sketch, "E5311", {"start": v(-127.5, -58.49) * mm, "end": v(-127.3, -58.29) * mm});
            skLineSegment(sketch, "E5312", {"start": v(-127.3, -58.29) * mm, "end": v(-127.1, -58.09) * mm});
            skLineSegment(sketch, "E5313", {"start": v(-127.1, -58.09) * mm, "end": v(-126.94, -57.88) * mm});
            skLineSegment(sketch, "E5314", {"start": v(-126.94, -57.88) * mm, "end": v(-126.78, -57.68) * mm});
            skLineSegment(sketch, "E5315", {"start": v(-126.78, -57.68) * mm, "end": v(-126.64, -57.48) * mm});
            skLineSegment(sketch, "E5316", {"start": v(-126.64, -57.48) * mm, "end": v(-126.52, -57.27) * mm});
            skLineSegment(sketch, "E5317", {"start": v(-126.52, -57.27) * mm, "end": v(-126.4, -57.05) * mm});
            skLineSegment(sketch, "E5318", {"start": v(-126.4, -57.05) * mm, "end": v(-126.3, -56.81) * mm});
            skLineSegment(sketch, "E5319", {"start": v(-126.3, -56.81) * mm, "end": v(-126.2, -56.55) * mm});
            skLineSegment(sketch, "E5320", {"start": v(-126.2, -56.55) * mm, "end": v(-126.1, -56.26) * mm});
            skLineSegment(sketch, "E5321", {"start": v(-126.1, -56.26) * mm, "end": v(-126.02, -55.95) * mm});
            skLineSegment(sketch, "E5322", {"start": v(-126.02, -55.95) * mm, "end": v(-125.93, -55.61) * mm});
            skLineSegment(sketch, "E5323", {"start": v(-125.93, -55.61) * mm, "end": v(-125.85, -55.25) * mm});
            skLineSegment(sketch, "E5324", {"start": v(-125.85, -55.25) * mm, "end": v(-125.78, -54.87) * mm});
            skLineSegment(sketch, "E5325", {"start": v(-125.78, -54.87) * mm, "end": v(-125.7, -54.4) * mm});
            skLineSegment(sketch, "E5326", {"start": v(-125.7, -54.4) * mm, "end": v(-125.59, -53.8) * mm});
            skLineSegment(sketch, "E5327", {"start": v(-125.59, -53.8) * mm, "end": v(-125.34, -52.12) * mm});
            skLineSegment(sketch, "E5328", {"start": v(-125.34, -52.12) * mm, "end": v(-125.13, -50.59) * mm});
            skLineSegment(sketch, "E5329", {"start": v(-125.13, -50.59) * mm, "end": v(-125.08, -50.14) * mm});
            skLineSegment(sketch, "E5330", {"start": v(-125.08, -50.14) * mm, "end": v(-125.06, -49.92) * mm});
            skLineSegment(sketch, "E5331", {"start": v(-125.06, -49.92) * mm, "end": v(-125.06, -28.21) * mm});
            skLineSegment(sketch, "E5332", {"start": v(-125.06, -28.21) * mm, "end": v(-125.07, -27.71) * mm});
            skLineSegment(sketch, "E5333", {"start": v(-125.07, -27.71) * mm, "end": v(-125.12, -27.07) * mm});
            skLineSegment(sketch, "E5334", {"start": v(-125.12, -27.07) * mm, "end": v(-125.2, -26.3) * mm});
            skLineSegment(sketch, "E5335", {"start": v(-125.2, -26.3) * mm, "end": v(-125.3, -25.38) * mm});
            skLineSegment(sketch, "E5336", {"start": v(-125.3, -25.38) * mm, "end": v(-125.74, -21.06) * mm});
            skLineSegment(sketch, "E5337", {"start": v(-125.74, -21.06) * mm, "end": v(-125.8, -20.81) * mm});
            skLineSegment(sketch, "E5338", {"start": v(-125.8, -20.81) * mm, "end": v(-125.86, -20.57) * mm});
            skLineSegment(sketch, "E5339", {"start": v(-125.86, -20.57) * mm, "end": v(-125.94, -20.33) * mm});
            skLineSegment(sketch, "E5340", {"start": v(-125.94, -20.33) * mm, "end": v(-126.03, -20.08) * mm});
            skLineSegment(sketch, "E5341", {"start": v(-126.03, -20.08) * mm, "end": v(-126.13, -19.84) * mm});
            skLineSegment(sketch, "E5342", {"start": v(-126.13, -19.84) * mm, "end": v(-126.24, -19.6) * mm});
            skLineSegment(sketch, "E5343", {"start": v(-126.24, -19.6) * mm, "end": v(-126.36, -19.37) * mm});
            skLineSegment(sketch, "E5344", {"start": v(-126.36, -19.37) * mm, "end": v(-126.5, -19.13) * mm});
            skLineSegment(sketch, "E5345", {"start": v(-126.5, -19.13) * mm, "end": v(-126.63, -18.9) * mm});
            skLineSegment(sketch, "E5346", {"start": v(-126.63, -18.9) * mm, "end": v(-126.79, -18.66) * mm});
            skLineSegment(sketch, "E5347", {"start": v(-126.79, -18.66) * mm, "end": v(-126.95, -18.43) * mm});
            skLineSegment(sketch, "E5348", {"start": v(-126.95, -18.43) * mm, "end": v(-127.13, -18.2) * mm});
            skLineSegment(sketch, "E5349", {"start": v(-127.13, -18.2) * mm, "end": v(-127.31, -17.97) * mm});
            skLineSegment(sketch, "E5350", {"start": v(-127.31, -17.97) * mm, "end": v(-127.51, -17.74) * mm});
            skLineSegment(sketch, "E5351", {"start": v(-127.51, -17.74) * mm, "end": v(-127.72, -17.5) * mm});
            skLineSegment(sketch, "E5352", {"start": v(-127.72, -17.5) * mm, "end": v(-127.94, -17.28) * mm});
            skLineSegment(sketch, "E5353", {"start": v(-130.3, -254.07) * mm, "end": v(-130.83, -253.93) * mm});
            skLineSegment(sketch, "E5354", {"start": v(-130.83, -253.93) * mm, "end": v(-131.34, -253.77) * mm});
            skLineSegment(sketch, "E5355", {"start": v(-131.34, -253.77) * mm, "end": v(-131.85, -253.6) * mm});
            skLineSegment(sketch, "E5356", {"start": v(-131.85, -253.6) * mm, "end": v(-132.35, -253.4) * mm});
            skLineSegment(sketch, "E5357", {"start": v(-132.35, -253.4) * mm, "end": v(-132.84, -253.17) * mm});
            skLineSegment(sketch, "E5358", {"start": v(-132.84, -253.17) * mm, "end": v(-133.33, -252.93) * mm});
            skLineSegment(sketch, "E5359", {"start": v(-133.33, -252.93) * mm, "end": v(-133.8, -252.67) * mm});
            skLineSegment(sketch, "E5360", {"start": v(-133.8, -252.67) * mm, "end": v(-134.27, -252.39) * mm});
            skLineSegment(sketch, "E5361", {"start": v(-134.27, -252.39) * mm, "end": v(-134.74, -252.08) * mm});
            skLineSegment(sketch, "E5362", {"start": v(-134.74, -252.08) * mm, "end": v(-135.2, -251.76) * mm});
            skLineSegment(sketch, "E5363", {"start": v(-135.2, -251.76) * mm, "end": v(-135.64, -251.42) * mm});
            skLineSegment(sketch, "E5364", {"start": v(-135.64, -251.42) * mm, "end": v(-136.08, -251.05) * mm});
            skLineSegment(sketch, "E5365", {"start": v(-136.08, -251.05) * mm, "end": v(-136.51, -250.67) * mm});
            skLineSegment(sketch, "E5366", {"start": v(-136.51, -250.67) * mm, "end": v(-136.94, -250.26) * mm});
            skLineSegment(sketch, "E5367", {"start": v(-136.94, -250.26) * mm, "end": v(-137.36, -249.83) * mm});
            skLineSegment(sketch, "E5368", {"start": v(-137.36, -249.83) * mm, "end": v(-137.77, -249.39) * mm});
            skLineSegment(sketch, "E5369", {"start": v(-137.77, -249.39) * mm, "end": v(-138.18, -248.92) * mm});
            skLineSegment(sketch, "E5370", {"start": v(-138.18, -248.92) * mm, "end": v(-138.58, -248.42) * mm});
            skLineSegment(sketch, "E5371", {"start": v(-138.58, -248.42) * mm, "end": v(-138.98, -247.9) * mm});
            skLineSegment(sketch, "E5372", {"start": v(-138.98, -247.9) * mm, "end": v(-139.37, -247.36) * mm});
            skLineSegment(sketch, "E5373", {"start": v(-139.37, -247.36) * mm, "end": v(-139.76, -246.78) * mm});
            skLineSegment(sketch, "E5374", {"start": v(-139.76, -246.78) * mm, "end": v(-140.15, -246.19) * mm});
            skLineSegment(sketch, "E5375", {"start": v(-140.15, -246.19) * mm, "end": v(-140.54, -245.56) * mm});
            skLineSegment(sketch, "E5376", {"start": v(-140.54, -245.56) * mm, "end": v(-140.92, -244.92) * mm});
            skLineSegment(sketch, "E5377", {"start": v(-140.92, -244.92) * mm, "end": v(-141.3, -244.24) * mm});
            skLineSegment(sketch, "E5378", {"start": v(-141.3, -244.24) * mm, "end": v(-141.67, -243.54) * mm});
            skLineSegment(sketch, "E5379", {"start": v(-141.67, -243.54) * mm, "end": v(-142.04, -242.82) * mm});
            skLineSegment(sketch, "E5380", {"start": v(-142.04, -242.82) * mm, "end": v(-142.4, -242.07) * mm});
            skLineSegment(sketch, "E5381", {"start": v(-142.4, -242.07) * mm, "end": v(-142.77, -241.3) * mm});
            skLineSegment(sketch, "E5382", {"start": v(-142.77, -241.3) * mm, "end": v(-143.13, -240.5) * mm});
            skLineSegment(sketch, "E5383", {"start": v(-143.13, -240.5) * mm, "end": v(-143.48, -239.66) * mm});
            skLineSegment(sketch, "E5384", {"start": v(-143.48, -239.66) * mm, "end": v(-143.83, -238.81) * mm});
            skLineSegment(sketch, "E5385", {"start": v(-143.83, -238.81) * mm, "end": v(-144.21, -237.86) * mm});
            skLineSegment(sketch, "E5386", {"start": v(-144.21, -237.86) * mm, "end": v(-144.58, -236.88) * mm});
            skLineSegment(sketch, "E5387", {"start": v(-144.58, -236.88) * mm, "end": v(-144.94, -235.89) * mm});
            skLineSegment(sketch, "E5388", {"start": v(-144.94, -235.89) * mm, "end": v(-145.28, -234.87) * mm});
            skLineSegment(sketch, "E5389", {"start": v(-145.28, -234.87) * mm, "end": v(-145.62, -233.84) * mm});
            skLineSegment(sketch, "E5390", {"start": v(-145.62, -233.84) * mm, "end": v(-145.94, -232.78) * mm});
            skLineSegment(sketch, "E5391", {"start": v(-145.94, -232.78) * mm, "end": v(-146.25, -231.7) * mm});
            skLineSegment(sketch, "E5392", {"start": v(-146.25, -231.7) * mm, "end": v(-146.55, -230.61) * mm});
            skLineSegment(sketch, "E5393", {"start": v(-146.55, -230.61) * mm, "end": v(-146.83, -229.5) * mm});
            skLineSegment(sketch, "E5394", {"start": v(-146.83, -229.5) * mm, "end": v(-147.1, -228.36) * mm});
            skLineSegment(sketch, "E5395", {"start": v(-147.1, -228.36) * mm, "end": v(-147.37, -227.2) * mm});
            skLineSegment(sketch, "E5396", {"start": v(-147.37, -227.2) * mm, "end": v(-147.62, -226.03) * mm});
            skLineSegment(sketch, "E5397", {"start": v(-147.62, -226.03) * mm, "end": v(-147.87, -224.83) * mm});
            skLineSegment(sketch, "E5398", {"start": v(-147.87, -224.83) * mm, "end": v(-148.1, -223.61) * mm});
            skLineSegment(sketch, "E5399", {"start": v(-148.1, -223.61) * mm, "end": v(-148.31, -222.38) * mm});
            skLineSegment(sketch, "E5400", {"start": v(-148.31, -222.38) * mm, "end": v(-148.52, -221.12) * mm});
            skLineSegment(sketch, "E5401", {"start": v(-148.52, -221.12) * mm, "end": v(-148.71, -219.84) * mm});
            skLineSegment(sketch, "E5402", {"start": v(-148.71, -219.84) * mm, "end": v(-148.9, -218.55) * mm});
            skLineSegment(sketch, "E5403", {"start": v(-148.9, -218.55) * mm, "end": v(-149.06, -217.25) * mm});
            skLineSegment(sketch, "E5404", {"start": v(-149.06, -217.25) * mm, "end": v(-149.22, -215.93) * mm});
            skLineSegment(sketch, "E5405", {"start": v(-149.22, -215.93) * mm, "end": v(-149.36, -214.6) * mm});
            skLineSegment(sketch, "E5406", {"start": v(-149.36, -214.6) * mm, "end": v(-149.5, -213.25) * mm});
            skLineSegment(sketch, "E5407", {"start": v(-149.5, -213.25) * mm, "end": v(-149.61, -211.9) * mm});
            skLineSegment(sketch, "E5408", {"start": v(-149.61, -211.9) * mm, "end": v(-149.72, -210.52) * mm});
            skLineSegment(sketch, "E5409", {"start": v(-149.72, -210.52) * mm, "end": v(-149.81, -209.13) * mm});
            skLineSegment(sketch, "E5410", {"start": v(-149.81, -209.13) * mm, "end": v(-149.9, -207.73) * mm});
            skLineSegment(sketch, "E5411", {"start": v(-149.9, -207.73) * mm, "end": v(-149.96, -206.31) * mm});
            skLineSegment(sketch, "E5412", {"start": v(-149.96, -206.31) * mm, "end": v(-150.02, -204.88) * mm});
            skLineSegment(sketch, "E5413", {"start": v(-150.02, -204.88) * mm, "end": v(-150.06, -203.44) * mm});
            skLineSegment(sketch, "E5414", {"start": v(-150.06, -203.44) * mm, "end": v(-150.1, -201.98) * mm});
            skLineSegment(sketch, "E5415", {"start": v(-150.1, -201.98) * mm, "end": v(-150.11, -200.5) * mm});
            skLineSegment(sketch, "E5416", {"start": v(-150.11, -200.5) * mm, "end": v(-150.12, -199.02) * mm});
            skLineSegment(sketch, "E5417", {"start": v(-150.12, -199.02) * mm, "end": v(-150.11, -197.54) * mm});
            skLineSegment(sketch, "E5418", {"start": v(-150.11, -197.54) * mm, "end": v(-150.1, -196.08) * mm});
            skLineSegment(sketch, "E5419", {"start": v(-150.1, -196.08) * mm, "end": v(-150.06, -194.63) * mm});
            skLineSegment(sketch, "E5420", {"start": v(-150.06, -194.63) * mm, "end": v(-150.02, -193.2) * mm});
            skLineSegment(sketch, "E5421", {"start": v(-150.02, -193.2) * mm, "end": v(-149.96, -191.77) * mm});
            skLineSegment(sketch, "E5422", {"start": v(-149.96, -191.77) * mm, "end": v(-149.9, -190.36) * mm});
            skLineSegment(sketch, "E5423", {"start": v(-149.9, -190.36) * mm, "end": v(-149.81, -188.96) * mm});
            skLineSegment(sketch, "E5424", {"start": v(-149.81, -188.96) * mm, "end": v(-149.72, -187.58) * mm});
            skLineSegment(sketch, "E5425", {"start": v(-149.72, -187.58) * mm, "end": v(-149.61, -186.2) * mm});
            skLineSegment(sketch, "E5426", {"start": v(-149.61, -186.2) * mm, "end": v(-149.5, -184.85) * mm});
            skLineSegment(sketch, "E5427", {"start": v(-149.5, -184.85) * mm, "end": v(-149.36, -183.51) * mm});
            skLineSegment(sketch, "E5428", {"start": v(-149.36, -183.51) * mm, "end": v(-149.22, -182.18) * mm});
            skLineSegment(sketch, "E5429", {"start": v(-149.22, -182.18) * mm, "end": v(-149.06, -180.87) * mm});
            skLineSegment(sketch, "E5430", {"start": v(-149.06, -180.87) * mm, "end": v(-148.9, -179.56) * mm});
            skLineSegment(sketch, "E5431", {"start": v(-148.9, -179.56) * mm, "end": v(-148.71, -178.28) * mm});
            skLineSegment(sketch, "E5432", {"start": v(-148.71, -178.28) * mm, "end": v(-148.52, -177) * mm});
            skLineSegment(sketch, "E5433", {"start": v(-148.52, -177) * mm, "end": v(-148.31, -175.74) * mm});
            skLineSegment(sketch, "E5434", {"start": v(-148.31, -175.74) * mm, "end": v(-148.1, -174.5) * mm});
            skLineSegment(sketch, "E5435", {"start": v(-148.1, -174.5) * mm, "end": v(-147.87, -173.29) * mm});
            skLineSegment(sketch, "E5436", {"start": v(-147.87, -173.29) * mm, "end": v(-147.62, -172.1) * mm});
            skLineSegment(sketch, "E5437", {"start": v(-147.62, -172.1) * mm, "end": v(-147.37, -170.91) * mm});
            skLineSegment(sketch, "E5438", {"start": v(-147.37, -170.91) * mm, "end": v(-147.1, -169.76) * mm});
            skLineSegment(sketch, "E5439", {"start": v(-147.1, -169.76) * mm, "end": v(-146.83, -168.62) * mm});
            skLineSegment(sketch, "E5440", {"start": v(-146.83, -168.62) * mm, "end": v(-146.55, -167.5) * mm});
            skLineSegment(sketch, "E5441", {"start": v(-146.55, -167.5) * mm, "end": v(-146.25, -166.4) * mm});
            skLineSegment(sketch, "E5442", {"start": v(-146.25, -166.4) * mm, "end": v(-145.94, -165.33) * mm});
            skLineSegment(sketch, "E5443", {"start": v(-145.94, -165.33) * mm, "end": v(-145.62, -164.28) * mm});
            skLineSegment(sketch, "E5444", {"start": v(-145.62, -164.28) * mm, "end": v(-145.28, -163.24) * mm});
            skLineSegment(sketch, "E5445", {"start": v(-145.28, -163.24) * mm, "end": v(-144.94, -162.23) * mm});
            skLineSegment(sketch, "E5446", {"start": v(-144.94, -162.23) * mm, "end": v(-144.58, -161.24) * mm});
            skLineSegment(sketch, "E5447", {"start": v(-144.58, -161.24) * mm, "end": v(-144.21, -160.26) * mm});
            skLineSegment(sketch, "E5448", {"start": v(-144.21, -160.26) * mm, "end": v(-143.83, -159.3) * mm});
            skLineSegment(sketch, "E5449", {"start": v(-143.83, -159.3) * mm, "end": v(-143.48, -158.46) * mm});
            skLineSegment(sketch, "E5450", {"start": v(-143.48, -158.46) * mm, "end": v(-143.13, -157.63) * mm});
            skLineSegment(sketch, "E5451", {"start": v(-143.13, -157.63) * mm, "end": v(-142.77, -156.83) * mm});
            skLineSegment(sketch, "E5452", {"start": v(-142.77, -156.83) * mm, "end": v(-142.4, -156.05) * mm});
            skLineSegment(sketch, "E5453", {"start": v(-142.4, -156.05) * mm, "end": v(-142.04, -155.3) * mm});
            skLineSegment(sketch, "E5454", {"start": v(-142.04, -155.3) * mm, "end": v(-141.67, -154.58) * mm});
            skLineSegment(sketch, "E5455", {"start": v(-141.67, -154.58) * mm, "end": v(-141.3, -153.88) * mm});
            skLineSegment(sketch, "E5456", {"start": v(-141.3, -153.88) * mm, "end": v(-140.92, -153.2) * mm});
            skLineSegment(sketch, "E5457", {"start": v(-140.92, -153.2) * mm, "end": v(-140.54, -152.55) * mm});
            skLineSegment(sketch, "E5458", {"start": v(-140.54, -152.55) * mm, "end": v(-140.15, -151.93) * mm});
            skLineSegment(sketch, "E5459", {"start": v(-140.15, -151.93) * mm, "end": v(-139.76, -151.33) * mm});
            skLineSegment(sketch, "E5460", {"start": v(-139.76, -151.33) * mm, "end": v(-139.37, -150.76) * mm});
            skLineSegment(sketch, "E5461", {"start": v(-139.37, -150.76) * mm, "end": v(-138.98, -150.22) * mm});
            skLineSegment(sketch, "E5462", {"start": v(-138.98, -150.22) * mm, "end": v(-138.58, -149.7) * mm});
            skLineSegment(sketch, "E5463", {"start": v(-138.58, -149.7) * mm, "end": v(-138.18, -149.2) * mm});
            skLineSegment(sketch, "E5464", {"start": v(-138.18, -149.2) * mm, "end": v(-137.77, -148.73) * mm});
            skLineSegment(sketch, "E5465", {"start": v(-137.77, -148.73) * mm, "end": v(-137.36, -148.28) * mm});
            skLineSegment(sketch, "E5466", {"start": v(-137.36, -148.28) * mm, "end": v(-136.94, -147.86) * mm});
            skLineSegment(sketch, "E5467", {"start": v(-136.94, -147.86) * mm, "end": v(-136.51, -147.45) * mm});
            skLineSegment(sketch, "E5468", {"start": v(-136.51, -147.45) * mm, "end": v(-136.08, -147.07) * mm});
            skLineSegment(sketch, "E5469", {"start": v(-136.08, -147.07) * mm, "end": v(-135.64, -146.7) * mm});
            skLineSegment(sketch, "E5470", {"start": v(-135.64, -146.7) * mm, "end": v(-135.2, -146.36) * mm});
            skLineSegment(sketch, "E5471", {"start": v(-135.2, -146.36) * mm, "end": v(-134.74, -146.04) * mm});
            skLineSegment(sketch, "E5472", {"start": v(-134.74, -146.04) * mm, "end": v(-134.27, -145.73) * mm});
            skLineSegment(sketch, "E5473", {"start": v(-134.27, -145.73) * mm, "end": v(-133.8, -145.45) * mm});
            skLineSegment(sketch, "E5474", {"start": v(-133.8, -145.45) * mm, "end": v(-133.33, -145.19) * mm});
            skLineSegment(sketch, "E5475", {"start": v(-133.33, -145.19) * mm, "end": v(-132.84, -144.95) * mm});
            skLineSegment(sketch, "E5476", {"start": v(-132.84, -144.95) * mm, "end": v(-132.35, -144.73) * mm});
            skLineSegment(sketch, "E5477", {"start": v(-132.35, -144.73) * mm, "end": v(-131.85, -144.53) * mm});
            skLineSegment(sketch, "E5478", {"start": v(-131.85, -144.53) * mm, "end": v(-131.34, -144.35) * mm});
            skLineSegment(sketch, "E5479", {"start": v(-131.34, -144.35) * mm, "end": v(-130.83, -144.19) * mm});
            skLineSegment(sketch, "E5480", {"start": v(-130.83, -144.19) * mm, "end": v(-130.3, -144.05) * mm});
            skLineSegment(sketch, "E5481", {"start": v(-130.3, -144.05) * mm, "end": v(-130.3, -152.23) * mm});
            skLineSegment(sketch, "E5482", {"start": v(-130.3, -152.23) * mm, "end": v(-130.82, -152.57) * mm});
            skLineSegment(sketch, "E5483", {"start": v(-130.82, -152.57) * mm, "end": v(-131.26, -152.89) * mm});
            skLineSegment(sketch, "E5484", {"start": v(-131.26, -152.89) * mm, "end": v(-131.44, -153.04) * mm});
            skLineSegment(sketch, "E5485", {"start": v(-131.44, -153.04) * mm, "end": v(-131.6, -153.18) * mm});
            skLineSegment(sketch, "E5486", {"start": v(-131.6, -153.18) * mm, "end": v(-131.75, -153.32) * mm});
            skLineSegment(sketch, "E5487", {"start": v(-131.75, -153.32) * mm, "end": v(-131.87, -153.45) * mm});
            skLineSegment(sketch, "E5488", {"start": v(-131.87, -153.45) * mm, "end": v(-131.98, -153.58) * mm});
            skLineSegment(sketch, "E5489", {"start": v(-131.98, -153.58) * mm, "end": v(-132.09, -153.74) * mm});
            skLineSegment(sketch, "E5490", {"start": v(-132.09, -153.74) * mm, "end": v(-132.2, -153.9) * mm});
            skLineSegment(sketch, "E5491", {"start": v(-132.2, -153.9) * mm, "end": v(-132.3, -154.09) * mm});
            skLineSegment(sketch, "E5492", {"start": v(-132.3, -154.09) * mm, "end": v(-132.4, -154.29) * mm});
            skLineSegment(sketch, "E5493", {"start": v(-132.4, -154.29) * mm, "end": v(-132.5, -154.5) * mm});
            skLineSegment(sketch, "E5494", {"start": v(-132.5, -154.5) * mm, "end": v(-132.7, -154.98) * mm});
            skLineSegment(sketch, "E5495", {"start": v(-132.7, -154.98) * mm, "end": v(-132.85, -155.36) * mm});
            skLineSegment(sketch, "E5496", {"start": v(-132.85, -155.36) * mm, "end": v(-132.98, -155.75) * mm});
            skLineSegment(sketch, "E5497", {"start": v(-132.98, -155.75) * mm, "end": v(-133.1, -156.16) * mm});
            skLineSegment(sketch, "E5498", {"start": v(-133.1, -156.16) * mm, "end": v(-133.22, -156.6) * mm});
            skLineSegment(sketch, "E5499", {"start": v(-133.22, -156.6) * mm, "end": v(-133.32, -157.05) * mm});
            skLineSegment(sketch, "E5500", {"start": v(-133.32, -157.05) * mm, "end": v(-133.42, -157.53) * mm});
            skLineSegment(sketch, "E5501", {"start": v(-133.42, -157.53) * mm, "end": v(-133.5, -158.02) * mm});
            skLineSegment(sketch, "E5502", {"start": v(-133.5, -158.02) * mm, "end": v(-133.58, -158.54) * mm});
            skLineSegment(sketch, "E5503", {"start": v(-133.58, -158.54) * mm, "end": v(-133.65, -159.08) * mm});
            skLineSegment(sketch, "E5504", {"start": v(-133.65, -159.08) * mm, "end": v(-133.7, -159.63) * mm});
            skLineSegment(sketch, "E5505", {"start": v(-133.7, -159.63) * mm, "end": v(-133.76, -160.2) * mm});
            skLineSegment(sketch, "E5506", {"start": v(-133.76, -160.2) * mm, "end": v(-133.8, -160.8) * mm});
            skLineSegment(sketch, "E5507", {"start": v(-133.8, -160.8) * mm, "end": v(-133.83, -161.42) * mm});
            skLineSegment(sketch, "E5508", {"start": v(-133.83, -161.42) * mm, "end": v(-133.85, -162.06) * mm});
            skLineSegment(sketch, "E5509", {"start": v(-133.85, -162.06) * mm, "end": v(-133.86, -162.72) * mm});
            skLineSegment(sketch, "E5510", {"start": v(-133.86, -162.72) * mm, "end": v(-133.87, -163.4) * mm});
            skLineSegment(sketch, "E5511", {"start": v(-133.87, -163.4) * mm, "end": v(-133.87, -234.72) * mm});
            skLineSegment(sketch, "E5512", {"start": v(-133.87, -234.72) * mm, "end": v(-133.86, -235.4) * mm});
            skLineSegment(sketch, "E5513", {"start": v(-133.86, -235.4) * mm, "end": v(-133.85, -236.06) * mm});
            skLineSegment(sketch, "E5514", {"start": v(-133.85, -236.06) * mm, "end": v(-133.83, -236.7) * mm});
            skLineSegment(sketch, "E5515", {"start": v(-133.83, -236.7) * mm, "end": v(-133.8, -237.31) * mm});
            skLineSegment(sketch, "E5516", {"start": v(-133.8, -237.31) * mm, "end": v(-133.76, -237.9) * mm});
            skLineSegment(sketch, "E5517", {"start": v(-133.76, -237.9) * mm, "end": v(-133.7, -238.49) * mm});
            skLineSegment(sketch, "E5518", {"start": v(-133.7, -238.49) * mm, "end": v(-133.65, -239.04) * mm});
            skLineSegment(sketch, "E5519", {"start": v(-133.65, -239.04) * mm, "end": v(-133.58, -239.58) * mm});
            skLineSegment(sketch, "E5520", {"start": v(-133.58, -239.58) * mm, "end": v(-133.5, -240.1) * mm});
            skLineSegment(sketch, "E5521", {"start": v(-133.5, -240.1) * mm, "end": v(-133.42, -240.59) * mm});
            skLineSegment(sketch, "E5522", {"start": v(-133.42, -240.59) * mm, "end": v(-133.32, -241.06) * mm});
            skLineSegment(sketch, "E5523", {"start": v(-133.32, -241.06) * mm, "end": v(-133.22, -241.52) * mm});
            skLineSegment(sketch, "E5524", {"start": v(-133.22, -241.52) * mm, "end": v(-133.1, -241.95) * mm});
            skLineSegment(sketch, "E5525", {"start": v(-133.1, -241.95) * mm, "end": v(-132.98, -242.37) * mm});
            skLineSegment(sketch, "E5526", {"start": v(-132.98, -242.37) * mm, "end": v(-132.85, -242.76) * mm});
            skLineSegment(sketch, "E5527", {"start": v(-132.85, -242.76) * mm, "end": v(-132.7, -243.14) * mm});
            skLineSegment(sketch, "E5528", {"start": v(-132.7, -243.14) * mm, "end": v(-132.5, -243.62) * mm});
            skLineSegment(sketch, "E5529", {"start": v(-132.5, -243.62) * mm, "end": v(-132.4, -243.83) * mm});
            skLineSegment(sketch, "E5530", {"start": v(-132.4, -243.83) * mm, "end": v(-132.3, -244.03) * mm});
            skLineSegment(sketch, "E5531", {"start": v(-132.3, -244.03) * mm, "end": v(-132.2, -244.21) * mm});
            skLineSegment(sketch, "E5532", {"start": v(-132.2, -244.21) * mm, "end": v(-132.09, -244.38) * mm});
            skLineSegment(sketch, "E5533", {"start": v(-132.09, -244.38) * mm, "end": v(-131.98, -244.53) * mm});
            skLineSegment(sketch, "E5534", {"start": v(-131.98, -244.53) * mm, "end": v(-131.87, -244.67) * mm});
            skLineSegment(sketch, "E5535", {"start": v(-131.87, -244.67) * mm, "end": v(-131.75, -244.8) * mm});
            skLineSegment(sketch, "E5536", {"start": v(-131.75, -244.8) * mm, "end": v(-131.6, -244.94) * mm});
            skLineSegment(sketch, "E5537", {"start": v(-131.6, -244.94) * mm, "end": v(-131.44, -245.08) * mm});
            skLineSegment(sketch, "E5538", {"start": v(-131.44, -245.08) * mm, "end": v(-131.26, -245.23) * mm});
            skLineSegment(sketch, "E5539", {"start": v(-131.26, -245.23) * mm, "end": v(-130.82, -245.55) * mm});
            skLineSegment(sketch, "E5540", {"start": v(-130.82, -245.55) * mm, "end": v(-130.3, -245.89) * mm});
            skLineSegment(sketch, "E5541", {"start": v(-130.3, -245.89) * mm, "end": v(-130.3, -254.07) * mm});
            skLineSegment(sketch, "E5542", {"start": v(-127.22, -254.07) * mm, "end": v(-127.22, -245.89) * mm});
            skLineSegment(sketch, "E5543", {"start": v(-127.22, -245.89) * mm, "end": v(-126.7, -245.55) * mm});
            skLineSegment(sketch, "E5544", {"start": v(-126.7, -245.55) * mm, "end": v(-126.27, -245.23) * mm});
            skLineSegment(sketch, "E5545", {"start": v(-126.27, -245.23) * mm, "end": v(-126.09, -245.08) * mm});
            skLineSegment(sketch, "E5546", {"start": v(-126.09, -245.08) * mm, "end": v(-125.93, -244.94) * mm});
            skLineSegment(sketch, "E5547", {"start": v(-125.93, -244.94) * mm, "end": v(-125.78, -244.8) * mm});
            skLineSegment(sketch, "E5548", {"start": v(-125.78, -244.8) * mm, "end": v(-125.66, -244.67) * mm});
            skLineSegment(sketch, "E5549", {"start": v(-125.66, -244.67) * mm, "end": v(-125.55, -244.53) * mm});
            skLineSegment(sketch, "E5550", {"start": v(-125.55, -244.53) * mm, "end": v(-125.45, -244.38) * mm});
            skLineSegment(sketch, "E5551", {"start": v(-125.45, -244.38) * mm, "end": v(-125.34, -244.21) * mm});
            skLineSegment(sketch, "E5552", {"start": v(-125.34, -244.21) * mm, "end": v(-125.23, -244.03) * mm});
            skLineSegment(sketch, "E5553", {"start": v(-125.23, -244.03) * mm, "end": v(-125.13, -243.83) * mm});
            skLineSegment(sketch, "E5554", {"start": v(-125.13, -243.83) * mm, "end": v(-125.03, -243.62) * mm});
            skLineSegment(sketch, "E5555", {"start": v(-125.03, -243.62) * mm, "end": v(-124.82, -243.14) * mm});
            skLineSegment(sketch, "E5556", {"start": v(-124.82, -243.14) * mm, "end": v(-124.68, -242.76) * mm});
            skLineSegment(sketch, "E5557", {"start": v(-124.68, -242.76) * mm, "end": v(-124.55, -242.37) * mm});
            skLineSegment(sketch, "E5558", {"start": v(-124.55, -242.37) * mm, "end": v(-124.43, -241.95) * mm});
            skLineSegment(sketch, "E5559", {"start": v(-124.43, -241.95) * mm, "end": v(-124.32, -241.52) * mm});
            skLineSegment(sketch, "E5560", {"start": v(-124.32, -241.52) * mm, "end": v(-124.21, -241.06) * mm});
            skLineSegment(sketch, "E5561", {"start": v(-124.21, -241.06) * mm, "end": v(-124.12, -240.59) * mm});
            skLineSegment(sketch, "E5562", {"start": v(-124.12, -240.59) * mm, "end": v(-124.03, -240.1) * mm});
            skLineSegment(sketch, "E5563", {"start": v(-124.03, -240.1) * mm, "end": v(-123.95, -239.58) * mm});
            skLineSegment(sketch, "E5564", {"start": v(-123.95, -239.58) * mm, "end": v(-123.88, -239.04) * mm});
            skLineSegment(sketch, "E5565", {"start": v(-123.88, -239.04) * mm, "end": v(-123.83, -238.49) * mm});
            skLineSegment(sketch, "E5566", {"start": v(-123.83, -238.49) * mm, "end": v(-123.78, -237.9) * mm});
            skLineSegment(sketch, "E5567", {"start": v(-123.78, -237.9) * mm, "end": v(-123.74, -237.31) * mm});
            skLineSegment(sketch, "E5568", {"start": v(-123.74, -237.31) * mm, "end": v(-123.7, -236.7) * mm});
            skLineSegment(sketch, "E5569", {"start": v(-123.7, -236.7) * mm, "end": v(-123.68, -236.06) * mm});
            skLineSegment(sketch, "E5570", {"start": v(-123.68, -236.06) * mm, "end": v(-123.67, -235.4) * mm});
            skLineSegment(sketch, "E5571", {"start": v(-123.67, -235.4) * mm, "end": v(-123.66, -234.72) * mm});
            skLineSegment(sketch, "E5572", {"start": v(-123.66, -234.72) * mm, "end": v(-123.66, -163.4) * mm});
            skLineSegment(sketch, "E5573", {"start": v(-123.66, -163.4) * mm, "end": v(-123.67, -162.72) * mm});
            skLineSegment(sketch, "E5574", {"start": v(-123.67, -162.72) * mm, "end": v(-123.68, -162.06) * mm});
            skLineSegment(sketch, "E5575", {"start": v(-123.68, -162.06) * mm, "end": v(-123.7, -161.42) * mm});
            skLineSegment(sketch, "E5576", {"start": v(-123.7, -161.42) * mm, "end": v(-123.74, -160.8) * mm});
            skLineSegment(sketch, "E5577", {"start": v(-123.74, -160.8) * mm, "end": v(-123.78, -160.2) * mm});
            skLineSegment(sketch, "E5578", {"start": v(-123.78, -160.2) * mm, "end": v(-123.83, -159.63) * mm});
            skLineSegment(sketch, "E5579", {"start": v(-123.83, -159.63) * mm, "end": v(-123.88, -159.08) * mm});
            skLineSegment(sketch, "E5580", {"start": v(-123.88, -159.08) * mm, "end": v(-123.95, -158.54) * mm});
            skLineSegment(sketch, "E5581", {"start": v(-123.95, -158.54) * mm, "end": v(-124.03, -158.02) * mm});
            skLineSegment(sketch, "E5582", {"start": v(-124.03, -158.02) * mm, "end": v(-124.12, -157.53) * mm});
            skLineSegment(sketch, "E5583", {"start": v(-124.12, -157.53) * mm, "end": v(-124.21, -157.05) * mm});
            skLineSegment(sketch, "E5584", {"start": v(-124.21, -157.05) * mm, "end": v(-124.32, -156.6) * mm});
            skLineSegment(sketch, "E5585", {"start": v(-124.32, -156.6) * mm, "end": v(-124.43, -156.16) * mm});
            skLineSegment(sketch, "E5586", {"start": v(-124.43, -156.16) * mm, "end": v(-124.55, -155.75) * mm});
            skLineSegment(sketch, "E5587", {"start": v(-124.55, -155.75) * mm, "end": v(-124.68, -155.36) * mm});
            skLineSegment(sketch, "E5588", {"start": v(-124.68, -155.36) * mm, "end": v(-124.82, -154.98) * mm});
            skLineSegment(sketch, "E5589", {"start": v(-124.82, -154.98) * mm, "end": v(-125.03, -154.5) * mm});
            skLineSegment(sketch, "E5590", {"start": v(-125.03, -154.5) * mm, "end": v(-125.13, -154.29) * mm});
            skLineSegment(sketch, "E5591", {"start": v(-125.13, -154.29) * mm, "end": v(-125.23, -154.09) * mm});
            skLineSegment(sketch, "E5592", {"start": v(-125.23, -154.09) * mm, "end": v(-125.34, -153.9) * mm});
            skLineSegment(sketch, "E5593", {"start": v(-125.34, -153.9) * mm, "end": v(-125.45, -153.74) * mm});
            skLineSegment(sketch, "E5594", {"start": v(-125.45, -153.74) * mm, "end": v(-125.55, -153.58) * mm});
            skLineSegment(sketch, "E5595", {"start": v(-125.55, -153.58) * mm, "end": v(-125.66, -153.45) * mm});
            skLineSegment(sketch, "E5596", {"start": v(-125.66, -153.45) * mm, "end": v(-125.78, -153.32) * mm});
            skLineSegment(sketch, "E5597", {"start": v(-125.78, -153.32) * mm, "end": v(-125.93, -153.18) * mm});
            skLineSegment(sketch, "E5598", {"start": v(-125.93, -153.18) * mm, "end": v(-126.09, -153.04) * mm});
            skLineSegment(sketch, "E5599", {"start": v(-126.09, -153.04) * mm, "end": v(-126.27, -152.89) * mm});
            skLineSegment(sketch, "E5600", {"start": v(-126.27, -152.89) * mm, "end": v(-126.7, -152.57) * mm});
            skLineSegment(sketch, "E5601", {"start": v(-126.7, -152.57) * mm, "end": v(-127.22, -152.23) * mm});
            skLineSegment(sketch, "E5602", {"start": v(-127.22, -152.23) * mm, "end": v(-127.22, -144.05) * mm});
            skLineSegment(sketch, "E5603", {"start": v(-127.22, -144.05) * mm, "end": v(-126.7, -144.19) * mm});
            skLineSegment(sketch, "E5604", {"start": v(-126.7, -144.19) * mm, "end": v(-126.19, -144.35) * mm});
            skLineSegment(sketch, "E5605", {"start": v(-126.19, -144.35) * mm, "end": v(-125.68, -144.53) * mm});
            skLineSegment(sketch, "E5606", {"start": v(-125.68, -144.53) * mm, "end": v(-125.18, -144.73) * mm});
            skLineSegment(sketch, "E5607", {"start": v(-125.18, -144.73) * mm, "end": v(-124.7, -144.95) * mm});
            skLineSegment(sketch, "E5608", {"start": v(-124.7, -144.95) * mm, "end": v(-124.2, -145.19) * mm});
            skLineSegment(sketch, "E5609", {"start": v(-124.2, -145.19) * mm, "end": v(-123.73, -145.45) * mm});
            skLineSegment(sketch, "E5610", {"start": v(-123.73, -145.45) * mm, "end": v(-123.26, -145.73) * mm});
            skLineSegment(sketch, "E5611", {"start": v(-123.26, -145.73) * mm, "end": v(-122.8, -146.04) * mm});
            skLineSegment(sketch, "E5612", {"start": v(-122.8, -146.04) * mm, "end": v(-122.34, -146.36) * mm});
            skLineSegment(sketch, "E5613", {"start": v(-122.34, -146.36) * mm, "end": v(-121.9, -146.7) * mm});
            skLineSegment(sketch, "E5614", {"start": v(-121.9, -146.7) * mm, "end": v(-121.45, -147.07) * mm});
            skLineSegment(sketch, "E5615", {"start": v(-121.45, -147.07) * mm, "end": v(-121.02, -147.45) * mm});
            skLineSegment(sketch, "E5616", {"start": v(-121.02, -147.45) * mm, "end": v(-120.6, -147.86) * mm});
            skLineSegment(sketch, "E5617", {"start": v(-120.6, -147.86) * mm, "end": v(-120.17, -148.28) * mm});
            skLineSegment(sketch, "E5618", {"start": v(-120.17, -148.28) * mm, "end": v(-119.76, -148.73) * mm});
            skLineSegment(sketch, "E5619", {"start": v(-119.76, -148.73) * mm, "end": v(-119.35, -149.2) * mm});
            skLineSegment(sketch, "E5620", {"start": v(-119.35, -149.2) * mm, "end": v(-118.95, -149.7) * mm});
            skLineSegment(sketch, "E5621", {"start": v(-118.95, -149.7) * mm, "end": v(-118.55, -150.22) * mm});
            skLineSegment(sketch, "E5622", {"start": v(-118.55, -150.22) * mm, "end": v(-118.16, -150.76) * mm});
            skLineSegment(sketch, "E5623", {"start": v(-118.16, -150.76) * mm, "end": v(-117.77, -151.33) * mm});
            skLineSegment(sketch, "E5624", {"start": v(-117.77, -151.33) * mm, "end": v(-117.38, -151.93) * mm});
            skLineSegment(sketch, "E5625", {"start": v(-117.38, -151.93) * mm, "end": v(-117, -152.55) * mm});
            skLineSegment(sketch, "E5626", {"start": v(-117, -152.55) * mm, "end": v(-116.61, -153.2) * mm});
            skLineSegment(sketch, "E5627", {"start": v(-116.61, -153.2) * mm, "end": v(-116.24, -153.88) * mm});
            skLineSegment(sketch, "E5628", {"start": v(-116.24, -153.88) * mm, "end": v(-115.86, -154.58) * mm});
            skLineSegment(sketch, "E5629", {"start": v(-115.86, -154.58) * mm, "end": v(-115.5, -155.3) * mm});
            skLineSegment(sketch, "E5630", {"start": v(-115.5, -155.3) * mm, "end": v(-115.13, -156.05) * mm});
            skLineSegment(sketch, "E5631", {"start": v(-115.13, -156.05) * mm, "end": v(-114.76, -156.83) * mm});
            skLineSegment(sketch, "E5632", {"start": v(-114.76, -156.83) * mm, "end": v(-114.4, -157.63) * mm});
            skLineSegment(sketch, "E5633", {"start": v(-114.4, -157.63) * mm, "end": v(-114.05, -158.46) * mm});
            skLineSegment(sketch, "E5634", {"start": v(-114.05, -158.46) * mm, "end": v(-113.7, -159.3) * mm});
            skLineSegment(sketch, "E5635", {"start": v(-113.7, -159.3) * mm, "end": v(-113.32, -160.26) * mm});
            skLineSegment(sketch, "E5636", {"start": v(-113.32, -160.26) * mm, "end": v(-112.95, -161.24) * mm});
            skLineSegment(sketch, "E5637", {"start": v(-112.95, -161.24) * mm, "end": v(-112.6, -162.23) * mm});
            skLineSegment(sketch, "E5638", {"start": v(-112.6, -162.23) * mm, "end": v(-112.25, -163.24) * mm});
            skLineSegment(sketch, "E5639", {"start": v(-112.25, -163.24) * mm, "end": v(-111.92, -164.28) * mm});
            skLineSegment(sketch, "E5640", {"start": v(-111.92, -164.28) * mm, "end": v(-111.6, -165.33) * mm});
            skLineSegment(sketch, "E5641", {"start": v(-111.6, -165.33) * mm, "end": v(-111.28, -166.4) * mm});
            skLineSegment(sketch, "E5642", {"start": v(-111.28, -166.4) * mm, "end": v(-110.99, -167.5) * mm});
            skLineSegment(sketch, "E5643", {"start": v(-110.99, -167.5) * mm, "end": v(-110.7, -168.62) * mm});
            skLineSegment(sketch, "E5644", {"start": v(-110.7, -168.62) * mm, "end": v(-110.42, -169.76) * mm});
            skLineSegment(sketch, "E5645", {"start": v(-110.42, -169.76) * mm, "end": v(-110.16, -170.91) * mm});
            skLineSegment(sketch, "E5646", {"start": v(-110.16, -170.91) * mm, "end": v(-109.9, -172.1) * mm});
            skLineSegment(sketch, "E5647", {"start": v(-109.9, -172.1) * mm, "end": v(-109.67, -173.29) * mm});
            skLineSegment(sketch, "E5648", {"start": v(-109.67, -173.29) * mm, "end": v(-109.44, -174.5) * mm});
            skLineSegment(sketch, "E5649", {"start": v(-109.44, -174.5) * mm, "end": v(-109.22, -175.74) * mm});
            skLineSegment(sketch, "E5650", {"start": v(-109.22, -175.74) * mm, "end": v(-109.01, -177) * mm});
            skLineSegment(sketch, "E5651", {"start": v(-109.01, -177) * mm, "end": v(-108.82, -178.28) * mm});
            skLineSegment(sketch, "E5652", {"start": v(-108.82, -178.28) * mm, "end": v(-108.64, -179.56) * mm});
            skLineSegment(sketch, "E5653", {"start": v(-108.64, -179.56) * mm, "end": v(-108.47, -180.87) * mm});
            skLineSegment(sketch, "E5654", {"start": v(-108.47, -180.87) * mm, "end": v(-108.31, -182.18) * mm});
            skLineSegment(sketch, "E5655", {"start": v(-108.31, -182.18) * mm, "end": v(-108.17, -183.51) * mm});
            skLineSegment(sketch, "E5656", {"start": v(-108.17, -183.51) * mm, "end": v(-108.04, -184.85) * mm});
            skLineSegment(sketch, "E5657", {"start": v(-108.04, -184.85) * mm, "end": v(-107.92, -186.2) * mm});
            skLineSegment(sketch, "E5658", {"start": v(-107.92, -186.2) * mm, "end": v(-107.81, -187.58) * mm});
            skLineSegment(sketch, "E5659", {"start": v(-107.81, -187.58) * mm, "end": v(-107.72, -188.96) * mm});
            skLineSegment(sketch, "E5660", {"start": v(-107.72, -188.96) * mm, "end": v(-107.64, -190.36) * mm});
            skLineSegment(sketch, "E5661", {"start": v(-107.64, -190.36) * mm, "end": v(-107.57, -191.77) * mm});
            skLineSegment(sketch, "E5662", {"start": v(-107.57, -191.77) * mm, "end": v(-107.51, -193.2) * mm});
            skLineSegment(sketch, "E5663", {"start": v(-107.51, -193.2) * mm, "end": v(-107.47, -194.63) * mm});
            skLineSegment(sketch, "E5664", {"start": v(-107.47, -194.63) * mm, "end": v(-107.44, -196.08) * mm});
            skLineSegment(sketch, "E5665", {"start": v(-107.44, -196.08) * mm, "end": v(-107.42, -197.54) * mm});
            skLineSegment(sketch, "E5666", {"start": v(-107.42, -197.54) * mm, "end": v(-107.41, -199.02) * mm});
            skLineSegment(sketch, "E5667", {"start": v(-107.41, -199.02) * mm, "end": v(-107.42, -200.5) * mm});
            skLineSegment(sketch, "E5668", {"start": v(-107.42, -200.5) * mm, "end": v(-107.44, -201.98) * mm});
            skLineSegment(sketch, "E5669", {"start": v(-107.44, -201.98) * mm, "end": v(-107.47, -203.44) * mm});
            skLineSegment(sketch, "E5670", {"start": v(-107.47, -203.44) * mm, "end": v(-107.51, -204.88) * mm});
            skLineSegment(sketch, "E5671", {"start": v(-107.51, -204.88) * mm, "end": v(-107.57, -206.31) * mm});
            skLineSegment(sketch, "E5672", {"start": v(-107.57, -206.31) * mm, "end": v(-107.64, -207.73) * mm});
            skLineSegment(sketch, "E5673", {"start": v(-107.64, -207.73) * mm, "end": v(-107.72, -209.13) * mm});
            skLineSegment(sketch, "E5674", {"start": v(-107.72, -209.13) * mm, "end": v(-107.81, -210.52) * mm});
            skLineSegment(sketch, "E5675", {"start": v(-107.81, -210.52) * mm, "end": v(-107.92, -211.9) * mm});
            skLineSegment(sketch, "E5676", {"start": v(-107.92, -211.9) * mm, "end": v(-108.04, -213.25) * mm});
            skLineSegment(sketch, "E5677", {"start": v(-108.04, -213.25) * mm, "end": v(-108.17, -214.6) * mm});
            skLineSegment(sketch, "E5678", {"start": v(-108.17, -214.6) * mm, "end": v(-108.31, -215.93) * mm});
            skLineSegment(sketch, "E5679", {"start": v(-108.31, -215.93) * mm, "end": v(-108.47, -217.25) * mm});
            skLineSegment(sketch, "E5680", {"start": v(-108.47, -217.25) * mm, "end": v(-108.64, -218.55) * mm});
            skLineSegment(sketch, "E5681", {"start": v(-108.64, -218.55) * mm, "end": v(-108.82, -219.84) * mm});
            skLineSegment(sketch, "E5682", {"start": v(-108.82, -219.84) * mm, "end": v(-109.01, -221.12) * mm});
            skLineSegment(sketch, "E5683", {"start": v(-109.01, -221.12) * mm, "end": v(-109.22, -222.38) * mm});
            skLineSegment(sketch, "E5684", {"start": v(-109.22, -222.38) * mm, "end": v(-109.44, -223.61) * mm});
            skLineSegment(sketch, "E5685", {"start": v(-109.44, -223.61) * mm, "end": v(-109.67, -224.83) * mm});
            skLineSegment(sketch, "E5686", {"start": v(-109.67, -224.83) * mm, "end": v(-109.9, -226.03) * mm});
            skLineSegment(sketch, "E5687", {"start": v(-109.9, -226.03) * mm, "end": v(-110.16, -227.2) * mm});
            skLineSegment(sketch, "E5688", {"start": v(-110.16, -227.2) * mm, "end": v(-110.42, -228.36) * mm});
            skLineSegment(sketch, "E5689", {"start": v(-110.42, -228.36) * mm, "end": v(-110.7, -229.5) * mm});
            skLineSegment(sketch, "E5690", {"start": v(-110.7, -229.5) * mm, "end": v(-110.99, -230.61) * mm});
            skLineSegment(sketch, "E5691", {"start": v(-110.99, -230.61) * mm, "end": v(-111.28, -231.7) * mm});
            skLineSegment(sketch, "E5692", {"start": v(-111.28, -231.7) * mm, "end": v(-111.6, -232.78) * mm});
            skLineSegment(sketch, "E5693", {"start": v(-111.6, -232.78) * mm, "end": v(-111.92, -233.84) * mm});
            skLineSegment(sketch, "E5694", {"start": v(-111.92, -233.84) * mm, "end": v(-112.25, -234.87) * mm});
            skLineSegment(sketch, "E5695", {"start": v(-112.25, -234.87) * mm, "end": v(-112.6, -235.89) * mm});
            skLineSegment(sketch, "E5696", {"start": v(-112.6, -235.89) * mm, "end": v(-112.95, -236.88) * mm});
            skLineSegment(sketch, "E5697", {"start": v(-112.95, -236.88) * mm, "end": v(-113.32, -237.86) * mm});
            skLineSegment(sketch, "E5698", {"start": v(-113.32, -237.86) * mm, "end": v(-113.7, -238.81) * mm});
            skLineSegment(sketch, "E5699", {"start": v(-113.7, -238.81) * mm, "end": v(-114.05, -239.66) * mm});
            skLineSegment(sketch, "E5700", {"start": v(-114.05, -239.66) * mm, "end": v(-114.4, -240.5) * mm});
            skLineSegment(sketch, "E5701", {"start": v(-114.4, -240.5) * mm, "end": v(-114.76, -241.3) * mm});
            skLineSegment(sketch, "E5702", {"start": v(-114.76, -241.3) * mm, "end": v(-115.13, -242.07) * mm});
            skLineSegment(sketch, "E5703", {"start": v(-115.13, -242.07) * mm, "end": v(-115.5, -242.82) * mm});
            skLineSegment(sketch, "E5704", {"start": v(-115.5, -242.82) * mm, "end": v(-115.86, -243.54) * mm});
            skLineSegment(sketch, "E5705", {"start": v(-115.86, -243.54) * mm, "end": v(-116.24, -244.24) * mm});
            skLineSegment(sketch, "E5706", {"start": v(-116.24, -244.24) * mm, "end": v(-116.61, -244.92) * mm});
            skLineSegment(sketch, "E5707", {"start": v(-116.61, -244.92) * mm, "end": v(-117, -245.56) * mm});
            skLineSegment(sketch, "E5708", {"start": v(-117, -245.56) * mm, "end": v(-117.38, -246.19) * mm});
            skLineSegment(sketch, "E5709", {"start": v(-117.38, -246.19) * mm, "end": v(-117.77, -246.78) * mm});
            skLineSegment(sketch, "E5710", {"start": v(-117.77, -246.78) * mm, "end": v(-118.16, -247.36) * mm});
            skLineSegment(sketch, "E5711", {"start": v(-118.16, -247.36) * mm, "end": v(-118.55, -247.9) * mm});
            skLineSegment(sketch, "E5712", {"start": v(-118.55, -247.9) * mm, "end": v(-118.95, -248.42) * mm});
            skLineSegment(sketch, "E5713", {"start": v(-118.95, -248.42) * mm, "end": v(-119.35, -248.92) * mm});
            skLineSegment(sketch, "E5714", {"start": v(-119.35, -248.92) * mm, "end": v(-119.76, -249.39) * mm});
            skLineSegment(sketch, "E5715", {"start": v(-119.76, -249.39) * mm, "end": v(-120.17, -249.83) * mm});
            skLineSegment(sketch, "E5716", {"start": v(-120.17, -249.83) * mm, "end": v(-120.6, -250.26) * mm});
            skLineSegment(sketch, "E5717", {"start": v(-120.6, -250.26) * mm, "end": v(-121.02, -250.67) * mm});
            skLineSegment(sketch, "E5718", {"start": v(-121.02, -250.67) * mm, "end": v(-121.45, -251.05) * mm});
            skLineSegment(sketch, "E5719", {"start": v(-121.45, -251.05) * mm, "end": v(-121.9, -251.42) * mm});
            skLineSegment(sketch, "E5720", {"start": v(-121.9, -251.42) * mm, "end": v(-122.34, -251.76) * mm});
            skLineSegment(sketch, "E5721", {"start": v(-122.34, -251.76) * mm, "end": v(-122.8, -252.08) * mm});
            skLineSegment(sketch, "E5722", {"start": v(-122.8, -252.08) * mm, "end": v(-123.26, -252.39) * mm});
            skLineSegment(sketch, "E5723", {"start": v(-123.26, -252.39) * mm, "end": v(-123.73, -252.67) * mm});
            skLineSegment(sketch, "E5724", {"start": v(-123.73, -252.67) * mm, "end": v(-124.2, -252.93) * mm});
            skLineSegment(sketch, "E5725", {"start": v(-124.2, -252.93) * mm, "end": v(-124.7, -253.17) * mm});
            skLineSegment(sketch, "E5726", {"start": v(-124.7, -253.17) * mm, "end": v(-125.18, -253.4) * mm});
            skLineSegment(sketch, "E5727", {"start": v(-125.18, -253.4) * mm, "end": v(-125.68, -253.6) * mm});
            skLineSegment(sketch, "E5728", {"start": v(-125.68, -253.6) * mm, "end": v(-126.19, -253.77) * mm});
            skLineSegment(sketch, "E5729", {"start": v(-126.19, -253.77) * mm, "end": v(-126.7, -253.93) * mm});
            skLineSegment(sketch, "E5730", {"start": v(-126.7, -253.93) * mm, "end": v(-127.22, -254.07) * mm});
            skSolve(sketch);
        }
        {
            var Q0;
            Q0 = qSketchRegion(id + "F0", true);
            extrude(context, id + "F1", {"entities" : qUnion([Q0]), "depth" : 3.17 * mm});
        }
    });
